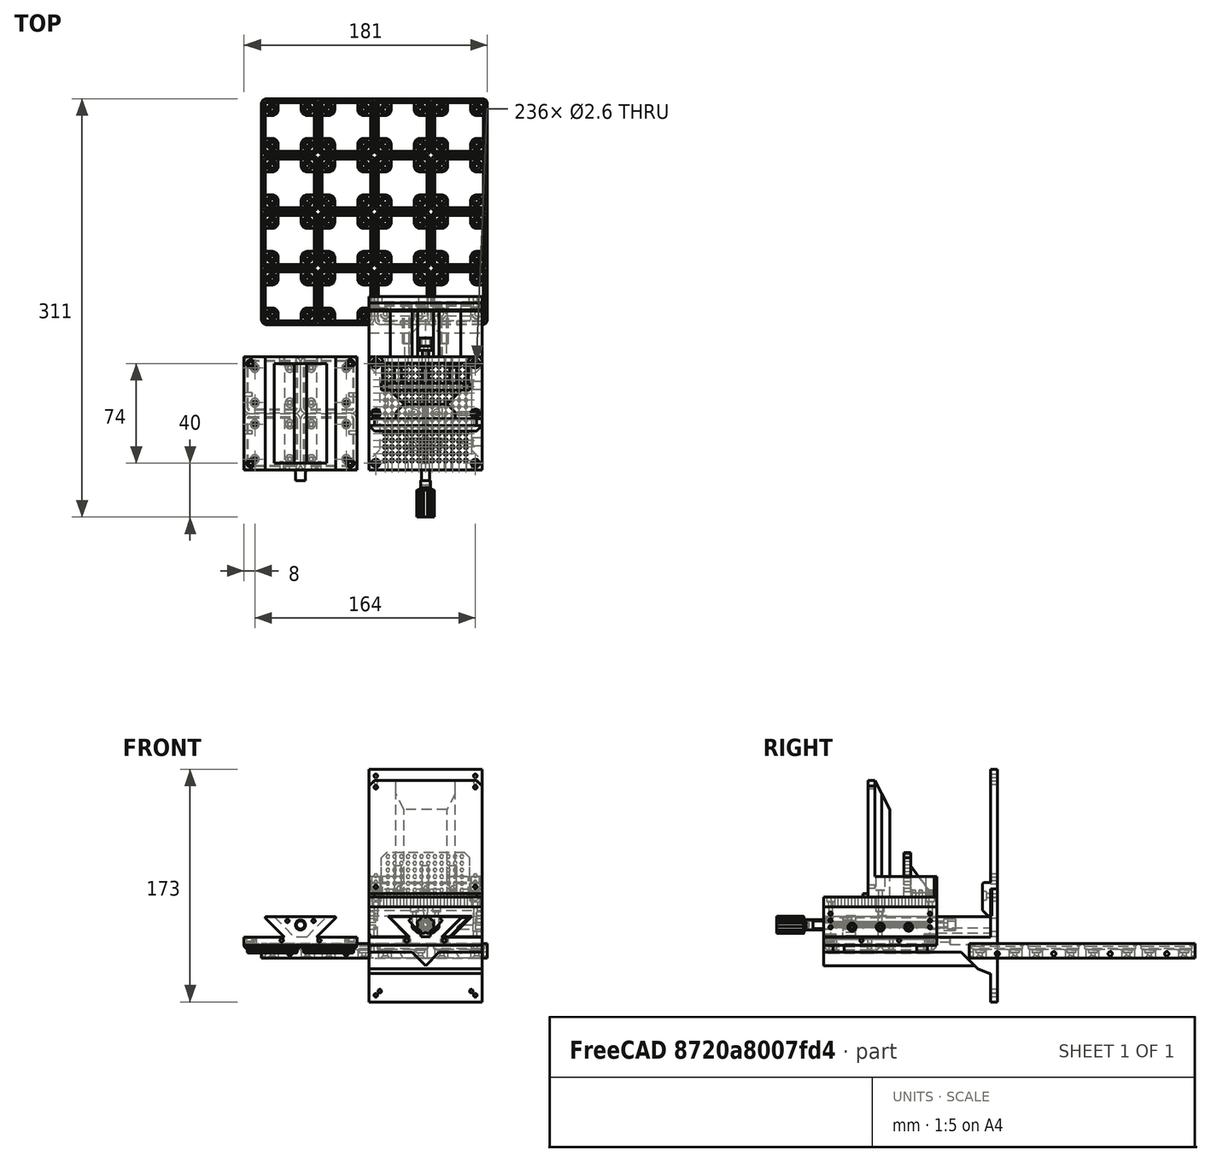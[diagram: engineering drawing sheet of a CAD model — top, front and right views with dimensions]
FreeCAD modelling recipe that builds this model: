
FCSTD DOCUMENT  (FreeCAD 1.0R39109 (Git))
Label: Linear Stage Z Version
License: All rights reserved
LicenseURL: https://en.wikipedia.org/wiki/All_rights_reserved
objects: Sketcher::SketchObject×94, PartDesign::Pocket×53, PartDesign::Pad×46, PartDesign::Chamfer×30, PartDesign::Plane×17, PartDesign::ShapeBinder×15, PartDesign::Body×15, PartDesign::Fillet×6, PartDesign::SubShapeBinder×5, PartDesign::Hole×3, PartDesign::FeatureBase×3, PartDesign::LinearPattern×2, PartDesign::Point×1, Part::Part2DObjectPython×1, Part::Helix×1, PartDesign::AdditivePipe×1, Part::FeaturePython×1, App::VarSet×1, PartDesign::FeaturePython×1
note: 673 computed .brp shape members not serialized (recipe doc carries the construction recipe); baked Part::Feature solids carry a one-line shape summary decoded from their .brp

FEATURE [Sketcher::SketchObject] Sketch
  ArcFitTolerance = 1e-06
  AttachmentSupport = -> [XZ_Plane]
  FullyConstrained = true
  MakeInternals = false
  MapMode = 5
  Placement = pos=(0,0,0) rot=(1,0,0;1.5708rad)
  sketch-geometry (8):
    g0: LineSegment StartX=0 StartY=0 StartZ=0 EndX=84 EndY=0 EndZ=0
    g1: LineSegment StartX=0 StartY=0 StartZ=0 EndX=0 EndY=5 EndZ=0
    g2: LineSegment StartX=84 StartY=0 StartZ=0 EndX=84 EndY=5 EndZ=0
    g3: LineSegment StartX=0 StartY=5 StartZ=0 EndX=30 EndY=5 EndZ=0
    g4: LineSegment StartX=84 StartY=5 StartZ=0 EndX=54 EndY=5 EndZ=0
    g5: LineSegment StartX=30 StartY=5 StartZ=0 EndX=15 EndY=20 EndZ=0
    g6: LineSegment StartX=54 StartY=5 StartZ=0 EndX=69 EndY=20 EndZ=0
    g7: LineSegment StartX=15 StartY=20 StartZ=0 EndX=69 EndY=20 EndZ=0
  constraints (24):
    c: Distance(g0) = 84
    c: Distance(g1) = 5
    c: Coincident(g1,g0)
    c: PointOnObject(g1,g-2)
    c: Vertical(g1)
    c: Distance(g2) = 5
    c: Vertical(g2)
    c: Tangent(g0,g-1)
    c: PointOnObject(g2,g0)
    c: PointOnObject(g0,g2)
    c: Coincident(g3,g1)
    c: Horizontal(g3)
    c: Coincident(g4,g2)
    c: Horizontal(g4)
    c: DistanceX(g3,g3) = 30
    c: DistanceX(g4,g4) = 30
    c: Angle(g-1,g5) = 2.35619
    c: Coincident(g5,g3)
    c: Angle(g-1,g6) = 0.785398
    c: Coincident(g6,g4)
    c: DistanceY(g-1,g5) = 20
    c: DistanceY(g-1,g6) = 20
    c: Coincident(g7,g5)
    c: Coincident(g7,g6)
FEATURE [PartDesign::Pad] Pad
  Direction = (0,-1,2e-16)
  Length = 5
  Length2 = 10
  Placement = pos=(0,0,0) rot=(1,0,0;1.5708rad)
  Profile = -> Sketch
  ReferenceAxis = -> Sketch [N_Axis]
  Refine = true
  Suppressed = false
  Type = 0
FEATURE [Sketcher::SketchObject] Sketch001
  ArcFitTolerance = 1e-06
  AttachmentSupport = -> [Pad]
  ExternalGeometry = -> [Pad]
  FullyConstrained = true
  MakeInternals = false
  MapMode = 5
  Placement = pos=(0,-5,0) rot=(1,0,0;1.5708rad)
  sketch-geometry (14):
    g0: LineSegment StartX=15 StartY=20 StartZ=0 EndX=22.5 EndY=20 EndZ=0
    g1: LineSegment [constr] StartX=30 StartY=5 StartZ=0 EndX=37.5 EndY=5 EndZ=0
    g2: LineSegment StartX=22.5 StartY=20 StartZ=0 EndX=37.5 EndY=5 EndZ=0
    g3: LineSegment StartX=69 StartY=20 StartZ=0 EndX=61.5 EndY=20 EndZ=0
    g4: LineSegment [constr] StartX=54 StartY=5 StartZ=0 EndX=46.5 EndY=5 EndZ=0
    g5: LineSegment StartX=46.5 StartY=5 StartZ=0 EndX=61.5 EndY=20 EndZ=0
    g6: LineSegment StartX=46.5 StartY=5 StartZ=0 EndX=37.5 EndY=5 EndZ=0
    g7: LineSegment StartX=15 StartY=20 StartZ=0 EndX=30 EndY=5 EndZ=0
    g8: LineSegment StartX=30 StartY=5 StartZ=0 EndX=0 EndY=5 EndZ=0
    g9: LineSegment StartX=0 StartY=5 StartZ=0 EndX=0 EndY=0 EndZ=0
    g10: LineSegment StartX=0 StartY=0 StartZ=0 EndX=84 EndY=0 EndZ=0
    g11: LineSegment StartX=84 StartY=0 StartZ=0 EndX=84 EndY=5 EndZ=0
    g12: LineSegment StartX=84 StartY=5 StartZ=0 EndX=54 EndY=5 EndZ=0
    g13: LineSegment StartX=54 StartY=5 StartZ=0 EndX=69 EndY=20 EndZ=0
  constraints (32):
    c: Distance(g0) = 7.5
    c: Coincident(g0,g-4)
    c: PointOnObject(g0,g-3)
    c: Distance(g1) = 7.5
    c: Coincident(g1,g-5)
    c: Horizontal(g1)
    c: Coincident(g2,g0)
    c: Coincident(g2,g1)
    c: Distance(g3) = 7.5
    c: Coincident(g3,g-3)
    c: PointOnObject(g3,g-3)
    c: Distance(g4) = 7.5
    c: Coincident(g4,g-6)
    c: Horizontal(g4)
    c: Coincident(g5,g4)
    c: Coincident(g5,g3)
    c: Coincident(g6,g4)
    c: Coincident(g6,g1)
    c: Coincident(g7,g0)
    c: Coincident(g7,g1)
    c: Coincident(g8,g1)
    c: Coincident(g8,g-8)
    c: Coincident(g9,g8)
    c: Coincident(g9,g-1)
    c: Coincident(g10,g9)
    c: Coincident(g10,g-9)
    c: Coincident(g11,g10)
    c: Coincident(g11,g-7)
    c: Coincident(g12,g11)
    c: Coincident(g12,g4)
    c: Coincident(g13,g4)
    c: Coincident(g13,g3)
FEATURE [PartDesign::Pad] Pad001
  BaseFeature = -> Pad
  Direction = (0,-1,2e-16)
  Length = 74
  Length2 = 10
  Placement = pos=(0,0,0) rot=(1,0,0;1.5708rad)
  Profile = -> Sketch001
  ReferenceAxis = -> Sketch001 [N_Axis]
  Refine = true
  Suppressed = false
  Type = 0
FEATURE [Sketcher::SketchObject] Sketch002
  ArcFitTolerance = 1e-06
  AttachmentSupport = -> [Pad001]
  ExternalGeometry = -> [Pad001]
  FullyConstrained = true
  MakeInternals = false
  MapMode = 5
  Placement = pos=(0,-5,0) rot=(1,0,0;1.5708rad)
  sketch-geometry (2):
    g0: LineSegment [constr] StartX=42 StartY=20 StartZ=0 EndX=42 EndY=14 EndZ=0
    g1: Circle CenterX=42 CenterY=14 CenterZ=0 NormalX=0 NormalY=0 NormalZ=1 AngleXU=0 Radius=3
  constraints (5):
    c: Distance(g0) = 6
    c: Symmetric(g-3,g-3,g0)
    c: Vertical(g0)
    c: Diameter(g1) = 6
    c: Coincident(g1,g0)
FEATURE [PartDesign::Hole] Hole
  BaseFeature = -> Pad001
  CustomThreadClearance = 0
  Depth = 25
  DepthType = 0
  Diameter = 6
  DrillForDepth = false
  DrillPoint = 1
  DrillPointAngle = 118
  HoleCutCountersinkAngle = 90
  HoleCutCustomValues = false
  HoleCutDepth = 0
  HoleCutDiameter = 6.1
  HoleCutType = 0
  ModelThread = false
  Placement = pos=(0,0,0) rot=(1,0,0;1.5708rad)
  Profile = -> Sketch002
  Refine = true
  Suppressed = false
  Tapered = false
  TaperedAngle = 90
  ThreadClass = 0
  ThreadDepth = 25
  ThreadDepthType = 0
  ThreadDirection = 0
  ThreadFit = 0
  ThreadSize = 0
  ThreadType = 0
  Threaded = false
  UseCustomThreadClearance = false
FEATURE [Sketcher::SketchObject] Sketch003
  ArcFitTolerance = 1e-06
  AttachmentSupport = -> [Hole]
  ExternalGeometry = -> [Hole]
  FullyConstrained = true
  MakeInternals = false
  MapMode = 5
  Placement = pos=(0,-79,1.74e-14) rot=(1,0,0;1.5708rad)
  sketch-geometry (16):
    g0: LineSegment StartX=15 StartY=20 StartZ=0 EndX=69 EndY=20 EndZ=0
    g1: LineSegment StartX=15 StartY=20 StartZ=0 EndX=30 EndY=5 EndZ=0
    g2: LineSegment StartX=30 StartY=5 StartZ=0 EndX=0 EndY=5 EndZ=0
    g3: LineSegment StartX=0 StartY=5 StartZ=0 EndX=0 EndY=0 EndZ=0
    g4: LineSegment StartX=0 StartY=0 StartZ=0 EndX=84 EndY=0 EndZ=0
    g5: LineSegment StartX=84 StartY=0 StartZ=0 EndX=84 EndY=5 EndZ=0
    g6: LineSegment StartX=84 StartY=5 StartZ=0 EndX=54 EndY=5 EndZ=0
    g7: LineSegment StartX=54 StartY=5 StartZ=0 EndX=69 EndY=20 EndZ=0
    g8: LineSegment [constr] StartX=42 StartY=20 StartZ=0 EndX=42 EndY=14 EndZ=0
    g9: Circle CenterX=42 CenterY=14 CenterZ=0 NormalX=0 NormalY=0 NormalZ=1 AngleXU=0 Radius=3
    g10: LineSegment [constr] StartX=42 StartY=14 StartZ=0 EndX=22.5 EndY=20 EndZ=0
    g11: LineSegment [constr] StartX=42 StartY=14 StartZ=0 EndX=61.5 EndY=20 EndZ=0
    g12: GeomPoint [constr] X=32.25 Y=17 Z=0
    g13: GeomPoint [constr] X=51.75 Y=17 Z=0
    g14: Circle CenterX=32.25 CenterY=17 CenterZ=0 NormalX=0 NormalY=0 NormalZ=1 AngleXU=0 Radius=1.25
    g15: Circle CenterX=51.75 CenterY=17 CenterZ=0 NormalX=0 NormalY=0 NormalZ=1 AngleXU=0 Radius=1.25
  constraints (31):
    c: Coincident(g0,g-4)
    c: Coincident(g0,g-11)
    c: Coincident(g1,g0)
    c: Coincident(g1,g-5)
    c: Coincident(g2,g1)
    c: Coincident(g2,g-6)
    c: Coincident(g3,g2)
    c: Coincident(g3,g-1)
    c: Coincident(g4,g3)
    c: Coincident(g4,g-8)
    c: Coincident(g5,g4)
    c: Coincident(g5,g-9)
    c: Coincident(g6,g5)
    c: Coincident(g6,g-10)
    c: Coincident(g7,g6)
    c: Coincident(g7,g0)
    c: Distance(g8) = 6
    c: Symmetric(g0,g0,g8)
    c: Vertical(g8)
    c: Diameter(g9) = 6
    c: Coincident(g9,g8)
    c: Coincident(g10,g8)
    c: Coincident(g10,g-14)
    c: Coincident(g11,g8)
    c: Coincident(g11,g-12)
    c: Symmetric(g10,g10,g12)
    c: Symmetric(g11,g11,g13)
    c: Diameter(g14) = 2.5
    c: Coincident(g14,g12)
    c: Diameter(g15) = 2.5
    c: Coincident(g15,g13)
FEATURE [PartDesign::Pad] Pad002
  BaseFeature = -> Hole
  Direction = (0,-1,2e-16)
  Length = 5
  Length2 = 10
  Placement = pos=(0,0,0) rot=(1,0,0;1.5708rad)
  Profile = -> Sketch003
  ReferenceAxis = -> Sketch003 [N_Axis]
  Refine = true
  Suppressed = false
  Type = 0
FEATURE [PartDesign::Plane] DatumPlane
  AttachmentSupport = -> [Pad002]
  Length = 131.586
  MapMode = 5
  Placement = pos=(0,0,-5e-16) rot=(1,0,0;3.14159rad)
  ResizeMode = 0
  Width = 139.586
FEATURE [Sketcher::SketchObject] Sketch004
  ArcFitTolerance = 1e-06
  AttachmentSupport = -> [Pad002]
  ExternalGeometry = -> [Pad002]
  FullyConstrained = true
  MakeInternals = false
  MapMode = 5
  Placement = pos=(0,0,-5e-16) rot=(1,0,0;3.14159rad)
  sketch-geometry (23):
    g0: LineSegment [constr] StartX=0 StartY=84 StartZ=0 EndX=84 EndY=0 EndZ=0
    g1: LineSegment [constr] StartX=41.75 StartY=41.75 StartZ=0 EndX=42.25 EndY=41.75 EndZ=0
    g2: LineSegment [constr] StartX=42.25 StartY=41.75 StartZ=0 EndX=42.25 EndY=42.25 EndZ=0
    g3: LineSegment [constr] StartX=42.25 StartY=42.25 StartZ=0 EndX=41.75 EndY=42.25 EndZ=0
    g4: LineSegment [constr] StartX=41.75 StartY=42.25 StartZ=0 EndX=41.75 EndY=41.75 EndZ=0
    g5: GeomPoint [constr] X=42 Y=42 Z=0
    g6: LineSegment [constr] StartX=0 StartY=0 StartZ=0 EndX=84 EndY=84 EndZ=0
    g7: LineSegment StartX=42.25 StartY=42.25 StartZ=0 EndX=83.75 EndY=42.25 EndZ=0
    g8: LineSegment StartX=83.75 StartY=42.25 StartZ=0 EndX=83.75 EndY=83.75 EndZ=0
    g9: LineSegment StartX=83.75 StartY=83.75 StartZ=0 EndX=42.25 EndY=83.75 EndZ=0
    g10: LineSegment StartX=42.25 StartY=83.75 StartZ=0 EndX=42.25 EndY=42.25 EndZ=0
    g11: LineSegment StartX=41.75 StartY=42.25 StartZ=0 EndX=41.75 EndY=83.75 EndZ=0
    g12: LineSegment StartX=41.75 StartY=83.75 StartZ=0 EndX=0.25 EndY=83.75 EndZ=0
    g13: LineSegment StartX=0.25 StartY=83.75 StartZ=0 EndX=0.25 EndY=42.25 EndZ=0
    g14: LineSegment StartX=0.25 StartY=42.25 StartZ=0 EndX=41.75 EndY=42.25 EndZ=0
    g15: LineSegment StartX=42.25 StartY=41.75 StartZ=0 EndX=42.25 EndY=0.25 EndZ=0
    g16: LineSegment StartX=42.25 StartY=0.25 StartZ=0 EndX=83.75 EndY=0.25 EndZ=0
    g17: LineSegment StartX=83.75 StartY=0.25 StartZ=0 EndX=83.75 EndY=41.75 EndZ=0
    g18: LineSegment StartX=83.75 StartY=41.75 StartZ=0 EndX=42.25 EndY=41.75 EndZ=0
    g19: LineSegment StartX=41.75 StartY=41.75 StartZ=0 EndX=0.25 EndY=41.75 EndZ=0
    g20: LineSegment StartX=0.25 StartY=41.75 StartZ=0 EndX=0.25 EndY=0.25 EndZ=0
    g21: LineSegment StartX=0.25 StartY=0.25 StartZ=0 EndX=41.75 EndY=0.25 EndZ=0
    g22: LineSegment StartX=41.75 StartY=0.25 StartZ=0 EndX=41.75 EndY=41.75 EndZ=0
  constraints (61):
    c: Coincident(g0,g-6)
    c: Coincident(g0,g-5)
    c: Coincident(g1,g2)
    c: Coincident(g2,g3)
    c: Coincident(g3,g4)
    c: Coincident(g4,g1)
    c: Horizontal(g1)
    c: Horizontal(g3)
    c: Vertical(g2)
    c: Vertical(g4)
    c: Symmetric(g3,g1,g5)
    c: Distance(g2,g4) = 0.5
    c: Distance(g1,g3) = 0.5
    c: PointOnObject(g5,g0)
    c: Coincident(g6,g-1)
    c: Coincident(g6,g-4)
    c: PointOnObject(g5,g6)
    c: Coincident(g7,g8)
    c: Coincident(g8,g9)
    c: Coincident(g9,g10)
    c: Coincident(g10,g7)
    c: Horizontal(g7)
    c: Horizontal(g9)
    c: Vertical(g8)
    c: Vertical(g10)
    c: Distance(g8,g10) = 41.5
    c: Coincident(g7,g2)
    c: PointOnObject(g8,g6)
    c: Coincident(g11,g12)
    c: Coincident(g12,g13)
    c: Coincident(g13,g14)
    c: Coincident(g14,g11)
    c: Vertical(g11)
    c: Vertical(g13)
    c: Horizontal(g12)
    c: Horizontal(g14)
    c: Distance(g11,g13) = 41.5
    c: Coincident(g11,g3)
    c: PointOnObject(g12,g0)
    c: Coincident(g15,g16)
    c: Coincident(g16,g17)
    c: Coincident(g17,g18)
    c: Coincident(g18,g15)
    c: Vertical(g15)
    c: Vertical(g17)
    c: Horizontal(g16)
    c: Horizontal(g18)
    c: Distance(g15,g17) = 41.5
    c: Coincident(g15,g1)
    c: PointOnObject(g16,g0)
    c: Coincident(g19,g20)
    c: Coincident(g20,g21)
    c: Coincident(g21,g22)
    c: Coincident(g22,g19)
    c: Horizontal(g19)
    c: Horizontal(g21)
    c: Vertical(g20)
    c: Vertical(g22)
    c: Distance(g20,g22) = 41.5
    c: Coincident(g19,g1)
    c: PointOnObject(g20,g6)
FEATURE [PartDesign::Pad] Pad003
  BaseFeature = -> Pad002
  Direction = (0,0,-1)
  Length = 1
  Length2 = 10
  Placement = pos=(0,0,0) rot=(1,0,0;1.5708rad)
  Profile = -> Sketch004
  ReferenceAxis = -> Sketch004 [N_Axis]
  Refine = true
  Suppressed = false
  Type = 0
FEATURE [PartDesign::Plane] DatumPlane001
  AttachmentSupport = -> [Pad003]
  Length = 131.586
  MapMode = 5
  Placement = pos=(0,0,-1) rot=(1,0,0;3.14159rad)
  ResizeMode = 0
  Width = 139.586
FEATURE [Sketcher::SketchObject] Sketch005
  ArcFitTolerance = 1e-06
  AttachmentSupport = -> [DatumPlane001]
  ExternalGeometry = -> [Pad003]
  FullyConstrained = true
  MakeInternals = false
  MapMode = 5
  Placement = pos=(0,0,-1) rot=(1,0,0;3.14159rad)
  sketch-geometry (28):
    g0: LineSegment [constr] StartX=41.75 StartY=42.25 StartZ=0 EndX=0.25 EndY=83.75 EndZ=0
    g1: GeomPoint [constr] X=21 Y=63 Z=0
    g2: LineSegment StartX=2.4 StartY=44.4 StartZ=0 EndX=39.6 EndY=44.4 EndZ=0
    g3: LineSegment StartX=39.6 StartY=44.4 StartZ=0 EndX=39.6 EndY=81.6 EndZ=0
    g4: LineSegment StartX=39.6 StartY=81.6 StartZ=0 EndX=2.4 EndY=81.6 EndZ=0
    g5: LineSegment StartX=2.4 StartY=81.6 StartZ=0 EndX=2.4 EndY=44.4 EndZ=0
    g6: GeomPoint [constr] X=21 Y=63 Z=0
    g7: LineSegment [constr] StartX=42.25 StartY=83.75 StartZ=0 EndX=83.75 EndY=42.25 EndZ=0
    g8: LineSegment [constr] StartX=83.75 StartY=41.75 StartZ=0 EndX=42.25 EndY=0.25 EndZ=0
    g9: LineSegment [constr] StartX=41.75 StartY=0.25 StartZ=0 EndX=0.25 EndY=41.75 EndZ=0
    g10: GeomPoint [constr] X=63 Y=63 Z=0
    g11: GeomPoint [constr] X=63 Y=21 Z=0
    g12: GeomPoint [constr] X=21 Y=21 Z=0
    g13: LineSegment StartX=44.4 StartY=44.4 StartZ=0 EndX=81.6 EndY=44.4 EndZ=0
    g14: LineSegment StartX=81.6 StartY=44.4 StartZ=0 EndX=81.6 EndY=81.6 EndZ=0
    g15: LineSegment StartX=81.6 StartY=81.6 StartZ=0 EndX=44.4 EndY=81.6 EndZ=0
    g16: LineSegment StartX=44.4 StartY=81.6 StartZ=0 EndX=44.4 EndY=44.4 EndZ=0
    g17: GeomPoint [constr] X=63 Y=63 Z=0
    g18: LineSegment StartX=44.4 StartY=2.4 StartZ=0 EndX=81.6 EndY=2.4 EndZ=0
    g19: LineSegment StartX=81.6 StartY=2.4 StartZ=0 EndX=81.6 EndY=39.6 EndZ=0
    g20: LineSegment StartX=81.6 StartY=39.6 StartZ=0 EndX=44.4 EndY=39.6 EndZ=0
    g21: LineSegment StartX=44.4 StartY=39.6 StartZ=0 EndX=44.4 EndY=2.4 EndZ=0
    g22: GeomPoint [constr] X=63 Y=21 Z=0
    g23: LineSegment StartX=2.4 StartY=2.4 StartZ=0 EndX=39.6 EndY=2.4 EndZ=0
    g24: LineSegment StartX=39.6 StartY=2.4 StartZ=0 EndX=39.6 EndY=39.6 EndZ=0
    g25: LineSegment StartX=39.6 StartY=39.6 StartZ=0 EndX=2.4 EndY=39.6 EndZ=0
    g26: LineSegment StartX=2.4 StartY=39.6 StartZ=0 EndX=2.4 EndY=2.4 EndZ=0
    g27: GeomPoint [constr] X=21 Y=21 Z=0
  constraints (60):
    c: Coincident(g0,g-14)
    c: Coincident(g0,g-16)
    c: Symmetric(g0,g0,g1)
    c: Coincident(g2,g3)
    c: Coincident(g3,g4)
    c: Coincident(g4,g5)
    c: Coincident(g5,g2)
    c: Horizontal(g2)
    c: Horizontal(g4)
    c: Vertical(g3)
    c: Vertical(g5)
    c: Symmetric(g4,g2,g6)
    c: Distance(g3,g5) = 37.2
    c: Distance(g2,g4) = 37.2
    c: Coincident(g6,g1)
    c: Coincident(g7,g-18)
    c: Coincident(g7,g-17)
    c: Coincident(g8,g-9)
    c: Coincident(g8,g-10)
    c: Coincident(g9,g-4)
    c: Coincident(g9,g-6)
    c: Symmetric(g7,g7,g10)
    c: Symmetric(g8,g8,g11)
    c: Symmetric(g9,g9,g12)
    c: Coincident(g13,g14)
    c: Coincident(g14,g15)
    c: Coincident(g15,g16)
    c: Coincident(g16,g13)
    c: Horizontal(g13)
    c: Horizontal(g15)
    c: Vertical(g14)
    c: Vertical(g16)
    c: Symmetric(g15,g13,g17)
    c: Distance(g14,g16) = 37.2
    c: Distance(g13,g15) = 37.2
    c: Coincident(g17,g10)
    c: Coincident(g18,g19)
    c: Coincident(g19,g20)
    c: Coincident(g20,g21)
    c: Coincident(g21,g18)
    c: Horizontal(g18)
    c: Horizontal(g20)
    c: Vertical(g19)
    c: Vertical(g21)
    c: Symmetric(g20,g18,g22)
    c: Distance(g19,g21) = 37.2
    c: Coincident(g22,g11)
    c: PointOnObject(g19,g8)
    c: Coincident(g23,g24)
    c: Coincident(g24,g25)
    c: Coincident(g25,g26)
    c: Coincident(g26,g23)
    c: Horizontal(g23)
    c: Horizontal(g25)
    c: Vertical(g24)
    c: Vertical(g26)
    c: Symmetric(g25,g23,g27)
    c: Distance(g24,g26) = 37.2
    c: Distance(g23,g25) = 37.2
    c: Coincident(g27,g12)
FEATURE [PartDesign::Pad] Pad004
  BaseFeature = -> Pad003
  Direction = (0,0,-1)
  Length = 3.5
  Length2 = 10
  Placement = pos=(0,0,0) rot=(1,0,0;1.5708rad)
  Profile = -> Sketch005
  ReferenceAxis = -> Sketch005 [N_Axis]
  Refine = true
  Suppressed = false
  Type = 0
FEATURE [PartDesign::Chamfer] Chamfer
  Angle = 45
  Base = -> Pad004 [Edge114]
  BaseFeature = -> Pad004
  ChamferType = 0
  FlipDirection = false
  Placement = pos=(0,0,0) rot=(1,0,0;1.5708rad)
  Refine = true
  Size = 7
  Size2 = 1
  SupportTransform = false
  Suppressed = false
  UseAllEdges = false
FEATURE [PartDesign::Chamfer] Chamfer001
  Angle = 45
  Base = -> Chamfer [Edge23]
  BaseFeature = -> Chamfer
  ChamferType = 0
  FlipDirection = false
  Placement = pos=(0,0,0) rot=(1,0,0;1.5708rad)
  Refine = true
  Size = 7
  Size2 = 1
  SupportTransform = false
  Suppressed = false
  UseAllEdges = false
FEATURE [PartDesign::Chamfer] Chamfer002
  Angle = 45
  Base = -> Chamfer001 [Edge136,Edge28,Edge143,Edge22,Edge135,Edge128,Edge144,Edge148,Edge140,Edge127,Edge132,Edge138,Edge26,Edge130]
  BaseFeature = -> Chamfer001
  ChamferType = 0
  FlipDirection = false
  Placement = pos=(0,0,0) rot=(1,0,0;1.5708rad)
  Refine = true
  Size = 7
  Size2 = 1
  SupportTransform = false
  Suppressed = false
  UseAllEdges = false
FEATURE [PartDesign::Chamfer] Chamfer003
  Angle = 45
  Base = -> Chamfer002 [Edge77,Edge79,Edge93,Edge81,Edge95,Edge38,Edge76,Edge32,Edge92,Edge84,Edge97,Edge85,Edge87,Edge89,Edge35]
  BaseFeature = -> Chamfer002
  ChamferType = 0
  FlipDirection = false
  Placement = pos=(0,0,0) rot=(1,0,0;1.5708rad)
  Refine = true
  Size = 8
  Size2 = 1
  SupportTransform = false
  Suppressed = false
  UseAllEdges = false
FEATURE [PartDesign::Chamfer] Chamfer004
  Angle = 45
  Base = -> Chamfer003 [Edge231]
  BaseFeature = -> Chamfer003
  ChamferType = 0
  FlipDirection = false
  Placement = pos=(0,0,0) rot=(1,0,0;1.5708rad)
  Refine = true
  Size = 7
  Size2 = 1
  SupportTransform = false
  Suppressed = false
  UseAllEdges = false
FEATURE [PartDesign::Chamfer] Chamfer005
  Angle = 45
  Base = -> Chamfer004 [Edge1,Edge2,Edge4,Edge6,Edge8,Edge7,Edge5,Edge3]
  BaseFeature = -> Chamfer004
  ChamferType = 0
  FlipDirection = false
  Placement = pos=(0,0,0) rot=(1,0,0;1.5708rad)
  Refine = true
  Size = 2
  Size2 = 1
  SupportTransform = false
  Suppressed = false
  UseAllEdges = false
FEATURE [PartDesign::Chamfer] Chamfer006
  Angle = 45
  Base = -> Chamfer005 [Edge60,Edge64,Edge62,Edge58,Edge55,Edge50,Edge52,Edge56]
  BaseFeature = -> Chamfer005
  ChamferType = 0
  FlipDirection = false
  Placement = pos=(0,0,0) rot=(1,0,0;1.5708rad)
  Refine = true
  Size = 0.8
  Size2 = 1
  SupportTransform = false
  Suppressed = false
  UseAllEdges = false
FEATURE [PartDesign::Chamfer] Chamfer007
  Angle = 45
  Base = -> Chamfer006 [Edge207,Edge208,Edge205,Edge206,Edge204,Edge202,Edge203,Edge201]
  BaseFeature = -> Chamfer006
  ChamferType = 0
  FlipDirection = false
  Placement = pos=(0,0,0) rot=(1,0,0;1.5708rad)
  Refine = true
  Size = 2
  Size2 = 1
  SupportTransform = false
  Suppressed = false
  UseAllEdges = false
FEATURE [PartDesign::Chamfer] Chamfer008
  Angle = 45
  Base = -> Chamfer007 [Edge63,Edge64,Edge60,Edge57,Edge52,Edge50,Edge55,Edge59]
  BaseFeature = -> Chamfer007
  ChamferType = 0
  FlipDirection = false
  Placement = pos=(0,0,0) rot=(1,0,0;1.5708rad)
  Refine = true
  Size = 0.8
  Size2 = 1
  SupportTransform = false
  Suppressed = false
  UseAllEdges = false
FEATURE [PartDesign::Chamfer] Chamfer009
  Angle = 45
  Base = -> Chamfer008 [Edge179,Edge177,Edge178,Edge181,Edge180,Edge182,Edge184,Edge183]
  BaseFeature = -> Chamfer008
  ChamferType = 0
  FlipDirection = false
  Placement = pos=(0,0,0) rot=(1,0,0;1.5708rad)
  Refine = true
  Size = 2
  Size2 = 1
  SupportTransform = false
  Suppressed = false
  UseAllEdges = false
FEATURE [PartDesign::Chamfer] Chamfer010
  Angle = 45
  Base = -> Chamfer009 [Edge55,Edge58,Edge62,Edge64,Edge61,Edge56,Edge53,Edge50]
  BaseFeature = -> Chamfer009
  ChamferType = 0
  FlipDirection = false
  Placement = pos=(0,0,0) rot=(1,0,0;1.5708rad)
  Refine = true
  Size = 0.8
  Size2 = 1
  SupportTransform = false
  Suppressed = false
  UseAllEdges = false
FEATURE [PartDesign::Chamfer] Chamfer011
  Angle = 45
  Base = -> Chamfer010 [Edge203,Edge205,Edge201,Edge202,Edge204,Edge206,Edge208,Edge207]
  BaseFeature = -> Chamfer010
  ChamferType = 0
  FlipDirection = false
  Placement = pos=(0,0,0) rot=(1,0,0;1.5708rad)
  Refine = true
  Size = 2
  Size2 = 1
  SupportTransform = false
  Suppressed = false
  UseAllEdges = false
FEATURE [PartDesign::Chamfer] Chamfer012
  Angle = 45
  Base = -> Chamfer011 [Edge62,Edge59,Edge54,Edge50,Edge53,Edge56,Edge61,Edge64]
  BaseFeature = -> Chamfer011
  ChamferType = 0
  FlipDirection = false
  Placement = pos=(0,0,0) rot=(1,0,0;1.5708rad)
  Refine = true
  Size = 0.8
  Size2 = 1
  SupportTransform = false
  Suppressed = false
  UseAllEdges = false
FEATURE [PartDesign::Fillet] Fillet
  Base = -> Chamfer012 [Edge188,Edge187]
  BaseFeature = -> Chamfer012
  Placement = pos=(0,0,0) rot=(1,0,0;1.5708rad)
  Radius = 0.5
  Refine = true
  SupportTransform = false
  Suppressed = false
  UseAllEdges = false
FEATURE [PartDesign::ShapeBinder] ShapeBinder
  Support = -> [Fillet]
  TraceSupport = false
FEATURE [PartDesign::ShapeBinder] CopyFillet
  Placement = pos=(0,-5,2e-15) rot=(0,0,1;0rad)
  TraceSupport = false
FEATURE [PartDesign::Plane] DatumPlane002
  AttachmentSupport = -> [CopyFillet]
  Length = 111.71
  MapMode = 5
  Placement = pos=(0,-84,2e-15) rot=(1,0,0;1.5708rad)
  ResizeMode = 0
  Width = 63.9806
FEATURE [Sketcher::SketchObject] Sketch006
  ArcFitTolerance = 1e-06
  AttachmentSupport = -> [DatumPlane002]
  ExternalGeometry = -> [ShapeBinder]
  FullyConstrained = true
  MakeInternals = false
  MapMode = 5
  Placement = pos=(0,-84,2e-15) rot=(1,0,0;1.5708rad)
  sketch-geometry (16):
    g0: LineSegment [constr] StartX=68.1465 StartY=19.1464 StartZ=0 EndX=69 EndY=20 EndZ=0
    g1: LineSegment [constr] StartX=67.7929 StartY=20 StartZ=0 EndX=69 EndY=20 EndZ=0
    g2: LineSegment [constr] StartX=69 StartY=20 StartZ=0 EndX=69.5 EndY=20 EndZ=0
    g3: LineSegment [constr] StartX=69.5 StartY=20 StartZ=0 EndX=74.5 EndY=20 EndZ=0
    g4: LineSegment [constr] StartX=54 StartY=5 StartZ=0 EndX=54.5 EndY=5 EndZ=0
    g5: LineSegment [constr] StartX=54.5 StartY=5 StartZ=0 EndX=59.5 EndY=5 EndZ=0
    g6: LineSegment [constr] StartX=59.5 StartY=5 StartZ=0 EndX=74.5 EndY=20 EndZ=0
    g7: LineSegment [constr] StartX=54.5 StartY=5 StartZ=0 EndX=69.5 EndY=20 EndZ=0
    g8: LineSegment [constr] StartX=59.5 StartY=5 StartZ=0 EndX=59.8536 EndY=5.35355 EndZ=0
    g9: LineSegment [constr] StartX=54.5 StartY=5 StartZ=0 EndX=54.8536 EndY=5.35355 EndZ=0
    g10: LineSegment [constr] StartX=74.5 StartY=20 StartZ=0 EndX=74.1465 EndY=19.6464 EndZ=0
    g11: LineSegment [constr] StartX=69.5 StartY=20 StartZ=0 EndX=69.1465 EndY=19.6464 EndZ=0
    g12: LineSegment StartX=54.8536 StartY=5.35355 StartZ=0 EndX=59.8536 EndY=5.35355 EndZ=0
    g13: LineSegment StartX=59.8536 StartY=5.35355 StartZ=0 EndX=74.1465 EndY=19.6464 EndZ=0
    g14: LineSegment StartX=74.1465 StartY=19.6464 StartZ=0 EndX=69.1465 EndY=19.6464 EndZ=0
    g15: LineSegment StartX=69.1465 StartY=19.6464 StartZ=0 EndX=54.8536 EndY=5.35355 EndZ=0
  constraints (41):
    c: Coincident(g0,g-3)
    c: Coincident(g1,g-4)
    c: Coincident(g1,g0)
    c: Angle(g-4,g1) = 3.14159
    c: Angle(g-3,g0) = 3.14159
    c: Distance(g2) = 0.5
    c: Coincident(g2,g0)
    c: Horizontal(g2)
    c: Distance(g3) = 5
    c: Coincident(g3,g2)
    c: Horizontal(g3)
    c: Distance(g4) = 0.5
    c: Coincident(g4,g-3)
    c: Horizontal(g4)
    c: Distance(g5) = 5
    c: Coincident(g5,g4)
    c: Horizontal(g5)
    c: Coincident(g6,g5)
    c: Coincident(g6,g3)
    c: Coincident(g7,g4)
    c: Coincident(g7,g2)
    c: Distance(g8) = 0.5
    c: Coincident(g8,g5)
    c: PointOnObject(g8,g6)
    c: Distance(g9) = 0.5
    c: Coincident(g9,g4)
    c: PointOnObject(g9,g7)
    c: Distance(g10) = 0.5
    c: Coincident(g10,g3)
    c: PointOnObject(g10,g6)
    c: Distance(g11) = 0.5
    c: Coincident(g11,g2)
    c: PointOnObject(g11,g7)
    c: Coincident(g12,g9)
    c: Coincident(g12,g8)
    c: Coincident(g13,g8)
    c: Coincident(g13,g10)
    c: Coincident(g14,g10)
    c: Coincident(g14,g11)
    c: Coincident(g15,g11)
    c: Coincident(g15,g9)
FEATURE [PartDesign::Pad] Pad005
  Direction = (0,-1,2e-16)
  Length = 84
  Length2 = 10
  Placement = pos=(0,-84,2e-15) rot=(1,0,0;1.5708rad)
  Profile = -> Sketch006
  ReferenceAxis = -> Sketch006 [N_Axis]
  Refine = true
  Reversed = true
  Suppressed = false
  Type = 0
FEATURE [PartDesign::Plane] DatumPlane003
  AttachmentSupport = -> [Pad005]
  Length = 125.801
  MapMode = 5
  Placement = pos=(27.25,-84,-27.25) rot=(0.92388,0,0.382683;3.14159rad)
  ResizeMode = 0
  Width = 130.341
FEATURE [Sketcher::SketchObject] Sketch007
  ArcFitTolerance = 1e-06
  AttachmentSupport = -> [DatumPlane003]
  ExternalGeometry = -> [Pad005]
  FullyConstrained = true
  MakeInternals = false
  MapMode = 5
  Placement = pos=(27.25,-84,-27.25) rot=(0.92388,0,0.382683;3.14159rad)
  sketch-geometry (8):
    g0: LineSegment [constr] StartX=46.1084 StartY=-42 StartZ=0 EndX=66.3216 EndY=-42 EndZ=0
    g1: LineSegment [constr] StartX=56.215 StartY=-42 StartZ=0 EndX=56.215 EndY=-1.42e-14 EndZ=0
    g2: LineSegment [constr] StartX=56.215 StartY=-42 StartZ=0 EndX=56.215 EndY=-84 EndZ=0
    g3: GeomPoint [constr] X=56.215 Y=-63 Z=0
    g4: GeomPoint [constr] X=56.215 Y=-21 Z=0
    g5: Circle CenterX=56.215 CenterY=-21 CenterZ=0 NormalX=0 NormalY=0 NormalZ=1 AngleXU=0 Radius=1.55
    g6: Circle CenterX=56.215 CenterY=-42 CenterZ=0 NormalX=0 NormalY=0 NormalZ=1 AngleXU=0 Radius=1.55
    g7: Circle CenterX=56.215 CenterY=-63 CenterZ=0 NormalX=0 NormalY=0 NormalZ=1 AngleXU=0 Radius=1.55
  constraints (14):
    c: Symmetric(g-4,g-4,g0)
    c: Symmetric(g-3,g-3,g0)
    c: Symmetric(g0,g0,g1)
    c: Symmetric(g-5,g-5,g1)
    c: Coincident(g2,g1)
    c: Symmetric(g-6,g-6,g2)
    c: Symmetric(g2,g2,g3)
    c: Symmetric(g1,g1,g4)
    c: Diameter(g5) = 3.1
    c: Coincident(g5,g4)
    c: Diameter(g6) = 3.1
    c: Coincident(g6,g1)
    c: Diameter(g7) = 3.1
    c: Coincident(g7,g3)
FEATURE [PartDesign::Pocket] Pocket
  BaseFeature = -> Pad005
  Direction = (-0.707107,0,0.707107)
  Length = 1
  Length2 = 5
  Placement = pos=(0,-84,2e-15) rot=(1,0,0;1.5708rad)
  Profile = -> Sketch007
  ReferenceAxis = -> Sketch007 [N_Axis]
  Refine = true
  Suppressed = false
  Type = 0
FEATURE [PartDesign::Fillet] Fillet001
  Base = -> Pocket [Edge5,Edge10,Edge1,Edge2]
  BaseFeature = -> Pocket
  Placement = pos=(0,-84,2e-15) rot=(1,0,0;1.5708rad)
  Radius = 1
  Refine = true
  SupportTransform = false
  Suppressed = false
  UseAllEdges = false
FEATURE [PartDesign::Fillet] Fillet002
  Base = -> Fillet001 [Edge24,Edge25,Edge23]
  BaseFeature = -> Fillet001
  Placement = pos=(0,-84,2e-15) rot=(1,0,0;1.5708rad)
  Radius = 0.3
  Refine = true
  SupportTransform = false
  Suppressed = false
  UseAllEdges = false
FEATURE [PartDesign::Fillet] Fillet003
  Base = -> Fillet002 [Edge31,Edge37,Edge39]
  BaseFeature = -> Fillet002
  Placement = pos=(0,-84,2e-15) rot=(1,0,0;1.5708rad)
  Radius = 0.3
  Refine = true
  SupportTransform = false
  Suppressed = false
  UseAllEdges = false
FEATURE [PartDesign::Body] Body001  label="Shim"
  AllowCompound = false
  Group = -> [ShapeBinder,DatumPlane002,CopyFillet,Sketch006,Pad005,DatumPlane003,Sketch007,Pocket,Fillet001,Fillet002,Fillet003]
  Origin = -> Origin001
  Tip = -> Fillet003
FEATURE [PartDesign::ShapeBinder] ShapeBinder001
  Support = -> [Fillet]
  TraceSupport = false
FEATURE [PartDesign::ShapeBinder] CopyFillet001
  Placement = pos=(0,-5,2e-15) rot=(0,0,1;0rad)
  TraceSupport = false
FEATURE [PartDesign::Plane] DatumPlane004
  AttachmentSupport = -> [CopyFillet001]
  Length = 124.108
  MapMode = 5
  Placement = pos=(0,-84,2e-15) rot=(1,0,0;1.5708rad)
  ResizeMode = 0
  Width = 67.4619
FEATURE [Sketcher::SketchObject] Sketch008
  ArcFitTolerance = 1e-06
  AttachmentSupport = -> [DatumPlane004]
  ExternalGeometry = -> [ShapeBinder001]
  FullyConstrained = true
  MakeInternals = false
  MapMode = 5
  Placement = pos=(0,-84,2e-15) rot=(1,0,0;1.5708rad)
  sketch-geometry (21):
    g0: LineSegment [constr] StartX=54 StartY=5 StartZ=0 EndX=61 EndY=5 EndZ=0
    g1: LineSegment [constr] StartX=68.1465 StartY=19.1464 StartZ=0 EndX=69 EndY=20 EndZ=0
    g2: LineSegment [constr] StartX=67.7929 StartY=20 StartZ=0 EndX=69 EndY=20 EndZ=0
    g3: LineSegment [constr] StartX=69 StartY=20 StartZ=0 EndX=76 EndY=20 EndZ=0
    g4: LineSegment [constr] StartX=61 StartY=5 StartZ=0 EndX=61.3536 EndY=5.35355 EndZ=0
    g5: LineSegment [constr] StartX=76 StartY=20 StartZ=0 EndX=76.3536 EndY=20.3536 EndZ=0
    g6: LineSegment StartX=76.3536 StartY=20.3536 StartZ=0 EndX=61.3536 EndY=5.35355 EndZ=0
    g7: LineSegment [constr] StartX=84 StartY=5 StartZ=0 EndX=84 EndY=5.5 EndZ=0
    g8: LineSegment StartX=61.3536 StartY=5.35355 StartZ=0 EndX=84 EndY=5.35355 EndZ=0
    g9: LineSegment StartX=84 StartY=5.35355 StartZ=0 EndX=84 EndY=25.3536 EndZ=0
    g10: LineSegment [constr] StartX=30 StartY=5 StartZ=0 EndX=29.5 EndY=5 EndZ=0
    g11: LineSegment [constr] StartX=16.2071 StartY=20 StartZ=0 EndX=14.5 EndY=20 EndZ=0
    g12: LineSegment [constr] StartX=29.5 StartY=5 StartZ=0 EndX=14.5 EndY=20 EndZ=0
    g13: LineSegment [constr] StartX=14.5 StartY=20 StartZ=0 EndX=14.1465 EndY=20.3536 EndZ=0
    g14: LineSegment [constr] StartX=29.5 StartY=5 StartZ=0 EndX=29.1464 EndY=5.35355 EndZ=0
    g15: LineSegment StartX=29.1464 StartY=5.35355 StartZ=0 EndX=14.1465 EndY=20.3536 EndZ=0
    g16: LineSegment [constr] StartX=0 StartY=5 StartZ=0 EndX=0 EndY=15 EndZ=0
    g17: LineSegment StartX=29.1464 StartY=5.35355 StartZ=0 EndX=0 EndY=5.35355 EndZ=0
    g18: LineSegment StartX=0 StartY=5.35355 StartZ=0 EndX=0 EndY=25.3536 EndZ=0
    g19: LineSegment StartX=0 StartY=25.3536 StartZ=0 EndX=84 EndY=25.3536 EndZ=0
    g20: LineSegment StartX=14.1465 StartY=20.3536 StartZ=0 EndX=76.3536 EndY=20.3536 EndZ=0
  constraints (58):
    c: Distance(g0) = 7
    c: Coincident(g0,g-8)
    c: PointOnObject(g0,g-8)
    c: Coincident(g1,g-7)
    c: Coincident(g2,g-6)
    c: Coincident(g2,g1)
    c: Parallel(g2,g-6)
    c: Parallel(g1,g-7)
    c: Distance(g3) = 7
    c: Coincident(g3,g1)
    c: Parallel(g3,g-6)
    c: Distance(g4) = 0.5
    c: Coincident(g4,g0)
    c: Parallel(g-7,g4)
    c: Distance(g5) = 0.5
    c: Coincident(g5,g3)
    c: Parallel(g5,g1)
    c: Coincident(g6,g5)
    c: Coincident(g6,g4)
    c: Distance(g7) = 0.5
    c: Coincident(g7,g-9)
    c: Vertical(g7)
    c: Coincident(g8,g4)
    c: PointOnObject(g8,g7)
    c: Horizontal(g8)
    c: Distance(g9) = 20
    c: Coincident(g9,g8)
    c: Vertical(g9)
    c: Distance(g10) = 0.5
    c: Coincident(g10,g-5)
    c: PointOnObject(g10,g-3)
    c: Coincident(g11,g-6)
    c: Horizontal(g11)
    c: Coincident(g12,g10)
    c: PointOnObject(g12,g11)
    c: Parallel(g12,g-5)
    c: PointOnObject(g11,g12)
    c: Distance(g13) = 0.5
    c: Coincident(g13,g11)
    c: Parallel(g12,g13)
    c: Distance(g14) = 0.5
    c: Coincident(g14,g10)
    c: PointOnObject(g14,g12)
    c: Coincident(g15,g14)
    c: Coincident(g15,g13)
    c: Distance(g16) = 10
    c: Coincident(g16,g-4)
    c: PointOnObject(g16,g-2)
    c: Coincident(g17,g14)
    c: PointOnObject(g17,g16)
    c: Parallel(g17,g-3)
    c: Distance(g18) = 20
    c: Coincident(g18,g17)
    c: PointOnObject(g18,g-2)
    c: Coincident(g19,g18)
    c: Coincident(g19,g9)
    c: Coincident(g20,g13)
    c: Coincident(g20,g5)
FEATURE [PartDesign::Pad] Pad006
  Direction = (0,-1,2e-16)
  Length = 84
  Length2 = 10
  Placement = pos=(0,-84,2e-15) rot=(1,0,0;1.5708rad)
  Profile = -> Sketch008
  ReferenceAxis = -> Sketch008 [N_Axis]
  Refine = true
  Reversed = true
  Suppressed = false
  Type = 0
FEATURE [Sketcher::SketchObject] Sketch009
  ArcFitTolerance = 1e-06
  AttachmentSupport = -> [Pad006]
  ExternalGeometry = -> [Pad006]
  FullyConstrained = true
  MakeInternals = false
  MapMode = 5
  Placement = pos=(84,-84,2e-15) rot=(0.707107,0,0.707107;3.14159rad)
  sketch-geometry (11):
    g0: GeomPoint [constr] X=25.3536 Y=-42 Z=0
    g1: GeomPoint [constr] X=5.35355 Y=-42 Z=0
    g2: LineSegment [constr] StartX=5.35355 StartY=-42 StartZ=0 EndX=25.3536 EndY=-42 EndZ=0
    g3: LineSegment [constr] StartX=5.35355 StartY=-42 StartZ=0 EndX=12.3536 EndY=-42 EndZ=0
    g4: LineSegment [constr] StartX=12.3536 StartY=-42 StartZ=0 EndX=12.3536 EndY=-7.1e-15 EndZ=0
    g5: LineSegment [constr] StartX=12.3536 StartY=-42 StartZ=0 EndX=12.3536 EndY=-84 EndZ=0
    g6: GeomPoint [constr] X=12.3536 Y=-21 Z=0
    g7: GeomPoint [constr] X=12.3536 Y=-63 Z=0
    g8: Circle CenterX=12.3536 CenterY=-21 CenterZ=0 NormalX=0 NormalY=0 NormalZ=1 AngleXU=0 Radius=1.325
    g9: Circle CenterX=12.3536 CenterY=-42 CenterZ=0 NormalX=0 NormalY=0 NormalZ=1 AngleXU=0 Radius=1.325
    g10: Circle CenterX=12.3536 CenterY=-63 CenterZ=0 NormalX=0 NormalY=0 NormalZ=1 AngleXU=0 Radius=1.325
  constraints (21):
    c: Symmetric(g-3,g-3,g0)
    c: Symmetric(g-5,g-5,g1)
    c: Coincident(g2,g1)
    c: Coincident(g2,g0)
    c: Distance(g3) = 7
    c: Coincident(g3,g1)
    c: PointOnObject(g3,g2)
    c: Coincident(g4,g3)
    c: PointOnObject(g4,g-6)
    c: Parallel(g4,g-5)
    c: Coincident(g5,g3)
    c: PointOnObject(g5,g-4)
    c: Vertical(g5)
    c: Symmetric(g4,g4,g6)
    c: Symmetric(g5,g5,g7)
    c: Diameter(g8) = 2.65
    c: Coincident(g8,g6)
    c: Diameter(g9) = 2.65
    c: Coincident(g9,g3)
    c: Diameter(g10) = 2.65
    c: Coincident(g10,g7)
FEATURE [PartDesign::Pocket] Pocket001
  BaseFeature = -> Pad006
  Direction = (-1,0,2e-16)
  Length = 20
  Length2 = 5
  Placement = pos=(0,-84,2e-15) rot=(1,0,0;1.5708rad)
  Profile = -> Sketch009
  ReferenceAxis = -> Sketch009 [N_Axis]
  Refine = true
  Suppressed = false
  Type = 0
FEATURE [Sketcher::SketchObject] Sketch010
  ArcFitTolerance = 1e-06
  AttachmentSupport = -> [Pocket001]
  ExternalGeometry = -> [Pocket001]
  FullyConstrained = true
  MakeInternals = false
  MapMode = 5
  Placement = pos=(7.71195e-08,-84,20.3536) rot=(1,0,0;3.14159rad)
  sketch-geometry (8):
    g0: LineSegment [constr] StartX=14.1465 StartY=0 StartZ=0 EndX=41.9965 EndY=0 EndZ=0
    g1: LineSegment [constr] StartX=41.9965 StartY=0 StartZ=0 EndX=41.9965 EndY=-84 EndZ=0
    g2: GeomPoint [constr] X=41.9965 Y=-42 Z=0
    g3: LineSegment StartX=35.4965 StartY=-47 StartZ=0 EndX=48.4965 EndY=-47 EndZ=0
    g4: LineSegment StartX=48.4965 StartY=-47 StartZ=0 EndX=48.4965 EndY=-37 EndZ=0
    g5: LineSegment StartX=48.4965 StartY=-37 StartZ=0 EndX=35.4965 EndY=-37 EndZ=0
    g6: LineSegment StartX=35.4965 StartY=-37 StartZ=0 EndX=35.4965 EndY=-47 EndZ=0
    g7: GeomPoint [constr] X=41.9965 Y=-42 Z=0
  constraints (19):
    c: Distance(g0) = 27.85
    c: Coincident(g0,g-3)
    c: PointOnObject(g0,g-3)
    c: Coincident(g1,g0)
    c: PointOnObject(g1,g-4)
    c: Vertical(g1)
    c: Symmetric(g1,g1,g2)
    c: Coincident(g3,g4)
    c: Coincident(g4,g5)
    c: Coincident(g5,g6)
    c: Coincident(g6,g3)
    c: Horizontal(g3)
    c: Horizontal(g5)
    c: Vertical(g4)
    c: Vertical(g6)
    c: Symmetric(g5,g3,g7)
    c: Distance(g4,g6) = 13
    c: Distance(g3,g5) = 10
    c: Coincident(g7,g2)
FEATURE [PartDesign::Pocket] Pocket002
  BaseFeature = -> Pocket001
  Direction = (3.78899e-09,0,1)
  Length = 0.5
  Length2 = 5
  Placement = pos=(0,-84,2e-15) rot=(1,0,0;1.5708rad)
  Profile = -> Sketch010
  ReferenceAxis = -> Sketch010 [N_Axis]
  Refine = true
  Suppressed = false
  Type = 0
FEATURE [Sketcher::SketchObject] Sketch011
  ArcFitTolerance = 1e-06
  AttachmentSupport = -> [Pocket002]
  FullyConstrained = true
  MakeInternals = false
  MapMode = 5
  Placement = pos=(7.9014e-08,-84,20.8536) rot=(1,0,0;3.14159rad)
  sketch-geometry (2):
    g0: LineSegment [constr] StartX=41.9965 StartY=-37 StartZ=0 EndX=41.9965 EndY=-47 EndZ=0
    g1: Circle CenterX=41.9965 CenterY=-42 CenterZ=0 NormalX=0 NormalY=0 NormalZ=1 AngleXU=0 Radius=1.55
  constraints (4):
    c: Symmetric(g-3,g-3,g0)
    c: Symmetric(g-5,g-5,g0)
    c: Diameter(g1) = 3.1
    c: Symmetric(g0,g0,g1)
FEATURE [PartDesign::Pocket] Pocket003
  BaseFeature = -> Pocket002
  Direction = (3.78899e-09,0,1)
  Length = 5
  Length2 = 5
  Placement = pos=(0,-84,2e-15) rot=(1,0,0;1.5708rad)
  Profile = -> Sketch011
  ReferenceAxis = -> Sketch011 [N_Axis]
  Refine = true
  Suppressed = false
  Type = 0
FEATURE [Sketcher::SketchObject] Sketch012
  ArcFitTolerance = 1e-06
  AttachmentSupport = -> [Pocket003]
  ExternalGeometry = -> [Pocket003]
  FullyConstrained = true
  MakeInternals = false
  MapMode = 5
  Placement = pos=(7.11416e-08,-84,25.3536) rot=(0,0,1;3.14159rad)
  sketch-geometry (20):
    g0: LineSegment [constr] StartX=-84 StartY=1.42e-14 StartZ=0 EndX=-84 EndY=-5 EndZ=0
    g1: LineSegment [constr] StartX=-84 StartY=-5 StartZ=0 EndX=-79 EndY=-5 EndZ=0
    g2: LineSegment [constr] StartX=-79 StartY=-5 StartZ=0 EndX=-79 EndY=1.42e-14 EndZ=0
    g3: LineSegment [constr] StartX=-79 StartY=1.42e-14 StartZ=0 EndX=-84 EndY=1.42e-14 EndZ=0
    g4: LineSegment [constr] StartX=-84 StartY=-84 StartZ=0 EndX=-79 EndY=-84 EndZ=0
    g5: LineSegment [constr] StartX=-79 StartY=-84 StartZ=0 EndX=-79 EndY=-79 EndZ=0
    g6: LineSegment [constr] StartX=-79 StartY=-79 StartZ=0 EndX=-84 EndY=-79 EndZ=0
    g7: LineSegment [constr] StartX=-84 StartY=-79 StartZ=0 EndX=-84 EndY=-84 EndZ=0
    g8: LineSegment [constr] StartX=0 StartY=0 StartZ=0 EndX=-5 EndY=0 EndZ=0
    g9: LineSegment [constr] StartX=-5 StartY=0 StartZ=0 EndX=-5 EndY=-5 EndZ=0
    g10: LineSegment [constr] StartX=-5 StartY=-5 StartZ=0 EndX=0 EndY=-5 EndZ=0
    g11: LineSegment [constr] StartX=0 StartY=-5 StartZ=0 EndX=0 EndY=0 EndZ=0
    g12: LineSegment [constr] StartX=7.11416e-08 StartY=-84 StartZ=0 EndX=7.11416e-08 EndY=-79 EndZ=0
    g13: LineSegment [constr] StartX=7.11416e-08 StartY=-79 StartZ=0 EndX=-5 EndY=-79 EndZ=0
    g14: LineSegment [constr] StartX=-5 StartY=-79 StartZ=0 EndX=-5 EndY=-84 EndZ=0
    g15: LineSegment [constr] StartX=-5 StartY=-84 StartZ=0 EndX=7.11416e-08 EndY=-84 EndZ=0
    g16: Circle CenterX=-79 CenterY=-5 CenterZ=0 NormalX=0 NormalY=0 NormalZ=1 AngleXU=0 Radius=1.35
    g17: Circle CenterX=-79 CenterY=-79 CenterZ=0 NormalX=0 NormalY=0 NormalZ=1 AngleXU=0 Radius=1.35
    g18: Circle CenterX=-5 CenterY=-79 CenterZ=0 NormalX=0 NormalY=0 NormalZ=1 AngleXU=0 Radius=1.35
    g19: Circle CenterX=-5 CenterY=-5 CenterZ=0 NormalX=0 NormalY=0 NormalZ=1 AngleXU=0 Radius=1.35
  constraints (52):
    c: Coincident(g0,g1)
    c: Coincident(g1,g2)
    c: Coincident(g2,g3)
    c: Coincident(g3,g0)
    c: Vertical(g0)
    c: Vertical(g2)
    c: Horizontal(g1)
    c: Horizontal(g3)
    c: Distance(g0,g2) = 5
    c: Distance(g1,g3) = 5
    c: Coincident(g0,g-4)
    c: Coincident(g4,g5)
    c: Coincident(g5,g6)
    c: Coincident(g6,g7)
    c: Coincident(g7,g4)
    c: Horizontal(g4)
    c: Horizontal(g6)
    c: Vertical(g5)
    c: Vertical(g7)
    c: Distance(g5,g7) = 5
    c: Distance(g4,g6) = 5
    c: Coincident(g4,g-6)
    c: Coincident(g8,g9)
    c: Coincident(g9,g10)
    c: Coincident(g10,g11)
    c: Coincident(g11,g8)
    c: Horizontal(g8)
    c: Horizontal(g10)
    c: Vertical(g9)
    c: Vertical(g11)
    c: Distance(g9,g11) = 5
    c: Distance(g8,g10) = 5
    c: Coincident(g8,g-1)
    c: Coincident(g12,g13)
    c: Coincident(g13,g14)
    c: Coincident(g14,g15)
    c: Coincident(g15,g12)
    c: Vertical(g12)
    c: Vertical(g14)
    c: Horizontal(g13)
    c: Horizontal(g15)
    c: Distance(g12,g14) = 5
    c: Distance(g13,g15) = 5
    c: Coincident(g12,g-6)
    c: Diameter(g16) = 2.7
    c: Coincident(g16,g1)
    c: Diameter(g17) = 2.7
    c: Coincident(g17,g5)
    c: Diameter(g18) = 2.7
    c: Coincident(g18,g13)
    c: Diameter(g19) = 2.7
    c: Coincident(g19,g9)
FEATURE [PartDesign::Pocket] Pocket004
  BaseFeature = -> Pocket003
  Direction = (-2.80598e-09,0,-1)
  Length = 5
  Length2 = 5
  Placement = pos=(0,-84,2e-15) rot=(1,0,0;1.5708rad)
  Profile = -> Sketch012
  ReferenceAxis = -> Sketch012 [N_Axis]
  Refine = true
  Suppressed = false
  Type = 0
FEATURE [Sketcher::SketchObject] Sketch013
  ArcFitTolerance = 1e-06
  AttachmentSupport = -> [Pocket004]
  ExternalGeometry = -> [Pocket004]
  FullyConstrained = true
  MakeInternals = false
  MapMode = 5
  Placement = pos=(7.11416e-08,-84,25.3536) rot=(0,0,1;3.14159rad)
  sketch-geometry (4):
    g0: LineSegment [constr] StartX=7.11416e-08 StartY=-42 StartZ=0 EndX=-5 EndY=-42 EndZ=0
    g1: Circle CenterX=-5 CenterY=-42 CenterZ=0 NormalX=0 NormalY=0 NormalZ=1 AngleXU=0 Radius=1.35
    g2: LineSegment [constr] StartX=-84 StartY=-42 StartZ=0 EndX=-79 EndY=-42 EndZ=0
    g3: Circle CenterX=-79 CenterY=-42 CenterZ=0 NormalX=0 NormalY=0 NormalZ=1 AngleXU=0 Radius=1.35
  constraints (10):
    c: Distance(g0) = 5
    c: Symmetric(g-3,g-3,g0)
    c: Horizontal(g0)
    c: Diameter(g1) = 2.7
    c: Coincident(g1,g0)
    c: Distance(g2) = 5
    c: Symmetric(g-4,g-4,g2)
    c: Horizontal(g2)
    c: Diameter(g3) = 2.7
    c: Coincident(g3,g2)
FEATURE [PartDesign::Pocket] Pocket005
  BaseFeature = -> Pocket004
  Direction = (-2.80598e-09,0,-1)
  Length = 22
  Length2 = 5
  Placement = pos=(0,-84,2e-15) rot=(1,0,0;1.5708rad)
  Profile = -> Sketch013
  ReferenceAxis = -> Sketch013 [N_Axis]
  Refine = true
  Suppressed = false
  Type = 0
FEATURE [PartDesign::ShapeBinder] CopyPocket005
  Placement = pos=(0,-84,2e-15) rot=(1,0,0;1.5708rad)
  TraceSupport = false
FEATURE [PartDesign::Plane] DatumPlane005
  AttachmentSupport = -> [CopyPocket005]
  Length = 91.117
  MapMode = 5
  Placement = pos=(7.9014e-08,-84,20.8536) rot=(1,0,0;3.14159rad)
  ResizeMode = 0
  Width = 126.87
FEATURE [Sketcher::SketchObject] Sketch014
  ArcFitTolerance = 1e-06
  AttachmentSupport = -> [DatumPlane005]
  FullyConstrained = true
  MakeInternals = false
  MapMode = 5
  Placement = pos=(7.9014e-08,-84,20.8536) rot=(1,0,0;3.14159rad)
  sketch-geometry (6):
    g0: Circle CenterX=41.9965 CenterY=-42 CenterZ=0 NormalX=0 NormalY=0 NormalZ=1 AngleXU=0 Radius=1.35
    g1: LineSegment StartX=35.7465 StartY=-46.75 StartZ=0 EndX=48.2465 EndY=-46.75 EndZ=0
    g2: LineSegment StartX=48.2465 StartY=-46.75 StartZ=0 EndX=48.2465 EndY=-37.25 EndZ=0
    g3: LineSegment StartX=48.2465 StartY=-37.25 StartZ=0 EndX=35.7465 EndY=-37.25 EndZ=0
    g4: LineSegment StartX=35.7465 StartY=-37.25 StartZ=0 EndX=35.7465 EndY=-46.75 EndZ=0
    g5: GeomPoint [constr] X=41.9965 Y=-42 Z=0
  constraints (14):
    c: Diameter(g0) = 2.7
    c: Coincident(g0,g-4)
    c: Coincident(g1,g2)
    c: Coincident(g2,g3)
    c: Coincident(g3,g4)
    c: Coincident(g4,g1)
    c: Horizontal(g1)
    c: Horizontal(g3)
    c: Vertical(g2)
    c: Vertical(g4)
    c: Symmetric(g3,g1,g5)
    c: Distance(g2,g4) = 12.5
    c: Distance(g1,g3) = 9.5
    c: Coincident(g5,g0)
FEATURE [PartDesign::Pad] Pad007
  Direction = (-3.78899e-09,0,-1)
  Length = 3
  Length2 = 10
  Placement = pos=(7.9014e-08,-84,20.8536) rot=(1,0,0;3.14159rad)
  Profile = -> Sketch014
  ReferenceAxis = -> Sketch014 [N_Axis]
  Refine = true
  Suppressed = false
  Type = 0
FEATURE [Sketcher::SketchObject] Sketch015
  ArcFitTolerance = 1e-06
  AttachmentSupport = -> [Pad007]
  ExternalGeometry = -> [Pad007]
  FullyConstrained = true
  MakeInternals = false
  MapMode = 5
  Placement = pos=(6.7647e-08,-84,17.8536) rot=(1,0,0;3.14159rad)
  sketch-geometry (4):
    g0: LineSegment StartX=35.7465 StartY=-37.25 StartZ=0 EndX=35.7465 EndY=-46.75 EndZ=0
    g1: LineSegment StartX=35.7465 StartY=-46.75 StartZ=0 EndX=48.2465 EndY=-46.75 EndZ=0
    g2: LineSegment StartX=48.2465 StartY=-46.75 StartZ=0 EndX=48.2465 EndY=-37.25 EndZ=0
    g3: LineSegment StartX=48.2465 StartY=-37.25 StartZ=0 EndX=35.7465 EndY=-37.25 EndZ=0
  constraints (10):
    c: Coincident(g0,g1)
    c: Coincident(g1,g2)
    c: Coincident(g2,g3)
    c: Coincident(g3,g0)
    c: Vertical(g0)
    c: Vertical(g2)
    c: Horizontal(g1)
    c: Horizontal(g3)
    c: Coincident(g0,g-6)
    c: Coincident(g1,g-5)
FEATURE [PartDesign::Pad] Pad008
  BaseFeature = -> Pad007
  Direction = (-3.78899e-09,0,-1)
  Length = 8
  Length2 = 10
  Placement = pos=(7.9014e-08,-84,20.8536) rot=(1,0,0;3.14159rad)
  Profile = -> Sketch015
  ReferenceAxis = -> Sketch015 [N_Axis]
  Refine = true
  Suppressed = false
  Type = 0
FEATURE [Sketcher::SketchObject] Sketch016
  ArcFitTolerance = 1e-06
  AttachmentSupport = -> [Pad008]
  ExternalGeometry = -> [Pad008]
  FullyConstrained = true
  MakeInternals = false
  MapMode = 5
  Placement = pos=(7.9014e-08,-46.75,20.8536) rot=(0,0.707107,-0.707107;3.14159rad)
  sketch-geometry (2):
    g0: LineSegment [constr] StartX=-41.9965 StartY=0 StartZ=0 EndX=-41.9965 EndY=7 EndZ=0
    g1: Circle CenterX=-41.9965 CenterY=7 CenterZ=0 NormalX=0 NormalY=0 NormalZ=1 AngleXU=0 Radius=2.5
  constraints (5):
    c: Distance(g0) = 7
    c: Symmetric(g-6,g-6,g0)
    c: Vertical(g0)
    c: Diameter(g1) = 5
    c: Coincident(g1,g0)
FEATURE [PartDesign::Hole] Hole001
  BaseFeature = -> Pad008
  CustomThreadClearance = 0
  Depth = 12.72
  DepthType = 0
  Diameter = 4.2
  DrillForDepth = false
  DrillPoint = 1
  DrillPointAngle = 118
  HoleCutCountersinkAngle = 90
  HoleCutCustomValues = false
  HoleCutDepth = 0
  HoleCutDiameter = 6.1
  HoleCutType = 0
  ModelThread = false
  Placement = pos=(7.9014e-08,-84,20.8536) rot=(1,0,0;3.14159rad)
  Profile = -> Sketch016
  Refine = true
  Suppressed = false
  Tapered = false
  TaperedAngle = 90
  ThreadClass = 0
  ThreadDepth = 12.72
  ThreadDepthType = 0
  ThreadDirection = 0
  ThreadFit = 0
  ThreadSize = 13
  ThreadType = 1
  Threaded = true
  UseCustomThreadClearance = false
FEATURE [Sketcher::SketchObject] Sketch017
  ArcFitTolerance = 1e-06
  AttachmentSupport = -> [Hole001]
  ExternalGeometry = -> [Hole001]
  FullyConstrained = true
  MakeInternals = false
  MapMode = 5
  Placement = pos=(7.9014e-08,-46.75,20.8536) rot=(0,0.707107,-0.707107;3.14159rad)
  sketch-geometry (4):
    g0: LineSegment [constr] StartX=-48.2465 StartY=0 StartZ=0 EndX=-48.2465 EndY=2.5 EndZ=0
    g1: LineSegment [constr] StartX=-35.7465 StartY=0 StartZ=0 EndX=-35.7465 EndY=2.5 EndZ=0
    g2: Circle CenterX=-48.2465 CenterY=2.5 CenterZ=0 NormalX=0 NormalY=0 NormalZ=1 AngleXU=0 Radius=1
    g3: Circle CenterX=-35.7465 CenterY=2.5 CenterZ=0 NormalX=0 NormalY=0 NormalZ=1 AngleXU=0 Radius=1
  constraints (10):
    c: Distance(g0) = 2.5
    c: Coincident(g0,g-6)
    c: PointOnObject(g0,g-3)
    c: Distance(g1) = 2.5
    c: Coincident(g1,g-6)
    c: PointOnObject(g1,g-5)
    c: Diameter(g2) = 2
    c: Coincident(g2,g0)
    c: Diameter(g3) = 2
    c: Coincident(g3,g1)
FEATURE [PartDesign::Pocket] Pocket006
  BaseFeature = -> Hole001
  Direction = (0,1,2e-16)
  Length = 10
  Length2 = 5
  Placement = pos=(7.9014e-08,-84,20.8536) rot=(1,0,0;3.14159rad)
  Profile = -> Sketch017
  ReferenceAxis = -> Sketch017 [N_Axis]
  Refine = true
  Suppressed = false
  Type = 0
FEATURE [PartDesign::Chamfer] Chamfer013
  Angle = 45
  Base = -> Pocket006 [Edge30,Edge29]
  BaseFeature = -> Pocket006
  ChamferType = 0
  FlipDirection = false
  Placement = pos=(7.9014e-08,-84,20.8536) rot=(1,0,0;3.14159rad)
  Refine = true
  Size = 3
  Size2 = 1
  SupportTransform = false
  Suppressed = false
  UseAllEdges = false
FEATURE [PartDesign::Body] Body003  label="PlateThreadBlock OLD"
  AllowCompound = false
  Group = -> [DatumPlane005,CopyPocket005,Sketch014,Pad007,Sketch015,Pad008,Sketch016,Hole001,Sketch017,Pocket006,Chamfer013]
  Origin = -> Origin003
  Tip = -> Chamfer013
FEATURE [PartDesign::FeatureBase] Clone
  BaseFeature = -> Body003
  Suppressed = false
FEATURE [Sketcher::SketchObject] Sketch018
  ArcFitTolerance = 1e-06
  AttachmentSupport = -> [Clone]
  ExternalGeometry = -> [Clone]
  FullyConstrained = true
  MakeInternals = false
  MapMode = 5
  Placement = pos=(0,-46.75,0) rot=(1,0,0;1.5708rad)
  sketch-geometry (1):
    g0: Circle CenterX=41.9965 CenterY=13.8536 CenterZ=0 NormalX=0 NormalY=0 NormalZ=1 AngleXU=0 Radius=2.5
  constraints (2):
    c: Diameter(g0) = 5
    c: Coincident(g0,g-3)
FEATURE [PartDesign::Hole] Hole002
  BaseFeature = -> Clone
  CustomThreadClearance = 0.2
  Depth = 25
  DepthType = 0
  Diameter = 5.2
  DrillForDepth = false
  DrillPoint = 1
  DrillPointAngle = 118
  HoleCutCountersinkAngle = 90
  HoleCutCustomValues = false
  HoleCutDepth = 0
  HoleCutDiameter = 6.1
  HoleCutType = 0
  ModelThread = true
  Profile = -> Sketch018
  Refine = true
  Suppressed = false
  Tapered = false
  TaperedAngle = 90
  ThreadClass = 0
  ThreadDepth = 25
  ThreadDepthType = 0
  ThreadDirection = 0
  ThreadFit = 0
  ThreadSize = 14
  ThreadType = 1
  Threaded = true
  UseCustomThreadClearance = true
FEATURE [PartDesign::ShapeBinder] ShapeBinder003
  Placement = pos=(0,-84,2e-14) rot=(1,0,0;1.5708rad)
  Support = -> [Fillet]
  TraceSupport = false
FEATURE [PartDesign::Plane] DatumPlane006
  AttachmentSupport = -> [ShapeBinder003]
  Length = 62.113
  MapMode = 11
  Placement = pos=(42,-84,14) rot=(0.57735,-0.57735,0.57735;2.0944rad)
  ResizeMode = 0
  Width = 85.4755
FEATURE [Sketcher::SketchObject] Sketch019
  ArcFitTolerance = 1e-06
  AttachmentSupport = -> [DatumPlane006]
  ExternalGeometry = -> [ShapeBinder003]
  FullyConstrained = true
  MakeInternals = false
  MapMode = 5
  Placement = pos=(42,-84,14) rot=(0.57735,-0.57735,0.57735;2.0944rad)
  sketch-geometry (1):
    g0: Circle CenterX=0 CenterY=0 CenterZ=0 NormalX=0 NormalY=0 NormalZ=1 AngleXU=0 Radius=2.9
  constraints (2):
    c: Diameter(g0) = 5.8
    c: Coincident(g0,g-1)
FEATURE [PartDesign::Pad] Pad009
  Direction = (0,-1,0)
  Length = 5
  Length2 = 10
  Placement = pos=(42,-84,14) rot=(0.57735,-0.57735,0.57735;2.0944rad)
  Profile = -> Sketch019
  ReferenceAxis = -> Sketch019 [N_Axis]
  Refine = true
  Reversed = true
  Suppressed = false
  Type = 0
FEATURE [Sketcher::SketchObject] Sketch020
  ArcFitTolerance = 1e-06
  AttachmentSupport = -> [Pad009]
  ExternalGeometry = -> [Pad009]
  FullyConstrained = true
  MakeInternals = false
  MapMode = 5
  Placement = pos=(42,-84,14) rot=(0.57735,-0.57735,0.57735;2.0944rad)
  sketch-geometry (1):
    g0: Circle CenterX=0 CenterY=0 CenterZ=0 NormalX=0 NormalY=0 NormalZ=1 AngleXU=0 Radius=3
  constraints (2):
    c: Diameter(g0) = 6
    c: Coincident(g0,g-1)
FEATURE [PartDesign::Pad] Pad010
  BaseFeature = -> Pad009
  Direction = (0,-1,0)
  Length = 15
  Length2 = 10
  Placement = pos=(42,-84,14) rot=(0.57735,-0.57735,0.57735;2.0944rad)
  Profile = -> Sketch020
  ReferenceAxis = -> Sketch020 [N_Axis]
  Refine = true
  Suppressed = false
  Type = 0
FEATURE [Sketcher::SketchObject] Sketch021
  ArcFitTolerance = 1e-06
  AttachmentSupport = -> [Pad010]
  ExternalGeometry = -> [Pad010]
  FullyConstrained = true
  MakeInternals = false
  MapMode = 5
  Placement = pos=(42,-99,14) rot=(0.57735,-0.57735,0.57735;2.0944rad)
  sketch-geometry (1):
    g0: Circle CenterX=0 CenterY=0 CenterZ=0 NormalX=0 NormalY=0 NormalZ=1 AngleXU=0 Radius=7.5
  constraints (2):
    c: Diameter(g0) = 15
    c: Coincident(g0,g-1)
FEATURE [PartDesign::Pad] Pad011
  BaseFeature = -> Pad010
  Direction = (0,-1,0)
  Length = 20
  Length2 = 10
  Placement = pos=(42,-84,14) rot=(0.57735,-0.57735,0.57735;2.0944rad)
  Profile = -> Sketch021
  ReferenceAxis = -> Sketch021 [N_Axis]
  Refine = true
  Suppressed = false
  Type = 0
FEATURE [Sketcher::SketchObject] Sketch022
  ArcFitTolerance = 1e-06
  AttachmentSupport = -> [Pad011]
  ExternalGeometry = -> [Pad011]
  FullyConstrained = true
  MakeInternals = false
  MapMode = 5
  Placement = pos=(42,-119,14) rot=(0.57735,-0.57735,0.57735;2.0944rad)
  sketch-geometry (17):
    g0: LineSegment [constr] StartX=-5.29923e-11 StartY=5.2929e-11 StartZ=0 EndX=-5.29923e-11 EndY=7.5 EndZ=0
    g1: LineSegment [constr] StartX=-5.29923e-11 StartY=5.2929e-11 StartZ=0 EndX=7.5 EndY=5.2929e-11 EndZ=0
    g2: LineSegment [constr] StartX=-5.29923e-11 StartY=5.2929e-11 StartZ=0 EndX=-5.29923e-11 EndY=-7.5 EndZ=0
    g3: LineSegment [constr] StartX=-5.29923e-11 StartY=5.2929e-11 StartZ=0 EndX=-7.5 EndY=5.2929e-11 EndZ=0
    g4: LineSegment [constr] StartX=-5.29923e-11 StartY=5.2929e-11 StartZ=0 EndX=-5.3033 EndY=5.3033 EndZ=0
    g5: LineSegment [constr] StartX=-5.29923e-11 StartY=5.2929e-11 StartZ=0 EndX=5.3033 EndY=5.3033 EndZ=0
    g6: LineSegment [constr] StartX=-5.29923e-11 StartY=5.2929e-11 StartZ=0 EndX=5.3033 EndY=-5.3033 EndZ=0
    g7: LineSegment [constr] StartX=-5.29923e-11 StartY=5.2929e-11 StartZ=0 EndX=-5.3033 EndY=-5.3033 EndZ=0
    g8: Circle CenterX=-5.3033 CenterY=5.3033 CenterZ=0 NormalX=0 NormalY=0 NormalZ=1 AngleXU=0 Radius=1.34e-13
    g9: Circle CenterX=-5.3033 CenterY=5.3033 CenterZ=0 NormalX=0 NormalY=0 NormalZ=1 AngleXU=0 Radius=1.75
    g10: Circle CenterX=-7.5 CenterY=5.2929e-11 CenterZ=0 NormalX=0 NormalY=0 NormalZ=1 AngleXU=0 Radius=1.75
    g11: Circle CenterX=-5.3033 CenterY=-5.3033 CenterZ=0 NormalX=0 NormalY=0 NormalZ=1 AngleXU=0 Radius=1.75
    g12: Circle CenterX=-5.29923e-11 CenterY=-7.5 CenterZ=0 NormalX=0 NormalY=0 NormalZ=1 AngleXU=0 Radius=1.75
    g13: Circle CenterX=5.3033 CenterY=-5.3033 CenterZ=0 NormalX=0 NormalY=0 NormalZ=1 AngleXU=0 Radius=1.75
    g14: Circle CenterX=7.5 CenterY=5.2929e-11 CenterZ=0 NormalX=0 NormalY=0 NormalZ=1 AngleXU=0 Radius=1.75
    g15: Circle CenterX=5.3033 CenterY=5.3033 CenterZ=0 NormalX=0 NormalY=0 NormalZ=1 AngleXU=0 Radius=1.75
    g16: Circle CenterX=-5.29923e-11 CenterY=7.5 CenterZ=0 NormalX=0 NormalY=0 NormalZ=1 AngleXU=0 Radius=1.75
  constraints (42):
    c: Coincident(g0,g-1)
    c: PointOnObject(g0,g-3)
    c: Vertical(g0)
    c: Coincident(g1,g0)
    c: PointOnObject(g1,g-3)
    c: Horizontal(g1)
    c: Coincident(g2,g0)
    c: PointOnObject(g2,g-3)
    c: Vertical(g2)
    c: Coincident(g3,g0)
    c: PointOnObject(g3,g-3)
    c: Horizontal(g3)
    c: Angle(g-1,g4) = 2.35619
    c: Coincident(g4,g0)
    c: PointOnObject(g4,g-3)
    c: Angle(g-1,g5) = 0.785398
    c: Coincident(g5,g0)
    c: PointOnObject(g5,g-3)
    c: Angle(g-1,g6) = -0.785398
    c: Coincident(g6,g0)
    c: PointOnObject(g6,g-3)
    c: Angle(g-1,g7) = -2.35619
    c: Coincident(g7,g0)
    c: PointOnObject(g7,g-3)
    c: Coincident(g8,g4)
    c: Tangent(g8,g-3)
    c: Diameter(g9) = 3.5
    c: Coincident(g9,g4)
    c: Diameter(g10) = 3.5
    c: Coincident(g10,g3)
    c: Diameter(g11) = 3.5
    c: Coincident(g11,g7)
    c: Diameter(g12) = 3.5
    c: Coincident(g12,g2)
    c: Diameter(g13) = 3.5
    c: Coincident(g13,g6)
    c: Diameter(g14) = 3.5
    c: Coincident(g14,g1)
    c: Diameter(g15) = 3.5
    c: Coincident(g15,g5)
    c: Diameter(g16) = 3.5
    c: Coincident(g16,g0)
FEATURE [PartDesign::Pocket] Pocket007
  BaseFeature = -> Pad011
  Direction = (0,1,0)
  Length = 50
  Length2 = 5
  Placement = pos=(42,-84,14) rot=(0.57735,-0.57735,0.57735;2.0944rad)
  Profile = -> Sketch022
  ReferenceAxis = -> Sketch022 [N_Axis]
  Refine = true
  Suppressed = false
  Type = 1
FEATURE [PartDesign::Fillet] Fillet004
  Base = -> Pocket007 [Edge23]
  BaseFeature = -> Pocket007
  Placement = pos=(42,-84,14) rot=(0.57735,-0.57735,0.57735;2.0944rad)
  Radius = 4
  Refine = true
  SupportTransform = false
  Suppressed = false
  UseAllEdges = false
FEATURE [PartDesign::Point] DatumPoint
  AttacherType = Attacher::AttachEnginePoint
  AttachmentSupport = -> [Fillet004]
  MapMode = 36
  Placement = pos=(42,-79,14) rot=(0.707107,0,0.707107;3.14159rad)
FEATURE [Part::Part2DObjectPython] VThreadProfile  # Draft 2D object (typed FeaturePython)
  Area = 21.5626
  Closed = true
  Continuity = C2
  Deviation = 0.1
  Height = 74
  Helix = Helix
  Instructions = Expand this with the ... button to view instructions | Sweep this object along a helix of the same pitch to produce your thread. | It is recommended to make the helix in the ThreadProfile workbench. | If there is an active Body the ThreadProfile object will be put into it.,If not it can be dragged and dropped into the body later. | If there is an active Body when the helix is made there will be made a ShapeBinder for it | For internal threads you will need to cut the Sweep object out of a cylinder, or if using Part Design sweep it as a Subtractive Pipe. | Always use Frenet mode | I have provided some presets, but it is possible there could be some errors.  Double check for mission critical applications. | Also, the tolerances might be different from what you wish to have.  I believe the internal minor diameters are all minimum and the external are all maximum.
  InternalOrExternal = 1
  MakeFace = true
  MinorDiameter = 4.773
  Parameterization = 1
  Pitch = 1
  Placement = pos=(42,-79,14) rot=(1,0,0;-1.5708rad)
  Points = (66) [(2.37314,0.228827,0),(2.31975,0.451556,0),(2.25136,0.667864,0),(2.16643,0.876642,0),(2.06474,1.07659,0),(1.94661,1.26636,0),(1.81267,1.44463,0),+59 more]
  Presets = 16
  Quality = 11
  ThreadCount = 74
  Variants = 0
  Version = 1.92
  external2S_data = [-0.00461051,-0.00886426,-0.0128148,-0.0165028,-0.0199596,-0.0232105,-0.0262759,-0.0291725,-0.0319145,-0.0345137,-0.0369805,-0.0393235,-0.0415505,-0.0436681,-0.0456823,-0.0475981,-0.0494204,-0.0511532,-0.0528003,-0.0543649,-0.0558502,+698 more]
  external3S_data = [-0.00677828,-0.0128149,-0.0182584,-0.0232106,-0.0277444,-0.0319145,-0.0357632,-0.0393236,-0.0426227,-0.0456823,-0.0485208,-0.0511533,-0.0535928,-0.0558503,-0.0579353,-0.059856,-0.0616195,-0.0632319,-0.0646984,-0.0660239,-0.0672123,+698 more]
  external45_data = [-0.00137363,-0.00271738,-0.00403219,-0.00531893,-0.00657844,-0.00781148,-0.00901878,-0.010201,-0.0113589,-0.012493,-0.0136039,-0.0146921,-0.0157583,-0.0168028,-0.0178261,-0.0188288,-0.0198112,-0.0207738,-0.0217169,-0.0226409,-0.0235462,+698 more]
  external_data = [-0.00235387,-0.00461052,-0.00677828,-0.00886428,-0.0108747,-0.0128149,-0.0146895,-0.0165028,-0.0182584,-0.0199597,-0.0216095,-0.0232106,-0.0247653,-0.0262759,-0.0277444,-0.0291725,-0.0305621,-0.0319145,-0.0332313,-0.0345138,-0.0357632,+698 more]
  internal2S_data = [0,0,0,0,0,0,0,0,0,0,0,0,0,0,0,0,0,0,0,0,0,0,0,0,0,0,0,0,0,0,0,0,0,0,0,0,0,0,0,0,0,0,0,0,0,0,0,0,0,0,0,0,0,0,0,0,0,0,0,0,0,0,0,0,0,0,0,0,0,0,0,0,0,0,0,0,0,0,0,0,0,0,0,0,0,0,0,0,0,0,0.00481128,0.00962256,0.0144338,0.0192451,0.0240564,+624 more]
  internal3S_data = [0,0,0,0,0,0,0,0,0,0,0,0,0,0,0,0,0,0,0,0,0,0,0,0,0,0,0,0,0,0,0,0,0,0,0,0,0,0,0,0,0,0,0,0,0,0,0,0,0,0,0,0,0,0,0,0,0,0,0,0,0.00721688,0.0144338,0.0216506,0.0288675,0.0360844,0.0433013,0.0505181,0.057735,0.0649519,0.0721688,0.0793857,0.0866025,+647 more]
  internal45_data = [0,0,0,0,0,0,0,0,0,0,0,0,0,0,0,0,0,0,0,0,0,0,0,0,0,0,0,0,0,0,0,0,0,0,0,0,0,0,0,0,0,0,0,0,0,0,0,0,0,0,0,0,0,0,0,0,0,0,0,0,0,0,0,0,0,0,0,0,0,0,0,0,0,0,0,0,0,0,0,0,0,0,0,0,0,0,0,0,0,0,0,0,0,0,0,0,0,0,0,0,0,0,0,0,0,0,0,0,0,0,0,0,0,0,0,0,0,0,0,0,+599 more]
  internal_data = [0,0,0,0,0,0,0,0,0,0,0,0,0,0,0,0,0,0,0,0,0,0,0,0,0,0,0,0,0,0,0,0,0,0,0,0,0,0,0,0,0,0,0,0,0,0,0,0,0,0,0,0,0,0,0,0,0,0,0,0,0,0,0,0,0,0,0,0,0,0,0,0,0,0,0,0,0,0,0,0,0,0,0,0,0,0,0,0,0,0,0,0,0,0,0,0,0,0,0,0,0,0,0,0,0,0,0,0,0,0,0,0,0,0,0,0,0,0,0,0,+599 more]
  preset_names = <blob: 3959 chars omitted>
  presets_data = [0,0,0,2.20878,24.1173,24.6888,0.25,0.693,0.729,0.25,0.793,0.829,0.25,0.893,0.929,0.3,1.032,1.075,0.35,1.171,1.221,0.35,1.371,1.421,0.4,1.509,1.567,0.45,1.648,1.713,0.45,1.948,2.013,0.5,2.387,2.459,0.6,2.764,2.85,0.7,3.141,3.242,0.75,3.58,+712 more]
FEATURE [Part::Helix] Helix
  Angle = 0
  AttacherType = Attacher::AttachEngine3D
  Height = 74
  Length = 470.808
  LocalCoord = 0
  Pitch = 1
  Placement = pos=(42,-79,14) rot=(1,0,0;-1.5708rad)
  Radius = 1
  SegmentLength = 1
  Style = 0
  expr: AttachmentOffset = VThreadProfile.AttachmentOffset
  expr: AttachmentSupport = VThreadProfile.AttachmentSupport
  expr: Height = VThreadProfile.ThreadCount * VThreadProfile.Pitch
  expr: MapMode = VThreadProfile.MapMode
  expr: MapPathParameter = VThreadProfile.MapPathParameter
  expr: MapReversed = VThreadProfile.MapReversed
  expr: Pitch = VThreadProfile.Pitch
  expr: SegmentLength = 1
FEATURE [PartDesign::AdditivePipe] AdditivePipe
  AuxilleryCurvelinear = true
  AuxillerySpineTangent = false
  BaseFeature = -> Fillet004
  Binormal = (0,0,0)
  Mode = 2
  Placement = pos=(42,-84,14) rot=(0.57735,-0.57735,0.57735;2.0944rad)
  Profile = -> VThreadProfile
  Refine = true
  Spine = -> Helix [Edge1,Edge2,Edge3,Edge4,Edge5,Edge6,Edge7,Edge8,Edge9,Edge10,Edge11,Edge12,Edge13,Edge14,Edge15,Edge16,Edge17,Edge18,Edge19,Edge20,Edge21,Edge22,Edge23,Edge24,Edge25,Edge26,Edge27,Edge28,Edge29,Edge30,Edge31,Edge32,Edge33,Edge34,Edge35,Edge36,Edge37,Edge38,Edge39,Edge40,+34 more]
  SpineTangent = false
  Suppressed = false
  Transformation = 0
  Transition = 0
FEATURE [PartDesign::ShapeBinder] ShapeBinder004
  Support = -> [Fillet]
  TraceSupport = false
FEATURE [PartDesign::Plane] DatumPlane007
  AttachmentSupport = -> [AdditivePipe]
  Length = 62.1132
  MapMode = 5
  Placement = pos=(42.0014,-4.99998,14) rot=(0.577354,0.577344,0.577354;4.18878rad)
  ResizeMode = 0
  Width = 85.4783
FEATURE [Sketcher::SketchObject] Sketch023
  ArcFitTolerance = 1e-06
  AttachmentSupport = -> [DatumPlane007]
  FullyConstrained = true
  MakeInternals = false
  MapMode = 5
  Placement = pos=(42.0014,-4.99998,14) rot=(0.577354,0.577344,0.577354;4.18878rad)
  sketch-geometry (1):
    g0: Circle CenterX=0 CenterY=0 CenterZ=0 NormalX=0 NormalY=0 NormalZ=1 AngleXU=0 Radius=2.9
  constraints (2):
    c: Diameter(g0) = 5.8
    c: Coincident(g0,g-1)
FEATURE [PartDesign::Pad] Pad012
  BaseFeature = -> AdditivePipe
  Direction = (1.755e-05,1,1.0234e-10)
  Length = 10
  Length2 = 10
  Placement = pos=(42,-84,14) rot=(0.57735,-0.57735,0.57735;2.0944rad)
  Profile = -> Sketch023
  ReferenceAxis = -> Sketch023 [N_Axis]
  Refine = true
  Suppressed = false
  Type = 0
FEATURE [PartDesign::ShapeBinder] CopyPocket008
  Placement = pos=(42,-84,14) rot=(0.57735,-0.57735,0.57735;2.0944rad)
  TraceSupport = false
FEATURE [PartDesign::Plane] DatumPlane008
  AttachmentSupport = -> [CopyPocket008]
  Length = 61.9575
  MapMode = 5
  Placement = pos=(41.9985,5.00002,14) rot=(-0.577347,-0.577357,-0.577347;2.09438rad)
  ResizeMode = 0
  Width = 83.4479
FEATURE [Sketcher::SketchObject] Sketch025
  ArcFitTolerance = 1e-06
  AttachmentSupport = -> [DatumPlane008]
  ExternalGeometry = -> [CopyPocket008]
  FullyConstrained = true
  MakeInternals = false
  MapMode = 5
  Placement = pos=(41.9985,5.00002,14) rot=(-0.577347,-0.577357,-0.577347;2.09438rad)
  sketch-geometry (2):
    g0: Circle CenterX=0 CenterY=0 CenterZ=0 NormalX=0 NormalY=0 NormalZ=1 AngleXU=0 Radius=1.55
    g1: Circle CenterX=0 CenterY=0 CenterZ=0 NormalX=0 NormalY=0 NormalZ=1 AngleXU=0 Radius=4.5
  constraints (4):
    c: Diameter(g0) = 3.1
    c: Coincident(g0,g-1)
    c: Diameter(g1) = 9
    c: Coincident(g1,g0)
FEATURE [PartDesign::Pad] Pad013
  Direction = (-1.75232e-05,1,-4.99912e-10)
  Length = 3
  Length2 = 10
  Placement = pos=(41.9985,5.00002,14) rot=(-0.577347,-0.577357,-0.577347;2.09438rad)
  Profile = -> Sketch025
  ReferenceAxis = -> Sketch025 [N_Axis]
  Refine = true
  Suppressed = false
  Type = 0
FEATURE [PartDesign::Plane] DatumPlane009
  AttachmentSupport = -> [Pad013]
  Length = 61.9575
  MapMode = 5
  Placement = pos=(41.9984,8.00002,14) rot=(-0.577347,-0.577357,-0.577347;2.09438rad)
  ResizeMode = 0
  Width = 83.4479
FEATURE [Sketcher::SketchObject] Sketch026
  ArcFitTolerance = 1e-06
  AttachmentSupport = -> [DatumPlane009]
  ExternalGeometry = -> [Pad013]
  FullyConstrained = true
  MakeInternals = false
  MapMode = 5
  Placement = pos=(41.9984,8.00002,14) rot=(-0.577347,-0.577357,-0.577347;2.09438rad)
  sketch-geometry (2):
    g0: Circle CenterX=0 CenterY=0 CenterZ=0 NormalX=0 NormalY=0 NormalZ=1 AngleXU=0 Radius=4.50001
    g1: Circle CenterX=0 CenterY=0 CenterZ=0 NormalX=0 NormalY=0 NormalZ=1 AngleXU=0 Radius=3.1
  constraints (4):
    c: Coincident(g0,g-1)
    c: Tangent(g0,g-3)
    c: Diameter(g1) = 6.2
    c: Coincident(g1,g0)
FEATURE [PartDesign::Pad] Pad014
  BaseFeature = -> Pad013
  Direction = (-1.75232e-05,1,-4.99912e-10)
  Length = 6
  Length2 = 10
  Placement = pos=(41.9985,5.00002,14) rot=(-0.577347,-0.577357,-0.577347;2.09438rad)
  Profile = -> Sketch026
  ReferenceAxis = -> Sketch026 [N_Axis]
  Refine = true
  Suppressed = false
  Type = 0
FEATURE [PartDesign::Chamfer] Chamfer014
  Angle = 45
  Base = -> Pad014 [Edge11]
  BaseFeature = -> Pad014
  ChamferType = 0
  FlipDirection = false
  Placement = pos=(41.9985,5.00002,14) rot=(-0.577347,-0.577357,-0.577347;2.09438rad)
  Refine = true
  Size = 0.5
  Size2 = 1
  SupportTransform = false
  Suppressed = false
  UseAllEdges = false
FEATURE [PartDesign::Body] Body006  label="Adjuster Cap"
  AllowCompound = false
  Group = -> [DatumPlane008,CopyPocket008,Sketch025,Pad013,DatumPlane009,Sketch026,Pad014,Chamfer014]
  Origin = -> Origin006
  Tip = -> Chamfer014
FEATURE [Sketcher::SketchObject] Sketch027
  ArcFitTolerance = 1e-06
  AttachmentSupport = -> [Fillet]
  ExternalGeometry = -> [Fillet]
  FullyConstrained = true
  MakeInternals = false
  MapMode = 5
  Placement = pos=(0,-84,0) rot=(1,0,0;1.5708rad)
  sketch-geometry (2):
    g0: Circle CenterX=42 CenterY=14 CenterZ=0 NormalX=0 NormalY=0 NormalZ=1 AngleXU=0 Radius=3.125
    g1: Circle CenterX=42 CenterY=14 CenterZ=0 NormalX=0 NormalY=0 NormalZ=1 AngleXU=0 Radius=3.75
  constraints (4):
    c: Coincident(g0,g-3)
    c: Diameter(g1) = 7.5
    c: Coincident(g1,g0)
    c: Diameter(g0) = 6.25
FEATURE [PartDesign::Pad] Pad015
  BaseFeature = -> Fillet
  Direction = (0,-1,2e-16)
  Length = 8
  Length2 = 10
  Placement = pos=(0,0,0) rot=(1,0,0;1.5708rad)
  Profile = -> Sketch027
  ReferenceAxis = -> Sketch027 [N_Axis]
  Refine = true
  Suppressed = false
  Type = 0
FEATURE [PartDesign::Fillet] Fillet005
  Base = -> Pad015 [Edge70]
  BaseFeature = -> Pad015
  Placement = pos=(0,0,0) rot=(1,0,0;1.5708rad)
  Radius = 2
  Refine = true
  SupportTransform = false
  Suppressed = false
  UseAllEdges = false
FEATURE [Sketcher::SketchObject] Sketch030
  ArcFitTolerance = 1e-06
  AttachmentSupport = -> [Pocket005]
  ExternalGeometry = -> [Pocket005]
  FullyConstrained = true
  MakeInternals = false
  MapMode = 5
  Placement = pos=(7.11416e-08,-84,25.3536) rot=(0,0,1;3.14159rad)
  sketch-geometry (11):
    g0: LineSegment StartX=-84 StartY=0 StartZ=0 EndX=-84 EndY=-84 EndZ=0
    g1: LineSegment StartX=-84 StartY=-84 StartZ=0 EndX=7.11416e-08 EndY=-84 EndZ=0
    g2: LineSegment StartX=7.11416e-08 StartY=-84 StartZ=0 EndX=7.11416e-08 EndY=0 EndZ=0
    g3: LineSegment StartX=7.11416e-08 StartY=0 StartZ=0 EndX=-84 EndY=0 EndZ=0
    g4: Circle CenterX=-79 CenterY=-5 CenterZ=0 NormalX=0 NormalY=0 NormalZ=1 AngleXU=0 Radius=1.35
    g5: Circle CenterX=-79 CenterY=-42 CenterZ=0 NormalX=0 NormalY=0 NormalZ=1 AngleXU=0 Radius=1.35
    g6: Circle CenterX=-79 CenterY=-79 CenterZ=0 NormalX=0 NormalY=0 NormalZ=1 AngleXU=0 Radius=1.35
    g7: Circle CenterX=-41.9965 CenterY=-42 CenterZ=0 NormalX=0 NormalY=0 NormalZ=1 AngleXU=0 Radius=1.55
    g8: Circle CenterX=-5 CenterY=-5 CenterZ=0 NormalX=0 NormalY=0 NormalZ=1 AngleXU=0 Radius=1.35
    g9: Circle CenterX=-5 CenterY=-42 CenterZ=0 NormalX=0 NormalY=0 NormalZ=1 AngleXU=0 Radius=1.35
    g10: Circle CenterX=-5 CenterY=-79 CenterZ=0 NormalX=0 NormalY=0 NormalZ=1 AngleXU=0 Radius=1.35
  constraints (24):
    c: Coincident(g0,g1)
    c: Coincident(g1,g2)
    c: Coincident(g2,g3)
    c: Coincident(g3,g0)
    c: Vertical(g0)
    c: Vertical(g2)
    c: Horizontal(g1)
    c: Horizontal(g3)
    c: Coincident(g0,g-7)
    c: Coincident(g1,g-6)
    c: Coincident(g4,g-3)
    c: Equal(g4,g-3)
    c: Coincident(g5,g-10)
    c: Equal(g5,g-10)
    c: Coincident(g6,g-12)
    c: Equal(g6,g-12)
    c: Coincident(g7,g-9)
    c: Equal(g7,g-9)
    c: Coincident(g8,g-11)
    c: Equal(g8,g-11)
    c: Coincident(g9,g-8)
    c: Equal(g9,g-8)
    c: Coincident(g10,g-13)
    c: Equal(g10,g-13)
FEATURE [PartDesign::Pad] Pad016
  BaseFeature = -> Pocket005
  Direction = (2.80598e-09,0,1)
  Length = 2
  Length2 = 10
  Placement = pos=(0,-84,2e-15) rot=(1,0,0;1.5708rad)
  Profile = -> Sketch030
  ReferenceAxis = -> Sketch030 [N_Axis]
  Refine = true
  Suppressed = false
  Type = 0
FEATURE [Sketcher::SketchObject] Sketch031
  ArcFitTolerance = 1e-06
  AttachmentSupport = -> [Pad016]
  ExternalGeometry = -> [Pad016]
  FullyConstrained = true
  MakeInternals = false
  MapMode = 5
  Placement = pos=(7.67535e-08,-84,27.3536) rot=(0,0,1;3.14159rad)
  sketch-geometry (1):
    g0: Circle CenterX=-41.9965 CenterY=-42 CenterZ=0 NormalX=0 NormalY=0 NormalZ=1 AngleXU=0 Radius=3
  constraints (2):
    c: Diameter(g0) = 6
    c: Coincident(g0,g-3)
FEATURE [PartDesign::Pocket] Pocket011
  BaseFeature = -> Pad016
  Direction = (-2.80598e-09,0,-1)
  Length = 4
  Length2 = 5
  Placement = pos=(0,-84,2e-15) rot=(1,0,0;1.5708rad)
  Profile = -> Sketch031
  ReferenceAxis = -> Sketch031 [N_Axis]
  Refine = true
  Suppressed = false
  Type = 0
FEATURE [PartDesign::ShapeBinder] CopyPocket011
  Placement = pos=(0,-84,2e-15) rot=(1,0,0;1.5708rad)
  TraceSupport = false
FEATURE [PartDesign::Plane] DatumPlane010
  AttachmentSupport = -> [CopyPocket011]
  Length = 130.8
  MapMode = 5
  Placement = pos=(7.67535e-08,-84,27.3536) rot=(0,0,1;3.14159rad)
  ResizeMode = 0
  Width = 130.8
FEATURE [Sketcher::SketchObject] Sketch032
  ArcFitTolerance = 1e-06
  AttachmentSupport = -> [DatumPlane010]
  ExternalGeometry = -> [CopyPocket011]
  FullyConstrained = true
  MakeInternals = false
  MapMode = 5
  Placement = pos=(7.67535e-08,-84,27.3536) rot=(0,0,1;3.14159rad)
  sketch-geometry (10):
    g0: Circle CenterX=-79 CenterY=-42 CenterZ=0 NormalX=0 NormalY=0 NormalZ=1 AngleXU=0 Radius=3
    g1: Circle CenterX=-5 CenterY=-42 CenterZ=0 NormalX=0 NormalY=0 NormalZ=1 AngleXU=0 Radius=3
    g2: LineSegment StartX=-84 StartY=0 StartZ=0 EndX=-84 EndY=-84 EndZ=0
    g3: LineSegment StartX=-84 StartY=-84 StartZ=0 EndX=7.11416e-08 EndY=-84 EndZ=0
    g4: LineSegment StartX=7.11416e-08 StartY=-84 StartZ=0 EndX=7.11416e-08 EndY=0 EndZ=0
    g5: LineSegment StartX=7.11416e-08 StartY=0 StartZ=0 EndX=-84 EndY=0 EndZ=0
    g6: Circle CenterX=-79 CenterY=-5 CenterZ=0 NormalX=0 NormalY=0 NormalZ=1 AngleXU=0 Radius=1.6
    g7: Circle CenterX=-79 CenterY=-79 CenterZ=0 NormalX=0 NormalY=0 NormalZ=1 AngleXU=0 Radius=1.6
    g8: Circle CenterX=-5 CenterY=-5 CenterZ=0 NormalX=0 NormalY=0 NormalZ=1 AngleXU=0 Radius=1.6
    g9: Circle CenterX=-5 CenterY=-79 CenterZ=0 NormalX=0 NormalY=0 NormalZ=1 AngleXU=0 Radius=1.6
  constraints (22):
    c: Diameter(g0) = 6
    c: Coincident(g0,g-8)
    c: Diameter(g1) = 6
    c: Coincident(g1,g-10)
    c: Coincident(g2,g3)
    c: Coincident(g3,g4)
    c: Coincident(g4,g5)
    c: Coincident(g5,g2)
    c: Vertical(g2)
    c: Vertical(g4)
    c: Horizontal(g3)
    c: Horizontal(g5)
    c: Coincident(g2,g-4)
    c: Coincident(g3,g-6)
    c: Diameter(g6) = 3.2
    c: Coincident(g6,g-9)
    c: Coincident(g7,g-7)
    c: Diameter(g7) = 3.2
    c: Coincident(g8,g-12)
    c: Coincident(g9,g-11)
    c: Diameter(g9) = 3.2
    c: Diameter(g8) = 3.2
FEATURE [PartDesign::Pad] Pad017
  Direction = (2.80598e-09,0,1)
  Length = 4
  Length2 = 10
  Placement = pos=(7.67535e-08,-84,27.3536) rot=(0,0,1;3.14159rad)
  Profile = -> Sketch032
  ReferenceAxis = -> Sketch032 [N_Axis]
  Refine = true
  Suppressed = false
  Type = 0
FEATURE [Sketcher::SketchObject] Sketch033
  ArcFitTolerance = 1e-06
  AttachmentSupport = -> [Pad017]
  ExternalGeometry = -> [Pad017]
  FullyConstrained = true
  MakeInternals = false
  MapMode = 5
  Placement = pos=(8.79774e-08,-84,31.3536) rot=(0,0,1;3.14159rad)
  sketch-geometry (10):
    g0: Circle CenterX=-79 CenterY=-42 CenterZ=0 NormalX=0 NormalY=0 NormalZ=1 AngleXU=0 Radius=3
    g1: Circle CenterX=-5 CenterY=-42 CenterZ=0 NormalX=0 NormalY=0 NormalZ=1 AngleXU=0 Radius=3
    g2: Circle CenterX=-5 CenterY=-5 CenterZ=0 NormalX=0 NormalY=0 NormalZ=1 AngleXU=0 Radius=3
    g3: Circle CenterX=-5 CenterY=-79 CenterZ=0 NormalX=0 NormalY=0 NormalZ=1 AngleXU=0 Radius=3
    g4: Circle CenterX=-79 CenterY=-79 CenterZ=0 NormalX=0 NormalY=0 NormalZ=1 AngleXU=0 Radius=3
    g5: Circle CenterX=-79 CenterY=-5 CenterZ=0 NormalX=0 NormalY=0 NormalZ=1 AngleXU=0 Radius=3
    g6: LineSegment StartX=-84 StartY=0 StartZ=0 EndX=-84 EndY=-84 EndZ=0
    g7: LineSegment StartX=-84 StartY=-84 StartZ=0 EndX=7.11416e-08 EndY=-84 EndZ=0
    g8: LineSegment StartX=7.11416e-08 StartY=-84 StartZ=0 EndX=7.11416e-08 EndY=0 EndZ=0
    g9: LineSegment StartX=7.11416e-08 StartY=0 StartZ=0 EndX=-84 EndY=0 EndZ=0
  constraints (22):
    c: Coincident(g0,g-8)
    c: Equal(g0,g-8)
    c: Coincident(g1,g-11)
    c: Equal(g1,g-11)
    c: Diameter(g2) = 6
    c: Coincident(g2,g-10)
    c: Diameter(g3) = 6
    c: Coincident(g3,g-12)
    c: Diameter(g4) = 6
    c: Coincident(g4,g-7)
    c: Diameter(g5) = 6
    c: Coincident(g5,g-9)
    c: Coincident(g6,g7)
    c: Coincident(g7,g8)
    c: Coincident(g8,g9)
    c: Coincident(g9,g6)
    c: Vertical(g6)
    c: Vertical(g8)
    c: Horizontal(g7)
    c: Horizontal(g9)
    c: Coincident(g6,g-4)
    c: Coincident(g7,g-6)
FEATURE [PartDesign::Pad] Pad018
  BaseFeature = -> Pad017
  Direction = (2.80598e-09,0,1)
  Length = 3.5
  Length2 = 10
  Placement = pos=(7.67535e-08,-84,27.3536) rot=(0,0,1;3.14159rad)
  Profile = -> Sketch033
  ReferenceAxis = -> Sketch033 [N_Axis]
  Refine = true
  Suppressed = false
  Type = 0
FEATURE [Sketcher::SketchObject] Sketch034
  ArcFitTolerance = 1e-06
  AttachmentSupport = -> [Pad018]
  ExternalGeometry = -> [Pad018]
  FullyConstrained = false
  MakeInternals = false
  MapMode = 5
  Placement = pos=(9.77984e-08,-84,34.8536) rot=(0,0,1;3.14159rad)
  sketch-geometry (212):
    g0: LineSegment [constr] StartX=-42 StartY=-7.1e-15 StartZ=0 EndX=-42 EndY=-84 EndZ=0
    g1: GeomPoint X=-42 Y=-42 Z=0
    g2: Circle CenterX=-42 CenterY=-42 CenterZ=0 NormalX=0 NormalY=0 NormalZ=1 AngleXU=0 Radius=1.3
    g3: Circle CenterX=-37 CenterY=-42 CenterZ=0 NormalX=0 NormalY=0 NormalZ=1 AngleXU=0 Radius=1.3
    g4: Circle CenterX=-32 CenterY=-42 CenterZ=0 NormalX=0 NormalY=0 NormalZ=1 AngleXU=0 Radius=1.3
    g5: Circle CenterX=-27 CenterY=-42 CenterZ=0 NormalX=0 NormalY=0 NormalZ=1 AngleXU=0 Radius=1.3
    g6: Circle CenterX=-22 CenterY=-42 CenterZ=0 NormalX=0 NormalY=0 NormalZ=1 AngleXU=0 Radius=1.3
    g7: Circle CenterX=-17 CenterY=-42 CenterZ=0 NormalX=0 NormalY=0 NormalZ=1 AngleXU=0 Radius=1.3
    g8: Circle CenterX=-12 CenterY=-42 CenterZ=0 NormalX=0 NormalY=0 NormalZ=1 AngleXU=0 Radius=1.3
    g9: GeomPoint X=-42 Y=-37 Z=0
    g10: Circle CenterX=-42 CenterY=-37 CenterZ=0 NormalX=0 NormalY=0 NormalZ=1 AngleXU=0 Radius=1.3
    g11: Circle CenterX=-37 CenterY=-37 CenterZ=0 NormalX=0 NormalY=0 NormalZ=1 AngleXU=0 Radius=1.3
    g12: Circle CenterX=-32 CenterY=-37 CenterZ=0 NormalX=0 NormalY=0 NormalZ=1 AngleXU=0 Radius=1.3
    g13: Circle CenterX=-27 CenterY=-37 CenterZ=0 NormalX=0 NormalY=0 NormalZ=1 AngleXU=0 Radius=1.3
    g14: Circle CenterX=-22 CenterY=-37 CenterZ=0 NormalX=0 NormalY=0 NormalZ=1 AngleXU=0 Radius=1.3
    g15: Circle CenterX=-17 CenterY=-37 CenterZ=0 NormalX=0 NormalY=0 NormalZ=1 AngleXU=0 Radius=1.3
    g16: Circle CenterX=-12 CenterY=-37 CenterZ=0 NormalX=0 NormalY=0 NormalZ=1 AngleXU=0 Radius=1.3
    g17: GeomPoint X=-42 Y=-32 Z=0
    g18: Circle CenterX=-42 CenterY=-32 CenterZ=0 NormalX=0 NormalY=0 NormalZ=1 AngleXU=0 Radius=1.3
    g19: Circle CenterX=-37 CenterY=-32 CenterZ=0 NormalX=0 NormalY=0 NormalZ=1 AngleXU=0 Radius=1.3
    g20: Circle CenterX=-32 CenterY=-32 CenterZ=0 NormalX=0 NormalY=0 NormalZ=1 AngleXU=0 Radius=1.3
    g21: Circle CenterX=-27 CenterY=-32 CenterZ=0 NormalX=0 NormalY=0 NormalZ=1 AngleXU=0 Radius=1.3
    g22: Circle CenterX=-22 CenterY=-32 CenterZ=0 NormalX=0 NormalY=0 NormalZ=1 AngleXU=0 Radius=1.3
    g23: Circle CenterX=-17 CenterY=-32 CenterZ=0 NormalX=0 NormalY=0 NormalZ=1 AngleXU=0 Radius=1.3
    g24: Circle CenterX=-12 CenterY=-32 CenterZ=0 NormalX=0 NormalY=0 NormalZ=1 AngleXU=0 Radius=1.3
    g25: GeomPoint X=-42 Y=-27 Z=0
    g26: Circle CenterX=-42 CenterY=-27 CenterZ=0 NormalX=0 NormalY=0 NormalZ=1 AngleXU=0 Radius=1.3
    g27: Circle CenterX=-37 CenterY=-27 CenterZ=0 NormalX=0 NormalY=0 NormalZ=1 AngleXU=0 Radius=1.3
    g28: Circle CenterX=-32 CenterY=-27 CenterZ=0 NormalX=0 NormalY=0 NormalZ=1 AngleXU=0 Radius=1.3
    g29: Circle CenterX=-27 CenterY=-27 CenterZ=0 NormalX=0 NormalY=0 NormalZ=1 AngleXU=0 Radius=1.3
    g30: Circle CenterX=-22 CenterY=-27 CenterZ=0 NormalX=0 NormalY=0 NormalZ=1 AngleXU=0 Radius=1.3
    g31: Circle CenterX=-17 CenterY=-27 CenterZ=0 NormalX=0 NormalY=0 NormalZ=1 AngleXU=0 Radius=1.3
    g32: Circle CenterX=-12 CenterY=-27 CenterZ=0 NormalX=0 NormalY=0 NormalZ=1 AngleXU=0 Radius=1.3
    g33: GeomPoint X=-42 Y=-22 Z=0
    g34: Circle CenterX=-42 CenterY=-22 CenterZ=0 NormalX=0 NormalY=0 NormalZ=1 AngleXU=0 Radius=1.3
    g35: Circle CenterX=-37 CenterY=-22 CenterZ=0 NormalX=0 NormalY=0 NormalZ=1 AngleXU=0 Radius=1.3
    g36: Circle CenterX=-32 CenterY=-22 CenterZ=0 NormalX=0 NormalY=0 NormalZ=1 AngleXU=0 Radius=1.3
    g37: Circle CenterX=-27 CenterY=-22 CenterZ=0 NormalX=0 NormalY=0 NormalZ=1 AngleXU=0 Radius=1.3
    g38: Circle CenterX=-22 CenterY=-22 CenterZ=0 NormalX=0 NormalY=0 NormalZ=1 AngleXU=0 Radius=1.3
    g39: Circle CenterX=-17 CenterY=-22 CenterZ=0 NormalX=0 NormalY=0 NormalZ=1 AngleXU=0 Radius=1.3
    g40: Circle CenterX=-12 CenterY=-22 CenterZ=0 NormalX=0 NormalY=0 NormalZ=1 AngleXU=0 Radius=1.3
    g41: GeomPoint X=-42 Y=-17 Z=0
    g42: Circle CenterX=-42 CenterY=-17 CenterZ=0 NormalX=0 NormalY=0 NormalZ=1 AngleXU=0 Radius=1.3
    g43: Circle CenterX=-37 CenterY=-17 CenterZ=0 NormalX=0 NormalY=0 NormalZ=1 AngleXU=0 Radius=1.3
    g44: Circle CenterX=-32 CenterY=-17 CenterZ=0 NormalX=0 NormalY=0 NormalZ=1 AngleXU=0 Radius=1.3
    g45: Circle CenterX=-27 CenterY=-17 CenterZ=0 NormalX=0 NormalY=0 NormalZ=1 AngleXU=0 Radius=1.3
    g46: Circle CenterX=-22 CenterY=-17 CenterZ=0 NormalX=0 NormalY=0 NormalZ=1 AngleXU=0 Radius=1.3
    g47: Circle CenterX=-17 CenterY=-17 CenterZ=0 NormalX=0 NormalY=0 NormalZ=1 AngleXU=0 Radius=1.3
    g48: Circle CenterX=-12 CenterY=-17 CenterZ=0 NormalX=0 NormalY=0 NormalZ=1 AngleXU=0 Radius=1.3
    g49: GeomPoint X=-42 Y=-12 Z=0
    g50: Circle CenterX=-42 CenterY=-12 CenterZ=0 NormalX=0 NormalY=0 NormalZ=1 AngleXU=0 Radius=1.3
    g51: Circle CenterX=-37 CenterY=-12 CenterZ=0 NormalX=0 NormalY=0 NormalZ=1 AngleXU=0 Radius=1.3
    g52: Circle CenterX=-32 CenterY=-12 CenterZ=0 NormalX=0 NormalY=0 NormalZ=1 AngleXU=0 Radius=1.3
    g53: Circle CenterX=-27 CenterY=-12 CenterZ=0 NormalX=0 NormalY=0 NormalZ=1 AngleXU=0 Radius=1.3
    g54: Circle CenterX=-22 CenterY=-12 CenterZ=0 NormalX=0 NormalY=0 NormalZ=1 AngleXU=0 Radius=1.3
    g55: Circle CenterX=-17 CenterY=-12 CenterZ=0 NormalX=0 NormalY=0 NormalZ=1 AngleXU=0 Radius=1.3
    g56: Circle CenterX=-12 CenterY=-12 CenterZ=0 NormalX=0 NormalY=0 NormalZ=1 AngleXU=0 Radius=1.3
    g57: GeomPoint X=-42 Y=-7 Z=0
    g58: Circle CenterX=-42 CenterY=-7 CenterZ=0 NormalX=0 NormalY=0 NormalZ=1 AngleXU=0 Radius=1.3
    g59: Circle CenterX=-37 CenterY=-7 CenterZ=0 NormalX=0 NormalY=0 NormalZ=1 AngleXU=0 Radius=1.3
    g60: Circle CenterX=-32 CenterY=-7 CenterZ=0 NormalX=0 NormalY=0 NormalZ=1 AngleXU=0 Radius=1.3
    g61: Circle CenterX=-27 CenterY=-7 CenterZ=0 NormalX=0 NormalY=0 NormalZ=1 AngleXU=0 Radius=1.3
    g62: Circle CenterX=-22 CenterY=-7 CenterZ=0 NormalX=0 NormalY=0 NormalZ=1 AngleXU=0 Radius=1.3
    g63: Circle CenterX=-17 CenterY=-7 CenterZ=0 NormalX=0 NormalY=0 NormalZ=1 AngleXU=0 Radius=1.3
    g64: Circle CenterX=-12 CenterY=-7 CenterZ=0 NormalX=0 NormalY=0 NormalZ=1 AngleXU=0 Radius=1.3
    g65: LineSegment [constr] StartX=-84 StartY=-42 StartZ=0 EndX=7.11416e-08 EndY=-42 EndZ=0
    g66: Circle CenterX=-47 CenterY=-42 CenterZ=0 NormalX=0 NormalY=0 NormalZ=1 AngleXU=0 Radius=1.3
    g67: Circle CenterX=-52 CenterY=-42 CenterZ=0 NormalX=0 NormalY=0 NormalZ=1 AngleXU=0 Radius=1.3
    g68: Circle CenterX=-57 CenterY=-42 CenterZ=0 NormalX=0 NormalY=0 NormalZ=1 AngleXU=0 Radius=1.3
    g69: Circle CenterX=-62 CenterY=-42 CenterZ=0 NormalX=0 NormalY=0 NormalZ=1 AngleXU=0 Radius=1.3
    g70: Circle CenterX=-67 CenterY=-42 CenterZ=0 NormalX=0 NormalY=0 NormalZ=1 AngleXU=0 Radius=1.3
    g71: Circle CenterX=-72 CenterY=-42 CenterZ=0 NormalX=0 NormalY=0 NormalZ=1 AngleXU=0 Radius=1.3
    g72: Circle CenterX=-47 CenterY=-37 CenterZ=0 NormalX=0 NormalY=0 NormalZ=1 AngleXU=0 Radius=1.3
    g73: Circle CenterX=-52 CenterY=-37 CenterZ=0 NormalX=0 NormalY=0 NormalZ=1 AngleXU=0 Radius=1.3
    g74: Circle CenterX=-57 CenterY=-37 CenterZ=0 NormalX=0 NormalY=0 NormalZ=1 AngleXU=0 Radius=1.3
    g75: Circle CenterX=-62 CenterY=-37 CenterZ=0 NormalX=0 NormalY=0 NormalZ=1 AngleXU=0 Radius=1.3
    g76: Circle CenterX=-67 CenterY=-37 CenterZ=0 NormalX=0 NormalY=0 NormalZ=1 AngleXU=0 Radius=1.3
    g77: Circle CenterX=-72 CenterY=-37 CenterZ=0 NormalX=0 NormalY=0 NormalZ=1 AngleXU=0 Radius=1.3
    g78: Circle CenterX=-47 CenterY=-32 CenterZ=0 NormalX=0 NormalY=0 NormalZ=1 AngleXU=0 Radius=1.3
    g79: Circle CenterX=-52 CenterY=-32 CenterZ=0 NormalX=0 NormalY=0 NormalZ=1 AngleXU=0 Radius=1.3
    g80: Circle CenterX=-57 CenterY=-32 CenterZ=0 NormalX=0 NormalY=0 NormalZ=1 AngleXU=0 Radius=1.3
    g81: Circle CenterX=-62 CenterY=-32 CenterZ=0 NormalX=0 NormalY=0 NormalZ=1 AngleXU=0 Radius=1.3
    g82: Circle CenterX=-67 CenterY=-32 CenterZ=0 NormalX=0 NormalY=0 NormalZ=1 AngleXU=0 Radius=1.3
    g83: Circle CenterX=-72 CenterY=-32 CenterZ=0 NormalX=0 NormalY=0 NormalZ=1 AngleXU=0 Radius=1.3
    g84: Circle CenterX=-47 CenterY=-27 CenterZ=0 NormalX=0 NormalY=0 NormalZ=1 AngleXU=0 Radius=1.3
    g85: Circle CenterX=-52 CenterY=-27 CenterZ=0 NormalX=0 NormalY=0 NormalZ=1 AngleXU=0 Radius=1.3
    g86: Circle CenterX=-57 CenterY=-27 CenterZ=0 NormalX=0 NormalY=0 NormalZ=1 AngleXU=0 Radius=1.3
    g87: Circle CenterX=-62 CenterY=-27 CenterZ=0 NormalX=0 NormalY=0 NormalZ=1 AngleXU=0 Radius=1.3
    g88: Circle CenterX=-67 CenterY=-27 CenterZ=0 NormalX=0 NormalY=0 NormalZ=1 AngleXU=0 Radius=1.3
    g89: Circle CenterX=-72 CenterY=-27 CenterZ=0 NormalX=0 NormalY=0 NormalZ=1 AngleXU=0 Radius=1.3
    g90: Circle CenterX=-47 CenterY=-22 CenterZ=0 NormalX=0 NormalY=0 NormalZ=1 AngleXU=0 Radius=1.3
    g91: Circle CenterX=-52 CenterY=-22 CenterZ=0 NormalX=0 NormalY=0 NormalZ=1 AngleXU=0 Radius=1.3
    g92: Circle CenterX=-57 CenterY=-22 CenterZ=0 NormalX=0 NormalY=0 NormalZ=1 AngleXU=0 Radius=1.3
    g93: Circle CenterX=-62 CenterY=-22 CenterZ=0 NormalX=0 NormalY=0 NormalZ=1 AngleXU=0 Radius=1.3
    g94: Circle CenterX=-67 CenterY=-22 CenterZ=0 NormalX=0 NormalY=0 NormalZ=1 AngleXU=0 Radius=1.3
    g95: Circle CenterX=-72 CenterY=-22 CenterZ=0 NormalX=0 NormalY=0 NormalZ=1 AngleXU=0 Radius=1.3
    g96: Circle CenterX=-47 CenterY=-17 CenterZ=0 NormalX=0 NormalY=0 NormalZ=1 AngleXU=0 Radius=1.3
    g97: Circle CenterX=-52 CenterY=-17 CenterZ=0 NormalX=0 NormalY=0 NormalZ=1 AngleXU=0 Radius=1.3
    g98: Circle CenterX=-57 CenterY=-17 CenterZ=0 NormalX=0 NormalY=0 NormalZ=1 AngleXU=0 Radius=1.3
    g99: Circle CenterX=-62 CenterY=-17 CenterZ=0 NormalX=0 NormalY=0 NormalZ=1 AngleXU=0 Radius=1.3
    g100: Circle CenterX=-67 CenterY=-17 CenterZ=0 NormalX=0 NormalY=0 NormalZ=1 AngleXU=0 Radius=1.3
    g101: Circle CenterX=-72 CenterY=-17 CenterZ=0 NormalX=0 NormalY=0 NormalZ=1 AngleXU=0 Radius=1.3
    g102: Circle CenterX=-47 CenterY=-12 CenterZ=0 NormalX=0 NormalY=0 NormalZ=1 AngleXU=0 Radius=1.3
    g103: Circle CenterX=-52 CenterY=-12 CenterZ=0 NormalX=0 NormalY=0 NormalZ=1 AngleXU=0 Radius=1.3
    g104: Circle CenterX=-57 CenterY=-12 CenterZ=0 NormalX=0 NormalY=0 NormalZ=1 AngleXU=0 Radius=1.3
    g105: Circle CenterX=-62 CenterY=-12 CenterZ=0 NormalX=0 NormalY=0 NormalZ=1 AngleXU=0 Radius=1.3
    g106: Circle CenterX=-67 CenterY=-12 CenterZ=0 NormalX=0 NormalY=0 NormalZ=1 AngleXU=0 Radius=1.3
    g107: Circle CenterX=-72 CenterY=-12 CenterZ=0 NormalX=0 NormalY=0 NormalZ=1 AngleXU=0 Radius=1.3
    g108: Circle CenterX=-47 CenterY=-7 CenterZ=0 NormalX=0 NormalY=0 NormalZ=1 AngleXU=0 Radius=1.3
    g109: Circle CenterX=-52 CenterY=-7 CenterZ=0 NormalX=0 NormalY=0 NormalZ=1 AngleXU=0 Radius=1.3
    g110: Circle CenterX=-57 CenterY=-7 CenterZ=0 NormalX=0 NormalY=0 NormalZ=1 AngleXU=0 Radius=1.3
    g111: Circle CenterX=-62 CenterY=-7 CenterZ=0 NormalX=0 NormalY=0 NormalZ=1 AngleXU=0 Radius=1.3
    g112: Circle CenterX=-67 CenterY=-7 CenterZ=0 NormalX=0 NormalY=0 NormalZ=1 AngleXU=0 Radius=1.3
    g113: Circle CenterX=-72 CenterY=-7 CenterZ=0 NormalX=0 NormalY=0 NormalZ=1 AngleXU=0 Radius=1.3
    g114: GeomPoint X=-42 Y=-47 Z=0
    g115: Circle CenterX=-42 CenterY=-47 CenterZ=0 NormalX=0 NormalY=0 NormalZ=1 AngleXU=0 Radius=1.3
    g116: Circle CenterX=-37 CenterY=-47 CenterZ=0 NormalX=0 NormalY=0 NormalZ=1 AngleXU=0 Radius=1.3
    g117: Circle CenterX=-32 CenterY=-47 CenterZ=0 NormalX=0 NormalY=0 NormalZ=1 AngleXU=0 Radius=1.3
    g118: Circle CenterX=-27 CenterY=-47 CenterZ=0 NormalX=0 NormalY=0 NormalZ=1 AngleXU=0 Radius=1.3
    g119: Circle CenterX=-22 CenterY=-47 CenterZ=0 NormalX=0 NormalY=0 NormalZ=1 AngleXU=0 Radius=1.3
    g120: Circle CenterX=-17 CenterY=-47 CenterZ=0 NormalX=0 NormalY=0 NormalZ=1 AngleXU=0 Radius=1.3
    g121: Circle CenterX=-12 CenterY=-47 CenterZ=0 NormalX=0 NormalY=0 NormalZ=1 AngleXU=0 Radius=1.3
    g122: GeomPoint X=-42 Y=-52 Z=0
    g123: Circle CenterX=-42 CenterY=-52 CenterZ=0 NormalX=0 NormalY=0 NormalZ=1 AngleXU=0 Radius=1.3
    g124: Circle CenterX=-37 CenterY=-52 CenterZ=0 NormalX=0 NormalY=0 NormalZ=1 AngleXU=0 Radius=1.3
    g125: Circle CenterX=-32 CenterY=-52 CenterZ=0 NormalX=0 NormalY=0 NormalZ=1 AngleXU=0 Radius=1.3
    g126: Circle CenterX=-27 CenterY=-52 CenterZ=0 NormalX=0 NormalY=0 NormalZ=1 AngleXU=0 Radius=1.3
    g127: Circle CenterX=-22 CenterY=-52 CenterZ=0 NormalX=0 NormalY=0 NormalZ=1 AngleXU=0 Radius=1.3
    g128: Circle CenterX=-17 CenterY=-52 CenterZ=0 NormalX=0 NormalY=0 NormalZ=1 AngleXU=0 Radius=1.3
    g129: Circle CenterX=-12 CenterY=-52 CenterZ=0 NormalX=0 NormalY=0 NormalZ=1 AngleXU=0 Radius=1.3
    g130: GeomPoint X=-42 Y=-57 Z=0
    g131: Circle CenterX=-42 CenterY=-57 CenterZ=0 NormalX=0 NormalY=0 NormalZ=1 AngleXU=0 Radius=1.3
    g132: Circle CenterX=-37 CenterY=-57 CenterZ=0 NormalX=0 NormalY=0 NormalZ=1 AngleXU=0 Radius=1.3
    g133: Circle CenterX=-32 CenterY=-57 CenterZ=0 NormalX=0 NormalY=0 NormalZ=1 AngleXU=0 Radius=1.3
    g134: Circle CenterX=-27 CenterY=-57 CenterZ=0 NormalX=0 NormalY=0 NormalZ=1 AngleXU=0 Radius=1.3
    g135: Circle CenterX=-22 CenterY=-57 CenterZ=0 NormalX=0 NormalY=0 NormalZ=1 AngleXU=0 Radius=1.3
    g136: Circle CenterX=-17 CenterY=-57 CenterZ=0 NormalX=0 NormalY=0 NormalZ=1 AngleXU=0 Radius=1.3
    g137: Circle CenterX=-12 CenterY=-57 CenterZ=0 NormalX=0 NormalY=0 NormalZ=1 AngleXU=0 Radius=1.3
    g138: GeomPoint X=-42 Y=-62 Z=0
    g139: Circle CenterX=-42 CenterY=-62 CenterZ=0 NormalX=0 NormalY=0 NormalZ=1 AngleXU=0 Radius=1.3
    g140: Circle CenterX=-37 CenterY=-62 CenterZ=0 NormalX=0 NormalY=0 NormalZ=1 AngleXU=0 Radius=1.3
    g141: Circle CenterX=-32 CenterY=-62 CenterZ=0 NormalX=0 NormalY=0 NormalZ=1 AngleXU=0 Radius=1.3
    g142: Circle CenterX=-27 CenterY=-62 CenterZ=0 NormalX=0 NormalY=0 NormalZ=1 AngleXU=0 Radius=1.3
    g143: Circle CenterX=-22 CenterY=-62 CenterZ=0 NormalX=0 NormalY=0 NormalZ=1 AngleXU=0 Radius=1.3
    g144: Circle CenterX=-17 CenterY=-62 CenterZ=0 NormalX=0 NormalY=0 NormalZ=1 AngleXU=0 Radius=1.3
    g145: Circle CenterX=-12 CenterY=-62 CenterZ=0 NormalX=0 NormalY=0 NormalZ=1 AngleXU=0 Radius=1.3
    g146: GeomPoint X=-42 Y=-67 Z=0
    g147: Circle CenterX=-42 CenterY=-67 CenterZ=0 NormalX=0 NormalY=0 NormalZ=1 AngleXU=0 Radius=1.3
    g148: Circle CenterX=-37 CenterY=-67 CenterZ=0 NormalX=0 NormalY=0 NormalZ=1 AngleXU=0 Radius=1.3
    g149: Circle CenterX=-32 CenterY=-67 CenterZ=0 NormalX=0 NormalY=0 NormalZ=1 AngleXU=0 Radius=1.3
    g150: Circle CenterX=-27 CenterY=-67 CenterZ=0 NormalX=0 NormalY=0 NormalZ=1 AngleXU=0 Radius=1.3
    g151: Circle CenterX=-22 CenterY=-67 CenterZ=0 NormalX=0 NormalY=0 NormalZ=1 AngleXU=0 Radius=1.3
    g152: Circle CenterX=-17 CenterY=-67 CenterZ=0 NormalX=0 NormalY=0 NormalZ=1 AngleXU=0 Radius=1.3
    g153: Circle CenterX=-12 CenterY=-67 CenterZ=0 NormalX=0 NormalY=0 NormalZ=1 AngleXU=0 Radius=1.3
    g154: GeomPoint X=-42 Y=-72 Z=0
    g155: Circle CenterX=-42 CenterY=-72 CenterZ=0 NormalX=0 NormalY=0 NormalZ=1 AngleXU=0 Radius=1.3
    g156: Circle CenterX=-37 CenterY=-72 CenterZ=0 NormalX=0 NormalY=0 NormalZ=1 AngleXU=0 Radius=1.3
    g157: Circle CenterX=-32 CenterY=-72 CenterZ=0 NormalX=0 NormalY=0 NormalZ=1 AngleXU=0 Radius=1.3
    g158: Circle CenterX=-27 CenterY=-72 CenterZ=0 NormalX=0 NormalY=0 NormalZ=1 AngleXU=0 Radius=1.3
    g159: Circle CenterX=-22 CenterY=-72 CenterZ=0 NormalX=0 NormalY=0 NormalZ=1 AngleXU=0 Radius=1.3
    g160: Circle CenterX=-17 CenterY=-72 CenterZ=0 NormalX=0 NormalY=0 NormalZ=1 AngleXU=0 Radius=1.3
    g161: Circle CenterX=-12 CenterY=-72 CenterZ=0 NormalX=0 NormalY=0 NormalZ=1 AngleXU=0 Radius=1.3
    g162: GeomPoint X=-42 Y=-77 Z=0
    g163: Circle CenterX=-42 CenterY=-77 CenterZ=0 NormalX=0 NormalY=0 NormalZ=1 AngleXU=0 Radius=1.3
    g164: Circle CenterX=-37 CenterY=-77 CenterZ=0 NormalX=0 NormalY=0 NormalZ=1 AngleXU=0 Radius=1.3
    g165: Circle CenterX=-32 CenterY=-77 CenterZ=0 NormalX=0 NormalY=0 NormalZ=1 AngleXU=0 Radius=1.3
    g166: Circle CenterX=-27 CenterY=-77 CenterZ=0 NormalX=0 NormalY=0 NormalZ=1 AngleXU=0 Radius=1.3
    g167: Circle CenterX=-22 CenterY=-77 CenterZ=0 NormalX=0 NormalY=0 NormalZ=1 AngleXU=0 Radius=1.3
    g168: Circle CenterX=-17 CenterY=-77 CenterZ=0 NormalX=0 NormalY=0 NormalZ=1 AngleXU=0 Radius=1.3
    g169: Circle CenterX=-12 CenterY=-77 CenterZ=0 NormalX=0 NormalY=0 NormalZ=1 AngleXU=0 Radius=1.3
    g170: Circle CenterX=-47 CenterY=-47 CenterZ=0 NormalX=0 NormalY=0 NormalZ=1 AngleXU=0 Radius=1.3
    g171: Circle CenterX=-52 CenterY=-47 CenterZ=0 NormalX=0 NormalY=0 NormalZ=1 AngleXU=0 Radius=1.3
    g172: Circle CenterX=-57 CenterY=-47 CenterZ=0 NormalX=0 NormalY=0 NormalZ=1 AngleXU=0 Radius=1.3
    g173: Circle CenterX=-62 CenterY=-47 CenterZ=0 NormalX=0 NormalY=0 NormalZ=1 AngleXU=0 Radius=1.3
    g174: Circle CenterX=-67 CenterY=-47 CenterZ=0 NormalX=0 NormalY=0 NormalZ=1 AngleXU=0 Radius=1.3
    g175: Circle CenterX=-72 CenterY=-47 CenterZ=0 NormalX=0 NormalY=0 NormalZ=1 AngleXU=0 Radius=1.3
    g176: Circle CenterX=-47 CenterY=-52 CenterZ=0 NormalX=0 NormalY=0 NormalZ=1 AngleXU=0 Radius=1.3
    g177: Circle CenterX=-52 CenterY=-52 CenterZ=0 NormalX=0 NormalY=0 NormalZ=1 AngleXU=0 Radius=1.3
    g178: Circle CenterX=-57 CenterY=-52 CenterZ=0 NormalX=0 NormalY=0 NormalZ=1 AngleXU=0 Radius=1.3
    g179: Circle CenterX=-62 CenterY=-52 CenterZ=0 NormalX=0 NormalY=0 NormalZ=1 AngleXU=0 Radius=1.3
    g180: Circle CenterX=-67 CenterY=-52 CenterZ=0 NormalX=0 NormalY=0 NormalZ=1 AngleXU=0 Radius=1.3
    g181: Circle CenterX=-72 CenterY=-52 CenterZ=0 NormalX=0 NormalY=0 NormalZ=1 AngleXU=0 Radius=1.3
    g182: Circle CenterX=-47 CenterY=-57 CenterZ=0 NormalX=0 NormalY=0 NormalZ=1 AngleXU=0 Radius=1.3
    g183: Circle CenterX=-52 CenterY=-57 CenterZ=0 NormalX=0 NormalY=0 NormalZ=1 AngleXU=0 Radius=1.3
    g184: Circle CenterX=-57 CenterY=-57 CenterZ=0 NormalX=0 NormalY=0 NormalZ=1 AngleXU=0 Radius=1.3
    g185: Circle CenterX=-62 CenterY=-57 CenterZ=0 NormalX=0 NormalY=0 NormalZ=1 AngleXU=0 Radius=1.3
    g186: Circle CenterX=-67 CenterY=-57 CenterZ=0 NormalX=0 NormalY=0 NormalZ=1 AngleXU=0 Radius=1.3
    g187: Circle CenterX=-72 CenterY=-57 CenterZ=0 NormalX=0 NormalY=0 NormalZ=1 AngleXU=0 Radius=1.3
    g188: Circle CenterX=-47 CenterY=-62 CenterZ=0 NormalX=0 NormalY=0 NormalZ=1 AngleXU=0 Radius=1.3
    g189: Circle CenterX=-52 CenterY=-62 CenterZ=0 NormalX=0 NormalY=0 NormalZ=1 AngleXU=0 Radius=1.3
    g190: Circle CenterX=-57 CenterY=-62 CenterZ=0 NormalX=0 NormalY=0 NormalZ=1 AngleXU=0 Radius=1.3
    g191: Circle CenterX=-62 CenterY=-62 CenterZ=0 NormalX=0 NormalY=0 NormalZ=1 AngleXU=0 Radius=1.3
    g192: Circle CenterX=-67 CenterY=-62 CenterZ=0 NormalX=0 NormalY=0 NormalZ=1 AngleXU=0 Radius=1.3
    g193: Circle CenterX=-72 CenterY=-62 CenterZ=0 NormalX=0 NormalY=0 NormalZ=1 AngleXU=0 Radius=1.3
    g194: Circle CenterX=-47 CenterY=-67 CenterZ=0 NormalX=0 NormalY=0 NormalZ=1 AngleXU=0 Radius=1.3
    g195: Circle CenterX=-52 CenterY=-67 CenterZ=0 NormalX=0 NormalY=0 NormalZ=1 AngleXU=0 Radius=1.3
    g196: Circle CenterX=-57 CenterY=-67 CenterZ=0 NormalX=0 NormalY=0 NormalZ=1 AngleXU=0 Radius=1.3
    g197: Circle CenterX=-62 CenterY=-67 CenterZ=0 NormalX=0 NormalY=0 NormalZ=1 AngleXU=0 Radius=1.3
    g198: Circle CenterX=-67 CenterY=-67 CenterZ=0 NormalX=0 NormalY=0 NormalZ=1 AngleXU=0 Radius=1.3
    g199: Circle CenterX=-72 CenterY=-67 CenterZ=0 NormalX=0 NormalY=0 NormalZ=1 AngleXU=0 Radius=1.3
    g200: Circle CenterX=-47 CenterY=-72 CenterZ=0 NormalX=0 NormalY=0 NormalZ=1 AngleXU=0 Radius=1.3
    g201: Circle CenterX=-52 CenterY=-72 CenterZ=0 NormalX=0 NormalY=0 NormalZ=1 AngleXU=0 Radius=1.3
    g202: Circle CenterX=-57 CenterY=-72 CenterZ=0 NormalX=0 NormalY=0 NormalZ=1 AngleXU=0 Radius=1.3
    g203: Circle CenterX=-62 CenterY=-72 CenterZ=0 NormalX=0 NormalY=0 NormalZ=1 AngleXU=0 Radius=1.3
    g204: Circle CenterX=-67 CenterY=-72 CenterZ=0 NormalX=0 NormalY=0 NormalZ=1 AngleXU=0 Radius=1.3
    g205: Circle CenterX=-72 CenterY=-72 CenterZ=0 NormalX=0 NormalY=0 NormalZ=1 AngleXU=0 Radius=1.3
    g206: Circle CenterX=-47 CenterY=-77 CenterZ=0 NormalX=0 NormalY=0 NormalZ=1 AngleXU=0 Radius=1.3
    g207: Circle CenterX=-52 CenterY=-77 CenterZ=0 NormalX=0 NormalY=0 NormalZ=1 AngleXU=0 Radius=1.3
    g208: Circle CenterX=-57 CenterY=-77 CenterZ=0 NormalX=0 NormalY=0 NormalZ=1 AngleXU=0 Radius=1.3
    g209: Circle CenterX=-62 CenterY=-77 CenterZ=0 NormalX=0 NormalY=0 NormalZ=1 AngleXU=0 Radius=1.3
    g210: Circle CenterX=-67 CenterY=-77 CenterZ=0 NormalX=0 NormalY=0 NormalZ=1 AngleXU=0 Radius=1.3
    g211: Circle CenterX=-72 CenterY=-77 CenterZ=0 NormalX=0 NormalY=0 NormalZ=1 AngleXU=0 Radius=1.3
  constraints (215):
    c: Symmetric(g-4,g-4,g0)
    c: Symmetric(g-6,g-6,g0)
    c: Symmetric(g0,g0,g1)
    c: Diameter(g2) = 2.6
    c: Coincident(g2,g1)
    c: Diameter(g3) = 2.6
    c: Diameter(g4) = 2.6
    c: Diameter(g5) = 2.6
    c: Diameter(g6) = 2.6
    c: Diameter(g7) = 2.6
    c: Diameter(g8) = 2.6
    c: Diameter(g10) = 2.6
    c: Diameter(g18) = 2.6
    c: Diameter(g26) = 2.6
    c: Diameter(g34) = 2.6
    c: Diameter(g42) = 2.6
    c: Diameter(g50) = 2.6
    c: Diameter(g58) = 2.6
    c: Coincident(g10,g9)
    c: Coincident(g18,g17)
    c: Coincident(g26,g25)
    c: Coincident(g34,g33)
    c: Coincident(g42,g41)
    c: Coincident(g50,g49)
    c: Coincident(g58,g57)
    c: Diameter(g11) = 2.6
    c: Diameter(g19) = 2.6
    c: Diameter(g27) = 2.6
    c: Diameter(g35) = 2.6
    c: Diameter(g43) = 2.6
    c: Diameter(g51) = 2.6
    c: Diameter(g59) = 2.6
    c: Diameter(g12) = 2.6
    c: Diameter(g20) = 2.6
    c: Diameter(g28) = 2.6
    c: Diameter(g36) = 2.6
    c: Diameter(g44) = 2.6
    c: Diameter(g52) = 2.6
    c: Diameter(g60) = 2.6
    c: Diameter(g13) = 2.6
    c: Diameter(g21) = 2.6
    c: Diameter(g29) = 2.6
    c: Diameter(g37) = 2.6
    c: Diameter(g45) = 2.6
    c: Diameter(g53) = 2.6
    c: Diameter(g61) = 2.6
    c: Diameter(g14) = 2.6
    c: Diameter(g22) = 2.6
    c: Diameter(g30) = 2.6
    c: Diameter(g38) = 2.6
    c: Diameter(g46) = 2.6
    c: Diameter(g54) = 2.6
    c: Diameter(g62) = 2.6
    c: Diameter(g15) = 2.6
    c: Diameter(g23) = 2.6
    c: Diameter(g31) = 2.6
    c: Diameter(g39) = 2.6
    c: Diameter(g47) = 2.6
    c: Diameter(g55) = 2.6
    c: Diameter(g63) = 2.6
    c: Diameter(g16) = 2.6
    c: Diameter(g24) = 2.6
    c: Diameter(g32) = 2.6
    c: Diameter(g40) = 2.6
    c: Diameter(g48) = 2.6
    c: Diameter(g56) = 2.6
    c: Diameter(g64) = 2.6
    c: Symmetric(g-3,g-3,g65)
    c: Symmetric(g-5,g-5,g65)
    c: Diameter(g66) = 2.6
    c: Diameter(g67) = 2.6
    c: Diameter(g68) = 2.6
    c: Diameter(g69) = 2.6
    c: Diameter(g70) = 2.6
    c: Diameter(g71) = 2.6
    c: Diameter(g72) = 2.6
    c: Diameter(g78) = 2.6
    c: Diameter(g84) = 2.6
    c: Diameter(g90) = 2.6
    c: Diameter(g96) = 2.6
    c: Diameter(g102) = 2.6
    c: Diameter(g108) = 2.6
    c: Diameter(g73) = 2.6
    c: Diameter(g79) = 2.6
    c: Diameter(g85) = 2.6
    c: Diameter(g91) = 2.6
    c: Diameter(g97) = 2.6
    c: Diameter(g103) = 2.6
    c: Diameter(g109) = 2.6
    c: Diameter(g74) = 2.6
    c: Diameter(g80) = 2.6
    c: Diameter(g86) = 2.6
    c: Diameter(g92) = 2.6
    c: Diameter(g98) = 2.6
    c: Diameter(g104) = 2.6
    c: Diameter(g110) = 2.6
    c: Diameter(g75) = 2.6
    c: Diameter(g81) = 2.6
    c: Diameter(g87) = 2.6
    c: Diameter(g93) = 2.6
    c: Diameter(g99) = 2.6
    c: Diameter(g105) = 2.6
    c: Diameter(g111) = 2.6
    c: Diameter(g76) = 2.6
    c: Diameter(g82) = 2.6
    c: Diameter(g88) = 2.6
    c: Diameter(g94) = 2.6
    c: Diameter(g100) = 2.6
    c: Diameter(g106) = 2.6
    c: Diameter(g112) = 2.6
    c: Diameter(g77) = 2.6
    c: Diameter(g83) = 2.6
    c: Diameter(g89) = 2.6
    c: Diameter(g95) = 2.6
    c: Diameter(g101) = 2.6
    c: Diameter(g107) = 2.6
    c: Diameter(g113) = 2.6
    c: Diameter(g115) = 2.6
    c: Diameter(g123) = 2.6
    c: Diameter(g131) = 2.6
    c: Diameter(g139) = 2.6
    c: Diameter(g147) = 2.6
    c: Diameter(g155) = 2.6
    c: Diameter(g163) = 2.6
    c: Coincident(g115,g114)
    c: Coincident(g123,g122)
    c: Coincident(g131,g130)
    c: Coincident(g139,g138)
    c: Coincident(g147,g146)
    c: Coincident(g155,g154)
    c: Coincident(g163,g162)
    c: Diameter(g116) = 2.6
    c: Diameter(g124) = 2.6
    c: Diameter(g132) = 2.6
    c: Diameter(g140) = 2.6
    c: Diameter(g148) = 2.6
    c: Diameter(g156) = 2.6
    c: Diameter(g164) = 2.6
    c: Diameter(g117) = 2.6
    c: Diameter(g125) = 2.6
    c: Diameter(g133) = 2.6
    c: Diameter(g141) = 2.6
    c: Diameter(g149) = 2.6
    c: Diameter(g157) = 2.6
    c: Diameter(g165) = 2.6
    c: Diameter(g118) = 2.6
    c: Diameter(g126) = 2.6
    c: Diameter(g134) = 2.6
    c: Diameter(g142) = 2.6
    c: Diameter(g150) = 2.6
    c: Diameter(g158) = 2.6
    c: Diameter(g166) = 2.6
    c: Diameter(g119) = 2.6
    c: Diameter(g127) = 2.6
    c: Diameter(g135) = 2.6
    c: Diameter(g143) = 2.6
    c: Diameter(g151) = 2.6
    c: Diameter(g159) = 2.6
    c: Diameter(g167) = 2.6
    c: Diameter(g120) = 2.6
    c: Diameter(g128) = 2.6
    c: Diameter(g136) = 2.6
    c: Diameter(g144) = 2.6
    c: Diameter(g152) = 2.6
    c: Diameter(g160) = 2.6
    c: Diameter(g168) = 2.6
    c: Diameter(g121) = 2.6
    c: Diameter(g129) = 2.6
    c: Diameter(g137) = 2.6
    c: Diameter(g145) = 2.6
    c: Diameter(g153) = 2.6
    c: Diameter(g161) = 2.6
    c: Diameter(g169) = 2.6
    c: Diameter(g170) = 2.6
    c: Diameter(g176) = 2.6
    c: Diameter(g182) = 2.6
    c: Diameter(g188) = 2.6
    c: Diameter(g194) = 2.6
    c: Diameter(g200) = 2.6
    c: Diameter(g206) = 2.6
    c: Diameter(g171) = 2.6
    c: Diameter(g177) = 2.6
    c: Diameter(g183) = 2.6
    c: Diameter(g189) = 2.6
    c: Diameter(g195) = 2.6
    c: Diameter(g201) = 2.6
    c: Diameter(g207) = 2.6
    c: Diameter(g172) = 2.6
    c: Diameter(g178) = 2.6
    c: Diameter(g184) = 2.6
    c: Diameter(g190) = 2.6
    c: Diameter(g196) = 2.6
    c: Diameter(g202) = 2.6
    c: Diameter(g208) = 2.6
    c: Diameter(g173) = 2.6
    c: Diameter(g179) = 2.6
    c: Diameter(g185) = 2.6
    c: Diameter(g191) = 2.6
    c: Diameter(g197) = 2.6
    c: Diameter(g203) = 2.6
    c: Diameter(g209) = 2.6
    c: Diameter(g174) = 2.6
    c: Diameter(g180) = 2.6
    c: Diameter(g186) = 2.6
    c: Diameter(g192) = 2.6
    c: Diameter(g198) = 2.6
    c: Diameter(g204) = 2.6
    c: Diameter(g210) = 2.6
    c: Diameter(g175) = 2.6
    c: Diameter(g181) = 2.6
    c: Diameter(g187) = 2.6
    c: Diameter(g193) = 2.6
    c: Diameter(g199) = 2.6
    c: Diameter(g205) = 2.6
    c: Diameter(g211) = 2.6
FEATURE [PartDesign::Pocket] Pocket012
  BaseFeature = -> Pad018
  Direction = (-2.80598e-09,0,-1)
  Length = 8
  Length2 = 5
  Placement = pos=(7.67535e-08,-84,27.3536) rot=(0,0,1;3.14159rad)
  Profile = -> Sketch034
  ReferenceAxis = -> Sketch034 [N_Axis]
  Refine = true
  Suppressed = false
  Type = 0
FEATURE [PartDesign::Body] Body008  label="M3 5mm Spaced Mounting Plate"
  AllowCompound = false
  Group = -> [DatumPlane010,CopyPocket011,Sketch032,Pad017,Sketch033,Pad018,Sketch034,Pocket012]
  Origin = -> Origin008
  Tip = -> Pocket012
FEATURE [Sketcher::SketchObject] Sketch035
  ArcFitTolerance = 1e-06
  AttachmentSupport = -> [Pad012]
  FullyConstrained = true
  MakeInternals = false
  MapMode = 5
  Placement = pos=(42.0016,5.00002,14) rot=(0.577354,0.577344,0.577354;4.18878rad)
  sketch-geometry (1):
    g0: Circle CenterX=0 CenterY=0 CenterZ=0 NormalX=0 NormalY=0 NormalZ=1 AngleXU=0 Radius=1.35
  constraints (2):
    c: Diameter(g0) = 2.7
    c: Coincident(g0,g-1)
FEATURE [PartDesign::Pocket] Pocket013
  BaseFeature = -> Pad012
  Direction = (-1.755e-05,-1,-1.0234e-10)
  Length = 5
  Length2 = 5
  Placement = pos=(42,-84,14) rot=(0.57735,-0.57735,0.57735;2.0944rad)
  Profile = -> Sketch035
  ReferenceAxis = -> Sketch035 [N_Axis]
  Refine = true
  Suppressed = false
  Type = 0
FEATURE [Sketcher::SketchObject] Sketch036
  ArcFitTolerance = 1e-06
  AttachmentSupport = -> [Pocket013]
  ExternalGeometry = -> [Pocket013]
  FullyConstrained = true
  MakeInternals = false
  MapMode = 5
  Placement = pos=(42.0016,5.00002,14) rot=(0.577354,0.577344,0.577354;4.18878rad)
  sketch-geometry (2):
    g0: Circle CenterX=0 CenterY=0 CenterZ=0 NormalX=0 NormalY=0 NormalZ=1 AngleXU=0 Radius=2.5
    g1: Circle CenterX=0 CenterY=0 CenterZ=0 NormalX=0 NormalY=0 NormalZ=1 AngleXU=0 Radius=2.9
  constraints (4):
    c: Diameter(g0) = 5
    c: Coincident(g0,g-1)
    c: Coincident(g1,g0)
    c: Tangent(g1,g-3)
FEATURE [PartDesign::Pocket] Pocket014
  BaseFeature = -> Pocket013
  Direction = (-1.755e-05,-1,-1.0234e-10)
  Length = 10
  Length2 = 5
  Placement = pos=(42,-84,14) rot=(0.57735,-0.57735,0.57735;2.0944rad)
  Profile = -> Sketch036
  ReferenceAxis = -> Sketch036 [N_Axis]
  Refine = true
  Suppressed = false
  Type = 0
FEATURE [Sketcher::SketchObject] Sketch037
  ArcFitTolerance = 1e-06
  AttachmentSupport = -> [Pocket011]
  FullyConstrained = true
  MakeInternals = false
  MapMode = 5
  Placement = pos=(84,-84,-1.80021e-08) rot=(0.707107,0,0.707107;3.14159rad)
  sketch-geometry (3):
    g0: Circle CenterX=12.3536 CenterY=-21 CenterZ=0 NormalX=0 NormalY=0 NormalZ=1 AngleXU=0 Radius=3
    g1: Circle CenterX=12.3536 CenterY=-42 CenterZ=0 NormalX=0 NormalY=0 NormalZ=1 AngleXU=0 Radius=3
    g2: Circle CenterX=12.3536 CenterY=-63 CenterZ=0 NormalX=0 NormalY=0 NormalZ=1 AngleXU=0 Radius=3
  constraints (6):
    c: Diameter(g0) = 6
    c: Coincident(g0,g-3)
    c: Diameter(g1) = 6
    c: Coincident(g1,g-4)
    c: Diameter(g2) = 6
    c: Coincident(g2,g-5)
FEATURE [PartDesign::Pocket] Pocket015
  BaseFeature = -> Pocket011
  Direction = (-1,0,2.14311e-10)
  Length = 7
  Length2 = 5
  Placement = pos=(0,-84,2e-15) rot=(1,0,0;1.5708rad)
  Profile = -> Sketch037
  ReferenceAxis = -> Sketch037 [N_Axis]
  Refine = true
  Suppressed = false
  Type = 0
FEATURE [Sketcher::SketchObject] Sketch038
  ArcFitTolerance = 1e-06
  AttachmentSupport = -> [Fillet005]
  ExternalGeometry = -> [Fillet005]
  FullyConstrained = false
  MakeInternals = false
  MapMode = 5
  Placement = pos=(0,0,0) rot=(0.707107,0,-0.707107;3.14159rad)
  sketch-geometry (332):
    g0: LineSegment [constr] StartX=-5 StartY=0 StartZ=0 EndX=-5 EndY=1 EndZ=0
    g1: LineSegment StartX=-5 StartY=1 StartZ=0 EndX=-3.00761 EndY=1.17431 EndZ=0
    g2: LineSegment StartX=-5 StartY=1 StartZ=0 EndX=-3.00761 EndY=0.825689 EndZ=0
    g3: LineSegment StartX=-3.00761 StartY=0.825689 StartZ=0 EndX=-3.00761 EndY=1.17431 EndZ=0
    g4: LineSegment [constr] StartX=-5 StartY=1 StartZ=0 EndX=-5 EndY=2 EndZ=0
    g5: LineSegment StartX=-5 StartY=2 StartZ=0 EndX=-3.00761 EndY=2.17431 EndZ=0
    g6: LineSegment StartX=-5 StartY=2 StartZ=0 EndX=-3.00761 EndY=1.82569 EndZ=0
    g7: LineSegment StartX=-3.00761 StartY=1.82569 StartZ=0 EndX=-3.00761 EndY=2.17431 EndZ=0
    g8: LineSegment [constr] StartX=-5 StartY=2 StartZ=0 EndX=-5 EndY=3 EndZ=0
    g9: LineSegment StartX=-5 StartY=3 StartZ=0 EndX=-3.00761 EndY=3.17431 EndZ=0
    g10: LineSegment StartX=-5 StartY=3 StartZ=0 EndX=-3.00761 EndY=2.82569 EndZ=0
    g11: LineSegment StartX=-3.00761 StartY=2.82569 StartZ=0 EndX=-3.00761 EndY=3.17431 EndZ=0
    g12: LineSegment [constr] StartX=-5 StartY=3 StartZ=0 EndX=-5 EndY=4 EndZ=0
    g13: LineSegment StartX=-5 StartY=4 StartZ=0 EndX=-3.00761 EndY=4.17431 EndZ=0
    g14: LineSegment StartX=-5 StartY=4 StartZ=0 EndX=-3.00761 EndY=3.82569 EndZ=0
    g15: LineSegment StartX=-3.00761 StartY=3.82569 StartZ=0 EndX=-3.00761 EndY=4.17431 EndZ=0
    g16: LineSegment [constr] StartX=-5 StartY=4 StartZ=0 EndX=-5 EndY=5 EndZ=0
    g17: LineSegment StartX=-5 StartY=5 StartZ=0 EndX=-3.00761 EndY=5.17431 EndZ=0
    g18: LineSegment StartX=-5 StartY=5 StartZ=0 EndX=-3.00761 EndY=4.82569 EndZ=0
    g19: LineSegment StartX=-3.00761 StartY=4.82569 StartZ=0 EndX=-3.00761 EndY=5.17431 EndZ=0
    g20: LineSegment [constr] StartX=-5 StartY=5 StartZ=0 EndX=-5 EndY=6 EndZ=0
    g21: LineSegment StartX=-5 StartY=6 StartZ=0 EndX=-3.00761 EndY=6.17431 EndZ=0
    g22: LineSegment StartX=-5 StartY=6 StartZ=0 EndX=-3.00761 EndY=5.82569 EndZ=0
    g23: LineSegment StartX=-3.00761 StartY=5.82569 StartZ=0 EndX=-3.00761 EndY=6.17431 EndZ=0
    g24: LineSegment [constr] StartX=-5 StartY=6 StartZ=0 EndX=-5 EndY=7 EndZ=0
    g25: LineSegment StartX=-5 StartY=7 StartZ=0 EndX=-3.00761 EndY=7.17431 EndZ=0
    g26: LineSegment StartX=-5 StartY=7 StartZ=0 EndX=-3.00761 EndY=6.82569 EndZ=0
    g27: LineSegment StartX=-3.00761 StartY=6.82569 StartZ=0 EndX=-3.00761 EndY=7.17431 EndZ=0
    g28: LineSegment [constr] StartX=-5 StartY=7 StartZ=0 EndX=-5 EndY=8 EndZ=0
    g29: LineSegment StartX=-5 StartY=8 StartZ=0 EndX=-3.00761 EndY=8.17431 EndZ=0
    g30: LineSegment StartX=-5 StartY=8 StartZ=0 EndX=-3.00761 EndY=7.82569 EndZ=0
    g31: LineSegment StartX=-3.00761 StartY=7.82569 StartZ=0 EndX=-3.00761 EndY=8.17431 EndZ=0
    g32: LineSegment [constr] StartX=-5 StartY=8 StartZ=0 EndX=-5 EndY=9 EndZ=0
    g33: LineSegment StartX=-5 StartY=9 StartZ=0 EndX=-3.00761 EndY=9.17431 EndZ=0
    g34: LineSegment StartX=-5 StartY=9 StartZ=0 EndX=-3.00761 EndY=8.82569 EndZ=0
    g35: LineSegment StartX=-3.00761 StartY=8.82569 StartZ=0 EndX=-3.00761 EndY=9.17431 EndZ=0
    g36: LineSegment [constr] StartX=-5 StartY=9 StartZ=0 EndX=-5 EndY=10 EndZ=0
    g37: LineSegment StartX=-5 StartY=10 StartZ=0 EndX=-3.00761 EndY=10.1743 EndZ=0
    g38: LineSegment StartX=-5 StartY=10 StartZ=0 EndX=-3.00761 EndY=9.82569 EndZ=0
    g39: LineSegment StartX=-3.00761 StartY=9.82569 StartZ=0 EndX=-3.00761 EndY=10.1743 EndZ=0
    g40: LineSegment [constr] StartX=-5 StartY=10 StartZ=0 EndX=-5 EndY=11 EndZ=0
    g41: LineSegment StartX=-5 StartY=11 StartZ=0 EndX=-3.00761 EndY=11.1743 EndZ=0
    g42: LineSegment StartX=-5 StartY=11 StartZ=0 EndX=-3.00761 EndY=10.8257 EndZ=0
    g43: LineSegment StartX=-3.00761 StartY=10.8257 StartZ=0 EndX=-3.00761 EndY=11.1743 EndZ=0
    g44: LineSegment [constr] StartX=-5 StartY=11 StartZ=0 EndX=-5 EndY=12 EndZ=0
    g45: LineSegment StartX=-5 StartY=12 StartZ=0 EndX=-3.00761 EndY=12.1743 EndZ=0
    g46: LineSegment StartX=-5 StartY=12 StartZ=0 EndX=-3.00761 EndY=11.8257 EndZ=0
    g47: LineSegment StartX=-3.00761 StartY=11.8257 StartZ=0 EndX=-3.00761 EndY=12.1743 EndZ=0
    g48: LineSegment [constr] StartX=-5 StartY=12 StartZ=0 EndX=-5 EndY=13 EndZ=0
    g49: LineSegment StartX=-5 StartY=13 StartZ=0 EndX=-3.00761 EndY=13.1743 EndZ=0
    g50: LineSegment StartX=-5 StartY=13 StartZ=0 EndX=-3.00761 EndY=12.8257 EndZ=0
    g51: LineSegment StartX=-3.00761 StartY=12.8257 StartZ=0 EndX=-3.00761 EndY=13.1743 EndZ=0
    g52: LineSegment [constr] StartX=-5 StartY=13 StartZ=0 EndX=-5 EndY=14 EndZ=0
    g53: LineSegment StartX=-5 StartY=14 StartZ=0 EndX=-3.00761 EndY=14.1743 EndZ=0
    g54: LineSegment StartX=-5 StartY=14 StartZ=0 EndX=-3.00761 EndY=13.8257 EndZ=0
    g55: LineSegment StartX=-3.00761 StartY=13.8257 StartZ=0 EndX=-3.00761 EndY=14.1743 EndZ=0
    g56: LineSegment [constr] StartX=-5 StartY=14 StartZ=0 EndX=-5 EndY=15 EndZ=0
    g57: LineSegment StartX=-5 StartY=15 StartZ=0 EndX=-3.00761 EndY=15.1743 EndZ=0
    g58: LineSegment StartX=-5 StartY=15 StartZ=0 EndX=-3.00761 EndY=14.8257 EndZ=0
    g59: LineSegment StartX=-3.00761 StartY=14.8257 StartZ=0 EndX=-3.00761 EndY=15.1743 EndZ=0
    g60: LineSegment [constr] StartX=-5 StartY=15 StartZ=0 EndX=-5 EndY=16 EndZ=0
    g61: LineSegment StartX=-5 StartY=16 StartZ=0 EndX=-3.00761 EndY=16.1743 EndZ=0
    g62: LineSegment StartX=-5 StartY=16 StartZ=0 EndX=-3.00761 EndY=15.8257 EndZ=0
    g63: LineSegment StartX=-3.00761 StartY=15.8257 StartZ=0 EndX=-3.00761 EndY=16.1743 EndZ=0
    g64: LineSegment [constr] StartX=-5 StartY=16 StartZ=0 EndX=-5 EndY=17 EndZ=0
    g65: LineSegment StartX=-5 StartY=17 StartZ=0 EndX=-3.00761 EndY=17.1743 EndZ=0
    g66: LineSegment StartX=-5 StartY=17 StartZ=0 EndX=-3.00761 EndY=16.8257 EndZ=0
    g67: LineSegment StartX=-3.00761 StartY=16.8257 StartZ=0 EndX=-3.00761 EndY=17.1743 EndZ=0
    g68: LineSegment [constr] StartX=-5 StartY=17 StartZ=0 EndX=-5 EndY=18 EndZ=0
    g69: LineSegment StartX=-5 StartY=18 StartZ=0 EndX=-3.00761 EndY=18.1743 EndZ=0
    g70: LineSegment StartX=-5 StartY=18 StartZ=0 EndX=-3.00761 EndY=17.8257 EndZ=0
    g71: LineSegment StartX=-3.00761 StartY=17.8257 StartZ=0 EndX=-3.00761 EndY=18.1743 EndZ=0
    g72: LineSegment [constr] StartX=-5 StartY=18 StartZ=0 EndX=-5 EndY=19 EndZ=0
    g73: LineSegment StartX=-5 StartY=19 StartZ=0 EndX=-3.00761 EndY=19.1743 EndZ=0
    g74: LineSegment StartX=-5 StartY=19 StartZ=0 EndX=-3.00761 EndY=18.8257 EndZ=0
    g75: LineSegment StartX=-3.00761 StartY=18.8257 StartZ=0 EndX=-3.00761 EndY=19.1743 EndZ=0
    g76: LineSegment [constr] StartX=-5 StartY=19 StartZ=0 EndX=-5 EndY=20 EndZ=0
    g77: LineSegment StartX=-5 StartY=20 StartZ=0 EndX=-3.00761 EndY=20.1743 EndZ=0
    g78: LineSegment StartX=-5 StartY=20 StartZ=0 EndX=-3.00761 EndY=19.8257 EndZ=0
    g79: LineSegment StartX=-3.00761 StartY=19.8257 StartZ=0 EndX=-3.00761 EndY=20.1743 EndZ=0
    g80: LineSegment [constr] StartX=-5 StartY=20 StartZ=0 EndX=-5 EndY=21 EndZ=0
    g81: LineSegment StartX=-5 StartY=21 StartZ=0 EndX=-3.00761 EndY=21.1743 EndZ=0
    g82: LineSegment StartX=-5 StartY=21 StartZ=0 EndX=-3.00761 EndY=20.8257 EndZ=0
    g83: LineSegment StartX=-3.00761 StartY=20.8257 StartZ=0 EndX=-3.00761 EndY=21.1743 EndZ=0
    g84: LineSegment [constr] StartX=-5 StartY=21 StartZ=0 EndX=-5 EndY=22 EndZ=0
    g85: LineSegment StartX=-5 StartY=22 StartZ=0 EndX=-3.00761 EndY=22.1743 EndZ=0
    g86: LineSegment StartX=-5 StartY=22 StartZ=0 EndX=-3.00761 EndY=21.8257 EndZ=0
    g87: LineSegment StartX=-3.00761 StartY=21.8257 StartZ=0 EndX=-3.00761 EndY=22.1743 EndZ=0
    g88: LineSegment [constr] StartX=-5 StartY=22 StartZ=0 EndX=-5 EndY=23 EndZ=0
    g89: LineSegment StartX=-5 StartY=23 StartZ=0 EndX=-3.00761 EndY=23.1743 EndZ=0
    g90: LineSegment StartX=-5 StartY=23 StartZ=0 EndX=-3.00761 EndY=22.8257 EndZ=0
    g91: LineSegment StartX=-3.00761 StartY=22.8257 StartZ=0 EndX=-3.00761 EndY=23.1743 EndZ=0
    g92: LineSegment [constr] StartX=-5 StartY=23 StartZ=0 EndX=-5 EndY=24 EndZ=0
    g93: LineSegment StartX=-5 StartY=24 StartZ=0 EndX=-3.00761 EndY=24.1743 EndZ=0
    g94: LineSegment StartX=-5 StartY=24 StartZ=0 EndX=-3.00761 EndY=23.8257 EndZ=0
    g95: LineSegment StartX=-3.00761 StartY=23.8257 StartZ=0 EndX=-3.00761 EndY=24.1743 EndZ=0
    g96: LineSegment [constr] StartX=-5 StartY=24 StartZ=0 EndX=-5 EndY=25 EndZ=0
    g97: LineSegment StartX=-5 StartY=25 StartZ=0 EndX=-3.00761 EndY=25.1743 EndZ=0
    g98: LineSegment StartX=-5 StartY=25 StartZ=0 EndX=-3.00761 EndY=24.8257 EndZ=0
    g99: LineSegment StartX=-3.00761 StartY=24.8257 StartZ=0 EndX=-3.00761 EndY=25.1743 EndZ=0
    g100: LineSegment [constr] StartX=-5 StartY=25 StartZ=0 EndX=-5 EndY=26 EndZ=0
    g101: LineSegment StartX=-5 StartY=26 StartZ=0 EndX=-3.00761 EndY=26.1743 EndZ=0
    g102: LineSegment StartX=-5 StartY=26 StartZ=0 EndX=-3.00761 EndY=25.8257 EndZ=0
    g103: LineSegment StartX=-3.00761 StartY=25.8257 StartZ=0 EndX=-3.00761 EndY=26.1743 EndZ=0
    g104: LineSegment [constr] StartX=-5 StartY=26 StartZ=0 EndX=-5 EndY=27 EndZ=0
    g105: LineSegment StartX=-5 StartY=27 StartZ=0 EndX=-3.00761 EndY=27.1743 EndZ=0
    g106: LineSegment StartX=-5 StartY=27 StartZ=0 EndX=-3.00761 EndY=26.8257 EndZ=0
    g107: LineSegment StartX=-3.00761 StartY=26.8257 StartZ=0 EndX=-3.00761 EndY=27.1743 EndZ=0
    g108: LineSegment [constr] StartX=-5 StartY=27 StartZ=0 EndX=-5 EndY=28 EndZ=0
    g109: LineSegment StartX=-5 StartY=28 StartZ=0 EndX=-3.00761 EndY=28.1743 EndZ=0
    g110: LineSegment StartX=-5 StartY=28 StartZ=0 EndX=-3.00761 EndY=27.8257 EndZ=0
    g111: LineSegment StartX=-3.00761 StartY=27.8257 StartZ=0 EndX=-3.00761 EndY=28.1743 EndZ=0
    g112: LineSegment [constr] StartX=-5 StartY=28 StartZ=0 EndX=-5 EndY=29 EndZ=0
    g113: LineSegment StartX=-5 StartY=29 StartZ=0 EndX=-3.00761 EndY=29.1743 EndZ=0
    g114: LineSegment StartX=-5 StartY=29 StartZ=0 EndX=-3.00761 EndY=28.8257 EndZ=0
    g115: LineSegment StartX=-3.00761 StartY=28.8257 StartZ=0 EndX=-3.00761 EndY=29.1743 EndZ=0
    g116: LineSegment [constr] StartX=-5 StartY=29 StartZ=0 EndX=-5 EndY=30 EndZ=0
    g117: LineSegment StartX=-5 StartY=30 StartZ=0 EndX=-3.00761 EndY=30.1743 EndZ=0
    g118: LineSegment StartX=-5 StartY=30 StartZ=0 EndX=-3.00761 EndY=29.8257 EndZ=0
    g119: LineSegment StartX=-3.00761 StartY=29.8257 StartZ=0 EndX=-3.00761 EndY=30.1743 EndZ=0
    g120: LineSegment [constr] StartX=-5 StartY=30 StartZ=0 EndX=-5 EndY=31 EndZ=0
    g121: LineSegment StartX=-5 StartY=31 StartZ=0 EndX=-3.00761 EndY=31.1743 EndZ=0
    g122: LineSegment StartX=-5 StartY=31 StartZ=0 EndX=-3.00761 EndY=30.8257 EndZ=0
    g123: LineSegment StartX=-3.00761 StartY=30.8257 StartZ=0 EndX=-3.00761 EndY=31.1743 EndZ=0
    g124: LineSegment [constr] StartX=-5 StartY=31 StartZ=0 EndX=-5 EndY=32 EndZ=0
    g125: LineSegment StartX=-5 StartY=32 StartZ=0 EndX=-3.00761 EndY=32.1743 EndZ=0
    g126: LineSegment StartX=-5 StartY=32 StartZ=0 EndX=-3.00761 EndY=31.8257 EndZ=0
    g127: LineSegment StartX=-3.00761 StartY=31.8257 StartZ=0 EndX=-3.00761 EndY=32.1743 EndZ=0
    g128: LineSegment [constr] StartX=-5 StartY=32 StartZ=0 EndX=-5 EndY=33 EndZ=0
    g129: LineSegment StartX=-5 StartY=33 StartZ=0 EndX=-3.00761 EndY=33.1743 EndZ=0
    g130: LineSegment StartX=-5 StartY=33 StartZ=0 EndX=-3.00761 EndY=32.8257 EndZ=0
    g131: LineSegment StartX=-3.00761 StartY=32.8257 StartZ=0 EndX=-3.00761 EndY=33.1743 EndZ=0
    g132: LineSegment [constr] StartX=-5 StartY=33 StartZ=0 EndX=-5 EndY=34 EndZ=0
    g133: LineSegment StartX=-5 StartY=34 StartZ=0 EndX=-3.00761 EndY=34.1743 EndZ=0
    g134: LineSegment StartX=-5 StartY=34 StartZ=0 EndX=-3.00761 EndY=33.8257 EndZ=0
    g135: LineSegment StartX=-3.00761 StartY=33.8257 StartZ=0 EndX=-3.00761 EndY=34.1743 EndZ=0
    g136: LineSegment [constr] StartX=-5 StartY=34 StartZ=0 EndX=-5 EndY=35 EndZ=0
    g137: LineSegment StartX=-5 StartY=35 StartZ=0 EndX=-3.00761 EndY=35.1743 EndZ=0
    g138: LineSegment StartX=-5 StartY=35 StartZ=0 EndX=-3.00761 EndY=34.8257 EndZ=0
    g139: LineSegment StartX=-3.00761 StartY=34.8257 StartZ=0 EndX=-3.00761 EndY=35.1743 EndZ=0
    g140: LineSegment [constr] StartX=-5 StartY=35 StartZ=0 EndX=-5 EndY=36 EndZ=0
    g141: LineSegment StartX=-5 StartY=36 StartZ=0 EndX=-3.00761 EndY=36.1743 EndZ=0
    g142: LineSegment StartX=-5 StartY=36 StartZ=0 EndX=-3.00761 EndY=35.8257 EndZ=0
    g143: LineSegment StartX=-3.00761 StartY=35.8257 StartZ=0 EndX=-3.00761 EndY=36.1743 EndZ=0
    g144: LineSegment [constr] StartX=-5 StartY=36 StartZ=0 EndX=-5 EndY=37 EndZ=0
    g145: LineSegment StartX=-5 StartY=37 StartZ=0 EndX=-3.00761 EndY=37.1743 EndZ=0
    g146: LineSegment StartX=-5 StartY=37 StartZ=0 EndX=-3.00761 EndY=36.8257 EndZ=0
    g147: LineSegment StartX=-3.00761 StartY=36.8257 StartZ=0 EndX=-3.00761 EndY=37.1743 EndZ=0
    g148: LineSegment [constr] StartX=-5 StartY=37 StartZ=0 EndX=-5 EndY=38 EndZ=0
    g149: LineSegment StartX=-5 StartY=38 StartZ=0 EndX=-3.00761 EndY=38.1743 EndZ=0
    g150: LineSegment StartX=-5 StartY=38 StartZ=0 EndX=-3.00761 EndY=37.8257 EndZ=0
    g151: LineSegment StartX=-3.00761 StartY=37.8257 StartZ=0 EndX=-3.00761 EndY=38.1743 EndZ=0
    g152: LineSegment [constr] StartX=-5 StartY=38 StartZ=0 EndX=-5 EndY=39 EndZ=0
    g153: LineSegment StartX=-5 StartY=39 StartZ=0 EndX=-3.00761 EndY=39.1743 EndZ=0
    g154: LineSegment StartX=-5 StartY=39 StartZ=0 EndX=-3.00761 EndY=38.8257 EndZ=0
    g155: LineSegment StartX=-3.00761 StartY=38.8257 StartZ=0 EndX=-3.00761 EndY=39.1743 EndZ=0
    g156: LineSegment [constr] StartX=-5 StartY=39 StartZ=0 EndX=-5 EndY=40 EndZ=0
    g157: LineSegment StartX=-5 StartY=40 StartZ=0 EndX=-3.00761 EndY=40.1743 EndZ=0
    g158: LineSegment StartX=-5 StartY=40 StartZ=0 EndX=-3.00761 EndY=39.8257 EndZ=0
    g159: LineSegment StartX=-3.00761 StartY=39.8257 StartZ=0 EndX=-3.00761 EndY=40.1743 EndZ=0
    g160: LineSegment [constr] StartX=-5 StartY=40 StartZ=0 EndX=-5 EndY=41 EndZ=0
    g161: LineSegment StartX=-5 StartY=41 StartZ=0 EndX=-3.00761 EndY=41.1743 EndZ=0
    g162: LineSegment StartX=-5 StartY=41 StartZ=0 EndX=-3.00761 EndY=40.8257 EndZ=0
    g163: LineSegment StartX=-3.00761 StartY=40.8257 StartZ=0 EndX=-3.00761 EndY=41.1743 EndZ=0
    g164: LineSegment [constr] StartX=-5 StartY=41 StartZ=0 EndX=-5 EndY=42 EndZ=0
    g165: LineSegment StartX=-5 StartY=42 StartZ=0 EndX=-3.00761 EndY=42.1743 EndZ=0
    g166: LineSegment StartX=-5 StartY=42 StartZ=0 EndX=-3.00761 EndY=41.8257 EndZ=0
    g167: LineSegment StartX=-3.00761 StartY=41.8257 StartZ=0 EndX=-3.00761 EndY=42.1743 EndZ=0
    g168: LineSegment [constr] StartX=-5 StartY=42 StartZ=0 EndX=-5 EndY=43 EndZ=0
    g169: LineSegment StartX=-5 StartY=43 StartZ=0 EndX=-3.00761 EndY=43.1743 EndZ=0
    g170: LineSegment StartX=-5 StartY=43 StartZ=0 EndX=-3.00761 EndY=42.8257 EndZ=0
    g171: LineSegment StartX=-3.00761 StartY=42.8257 StartZ=0 EndX=-3.00761 EndY=43.1743 EndZ=0
    g172: LineSegment [constr] StartX=-5 StartY=43 StartZ=0 EndX=-5 EndY=44 EndZ=0
    g173: LineSegment StartX=-5 StartY=44 StartZ=0 EndX=-3.00761 EndY=44.1743 EndZ=0
    g174: LineSegment StartX=-5 StartY=44 StartZ=0 EndX=-3.00761 EndY=43.8257 EndZ=0
    g175: LineSegment StartX=-3.00761 StartY=43.8257 StartZ=0 EndX=-3.00761 EndY=44.1743 EndZ=0
    g176: LineSegment [constr] StartX=-5 StartY=44 StartZ=0 EndX=-5 EndY=45 EndZ=0
    g177: LineSegment StartX=-5 StartY=45 StartZ=0 EndX=-3.00761 EndY=45.1743 EndZ=0
    g178: LineSegment StartX=-5 StartY=45 StartZ=0 EndX=-3.00761 EndY=44.8257 EndZ=0
    g179: LineSegment StartX=-3.00761 StartY=44.8257 StartZ=0 EndX=-3.00761 EndY=45.1743 EndZ=0
    g180: LineSegment [constr] StartX=-5 StartY=45 StartZ=0 EndX=-5 EndY=46 EndZ=0
    g181: LineSegment StartX=-5 StartY=46 StartZ=0 EndX=-3.00761 EndY=46.1743 EndZ=0
    g182: LineSegment StartX=-5 StartY=46 StartZ=0 EndX=-3.00761 EndY=45.8257 EndZ=0
    g183: LineSegment StartX=-3.00761 StartY=45.8257 StartZ=0 EndX=-3.00761 EndY=46.1743 EndZ=0
    g184: LineSegment [constr] StartX=-5 StartY=46 StartZ=0 EndX=-5 EndY=47 EndZ=0
    g185: LineSegment StartX=-5 StartY=47 StartZ=0 EndX=-3.00761 EndY=47.1743 EndZ=0
    g186: LineSegment StartX=-5 StartY=47 StartZ=0 EndX=-3.00761 EndY=46.8257 EndZ=0
    g187: LineSegment StartX=-3.00761 StartY=46.8257 StartZ=0 EndX=-3.00761 EndY=47.1743 EndZ=0
    g188: LineSegment [constr] StartX=-5 StartY=47 StartZ=0 EndX=-5 EndY=48 EndZ=0
    g189: LineSegment StartX=-5 StartY=48 StartZ=0 EndX=-3.00761 EndY=48.1743 EndZ=0
    g190: LineSegment StartX=-5 StartY=48 StartZ=0 EndX=-3.00761 EndY=47.8257 EndZ=0
    g191: LineSegment StartX=-3.00761 StartY=47.8257 StartZ=0 EndX=-3.00761 EndY=48.1743 EndZ=0
    g192: LineSegment [constr] StartX=-5 StartY=48 StartZ=0 EndX=-5 EndY=49 EndZ=0
    g193: LineSegment StartX=-5 StartY=49 StartZ=0 EndX=-3.00761 EndY=49.1743 EndZ=0
    g194: LineSegment StartX=-5 StartY=49 StartZ=0 EndX=-3.00761 EndY=48.8257 EndZ=0
    g195: LineSegment StartX=-3.00761 StartY=48.8257 StartZ=0 EndX=-3.00761 EndY=49.1743 EndZ=0
    g196: LineSegment [constr] StartX=-5 StartY=49 StartZ=0 EndX=-5 EndY=50 EndZ=0
    g197: LineSegment StartX=-5 StartY=50 StartZ=0 EndX=-3.00761 EndY=50.1743 EndZ=0
    g198: LineSegment StartX=-5 StartY=50 StartZ=0 EndX=-3.00761 EndY=49.8257 EndZ=0
    g199: LineSegment StartX=-3.00761 StartY=49.8257 StartZ=0 EndX=-3.00761 EndY=50.1743 EndZ=0
    g200: LineSegment [constr] StartX=-5 StartY=50 StartZ=0 EndX=-5 EndY=51 EndZ=0
    g201: LineSegment StartX=-5 StartY=51 StartZ=0 EndX=-3.00761 EndY=51.1743 EndZ=0
    g202: LineSegment StartX=-5 StartY=51 StartZ=0 EndX=-3.00761 EndY=50.8257 EndZ=0
    g203: LineSegment StartX=-3.00761 StartY=50.8257 StartZ=0 EndX=-3.00761 EndY=51.1743 EndZ=0
    g204: LineSegment [constr] StartX=-5 StartY=51 StartZ=0 EndX=-5 EndY=52 EndZ=0
    g205: LineSegment StartX=-5 StartY=52 StartZ=0 EndX=-3.00761 EndY=52.1743 EndZ=0
    g206: LineSegment StartX=-5 StartY=52 StartZ=0 EndX=-3.00761 EndY=51.8257 EndZ=0
    g207: LineSegment StartX=-3.00761 StartY=51.8257 StartZ=0 EndX=-3.00761 EndY=52.1743 EndZ=0
    g208: LineSegment [constr] StartX=-5 StartY=52 StartZ=0 EndX=-5 EndY=53 EndZ=0
    g209: LineSegment StartX=-5 StartY=53 StartZ=0 EndX=-3.00761 EndY=53.1743 EndZ=0
    g210: LineSegment StartX=-5 StartY=53 StartZ=0 EndX=-3.00761 EndY=52.8257 EndZ=0
    g211: LineSegment StartX=-3.00761 StartY=52.8257 StartZ=0 EndX=-3.00761 EndY=53.1743 EndZ=0
    g212: LineSegment [constr] StartX=-5 StartY=53 StartZ=0 EndX=-5 EndY=54 EndZ=0
    g213: LineSegment StartX=-5 StartY=54 StartZ=0 EndX=-3.00761 EndY=54.1743 EndZ=0
    g214: LineSegment StartX=-5 StartY=54 StartZ=0 EndX=-3.00761 EndY=53.8257 EndZ=0
    g215: LineSegment StartX=-3.00761 StartY=53.8257 StartZ=0 EndX=-3.00761 EndY=54.1743 EndZ=0
    g216: LineSegment [constr] StartX=-5 StartY=54 StartZ=0 EndX=-5 EndY=55 EndZ=0
    g217: LineSegment StartX=-5 StartY=55 StartZ=0 EndX=-3.00761 EndY=55.1743 EndZ=0
    g218: LineSegment StartX=-5 StartY=55 StartZ=0 EndX=-3.00761 EndY=54.8257 EndZ=0
    g219: LineSegment StartX=-3.00761 StartY=54.8257 StartZ=0 EndX=-3.00761 EndY=55.1743 EndZ=0
    g220: LineSegment [constr] StartX=-5 StartY=55 StartZ=0 EndX=-5 EndY=56 EndZ=0
    g221: LineSegment StartX=-5 StartY=56 StartZ=0 EndX=-3.00761 EndY=56.1743 EndZ=0
    g222: LineSegment StartX=-5 StartY=56 StartZ=0 EndX=-3.00761 EndY=55.8257 EndZ=0
    g223: LineSegment StartX=-3.00761 StartY=55.8257 StartZ=0 EndX=-3.00761 EndY=56.1743 EndZ=0
    g224: LineSegment [constr] StartX=-5 StartY=56 StartZ=0 EndX=-5 EndY=57 EndZ=0
    g225: LineSegment StartX=-5 StartY=57 StartZ=0 EndX=-3.00761 EndY=57.1743 EndZ=0
    g226: LineSegment StartX=-5 StartY=57 StartZ=0 EndX=-3.00761 EndY=56.8257 EndZ=0
    g227: LineSegment StartX=-3.00761 StartY=56.8257 StartZ=0 EndX=-3.00761 EndY=57.1743 EndZ=0
    g228: LineSegment [constr] StartX=-5 StartY=57 StartZ=0 EndX=-5 EndY=58 EndZ=0
    g229: LineSegment StartX=-5 StartY=58 StartZ=0 EndX=-3.00761 EndY=58.1743 EndZ=0
    g230: LineSegment StartX=-5 StartY=58 StartZ=0 EndX=-3.00761 EndY=57.8257 EndZ=0
    g231: LineSegment StartX=-3.00761 StartY=57.8257 StartZ=0 EndX=-3.00761 EndY=58.1743 EndZ=0
    g232: LineSegment [constr] StartX=-5 StartY=58 StartZ=0 EndX=-5 EndY=59 EndZ=0
    g233: LineSegment StartX=-5 StartY=59 StartZ=0 EndX=-3.00761 EndY=59.1743 EndZ=0
    g234: LineSegment StartX=-5 StartY=59 StartZ=0 EndX=-3.00761 EndY=58.8257 EndZ=0
    g235: LineSegment StartX=-3.00761 StartY=58.8257 StartZ=0 EndX=-3.00761 EndY=59.1743 EndZ=0
    g236: LineSegment [constr] StartX=-5 StartY=59 StartZ=0 EndX=-5 EndY=60 EndZ=0
    g237: LineSegment StartX=-5 StartY=60 StartZ=0 EndX=-3.00761 EndY=60.1743 EndZ=0
    g238: LineSegment StartX=-5 StartY=60 StartZ=0 EndX=-3.00761 EndY=59.8257 EndZ=0
    g239: LineSegment StartX=-3.00761 StartY=59.8257 StartZ=0 EndX=-3.00761 EndY=60.1743 EndZ=0
    g240: LineSegment [constr] StartX=-5 StartY=60 StartZ=0 EndX=-5 EndY=61 EndZ=0
    g241: LineSegment StartX=-5 StartY=61 StartZ=0 EndX=-3.00761 EndY=61.1743 EndZ=0
    g242: LineSegment StartX=-5 StartY=61 StartZ=0 EndX=-3.00761 EndY=60.8257 EndZ=0
    g243: LineSegment StartX=-3.00761 StartY=60.8257 StartZ=0 EndX=-3.00761 EndY=61.1743 EndZ=0
    g244: LineSegment [constr] StartX=-5 StartY=61 StartZ=0 EndX=-5 EndY=62 EndZ=0
    g245: LineSegment StartX=-5 StartY=62 StartZ=0 EndX=-3.00761 EndY=62.1743 EndZ=0
    g246: LineSegment StartX=-5 StartY=62 StartZ=0 EndX=-3.00761 EndY=61.8257 EndZ=0
    g247: LineSegment StartX=-3.00761 StartY=61.8257 StartZ=0 EndX=-3.00761 EndY=62.1743 EndZ=0
    g248: LineSegment [constr] StartX=-5 StartY=62 StartZ=0 EndX=-5 EndY=63 EndZ=0
    g249: LineSegment StartX=-5 StartY=63 StartZ=0 EndX=-3.00761 EndY=63.1743 EndZ=0
    g250: LineSegment StartX=-5 StartY=63 StartZ=0 EndX=-3.00761 EndY=62.8257 EndZ=0
    g251: LineSegment StartX=-3.00761 StartY=62.8257 StartZ=0 EndX=-3.00761 EndY=63.1743 EndZ=0
    g252: LineSegment [constr] StartX=-5 StartY=63 StartZ=0 EndX=-5 EndY=64 EndZ=0
    g253: LineSegment StartX=-5 StartY=64 StartZ=0 EndX=-3.00761 EndY=64.1743 EndZ=0
    g254: LineSegment StartX=-5 StartY=64 StartZ=0 EndX=-3.00761 EndY=63.8257 EndZ=0
    g255: LineSegment StartX=-3.00761 StartY=63.8257 StartZ=0 EndX=-3.00761 EndY=64.1743 EndZ=0
    g256: LineSegment [constr] StartX=-5 StartY=64 StartZ=0 EndX=-5 EndY=65 EndZ=0
    g257: LineSegment StartX=-5 StartY=65 StartZ=0 EndX=-3.00761 EndY=65.1743 EndZ=0
    g258: LineSegment StartX=-5 StartY=65 StartZ=0 EndX=-3.00761 EndY=64.8257 EndZ=0
    g259: LineSegment StartX=-3.00761 StartY=64.8257 StartZ=0 EndX=-3.00761 EndY=65.1743 EndZ=0
    g260: LineSegment [constr] StartX=-5 StartY=65 StartZ=0 EndX=-5 EndY=66 EndZ=0
    g261: LineSegment StartX=-5 StartY=66 StartZ=0 EndX=-3.00761 EndY=66.1743 EndZ=0
    g262: LineSegment StartX=-5 StartY=66 StartZ=0 EndX=-3.00761 EndY=65.8257 EndZ=0
    g263: LineSegment StartX=-3.00761 StartY=65.8257 StartZ=0 EndX=-3.00761 EndY=66.1743 EndZ=0
    g264: LineSegment [constr] StartX=-5 StartY=66 StartZ=0 EndX=-5 EndY=67 EndZ=0
    g265: LineSegment StartX=-5 StartY=67 StartZ=0 EndX=-3.00761 EndY=67.1743 EndZ=0
    g266: LineSegment StartX=-5 StartY=67 StartZ=0 EndX=-3.00761 EndY=66.8257 EndZ=0
    g267: LineSegment StartX=-3.00761 StartY=66.8257 StartZ=0 EndX=-3.00761 EndY=67.1743 EndZ=0
    g268: LineSegment [constr] StartX=-5 StartY=67 StartZ=0 EndX=-5 EndY=68 EndZ=0
    g269: LineSegment StartX=-5 StartY=68 StartZ=0 EndX=-3.00761 EndY=68.1743 EndZ=0
    g270: LineSegment StartX=-5 StartY=68 StartZ=0 EndX=-3.00761 EndY=67.8257 EndZ=0
    g271: LineSegment StartX=-3.00761 StartY=67.8257 StartZ=0 EndX=-3.00761 EndY=68.1743 EndZ=0
    g272: LineSegment [constr] StartX=-5 StartY=68 StartZ=0 EndX=-5 EndY=69 EndZ=0
    g273: LineSegment StartX=-5 StartY=69 StartZ=0 EndX=-3.00761 EndY=69.1743 EndZ=0
    g274: LineSegment StartX=-5 StartY=69 StartZ=0 EndX=-3.00761 EndY=68.8257 EndZ=0
    g275: LineSegment StartX=-3.00761 StartY=68.8257 StartZ=0 EndX=-3.00761 EndY=69.1743 EndZ=0
    g276: LineSegment [constr] StartX=-5 StartY=69 StartZ=0 EndX=-5 EndY=70 EndZ=0
    g277: LineSegment StartX=-5 StartY=70 StartZ=0 EndX=-3.00761 EndY=70.1743 EndZ=0
    g278: LineSegment StartX=-5 StartY=70 StartZ=0 EndX=-3.00761 EndY=69.8257 EndZ=0
    g279: LineSegment StartX=-3.00761 StartY=69.8257 StartZ=0 EndX=-3.00761 EndY=70.1743 EndZ=0
    g280: LineSegment [constr] StartX=-5 StartY=70 StartZ=0 EndX=-5 EndY=71 EndZ=0
    g281: LineSegment StartX=-5 StartY=71 StartZ=0 EndX=-3.00761 EndY=71.1743 EndZ=0
    g282: LineSegment StartX=-5 StartY=71 StartZ=0 EndX=-3.00761 EndY=70.8257 EndZ=0
    g283: LineSegment StartX=-3.00761 StartY=70.8257 StartZ=0 EndX=-3.00761 EndY=71.1743 EndZ=0
    g284: LineSegment [constr] StartX=-5 StartY=71 StartZ=0 EndX=-5 EndY=72 EndZ=0
    g285: LineSegment StartX=-5 StartY=72 StartZ=0 EndX=-3.00761 EndY=72.1743 EndZ=0
    g286: LineSegment StartX=-5 StartY=72 StartZ=0 EndX=-3.00761 EndY=71.8257 EndZ=0
    g287: LineSegment StartX=-3.00761 StartY=71.8257 StartZ=0 EndX=-3.00761 EndY=72.1743 EndZ=0
    g288: LineSegment [constr] StartX=-5 StartY=72 StartZ=0 EndX=-5 EndY=73 EndZ=0
    g289: LineSegment StartX=-5 StartY=73 StartZ=0 EndX=-3.00761 EndY=73.1743 EndZ=0
    g290: LineSegment StartX=-5 StartY=73 StartZ=0 EndX=-3.00761 EndY=72.8257 EndZ=0
    g291: LineSegment StartX=-3.00761 StartY=72.8257 StartZ=0 EndX=-3.00761 EndY=73.1743 EndZ=0
    g292: LineSegment [constr] StartX=-5 StartY=73 StartZ=0 EndX=-5 EndY=74 EndZ=0
    g293: LineSegment StartX=-5 StartY=74 StartZ=0 EndX=-3.00761 EndY=74.1743 EndZ=0
    g294: LineSegment StartX=-5 StartY=74 StartZ=0 EndX=-3.00761 EndY=73.8257 EndZ=0
    g295: LineSegment StartX=-3.00761 StartY=73.8257 StartZ=0 EndX=-3.00761 EndY=74.1743 EndZ=0
    g296: LineSegment [constr] StartX=-5 StartY=74 StartZ=0 EndX=-5 EndY=75 EndZ=0
    g297: LineSegment StartX=-5 StartY=75 StartZ=0 EndX=-3.00761 EndY=75.1743 EndZ=0
    g298: LineSegment StartX=-5 StartY=75 StartZ=0 EndX=-3.00761 EndY=74.8257 EndZ=0
    g299: LineSegment StartX=-3.00761 StartY=74.8257 StartZ=0 EndX=-3.00761 EndY=75.1743 EndZ=0
    g300: LineSegment [constr] StartX=-5 StartY=75 StartZ=0 EndX=-5 EndY=76 EndZ=0
    g301: LineSegment StartX=-5 StartY=76 StartZ=0 EndX=-3.00761 EndY=76.1743 EndZ=0
    g302: LineSegment StartX=-5 StartY=76 StartZ=0 EndX=-3.00761 EndY=75.8257 EndZ=0
    g303: LineSegment StartX=-3.00761 StartY=75.8257 StartZ=0 EndX=-3.00761 EndY=76.1743 EndZ=0
    g304: LineSegment [constr] StartX=-5 StartY=76 StartZ=0 EndX=-5 EndY=77 EndZ=0
    g305: LineSegment StartX=-5 StartY=77 StartZ=0 EndX=-3.00761 EndY=77.1743 EndZ=0
    g306: LineSegment StartX=-5 StartY=77 StartZ=0 EndX=-3.00761 EndY=76.8257 EndZ=0
    g307: LineSegment StartX=-3.00761 StartY=76.8257 StartZ=0 EndX=-3.00761 EndY=77.1743 EndZ=0
    g308: LineSegment [constr] StartX=-5 StartY=77 StartZ=0 EndX=-5 EndY=78 EndZ=0
    g309: LineSegment StartX=-5 StartY=78 StartZ=0 EndX=-3.00761 EndY=78.1743 EndZ=0
    g310: LineSegment StartX=-5 StartY=78 StartZ=0 EndX=-3.00761 EndY=77.8257 EndZ=0
    g311: LineSegment StartX=-3.00761 StartY=77.8257 StartZ=0 EndX=-3.00761 EndY=78.1743 EndZ=0
    g312: LineSegment [constr] StartX=-5 StartY=78 StartZ=0 EndX=-5 EndY=79 EndZ=0
    g313: LineSegment StartX=-5 StartY=79 StartZ=0 EndX=-3.00761 EndY=79.1743 EndZ=0
    g314: LineSegment StartX=-5 StartY=79 StartZ=0 EndX=-3.00761 EndY=78.8257 EndZ=0
    g315: LineSegment StartX=-3.00761 StartY=78.8257 StartZ=0 EndX=-3.00761 EndY=79.1743 EndZ=0
    g316: LineSegment [constr] StartX=-5 StartY=79 StartZ=0 EndX=-5 EndY=80 EndZ=0
    g317: LineSegment StartX=-5 StartY=80 StartZ=0 EndX=-3.00761 EndY=80.1743 EndZ=0
    g318: LineSegment StartX=-5 StartY=80 StartZ=0 EndX=-3.00761 EndY=79.8257 EndZ=0
    g319: LineSegment StartX=-3.00761 StartY=79.8257 StartZ=0 EndX=-3.00761 EndY=80.1743 EndZ=0
    g320: LineSegment [constr] StartX=-5 StartY=80 StartZ=0 EndX=-5 EndY=81 EndZ=0
    g321: LineSegment StartX=-5 StartY=81 StartZ=0 EndX=-3.00761 EndY=81.1743 EndZ=0
    g322: LineSegment StartX=-5 StartY=81 StartZ=0 EndX=-3.00761 EndY=80.8257 EndZ=0
    g323: LineSegment StartX=-3.00761 StartY=80.8257 StartZ=0 EndX=-3.00761 EndY=81.1743 EndZ=0
    g324: LineSegment [constr] StartX=-5 StartY=81 StartZ=0 EndX=-5 EndY=82 EndZ=0
    g325: LineSegment StartX=-5 StartY=82 StartZ=0 EndX=-3.00761 EndY=82.1743 EndZ=0
    g326: LineSegment StartX=-5 StartY=82 StartZ=0 EndX=-3.00761 EndY=81.8257 EndZ=0
    g327: LineSegment StartX=-3.00761 StartY=81.8257 StartZ=0 EndX=-3.00761 EndY=82.1743 EndZ=0
    g328: LineSegment [constr] StartX=-5 StartY=82 StartZ=0 EndX=-5 EndY=83 EndZ=0
    g329: LineSegment StartX=-5 StartY=83 StartZ=0 EndX=-3.00761 EndY=83.1743 EndZ=0
    g330: LineSegment StartX=-5 StartY=83 StartZ=0 EndX=-3.00761 EndY=82.8257 EndZ=0
    g331: LineSegment StartX=-3.00761 StartY=82.8257 StartZ=0 EndX=-3.00761 EndY=83.1743 EndZ=0
  constraints (339):
    c: Distance(g0) = 1
    c: Coincident(g0,g-4)
    c: PointOnObject(g0,g-3)
    c: Distance(g1) = 2
    c: Angle(g-1,g1) = 0.0872665
    c: Coincident(g1,g0)
    c: Distance(g2) = 2
    c: Angle(g-1,g2) = -0.0872665
    c: Coincident(g2,g0)
    c: Coincident(g3,g2)
    c: Coincident(g3,g1)
    c: Coincident(g5,g4)
    c: Coincident(g9,g8)
    c: Coincident(g13,g12)
    c: Coincident(g17,g16)
    c: Coincident(g21,g20)
    c: Coincident(g25,g24)
    c: Coincident(g29,g28)
    c: Coincident(g33,g32)
    c: Coincident(g37,g36)
    c: Coincident(g41,g40)
    c: Coincident(g45,g44)
    c: Coincident(g49,g48)
    c: Coincident(g53,g52)
    c: Coincident(g57,g56)
    c: Coincident(g61,g60)
    c: Coincident(g65,g64)
    c: Coincident(g69,g68)
    c: Coincident(g73,g72)
    c: Coincident(g77,g76)
    c: Coincident(g81,g80)
    c: Coincident(g85,g84)
    c: Coincident(g89,g88)
    c: Coincident(g93,g92)
    c: Coincident(g97,g96)
    c: Coincident(g101,g100)
    c: Coincident(g105,g104)
    c: Coincident(g109,g108)
    c: Coincident(g113,g112)
    c: Coincident(g117,g116)
    c: Coincident(g121,g120)
    c: Coincident(g125,g124)
    c: Coincident(g129,g128)
    c: Coincident(g133,g132)
    c: Coincident(g137,g136)
    c: Coincident(g141,g140)
    c: Coincident(g145,g144)
    c: Coincident(g149,g148)
    c: Coincident(g153,g152)
    c: Coincident(g157,g156)
    c: Coincident(g161,g160)
    c: Coincident(g165,g164)
    c: Coincident(g169,g168)
    c: Coincident(g173,g172)
    c: Coincident(g177,g176)
    c: Coincident(g181,g180)
    c: Coincident(g185,g184)
    c: Coincident(g189,g188)
    c: Coincident(g193,g192)
    c: Coincident(g197,g196)
    c: Coincident(g201,g200)
    c: Coincident(g205,g204)
    c: Coincident(g209,g208)
    c: Coincident(g213,g212)
    c: Coincident(g217,g216)
    c: Coincident(g221,g220)
    c: Coincident(g225,g224)
    c: Coincident(g229,g228)
    c: Coincident(g233,g232)
    c: Coincident(g237,g236)
    c: Coincident(g241,g240)
    c: Coincident(g245,g244)
    c: Coincident(g249,g248)
    c: Coincident(g253,g252)
    c: Coincident(g257,g256)
    c: Coincident(g261,g260)
    c: Coincident(g265,g264)
    c: Coincident(g269,g268)
    c: Coincident(g273,g272)
    c: Coincident(g277,g276)
    c: Coincident(g281,g280)
    c: Coincident(g285,g284)
    c: Coincident(g289,g288)
    c: Coincident(g293,g292)
    c: Coincident(g297,g296)
    c: Coincident(g301,g300)
    c: Coincident(g305,g304)
    c: Coincident(g309,g308)
    c: Coincident(g313,g312)
    c: Coincident(g317,g316)
    c: Coincident(g321,g320)
    c: Coincident(g325,g324)
    c: Coincident(g329,g328)
    c: Coincident(g6,g4)
    c: Coincident(g10,g8)
    c: Coincident(g14,g12)
    c: Coincident(g18,g16)
    c: Coincident(g22,g20)
    c: Coincident(g26,g24)
    c: Coincident(g30,g28)
    c: Coincident(g34,g32)
    c: Coincident(g38,g36)
    c: Coincident(g42,g40)
    c: Coincident(g46,g44)
    c: Coincident(g50,g48)
    c: Coincident(g54,g52)
    c: Coincident(g58,g56)
    c: Coincident(g62,g60)
    c: Coincident(g66,g64)
    c: Coincident(g70,g68)
    c: Coincident(g74,g72)
    c: Coincident(g78,g76)
    c: Coincident(g82,g80)
    c: Coincident(g86,g84)
    c: Coincident(g90,g88)
    c: Coincident(g94,g92)
    c: Coincident(g98,g96)
    c: Coincident(g102,g100)
    c: Coincident(g106,g104)
    c: Coincident(g110,g108)
    c: Coincident(g114,g112)
    c: Coincident(g118,g116)
    c: Coincident(g122,g120)
    c: Coincident(g126,g124)
    c: Coincident(g130,g128)
    c: Coincident(g134,g132)
    c: Coincident(g138,g136)
    c: Coincident(g142,g140)
    c: Coincident(g146,g144)
    c: Coincident(g150,g148)
    c: Coincident(g154,g152)
    c: Coincident(g158,g156)
    c: Coincident(g162,g160)
    c: Coincident(g166,g164)
    c: Coincident(g170,g168)
    c: Coincident(g174,g172)
    c: Coincident(g178,g176)
    c: Coincident(g182,g180)
    c: Coincident(g186,g184)
    c: Coincident(g190,g188)
    c: Coincident(g194,g192)
    c: Coincident(g198,g196)
    c: Coincident(g202,g200)
    c: Coincident(g206,g204)
    c: Coincident(g210,g208)
    c: Coincident(g214,g212)
    c: Coincident(g218,g216)
    c: Coincident(g222,g220)
    c: Coincident(g226,g224)
    c: Coincident(g230,g228)
    c: Coincident(g234,g232)
    c: Coincident(g238,g236)
    c: Coincident(g242,g240)
    c: Coincident(g246,g244)
    c: Coincident(g250,g248)
    c: Coincident(g254,g252)
    c: Coincident(g258,g256)
    c: Coincident(g262,g260)
    c: Coincident(g266,g264)
    c: Coincident(g270,g268)
    c: Coincident(g274,g272)
    c: Coincident(g278,g276)
    c: Coincident(g282,g280)
    c: Coincident(g286,g284)
    c: Coincident(g290,g288)
    c: Coincident(g294,g292)
    c: Coincident(g298,g296)
    c: Coincident(g302,g300)
    c: Coincident(g306,g304)
    c: Coincident(g310,g308)
    c: Coincident(g314,g312)
    c: Coincident(g318,g316)
    c: Coincident(g322,g320)
    c: Coincident(g326,g324)
    c: Coincident(g330,g328)
    c: Coincident(g7,g6)
    c: Coincident(g11,g10)
    c: Coincident(g15,g14)
    c: Coincident(g19,g18)
    c: Coincident(g23,g22)
    c: Coincident(g27,g26)
    c: Coincident(g31,g30)
    c: Coincident(g35,g34)
    c: Coincident(g39,g38)
    c: Coincident(g43,g42)
    c: Coincident(g47,g46)
    c: Coincident(g51,g50)
    c: Coincident(g55,g54)
    c: Coincident(g59,g58)
    c: Coincident(g63,g62)
    c: Coincident(g67,g66)
    c: Coincident(g71,g70)
    c: Coincident(g75,g74)
    c: Coincident(g79,g78)
    c: Coincident(g83,g82)
    c: Coincident(g87,g86)
    c: Coincident(g91,g90)
    c: Coincident(g95,g94)
    c: Coincident(g99,g98)
    c: Coincident(g103,g102)
    c: Coincident(g107,g106)
    c: Coincident(g111,g110)
    c: Coincident(g115,g114)
    c: Coincident(g119,g118)
    c: Coincident(g123,g122)
    c: Coincident(g127,g126)
    c: Coincident(g131,g130)
    c: Coincident(g135,g134)
    c: Coincident(g139,g138)
    c: Coincident(g143,g142)
    c: Coincident(g147,g146)
    c: Coincident(g151,g150)
    c: Coincident(g155,g154)
    c: Coincident(g159,g158)
    c: Coincident(g163,g162)
    c: Coincident(g167,g166)
    c: Coincident(g171,g170)
    c: Coincident(g175,g174)
    c: Coincident(g179,g178)
    c: Coincident(g183,g182)
    c: Coincident(g187,g186)
    c: Coincident(g191,g190)
    c: Coincident(g195,g194)
    c: Coincident(g199,g198)
    c: Coincident(g203,g202)
    c: Coincident(g207,g206)
    c: Coincident(g211,g210)
    c: Coincident(g215,g214)
    c: Coincident(g219,g218)
    c: Coincident(g223,g222)
    c: Coincident(g227,g226)
    c: Coincident(g231,g230)
    c: Coincident(g235,g234)
    c: Coincident(g239,g238)
    c: Coincident(g243,g242)
    c: Coincident(g247,g246)
    c: Coincident(g251,g250)
    c: Coincident(g255,g254)
    c: Coincident(g259,g258)
    c: Coincident(g263,g262)
    c: Coincident(g267,g266)
    c: Coincident(g271,g270)
    c: Coincident(g275,g274)
    c: Coincident(g279,g278)
    c: Coincident(g283,g282)
    c: Coincident(g287,g286)
    c: Coincident(g291,g290)
    c: Coincident(g295,g294)
    c: Coincident(g299,g298)
    c: Coincident(g303,g302)
    c: Coincident(g307,g306)
    c: Coincident(g311,g310)
    c: Coincident(g315,g314)
    c: Coincident(g319,g318)
    c: Coincident(g323,g322)
    c: Coincident(g327,g326)
    c: Coincident(g331,g330)
    c: Coincident(g7,g5)
    c: Coincident(g11,g9)
    c: Coincident(g15,g13)
    c: Coincident(g19,g17)
    c: Coincident(g23,g21)
    c: Coincident(g27,g25)
    c: Coincident(g31,g29)
    c: Coincident(g35,g33)
    c: Coincident(g39,g37)
    c: Coincident(g43,g41)
    c: Coincident(g47,g45)
    c: Coincident(g51,g49)
    c: Coincident(g55,g53)
    c: Coincident(g59,g57)
    c: Coincident(g63,g61)
    c: Coincident(g67,g65)
    c: Coincident(g71,g69)
    c: Coincident(g75,g73)
    c: Coincident(g79,g77)
    c: Coincident(g83,g81)
    c: Coincident(g87,g85)
    c: Coincident(g91,g89)
    c: Coincident(g95,g93)
    c: Coincident(g99,g97)
    c: Coincident(g103,g101)
    c: Coincident(g107,g105)
    c: Coincident(g111,g109)
    c: Coincident(g115,g113)
    c: Coincident(g119,g117)
    c: Coincident(g123,g121)
    c: Coincident(g127,g125)
    c: Coincident(g131,g129)
    c: Coincident(g135,g133)
    c: Coincident(g139,g137)
    c: Coincident(g143,g141)
    c: Coincident(g147,g145)
    c: Coincident(g151,g149)
    c: Coincident(g155,g153)
    c: Coincident(g159,g157)
    c: Coincident(g163,g161)
    c: Coincident(g167,g165)
    c: Coincident(g171,g169)
    c: Coincident(g175,g173)
    c: Coincident(g179,g177)
    c: Coincident(g183,g181)
    c: Coincident(g187,g185)
    c: Coincident(g191,g189)
    c: Coincident(g195,g193)
    c: Coincident(g199,g197)
    c: Coincident(g203,g201)
    c: Coincident(g207,g205)
    c: Coincident(g211,g209)
    c: Coincident(g215,g213)
    c: Coincident(g219,g217)
    c: Coincident(g223,g221)
    c: Coincident(g227,g225)
    c: Coincident(g231,g229)
    c: Coincident(g235,g233)
    c: Coincident(g239,g237)
    c: Coincident(g243,g241)
    c: Coincident(g247,g245)
    c: Coincident(g251,g249)
    c: Coincident(g255,g253)
    c: Coincident(g259,g257)
    c: Coincident(g263,g261)
    c: Coincident(g267,g265)
    c: Coincident(g271,g269)
    c: Coincident(g275,g273)
    c: Coincident(g279,g277)
    c: Coincident(g283,g281)
    c: Coincident(g287,g285)
    c: Coincident(g291,g289)
    c: Coincident(g295,g293)
    c: Coincident(g299,g297)
    c: Coincident(g303,g301)
    c: Coincident(g307,g305)
    c: Coincident(g311,g309)
    c: Coincident(g315,g313)
    c: Coincident(g319,g317)
    c: Coincident(g323,g321)
    c: Coincident(g327,g325)
    c: Coincident(g331,g329)
FEATURE [PartDesign::Pocket] Pocket016
  BaseFeature = -> Fillet005
  Direction = (1,0,2e-16)
  Length = 0.5
  Length2 = 5
  Placement = pos=(0,0,0) rot=(1,0,0;1.5708rad)
  Profile = -> Sketch038
  ReferenceAxis = -> Sketch038 [N_Axis]
  Refine = true
  Suppressed = false
  Type = 0
FEATURE [Sketcher::SketchObject] Sketch039
  ArcFitTolerance = 1e-06
  AttachmentSupport = -> [Pocket015]
  ExternalGeometry = -> [Pocket015]
  FullyConstrained = false
  MakeInternals = false
  MapMode = 5
  Placement = pos=(-1.2282e-09,-84,2e-15) rot=(-0.707107,0,0.707107;3.14159rad)
  sketch-geometry (68):
    g0: LineSegment [constr] StartX=-5.35355 StartY=-84 StartZ=0 EndX=-5.35355 EndY=-75 EndZ=0
    g1: LineSegment StartX=-5.35355 StartY=-75 StartZ=0 EndX=-7.34594 EndY=-74.8257 EndZ=0
    g2: LineSegment StartX=-5.35355 StartY=-75 StartZ=0 EndX=-7.34594 EndY=-75.1743 EndZ=0
    g3: LineSegment StartX=-7.34594 StartY=-75.1743 StartZ=0 EndX=-7.34594 EndY=-74.8257 EndZ=0
    g4: LineSegment StartX=-5.35355 StartY=-75.9 StartZ=0 EndX=-7.34594 EndY=-75.7257 EndZ=0
    g5: LineSegment StartX=-5.35355 StartY=-75.9 StartZ=0 EndX=-7.34594 EndY=-76.0743 EndZ=0
    g6: LineSegment StartX=-7.34594 StartY=-76.0743 StartZ=0 EndX=-7.34594 EndY=-75.7257 EndZ=0
    g7: LineSegment StartX=-5.35355 StartY=-76.8 StartZ=0 EndX=-7.34594 EndY=-76.6257 EndZ=0
    g8: LineSegment StartX=-5.35355 StartY=-76.8 StartZ=0 EndX=-7.34594 EndY=-76.9743 EndZ=0
    g9: LineSegment StartX=-7.34594 StartY=-76.9743 StartZ=0 EndX=-7.34594 EndY=-76.6257 EndZ=0
    g10: LineSegment StartX=-5.35355 StartY=-77.7 StartZ=0 EndX=-7.34594 EndY=-77.5257 EndZ=0
    g11: LineSegment StartX=-5.35355 StartY=-77.7 StartZ=0 EndX=-7.34594 EndY=-77.8743 EndZ=0
    g12: LineSegment StartX=-7.34594 StartY=-77.8743 StartZ=0 EndX=-7.34594 EndY=-77.5257 EndZ=0
    g13: LineSegment StartX=-5.35355 StartY=-78.6 StartZ=0 EndX=-7.34594 EndY=-78.4257 EndZ=0
    g14: LineSegment StartX=-5.35355 StartY=-78.6 StartZ=0 EndX=-7.34594 EndY=-78.7743 EndZ=0
    g15: LineSegment StartX=-7.34594 StartY=-78.7743 StartZ=0 EndX=-7.34594 EndY=-78.4257 EndZ=0
    g16: LineSegment StartX=-5.35355 StartY=-79.5 StartZ=0 EndX=-7.34594 EndY=-79.3257 EndZ=0
    g17: LineSegment StartX=-5.35355 StartY=-79.5 StartZ=0 EndX=-7.34594 EndY=-79.6743 EndZ=0
    g18: LineSegment StartX=-7.34594 StartY=-79.6743 StartZ=0 EndX=-7.34594 EndY=-79.3257 EndZ=0
    g19: LineSegment StartX=-5.35355 StartY=-80.4 StartZ=0 EndX=-7.34594 EndY=-80.2257 EndZ=0
    g20: LineSegment StartX=-5.35355 StartY=-80.4 StartZ=0 EndX=-7.34594 EndY=-80.5743 EndZ=0
    g21: LineSegment StartX=-7.34594 StartY=-80.5743 StartZ=0 EndX=-7.34594 EndY=-80.2257 EndZ=0
    g22: LineSegment StartX=-5.35355 StartY=-81.3 StartZ=0 EndX=-7.34594 EndY=-81.1257 EndZ=0
    g23: LineSegment StartX=-5.35355 StartY=-81.3 StartZ=0 EndX=-7.34594 EndY=-81.4743 EndZ=0
    g24: LineSegment StartX=-7.34594 StartY=-81.4743 StartZ=0 EndX=-7.34594 EndY=-81.1257 EndZ=0
    g25: LineSegment StartX=-5.35355 StartY=-82.2 StartZ=0 EndX=-7.34594 EndY=-82.0257 EndZ=0
    g26: LineSegment StartX=-5.35355 StartY=-82.2 StartZ=0 EndX=-7.34594 EndY=-82.3743 EndZ=0
    g27: LineSegment StartX=-7.34594 StartY=-82.3743 StartZ=0 EndX=-7.34594 EndY=-82.0257 EndZ=0
    g28: LineSegment StartX=-5.35355 StartY=-83.1 StartZ=0 EndX=-7.34594 EndY=-82.9257 EndZ=0
    g29: LineSegment StartX=-5.35355 StartY=-83.1 StartZ=0 EndX=-7.34594 EndY=-83.2743 EndZ=0
    g30: LineSegment StartX=-7.34594 StartY=-83.2743 StartZ=0 EndX=-7.34594 EndY=-82.9257 EndZ=0
    g31: LineSegment [constr] StartX=-5.35355 StartY=0 StartZ=0 EndX=-5.35355 EndY=-9 EndZ=0
    g32: LineSegment StartX=-5.35355 StartY=-9 StartZ=0 EndX=-7.34594 EndY=-9.17431 EndZ=0
    g33: LineSegment StartX=-5.35355 StartY=-9 StartZ=0 EndX=-7.34594 EndY=-8.82569 EndZ=0
    g34: LineSegment StartX=-7.34594 StartY=-8.82569 StartZ=0 EndX=-7.34594 EndY=-9.17431 EndZ=0
    g35: LineSegment StartX=-5.35355 StartY=-8.1 StartZ=0 EndX=-7.34594 EndY=-8.27431 EndZ=0
    g36: LineSegment StartX=-5.35355 StartY=-8.1 StartZ=0 EndX=-7.34594 EndY=-7.92569 EndZ=0
    g37: LineSegment StartX=-7.34594 StartY=-7.92569 StartZ=0 EndX=-7.34594 EndY=-8.27431 EndZ=0
    g38: LineSegment StartX=-5.35355 StartY=-7.2 StartZ=0 EndX=-7.34594 EndY=-7.37431 EndZ=0
    g39: LineSegment StartX=-5.35355 StartY=-7.2 StartZ=0 EndX=-7.34594 EndY=-7.02569 EndZ=0
    g40: LineSegment StartX=-7.34594 StartY=-7.02569 StartZ=0 EndX=-7.34594 EndY=-7.37431 EndZ=0
    g41: LineSegment StartX=-5.35355 StartY=-6.3 StartZ=0 EndX=-7.34594 EndY=-6.47431 EndZ=0
    g42: LineSegment StartX=-5.35355 StartY=-6.3 StartZ=0 EndX=-7.34594 EndY=-6.12569 EndZ=0
    g43: LineSegment StartX=-7.34594 StartY=-6.12569 StartZ=0 EndX=-7.34594 EndY=-6.47431 EndZ=0
    g44: LineSegment StartX=-5.35355 StartY=-5.4 StartZ=0 EndX=-7.34594 EndY=-5.57431 EndZ=0
    g45: LineSegment StartX=-5.35355 StartY=-5.4 StartZ=0 EndX=-7.34594 EndY=-5.22569 EndZ=0
    g46: LineSegment StartX=-7.34594 StartY=-5.22569 StartZ=0 EndX=-7.34594 EndY=-5.57431 EndZ=0
    g47: LineSegment StartX=-5.35355 StartY=-4.5 StartZ=0 EndX=-7.34594 EndY=-4.67431 EndZ=0
    g48: LineSegment StartX=-5.35355 StartY=-4.5 StartZ=0 EndX=-7.34594 EndY=-4.32569 EndZ=0
    g49: LineSegment StartX=-7.34594 StartY=-4.32569 StartZ=0 EndX=-7.34594 EndY=-4.67431 EndZ=0
    g50: LineSegment StartX=-5.35355 StartY=-3.6 StartZ=0 EndX=-7.34594 EndY=-3.77431 EndZ=0
    g51: LineSegment StartX=-5.35355 StartY=-3.6 StartZ=0 EndX=-7.34594 EndY=-3.42569 EndZ=0
    g52: LineSegment StartX=-7.34594 StartY=-3.42569 StartZ=0 EndX=-7.34594 EndY=-3.77431 EndZ=0
    g53: LineSegment StartX=-5.35355 StartY=-2.7 StartZ=0 EndX=-7.34594 EndY=-2.87431 EndZ=0
    g54: LineSegment StartX=-5.35355 StartY=-2.7 StartZ=0 EndX=-7.34594 EndY=-2.52569 EndZ=0
    g55: LineSegment StartX=-7.34594 StartY=-2.52569 StartZ=0 EndX=-7.34594 EndY=-2.87431 EndZ=0
    g56: LineSegment StartX=-5.35355 StartY=-1.8 StartZ=0 EndX=-7.34594 EndY=-1.97431 EndZ=0
    g57: LineSegment StartX=-5.35355 StartY=-1.8 StartZ=0 EndX=-7.34594 EndY=-1.62569 EndZ=0
    g58: LineSegment StartX=-7.34594 StartY=-1.62569 StartZ=0 EndX=-7.34594 EndY=-1.97431 EndZ=0
    g59: LineSegment StartX=-5.35355 StartY=-0.9 StartZ=0 EndX=-7.34594 EndY=-1.07431 EndZ=0
    g60: LineSegment StartX=-5.35355 StartY=-0.9 StartZ=0 EndX=-7.34594 EndY=-0.725689 EndZ=0
    g61: LineSegment StartX=-7.34594 StartY=-0.725689 StartZ=0 EndX=-7.34594 EndY=-1.07431 EndZ=0
    g62: LineSegment StartX=-5.35355 StartY=-84 StartZ=0 EndX=-7.34594 EndY=-83.8257 EndZ=0
    g63: LineSegment StartX=-7.34594 StartY=-83.8257 StartZ=0 EndX=-7.34594 EndY=-84 EndZ=0
    g64: LineSegment StartX=-7.34594 StartY=-84 StartZ=0 EndX=-5.35355 EndY=-84 EndZ=0
    g65: LineSegment StartX=-5.35355 StartY=0 StartZ=0 EndX=-7.34594 EndY=-0.174312 EndZ=0
    g66: LineSegment StartX=-7.34594 StartY=-0.174312 StartZ=0 EndX=-7.34594 EndY=0 EndZ=0
    g67: LineSegment StartX=-7.34594 StartY=0 StartZ=0 EndX=-5.35355 EndY=0 EndZ=0
  constraints (74):
    c: Distance(g0) = 9
    c: Coincident(g0,g-4)
    c: PointOnObject(g0,g-3)
    c: Distance(g1) = 2
    c: Angle(g-1,g1) = 3.05433
    c: Coincident(g1,g0)
    c: Distance(g2) = 2
    c: Angle(g-1,g2) = -3.05433
    c: Coincident(g2,g0)
    c: Coincident(g3,g2)
    c: Coincident(g3,g1)
    c: Coincident(g6,g5)
    c: Coincident(g9,g8)
    c: Coincident(g12,g11)
    c: Coincident(g15,g14)
    c: Coincident(g18,g17)
    c: Coincident(g21,g20)
    c: Coincident(g24,g23)
    c: Coincident(g27,g26)
    c: Coincident(g30,g29)
    c: Coincident(g6,g4)
    c: Coincident(g9,g7)
    c: Coincident(g12,g10)
    c: Coincident(g15,g13)
    c: Coincident(g18,g16)
    c: Coincident(g21,g19)
    c: Coincident(g24,g22)
    c: Coincident(g27,g25)
    c: Coincident(g30,g28)
    c: Distance(g31) = 9
    c: Coincident(g31,g-3)
    c: PointOnObject(g31,g-3)
    c: Distance(g32) = 2
    c: Angle(g-1,g32) = -3.05433
    c: Coincident(g32,g31)
    c: Distance(g33) = 2
    c: Angle(g-1,g33) = 3.05433
    c: Coincident(g33,g31)
    c: Coincident(g34,g33)
    c: Coincident(g34,g32)
    c: Coincident(g37,g36)
    c: Coincident(g40,g39)
    c: Coincident(g43,g42)
    c: Coincident(g46,g45)
    c: Coincident(g49,g48)
    c: Coincident(g52,g51)
    c: Coincident(g55,g54)
    c: Coincident(g58,g57)
    c: Coincident(g61,g60)
    c: Coincident(g37,g35)
    c: Coincident(g40,g38)
    c: Coincident(g43,g41)
    c: Coincident(g46,g44)
    c: Coincident(g49,g47)
    c: Coincident(g52,g50)
    c: Coincident(g55,g53)
    c: Coincident(g58,g56)
    c: Coincident(g61,g59)
    c: Distance(g62) = 2
    c: Angle(g-1,g62) = 3.05433
    c: Coincident(g62,g0)
    c: Coincident(g63,g62)
    c: PointOnObject(g63,g-4)
    c: Vertical(g63)
    c: Coincident(g64,g63)
    c: Coincident(g64,g0)
    c: Distance(g65) = 2
    c: Angle(g-1,g65) = -3.05433
    c: Coincident(g65,g31)
    c: Coincident(g66,g65)
    c: Vertical(g66)
    c: Coincident(g67,g66)
    c: Coincident(g67,g31)
    c: Horizontal(g67)
FEATURE [PartDesign::Pocket] Pocket017
  BaseFeature = -> Pocket015
  Direction = (1,0,-2.14311e-10)
  Length = 0.5
  Length2 = 5
  Placement = pos=(0,-84,2e-15) rot=(1,0,0;1.5708rad)
  Profile = -> Sketch039
  ReferenceAxis = -> Sketch039 [N_Axis]
  Refine = true
  Suppressed = false
  Type = 0
FEATURE [Sketcher::SketchObject] Sketch040
  ArcFitTolerance = 1e-06
  AttachmentSupport = -> [Hole002]
  ExternalGeometry = -> [Hole002]
  FullyConstrained = true
  MakeInternals = false
  MapMode = 5
  Placement = pos=(3.7335e-08,0,9.85355) rot=(1,0,0;3.14159rad)
  sketch-geometry (4):
    g0: LineSegment StartX=38.7465 StartY=46.75 StartZ=0 EndX=38.7465 EndY=37.25 EndZ=0
    g1: LineSegment StartX=38.7465 StartY=37.25 StartZ=0 EndX=45.2465 EndY=37.25 EndZ=0
    g2: LineSegment StartX=45.2465 StartY=37.25 StartZ=0 EndX=45.2465 EndY=46.75 EndZ=0
    g3: LineSegment StartX=45.2465 StartY=46.75 StartZ=0 EndX=38.7465 EndY=46.75 EndZ=0
  constraints (10):
    c: Coincident(g0,g1)
    c: Coincident(g1,g2)
    c: Coincident(g2,g3)
    c: Coincident(g3,g0)
    c: Vertical(g0)
    c: Vertical(g2)
    c: Horizontal(g1)
    c: Horizontal(g3)
    c: Coincident(g0,g-5)
    c: Coincident(g1,g-6)
FEATURE [PartDesign::Pad] Pad019
  BaseFeature = -> Hole002
  Direction = (-3.78899e-09,0,-1)
  Length = 4.65
  Length2 = 10
  Profile = -> Sketch040
  ReferenceAxis = -> Sketch040 [N_Axis]
  Refine = true
  Suppressed = false
  Type = 0
FEATURE [PartDesign::Chamfer] Chamfer015
  Angle = 45
  Base = -> Pad019 [Edge6]
  BaseFeature = -> Pad019
  ChamferType = 0
  FlipDirection = false
  Refine = true
  Size = 4
  Size2 = 1
  SupportTransform = false
  Suppressed = false
  UseAllEdges = false
FEATURE [PartDesign::Chamfer] Chamfer016
  Angle = 45
  Base = -> Chamfer015 [Edge47]
  BaseFeature = -> Chamfer015
  ChamferType = 0
  FlipDirection = false
  Refine = true
  Size = 4
  Size2 = 1
  SupportTransform = false
  Suppressed = false
  UseAllEdges = false
FEATURE [Sketcher::SketchObject] Sketch041
  ArcFitTolerance = 1e-06
  AttachmentSupport = -> [Chamfer016]
  ExternalGeometry = -> [Chamfer016]
  FullyConstrained = true
  MakeInternals = false
  MapMode = 5
  Placement = pos=(0,-37.25,0) rot=(0,0.707107,0.707107;3.14159rad)
  sketch-geometry (4):
    g0: LineSegment StartX=-48.2465 StartY=20.8536 StartZ=0 EndX=-48.2465 EndY=6.85355 EndZ=0
    g1: LineSegment StartX=-48.2465 StartY=6.85355 StartZ=0 EndX=-46.2465 EndY=6.85355 EndZ=0
    g2: LineSegment StartX=-46.2465 StartY=6.85355 StartZ=0 EndX=-46.2465 EndY=20.8536 EndZ=0
    g3: LineSegment StartX=-46.2465 StartY=20.8536 StartZ=0 EndX=-48.2465 EndY=20.8536 EndZ=0
  constraints (11):
    c: Coincident(g0,g1)
    c: Coincident(g1,g2)
    c: Coincident(g2,g3)
    c: Coincident(g3,g0)
    c: Vertical(g0)
    c: Vertical(g2)
    c: Horizontal(g1)
    c: Horizontal(g3)
    c: Distance(g0,g2) = 2
    c: Distance(g1,g3) = 14
    c: Coincident(g0,g-11)
FEATURE [PartDesign::Pocket] Pocket018
  BaseFeature = -> Chamfer016
  Direction = (0,-1,2e-16)
  Length = 10
  Length2 = 5
  Profile = -> Sketch041
  ReferenceAxis = -> Sketch041 [N_Axis]
  Refine = true
  Suppressed = false
  Type = 0
FEATURE [Sketcher::SketchObject] Sketch043
  ArcFitTolerance = 1e-06
  AttachmentSupport = -> [Pocket018]
  ExternalGeometry = -> [Pocket018]
  FullyConstrained = true
  MakeInternals = false
  MapMode = 5
  Placement = pos=(0,-37.25,0) rot=(0,0.707107,0.707107;3.14159rad)
  sketch-geometry (4):
    g0: LineSegment StartX=-35.7465 StartY=20.8536 StartZ=0 EndX=-37.7465 EndY=20.8536 EndZ=0
    g1: LineSegment StartX=-37.7465 StartY=20.8536 StartZ=0 EndX=-37.7465 EndY=7.85355 EndZ=0
    g2: LineSegment StartX=-37.7465 StartY=7.85355 StartZ=0 EndX=-35.7465 EndY=7.85355 EndZ=0
    g3: LineSegment StartX=-35.7465 StartY=7.85355 StartZ=0 EndX=-35.7465 EndY=20.8536 EndZ=0
  constraints (11):
    c: Coincident(g0,g1)
    c: Coincident(g1,g2)
    c: Coincident(g2,g3)
    c: Coincident(g3,g0)
    c: Horizontal(g0)
    c: Horizontal(g2)
    c: Vertical(g1)
    c: Vertical(g3)
    c: Distance(g1,g3) = 2
    c: Distance(g0,g2) = 13
    c: Coincident(g0,g-4)
FEATURE [PartDesign::Pocket] Pocket019
  BaseFeature = -> Pocket018
  Direction = (0,-1,2e-16)
  Length = 10
  Length2 = 5
  Profile = -> Sketch043
  ReferenceAxis = -> Sketch043 [N_Axis]
  Refine = true
  Suppressed = false
  Type = 0
FEATURE [Sketcher::SketchObject] Sketch044
  ArcFitTolerance = 1e-06
  AttachmentSupport = -> [Pocket019]
  ExternalGeometry = -> [Pocket019]
  FullyConstrained = true
  MakeInternals = false
  MapMode = 5
  Placement = pos=(0,-37.25,0) rot=(0,0.707107,0.707107;3.14159rad)
  sketch-geometry (4):
    g0: LineSegment StartX=-46.2465 StartY=20.8536 StartZ=0 EndX=-54.2465 EndY=20.8536 EndZ=0
    g1: LineSegment StartX=-54.2465 StartY=20.8536 StartZ=0 EndX=-54.2465 EndY=16.8536 EndZ=0
    g2: LineSegment StartX=-46.2465 StartY=8.26777 StartZ=0 EndX=-46.2465 EndY=20.8536 EndZ=0
    g3: LineSegment StartX=-54.2465 StartY=16.8536 StartZ=0 EndX=-46.2465 EndY=8.26777 EndZ=0
  constraints (10):
    c: Distance(g0) = 8
    c: Coincident(g0,g-4)
    c: Horizontal(g0)
    c: Distance(g1) = 4
    c: Coincident(g1,g0)
    c: Vertical(g1)
    c: Coincident(g2,g0)
    c: Coincident(g3,g1)
    c: Coincident(g3,g2)
    c: Coincident(g-4,g2)
FEATURE [PartDesign::Pad] Pad020
  BaseFeature = -> Pocket019
  Direction = (0,1,-2e-16)
  Length = 9.5
  Length2 = 10
  Profile = -> Sketch044
  ReferenceAxis = -> Sketch044 [N_Axis]
  Refine = true
  Reversed = true
  Suppressed = false
  Type = 0
FEATURE [Sketcher::SketchObject] Sketch045
  ArcFitTolerance = 1e-06
  AttachmentSupport = -> [Pad020]
  ExternalGeometry = -> [Pad020]
  FullyConstrained = true
  MakeInternals = false
  MapMode = 5
  Placement = pos=(2.2e-14,-37.25,1.23e-14) rot=(0,0.707107,0.707107;3.14159rad)
  sketch-geometry (4):
    g0: LineSegment StartX=-37.7465 StartY=20.8536 StartZ=0 EndX=-29.7465 EndY=20.8536 EndZ=0
    g1: LineSegment StartX=-29.7465 StartY=20.8536 StartZ=0 EndX=-29.7465 EndY=16.8536 EndZ=0
    g2: LineSegment StartX=-29.7465 StartY=16.8536 StartZ=0 EndX=-37.7465 EndY=8.26777 EndZ=0
    g3: LineSegment StartX=-37.7465 StartY=8.26777 StartZ=0 EndX=-37.7465 EndY=20.8536 EndZ=0
  constraints (10):
    c: Distance(g0) = 8
    c: Coincident(g0,g-4)
    c: Horizontal(g0)
    c: Distance(g1) = 4
    c: Coincident(g1,g0)
    c: Vertical(g1)
    c: Coincident(g2,g1)
    c: Coincident(g2,g-6)
    c: Coincident(g3,g2)
    c: Coincident(g3,g0)
FEATURE [PartDesign::Pad] Pad021
  BaseFeature = -> Pad020
  Direction = (0,1,-2e-16)
  Length = 9.5
  Length2 = 10
  Profile = -> Sketch045
  ReferenceAxis = -> Sketch045 [N_Axis]
  Refine = true
  Reversed = true
  Suppressed = false
  Type = 0
FEATURE [Sketcher::SketchObject] Sketch046
  ArcFitTolerance = 1e-06
  AttachmentSupport = -> [Pad021]
  ExternalGeometry = -> [Pad021]
  FullyConstrained = true
  MakeInternals = false
  MapMode = 5
  Placement = pos=(8.12e-14,-37.25,0) rot=(0,0.707107,0.707107;3.14159rad)
  sketch-geometry (2):
    g0: GeomPoint [constr] X=-54.2465 Y=18.8536 Z=0
    g1: Circle CenterX=-54.2465 CenterY=18.8536 CenterZ=0 NormalX=0 NormalY=0 NormalZ=1 AngleXU=0 Radius=1
  constraints (3):
    c: Symmetric(g-3,g-3,g0)
    c: Diameter(g1) = 2
    c: Coincident(g1,g0)
FEATURE [PartDesign::Pocket] Pocket020
  BaseFeature = -> Pad021
  Direction = (2.2e-15,-1,2e-16)
  Length = 10
  Length2 = 5
  Profile = -> Sketch046
  ReferenceAxis = -> Sketch046 [N_Axis]
  Refine = true
  Suppressed = false
  Type = 0
FEATURE [Sketcher::SketchObject] Sketch047
  ArcFitTolerance = 1e-06
  AttachmentSupport = -> [Pocket020]
  ExternalGeometry = -> [Pocket020]
  FullyConstrained = true
  MakeInternals = false
  MapMode = 5
  Placement = pos=(8.12e-14,-37.25,0) rot=(0,0.707107,0.707107;3.14159rad)
  sketch-geometry (2):
    g0: GeomPoint X=-29.7465 Y=18.8536 Z=0
    g1: Circle CenterX=-29.7465 CenterY=18.8536 CenterZ=0 NormalX=0 NormalY=0 NormalZ=1 AngleXU=0 Radius=1
  constraints (3):
    c: Symmetric(g-3,g-3,g0)
    c: Diameter(g1) = 2
    c: Coincident(g1,g0)
FEATURE [PartDesign::Pocket] Pocket021
  BaseFeature = -> Pocket020
  Direction = (2.2e-15,-1,2e-16)
  Length = 11
  Length2 = 5
  Profile = -> Sketch047
  ReferenceAxis = -> Sketch047 [N_Axis]
  Refine = true
  Suppressed = false
  Type = 0
FEATURE [Sketcher::SketchObject] Sketch048
  ArcFitTolerance = 1e-06
  AttachmentSupport = -> [Pocket021]
  ExternalGeometry = -> [Pocket021]
  FullyConstrained = true
  MakeInternals = false
  MapMode = 5
  Placement = pos=(6.7647e-08,0,17.8536) rot=(0,0,1;0rad)
  sketch-geometry (1):
    g0: Circle CenterX=41.9965 CenterY=-42 CenterZ=0 NormalX=0 NormalY=0 NormalZ=1 AngleXU=0 Radius=1.35
  constraints (2):
    c: Coincident(g0,g-3)
    c: Equal(g0,g-3)
FEATURE [PartDesign::Pad] Pad022
  BaseFeature = -> Pocket021
  Direction = (3.78899e-09,0,1)
  Length = 3
  Length2 = 10
  Profile = -> Sketch048
  ReferenceAxis = -> Sketch048 [N_Axis]
  Refine = true
  Suppressed = false
  Type = 0
FEATURE [Sketcher::SketchObject] Sketch049
  ArcFitTolerance = 1e-06
  AttachmentSupport = -> [Pad022]
  ExternalGeometry = -> [Pad022]
  FullyConstrained = true
  MakeInternals = false
  MapMode = 5
  Placement = pos=(3.93837e-08,0,20.8536) rot=(0,0,1;0rad)
  sketch-geometry (8):
    g0: GeomPoint X=33.7465 Y=-37.25 Z=0
    g1: GeomPoint X=33.7465 Y=-46.75 Z=0
    g2: GeomPoint X=50.2465 Y=-46.75 Z=0
    g3: GeomPoint X=50.2465 Y=-37.25 Z=0
    g4: LineSegment [constr] StartX=33.7465 StartY=-37.25 StartZ=0 EndX=33.7465 EndY=-46.75 EndZ=0
    g5: LineSegment [constr] StartX=50.2465 StartY=-37.25 StartZ=0 EndX=50.2465 EndY=-46.75 EndZ=0
    g6: Circle CenterX=33.7465 CenterY=-42 CenterZ=0 NormalX=0 NormalY=0 NormalZ=1 AngleXU=0 Radius=1.35
    g7: Circle CenterX=50.2465 CenterY=-42 CenterZ=0 NormalX=0 NormalY=0 NormalZ=1 AngleXU=0 Radius=1.35
  constraints (12):
    c: Symmetric(g-3,g-3,g0)
    c: Symmetric(g-6,g-6,g1)
    c: Symmetric(g-5,g-5,g2)
    c: Symmetric(g-4,g-4,g3)
    c: Coincident(g4,g0)
    c: Coincident(g4,g1)
    c: Coincident(g5,g3)
    c: Coincident(g5,g2)
    c: Diameter(g6) = 2.7
    c: Symmetric(g4,g4,g6)
    c: Diameter(g7) = 2.7
    c: Symmetric(g5,g5,g7)
FEATURE [PartDesign::Pocket] Pocket022
  BaseFeature = -> Pad022
  Direction = (-1.88858e-09,0,-1)
  Length = 13
  Length2 = 5
  Profile = -> Sketch049
  ReferenceAxis = -> Sketch049 [N_Axis]
  Refine = true
  Suppressed = false
  Type = 0
FEATURE [Sketcher::SketchObject] Sketch050
  ArcFitTolerance = 1e-06
  AttachmentSupport = -> [Pocket017]
  FullyConstrained = true
  MakeInternals = false
  MapMode = 5
  Placement = pos=(7.71195e-08,-84,20.3536) rot=(1,0,0;3.14159rad)
  sketch-geometry (10):
    g0: LineSegment [constr] StartX=35.4965 StartY=-37 StartZ=0 EndX=29.6465 EndY=-37 EndZ=0
    g1: LineSegment [constr] StartX=48.4965 StartY=-37 StartZ=0 EndX=54.3465 EndY=-37 EndZ=0
    g2: LineSegment StartX=29.6465 StartY=-37 StartZ=0 EndX=29.6465 EndY=-47 EndZ=0
    g3: LineSegment StartX=29.6465 StartY=-47 StartZ=0 EndX=35.4965 EndY=-47 EndZ=0
    g4: LineSegment StartX=35.4965 StartY=-47 StartZ=0 EndX=35.4965 EndY=-37 EndZ=0
    g5: LineSegment StartX=35.4965 StartY=-37 StartZ=0 EndX=29.6465 EndY=-37 EndZ=0
    g6: LineSegment StartX=54.3465 StartY=-37 StartZ=0 EndX=48.4965 EndY=-37 EndZ=0
    g7: LineSegment StartX=48.4965 StartY=-37 StartZ=0 EndX=48.4965 EndY=-47 EndZ=0
    g8: LineSegment StartX=48.4965 StartY=-47 StartZ=0 EndX=54.3465 EndY=-47 EndZ=0
    g9: LineSegment StartX=54.3465 StartY=-47 StartZ=0 EndX=54.3465 EndY=-37 EndZ=0
  constraints (26):
    c: Distance(g0) = 5.85
    c: Coincident(g0,g-4)
    c: Horizontal(g0)
    c: Distance(g1) = 5.85
    c: Coincident(g1,g-5)
    c: Horizontal(g1)
    c: Coincident(g2,g3)
    c: Coincident(g3,g4)
    c: Coincident(g4,g5)
    c: Coincident(g5,g2)
    c: Vertical(g2)
    c: Vertical(g4)
    c: Horizontal(g3)
    c: Horizontal(g5)
    c: Coincident(g2,g0)
    c: Coincident(g3,g-6)
    c: Coincident(g6,g7)
    c: Coincident(g7,g8)
    c: Coincident(g8,g9)
    c: Coincident(g9,g6)
    c: Horizontal(g6)
    c: Horizontal(g8)
    c: Vertical(g7)
    c: Vertical(g9)
    c: Coincident(g6,g1)
    c: Coincident(g7,g-6)
FEATURE [PartDesign::Pocket] Pocket023
  BaseFeature = -> Pocket017
  Direction = (3.78899e-09,1.1e-15,1)
  Length = 0.5
  Length2 = 5
  Placement = pos=(0,-84,2e-15) rot=(1,0,0;1.5708rad)
  Profile = -> Sketch050
  ReferenceAxis = -> Sketch050 [N_Axis]
  Refine = true
  Suppressed = false
  Type = 0
FEATURE [Sketcher::SketchObject] Sketch051
  ArcFitTolerance = 1e-06
  AttachmentSupport = -> [Pocket023]
  ExternalGeometry = -> [Pocket023]
  FullyConstrained = true
  MakeInternals = false
  MapMode = 5
  Placement = pos=(7.9014e-08,-84,20.8536) rot=(1,0,0;3.14159rad)
  sketch-geometry (4):
    g0: LineSegment [constr] StartX=41.9965 StartY=-42 StartZ=0 EndX=50.2465 EndY=-42 EndZ=0
    g1: LineSegment [constr] StartX=41.9965 StartY=-42 StartZ=0 EndX=33.7465 EndY=-42 EndZ=0
    g2: Circle CenterX=33.7465 CenterY=-42 CenterZ=0 NormalX=0 NormalY=0 NormalZ=1 AngleXU=0 Radius=1.5
    g3: Circle CenterX=50.2465 CenterY=-42 CenterZ=0 NormalX=0 NormalY=0 NormalZ=1 AngleXU=0 Radius=1.5
  constraints (10):
    c: Distance(g0) = 8.25
    c: Coincident(g0,g-3)
    c: Horizontal(g0)
    c: Distance(g1) = 8.25
    c: Coincident(g1,g0)
    c: Horizontal(g1)
    c: Diameter(g2) = 3
    c: Coincident(g2,g1)
    c: Diameter(g3) = 3
    c: Coincident(g3,g0)
FEATURE [PartDesign::Pocket] Pocket024
  BaseFeature = -> Pocket023
  Direction = (3.78899e-09,1.2e-15,1)
  Length = 11
  Length2 = 5
  Placement = pos=(0,-84,2e-15) rot=(1,0,0;1.5708rad)
  Profile = -> Sketch051
  ReferenceAxis = -> Sketch051 [N_Axis]
  Refine = true
  Suppressed = false
  Type = 0
FEATURE [Sketcher::SketchObject] Sketch052
  ArcFitTolerance = 1e-06
  AttachmentSupport = -> [Pocket024]
  ExternalGeometry = -> [Pocket024]
  FullyConstrained = true
  MakeInternals = false
  MapMode = 5
  Placement = pos=(6.55296e-08,-84,23.3536) rot=(0,0,1;3.14159rad)
  sketch-geometry (2):
    g0: Circle CenterX=-41.9965 CenterY=-42 CenterZ=0 NormalX=0 NormalY=0 NormalZ=1 AngleXU=0 Radius=1.55
    g1: Circle CenterX=-41.9965 CenterY=-42 CenterZ=0 NormalX=0 NormalY=0 NormalZ=1 AngleXU=0 Radius=3
  constraints (4):
    c: Diameter(g0) = 3.1
    c: Coincident(g0,g-4)
    c: Diameter(g1) = 6
    c: Coincident(g1,g0)
FEATURE [PartDesign::Pad] Pad023
  BaseFeature = -> Pocket024
  Direction = (2.80598e-09,0,1)
  Length = 4
  Length2 = 10
  Placement = pos=(0,-84,2e-15) rot=(1,0,0;1.5708rad)
  Profile = -> Sketch052
  ReferenceAxis = -> Sketch052 [N_Axis]
  Refine = true
  Suppressed = false
  Type = 0
FEATURE [Sketcher::SketchObject] Sketch053
  ArcFitTolerance = 1e-06
  AttachmentSupport = -> [Pad023]
  ExternalGeometry = -> [Pad023]
  FullyConstrained = true
  MakeInternals = false
  MapMode = 5
  Placement = pos=(7.67535e-08,-84,27.3536) rot=(0,0,1;3.14159rad)
  sketch-geometry (2):
    g0: Circle CenterX=-50.2465 CenterY=-42 CenterZ=0 NormalX=0 NormalY=0 NormalZ=1 AngleXU=0 Radius=3
    g1: Circle CenterX=-33.7465 CenterY=-42 CenterZ=0 NormalX=0 NormalY=0 NormalZ=1 AngleXU=0 Radius=3
  constraints (4):
    c: Diameter(g0) = 6
    c: Coincident(g0,g-4)
    c: Diameter(g1) = 6
    c: Coincident(g1,g-3)
FEATURE [PartDesign::Pocket] Pocket025
  BaseFeature = -> Pad023
  Direction = (-2.80598e-09,0,-1)
  Length = 3.5
  Length2 = 5
  Placement = pos=(0,-84,2e-15) rot=(1,0,0;1.5708rad)
  Profile = -> Sketch053
  ReferenceAxis = -> Sketch053 [N_Axis]
  Refine = true
  Suppressed = false
  Type = 0
FEATURE [Sketcher::SketchObject] Sketch054
  ArcFitTolerance = 1e-06
  AttachmentSupport = -> [Pocket022]
  ExternalGeometry = -> [Pocket022]
  FullyConstrained = true
  MakeInternals = false
  MapMode = 5
  Placement = pos=(3.93837e-08,0,20.8536) rot=(0,0,1;0rad)
  sketch-geometry (8):
    g0: GeomPoint X=41.9965 Y=-37.25 Z=0
    g1: GeomPoint X=41.9965 Y=-46.75 Z=0
    g2: LineSegment [constr] StartX=41.9965 StartY=-37.25 StartZ=0 EndX=41.9965 EndY=-46.75 EndZ=0
    g3: GeomPoint [constr] X=41.9965 Y=-42 Z=0
    g4: LineSegment StartX=41.9965 StartY=-41 StartZ=0 EndX=41.1304 EndY=-42.5 EndZ=0
    g5: LineSegment StartX=41.1304 StartY=-42.5 StartZ=0 EndX=42.8625 EndY=-42.5 EndZ=0
    g6: LineSegment StartX=42.8625 StartY=-42.5 StartZ=0 EndX=41.9965 EndY=-41 EndZ=0
    g7: Circle [constr] CenterX=41.9965 CenterY=-42 CenterZ=0 NormalX=0 NormalY=0 NormalZ=1 AngleXU=0 Radius=1
  constraints (16):
    c: Symmetric(g-3,g-3,g0)
    c: Symmetric(g-4,g-4,g1)
    c: Coincident(g2,g0)
    c: Coincident(g2,g1)
    c: Symmetric(g2,g2,g3)
    c: Coincident(g4,g5)
    c: Coincident(g5,g6)
    c: Coincident(g6,g4)
    c: Equal(g4,g5)
    c: Equal(g4,g6)
    c: PointOnObject(g4,g7)
    c: PointOnObject(g5,g7)
    c: PointOnObject(g6,g7)
    c: Radius(g7) = 1
    c: Coincident(g7,g3)
    c: PointOnObject(g6,g2)
FEATURE [PartDesign::Pocket] Pocket026
  BaseFeature = -> Pocket022
  Direction = (-1.88858e-09,0,-1)
  Length = 0.5
  Length2 = 5
  Profile = -> Sketch054
  ReferenceAxis = -> Sketch054 [N_Axis]
  Refine = true
  Suppressed = false
  Type = 0
FEATURE [PartDesign::Body] Body004  label="Thread Block Modelled"
  AllowCompound = false
  Group = -> [Clone,Sketch018,Hole002,Sketch040,Pad019,Chamfer015,Chamfer016,Sketch041,Pocket018,Sketch043,Pocket019,Sketch044,Pad020,Sketch045,Pad021,Sketch046,Pocket020,Sketch047,Pocket021,Sketch048,Pad022,Sketch049,Pocket022,Sketch054,Pocket026]
  Origin = -> Origin004
  Placement = pos=(0,-23,0) rot=(0,0,1;0rad)
  Tip = -> Pocket026
FEATURE [Sketcher::SketchObject] Sketch055
  ArcFitTolerance = 1e-06
  AttachmentSupport = -> [Pocket014]
  ExternalGeometry = -> [Pocket014]
  FullyConstrained = true
  MakeInternals = false
  MapMode = 5
  Placement = pos=(42,-84,14) rot=(0.57735,0.57735,0.57735;4.18879rad)
  sketch-geometry (2):
    g0: Circle CenterX=0 CenterY=-0.03 CenterZ=0 NormalX=0 NormalY=0 NormalZ=1 AngleXU=0 Radius=3.03
    g1: Circle CenterX=0 CenterY=-0.03 CenterZ=0 NormalX=0 NormalY=0 NormalZ=1 AngleXU=0 Radius=3.75
  constraints (5):
    c: PointOnObject(g0,g-2)
    c: Tangent(g0,g-3)
    c: Diameter(g0) = 6.06
    c: Diameter(g1) = 7.5
    c: Coincident(g1,g0)
FEATURE [PartDesign::Pad] Pad024
  BaseFeature = -> Pocket014
  Direction = (0,1,0)
  Length = 21
  Length2 = 10
  Placement = pos=(42,-84,14) rot=(0.57735,-0.57735,0.57735;2.0944rad)
  Profile = -> Sketch055
  ReferenceAxis = -> Sketch055 [N_Axis]
  Refine = true
  Reversed = true
  Suppressed = false
  Type = 0
FEATURE [Sketcher::SketchObject] Sketch056
  ArcFitTolerance = 1e-06
  AttachmentSupport = -> [Pad024]
  ExternalGeometry = -> [Pad024]
  FullyConstrained = true
  MakeInternals = false
  MapMode = 5
  Placement = pos=(42,-84,14) rot=(0.57735,0.57735,0.57735;4.18879rad)
  sketch-geometry (2):
    g0: Circle CenterX=0 CenterY=0 CenterZ=0 NormalX=0 NormalY=0 NormalZ=1 AngleXU=0 Radius=2.9
    g1: Circle CenterX=0 CenterY=-0.03 CenterZ=0 NormalX=0 NormalY=0 NormalZ=1 AngleXU=0 Radius=3.75
  constraints (4):
    c: Coincident(g0,g-1)
    c: Diameter(g0) = 5.8
    c: Coincident(g1,g-3)
    c: Equal(g1,g-3)
FEATURE [PartDesign::Pocket] Pocket027
  BaseFeature = -> Pad024
  Direction = (0,-1,0)
  Length = 8
  Length2 = 5
  Placement = pos=(42,-84,14) rot=(0.57735,-0.57735,0.57735;2.0944rad)
  Profile = -> Sketch056
  ReferenceAxis = -> Sketch056 [N_Axis]
  Refine = true
  Suppressed = false
  Type = 0
FEATURE [Part::FeaturePython] BinBase  label="2u Gridfinity Base Plate"  # WARN: FeaturePython — macro-defined, semantics opaque (R4)
  BaseProfileBottomChamfer = 0.8
  BaseProfileHeight = 4.75
  BaseProfileTopChamfer = 2.15
  BaseProfileVerticalSection = 1.8
  BinBottomRadius = 0.8
  BinOuterRadius = 3.75
  BinUnit = 41.5
  BinVerticalRadius = 1.6
  CustomHeight = 42
  GridSize = 42
  HeightUnitValue = 7
  HeightUnits = 1
  MagnetHoleDepth = 2.4
  MagnetHoleDiameter = 6.5
  MagnetHoleDistanceFromEdge = 8
  MagnetHoles = true
  NonStandardHeight = false
  Placement = pos=(-72,-63,-2) rot=(0,0,1;0rad)
  ScrewHoleDepth = 6
  ScrewHoleDiameter = 3
  ScrewHoles = true
  SequentialBridgingLayerHeight = 0.2
  StackingLip = false
  StackingLipBottomChamfer = 0.7
  StackingLipTopChamfer = 1.5
  StackingLipTopLedge = 0.4
  StackingLipVerticalSection = 1.8
  Tolerance = 0.25
  TotalHeight = 7
  WallThickness = 1
  version = 0.6.0
  xGridUnits = 2
  xTotalWidth = 83.5
  yGridUnits = 2
  yTotalWidth = 83.5
FEATURE [PartDesign::ShapeBinder] CopyBinBase
  Placement = pos=(-72,-63,-2) rot=(0,0,1;0rad)
  TraceSupport = false
FEATURE [PartDesign::Plane] DatumPlane011
  AttachmentSupport = -> [CopyBinBase]
  Length = 183.02
  MapMode = 5
  Placement = pos=(-72,-63,-9) rot=(1,0,0;3.14159rad)
  ResizeMode = 0
  Width = 144.02
FEATURE [PartDesign::SubShapeBinder] Binder
  BindCopyOnChange = 0
  BindMode = 0
  ClaimChildren = false
  Context = -> Body007 [Binder.]
  Fuse = false
  MakeFace = true
  OffsetFill = false
  OffsetIntersection = false
  OffsetJoinType = 0
  OffsetOpenResult = false
  PartialLoad = false
  Refine = true
  Relative = true
  Support = -> [BinBase]
  _Version = 2
FEATURE [PartDesign::SubShapeBinder] Binder001
  BindCopyOnChange = 0
  BindMode = 0
  ClaimChildren = false
  Context = -> Body007 [Binder001.]
  Fuse = false
  MakeFace = true
  OffsetFill = false
  OffsetIntersection = false
  OffsetJoinType = 0
  OffsetOpenResult = false
  PartialLoad = false
  Refine = true
  Relative = true
  Support = -> [BinBase[Face242]]
  _Version = 2
FEATURE [PartDesign::SubShapeBinder] Binder002
  BindCopyOnChange = 0
  BindMode = 0
  ClaimChildren = false
  Context = -> Body007 [Binder002.]
  Fuse = false
  MakeFace = true
  OffsetFill = false
  OffsetIntersection = false
  OffsetJoinType = 0
  OffsetOpenResult = false
  PartialLoad = false
  Refine = true
  Relative = true
  Support = -> [BinBase[Face2]]
  _Version = 2
FEATURE [PartDesign::SubShapeBinder] Binder003
  BindCopyOnChange = 0
  BindMode = 0
  ClaimChildren = false
  Context = -> Body007 [Binder003.]
  Fuse = false
  MakeFace = true
  OffsetFill = false
  OffsetIntersection = false
  OffsetJoinType = 0
  OffsetOpenResult = false
  PartialLoad = false
  Refine = true
  Relative = true
  Support = -> [BinBase[Face236]]
  _Version = 2
FEATURE [PartDesign::SubShapeBinder] Binder004
  BindCopyOnChange = 0
  BindMode = 0
  ClaimChildren = false
  Context = -> Body007 [Binder004.]
  Fuse = false
  MakeFace = true
  OffsetFill = false
  OffsetIntersection = false
  OffsetJoinType = 0
  OffsetOpenResult = false
  PartialLoad = false
  Refine = true
  Relative = true
  Support = -> [BinBase[Face234]]
  _Version = 2
FEATURE [Sketcher::SketchObject] Sketch060
  ArcFitTolerance = 1e-06
  AttachmentSupport = -> [DatumPlane011]
  ExternalGeometry = -> [Binder004,Binder001,Binder003,Binder002]
  FullyConstrained = true
  MakeInternals = false
  MapMode = 5
  Placement = pos=(-72,-63,-9) rot=(1,0,0;3.14159rad)
  sketch-geometry (8):
    g0: Circle CenterX=80 CenterY=13 CenterZ=0 NormalX=0 NormalY=0 NormalZ=1 AngleXU=0 Radius=1.3
    g1: Circle CenterX=80 CenterY=-13 CenterZ=0 NormalX=0 NormalY=0 NormalZ=1 AngleXU=0 Radius=1.3
    g2: Circle CenterX=80 CenterY=-29 CenterZ=0 NormalX=0 NormalY=0 NormalZ=1 AngleXU=0 Radius=1.3
    g3: Circle CenterX=80 CenterY=-55 CenterZ=0 NormalX=0 NormalY=0 NormalZ=1 AngleXU=0 Radius=1.3
    g4: Circle CenterX=148 CenterY=-55 CenterZ=0 NormalX=0 NormalY=0 NormalZ=1 AngleXU=0 Radius=1.3
    g5: Circle CenterX=148 CenterY=-29 CenterZ=0 NormalX=0 NormalY=0 NormalZ=1 AngleXU=0 Radius=1.3
    g6: Circle CenterX=148 CenterY=-13 CenterZ=0 NormalX=0 NormalY=0 NormalZ=1 AngleXU=0 Radius=1.3
    g7: Circle CenterX=148 CenterY=13 CenterZ=0 NormalX=0 NormalY=0 NormalZ=1 AngleXU=0 Radius=1.3
  constraints (16):
    c: Diameter(g0) = 2.6
    c: Coincident(g0,g-3)
    c: Diameter(g1) = 2.6
    c: Coincident(g1,g-8)
    c: Diameter(g2) = 2.6
    c: Coincident(g2,g-7)
    c: Diameter(g3) = 2.6
    c: Coincident(g3,g-6)
    c: Diameter(g4) = 2.6
    c: Coincident(g4,g-5)
    c: Diameter(g5) = 2.6
    c: Coincident(g5,g-10)
    c: Diameter(g6) = 2.6
    c: Coincident(g6,g-9)
    c: Diameter(g7) = 2.6
    c: Coincident(g7,g-4)
FEATURE [Sketcher::SketchObject] Sketch061
  ArcFitTolerance = 1e-06
  AttachmentSupport = -> [Pocket016]
  ExternalGeometry = -> [Pocket016]
  FullyConstrained = true
  MakeInternals = false
  MapMode = 5
  Placement = pos=(84,0,0) rot=(0.707107,0,0.707107;3.14159rad)
  expr: Constraints[19] = VarSet.HoleDiameter
  sketch-geometry (9):
    g0: LineSegment [constr] StartX=5 StartY=84 StartZ=0 EndX=5 EndY=56 EndZ=0
    g1: LineSegment [constr] StartX=5 StartY=56 StartZ=0 EndX=5 EndY=28 EndZ=0
    g2: LineSegment [constr] StartX=5 StartY=28 StartZ=0 EndX=5 EndY=0 EndZ=0
    g3: LineSegment [constr] StartX=5 StartY=56 StartZ=0 EndX=0 EndY=56 EndZ=0
    g4: LineSegment [constr] StartX=5 StartY=28 StartZ=0 EndX=0 EndY=28 EndZ=0
    g5: GeomPoint X=2.5 Y=56 Z=0
    g6: GeomPoint X=2.5 Y=28 Z=0
    g7: Circle CenterX=2.5 CenterY=56 CenterZ=0 NormalX=0 NormalY=0 NormalZ=1 AngleXU=0 Radius=1.3
    g8: Circle CenterX=2.5 CenterY=28 CenterZ=0 NormalX=0 NormalY=0 NormalZ=1 AngleXU=0 Radius=1.3
  constraints (20):
    c: Coincident(g0,g-4)
    c: PointOnObject(g0,g-4)
    c: Coincident(g1,g0)
    c: PointOnObject(g1,g-4)
    c: Coincident(g2,g1)
    c: Coincident(g2,g-4)
    c: Equal(g0,g1)
    c: Equal(g1,g2)
    c: Coincident(g3,g0)
    c: PointOnObject(g3,g-5)
    c: Horizontal(g3)
    c: Coincident(g4,g1)
    c: PointOnObject(g4,g-5)
    c: Horizontal(g4)
    c: Symmetric(g3,g3,g5)
    c: Symmetric(g4,g4,g6)
    c: Coincident(g7,g5)
    c: Coincident(g8,g6)
    c: Equal(g7,g8)
    c: Diameter(g8) = 2.6
FEATURE [App::VarSet] VarSet
  HoleDepth = 6
  HoleDiameter = 2.6
FEATURE [PartDesign::Pocket] Pocket031
  BaseFeature = -> Pocket016
  Direction = (-1,0,2e-16)
  Length = 6
  Length2 = 5
  Placement = pos=(0,0,0) rot=(1,0,0;1.5708rad)
  Profile = -> Sketch061
  ReferenceAxis = -> Sketch061 [N_Axis]
  Refine = true
  Suppressed = false
  Type = 0
  expr: Length = VarSet.HoleDepth
FEATURE [Sketcher::SketchObject] Sketch062
  ArcFitTolerance = 1e-06
  AttachmentSupport = -> [Pocket031]
  ExternalGeometry = -> [Pocket031]
  FullyConstrained = true
  MakeInternals = false
  MapMode = 5
  Placement = pos=(0,0,0) rot=(0.707107,0,-0.707107;3.14159rad)
  expr: Constraints[19] = VarSet.HoleDiameter
  sketch-geometry (9):
    g0: LineSegment [constr] StartX=-5 StartY=84 StartZ=0 EndX=-5 EndY=56 EndZ=0
    g1: LineSegment [constr] StartX=-5 StartY=56 StartZ=0 EndX=-5 EndY=28 EndZ=0
    g2: LineSegment [constr] StartX=-5 StartY=28 StartZ=0 EndX=-5 EndY=0 EndZ=0
    g3: LineSegment [constr] StartX=-5 StartY=56 StartZ=0 EndX=0 EndY=56 EndZ=0
    g4: LineSegment [constr] StartX=-5 StartY=28 StartZ=0 EndX=0 EndY=28 EndZ=0
    g5: GeomPoint [constr] X=-2.5 Y=56 Z=0
    g6: GeomPoint [constr] X=-2.5 Y=28 Z=0
    g7: Circle CenterX=-2.5 CenterY=56 CenterZ=0 NormalX=0 NormalY=0 NormalZ=1 AngleXU=0 Radius=1.3
    g8: Circle CenterX=-2.5 CenterY=28 CenterZ=0 NormalX=0 NormalY=0 NormalZ=1 AngleXU=0 Radius=1.3
  constraints (20):
    c: Coincident(g0,g-3)
    c: Vertical(g0)
    c: Coincident(g1,g0)
    c: Vertical(g1)
    c: Coincident(g2,g1)
    c: Coincident(g2,g-5)
    c: Equal(g2,g1)
    c: Equal(g1,g0)
    c: Coincident(g3,g0)
    c: PointOnObject(g3,g-4)
    c: Horizontal(g3)
    c: Coincident(g4,g1)
    c: PointOnObject(g4,g-4)
    c: Horizontal(g4)
    c: Symmetric(g3,g3,g5)
    c: Symmetric(g4,g4,g6)
    c: Coincident(g7,g5)
    c: Coincident(g8,g6)
    c: Equal(g8,g7)
    c: Diameter(g7) = 2.6
FEATURE [PartDesign::Pocket] Pocket032
  BaseFeature = -> Pocket031
  Direction = (1,0,2e-16)
  Length = 6
  Length2 = 5
  Placement = pos=(0,0,0) rot=(1,0,0;1.5708rad)
  Profile = -> Sketch062
  ReferenceAxis = -> Sketch062 [N_Axis]
  Refine = true
  Suppressed = false
  Type = 0
  expr: Length = VarSet.HoleDepth
FEATURE [Sketcher::SketchObject] Sketch063
  ArcFitTolerance = 1e-06
  AttachmentSupport = -> [Pocket032]
  ExternalGeometry = -> [Pocket032]
  FullyConstrained = true
  MakeInternals = false
  MapMode = 5
  Placement = pos=(0,-84,0) rot=(1,0,0;1.5708rad)
  expr: Constraints[19] = VarSet.HoleDiameter
  sketch-geometry (9):
    g0: LineSegment [constr] StartX=0 StartY=5 StartZ=0 EndX=28 EndY=5 EndZ=0
    g1: LineSegment [constr] StartX=28 StartY=5 StartZ=0 EndX=56 EndY=5 EndZ=0
    g2: LineSegment [constr] StartX=56 StartY=5 StartZ=0 EndX=84 EndY=5 EndZ=0
    g3: LineSegment [constr] StartX=28 StartY=5 StartZ=0 EndX=28 EndY=0 EndZ=0
    g4: LineSegment [constr] StartX=56 StartY=5 StartZ=0 EndX=56 EndY=0 EndZ=0
    g5: GeomPoint [constr] X=28 Y=2.5 Z=0
    g6: GeomPoint [constr] X=56 Y=2.5 Z=0
    g7: Circle CenterX=28 CenterY=2.5 CenterZ=0 NormalX=0 NormalY=0 NormalZ=1 AngleXU=0 Radius=1.3
    g8: Circle CenterX=56 CenterY=2.5 CenterZ=0 NormalX=0 NormalY=0 NormalZ=1 AngleXU=0 Radius=1.3
  constraints (20):
    c: Coincident(g0,g-3)
    c: Horizontal(g0)
    c: Coincident(g1,g0)
    c: Horizontal(g1)
    c: Coincident(g2,g1)
    c: Coincident(g2,g-4)
    c: Equal(g2,g1)
    c: Equal(g1,g0)
    c: Coincident(g3,g0)
    c: PointOnObject(g3,g-5)
    c: Vertical(g3)
    c: Coincident(g4,g1)
    c: PointOnObject(g4,g-5)
    c: Vertical(g4)
    c: Symmetric(g3,g3,g5)
    c: Symmetric(g4,g4,g6)
    c: Coincident(g7,g5)
    c: Coincident(g8,g6)
    c: Equal(g7,g8)
    c: Diameter(g7) = 2.6
FEATURE [PartDesign::Pocket] Pocket033
  BaseFeature = -> Pocket032
  Direction = (0,1,-2e-16)
  Length = 6
  Length2 = 5
  Placement = pos=(0,0,0) rot=(1,0,0;1.5708rad)
  Profile = -> Sketch063
  ReferenceAxis = -> Sketch063 [N_Axis]
  Refine = true
  Suppressed = false
  Type = 0
  expr: Length = VarSet.HoleDepth
FEATURE [Sketcher::SketchObject] Sketch064
  ArcFitTolerance = 1e-06
  AttachmentSupport = -> [Pocket033]
  ExternalGeometry = -> [Pocket033]
  FullyConstrained = true
  MakeInternals = false
  MapMode = 5
  Placement = pos=(0,1.7e-15,0) rot=(-1,0,0;1.5708rad)
  expr: Constraints[19] = VarSet.HoleDiameter
  sketch-geometry (9):
    g0: LineSegment [constr] StartX=0 StartY=-5 StartZ=0 EndX=28 EndY=-5 EndZ=0
    g1: LineSegment [constr] StartX=28 StartY=-5 StartZ=0 EndX=56 EndY=-5 EndZ=0
    g2: LineSegment [constr] StartX=56 StartY=-5 StartZ=0 EndX=84 EndY=-5 EndZ=0
    g3: LineSegment [constr] StartX=28 StartY=-5 StartZ=0 EndX=28 EndY=0 EndZ=0
    g4: LineSegment [constr] StartX=56 StartY=-5 StartZ=0 EndX=56 EndY=0 EndZ=0
    g5: GeomPoint [constr] X=28 Y=-2.5 Z=0
    g6: GeomPoint [constr] X=56 Y=-2.5 Z=0
    g7: Circle CenterX=28 CenterY=-2.5 CenterZ=0 NormalX=0 NormalY=0 NormalZ=1 AngleXU=0 Radius=1.3
    g8: Circle CenterX=56 CenterY=-2.5 CenterZ=0 NormalX=0 NormalY=0 NormalZ=1 AngleXU=0 Radius=1.3
  constraints (20):
    c: Coincident(g-4,g0)
    c: Horizontal(g0)
    c: Coincident(g0,g1)
    c: Horizontal(g1)
    c: Coincident(g1,g2)
    c: Coincident(g2,g-5)
    c: Equal(g0,g1)
    c: Equal(g1,g2)
    c: Coincident(g3,g0)
    c: PointOnObject(g3,g-3)
    c: Vertical(g3)
    c: Coincident(g4,g1)
    c: PointOnObject(g4,g-3)
    c: Vertical(g4)
    c: Symmetric(g3,g3,g5)
    c: Symmetric(g4,g4,g6)
    c: Coincident(g7,g5)
    c: Coincident(g8,g6)
    c: Equal(g7,g8)
    c: Diameter(g7) = 2.6
FEATURE [PartDesign::Pocket] Pocket034
  BaseFeature = -> Pocket033
  Direction = (0,-1,-2e-16)
  Length = 6
  Length2 = 5
  Placement = pos=(0,0,0) rot=(1,0,0;1.5708rad)
  Profile = -> Sketch064
  ReferenceAxis = -> Sketch064 [N_Axis]
  Refine = true
  Suppressed = false
  Type = 0
  expr: Length = VarSet.HoleDepth
FEATURE [PartDesign::Body] Body  label="Base with Integrated Gridfinity"
  AllowCompound = false
  Group = -> [Sketch,Pad,Sketch001,Pad001,Sketch002,Hole,Sketch003,Pad002,DatumPlane,Sketch004,Pad003,DatumPlane001,Sketch005,Pad004,Chamfer,Chamfer001,Chamfer002,Chamfer003,Chamfer004,Chamfer005,Chamfer006,Chamfer007,Chamfer008,Chamfer009,Chamfer010,Chamfer011,Chamfer012,Fillet,Sketch027,Pad015,Fillet005,Sketch038,Pocket016,Sketch061,VarSet,Pocket031,Sketch062,Pocket032,Sketch063,Pocket033,Sketch064,Pocket034]
  Origin = -> Origin
  Tip = -> Pocket034
FEATURE [PartDesign::FeatureBase] Clone001
  BaseFeature = -> Body
  Suppressed = false
FEATURE [Sketcher::SketchObject] Sketch028
  ArcFitTolerance = 1e-06
  AttachmentSupport = -> [Clone001]
  ExternalGeometry = -> [Clone001]
  FullyConstrained = true
  MakeInternals = false
  MapMode = 5
  Placement = pos=(0,1.7e-15,0) rot=(0,0.707107,0.707107;3.14159rad)
  sketch-geometry (4):
    g0: LineSegment StartX=-84 StartY=0 StartZ=0 EndX=-84 EndY=-7 EndZ=0
    g1: LineSegment StartX=-84 StartY=-7 StartZ=0 EndX=0 EndY=-7 EndZ=0
    g2: LineSegment StartX=0 StartY=-7 StartZ=0 EndX=0 EndY=0 EndZ=0
    g3: LineSegment StartX=0 StartY=0 StartZ=0 EndX=-84 EndY=0 EndZ=0
  constraints (11):
    c: Coincident(g0,g1)
    c: Coincident(g1,g2)
    c: Coincident(g2,g3)
    c: Coincident(g3,g0)
    c: Vertical(g0)
    c: Vertical(g2)
    c: Horizontal(g1)
    c: Horizontal(g3)
    c: Distance(g1,g3) = 7
    c: Coincident(g0,g-4)
    c: PointOnObject(g1,g-2)
FEATURE [PartDesign::Pocket] Pocket009
  BaseFeature = -> Clone001
  Direction = (0,-1,2e-16)
  Length = 5
  Length2 = 5
  Profile = -> Sketch028
  ReferenceAxis = -> Sketch028 [N_Axis]
  Refine = true
  Suppressed = false
  Type = 1
FEATURE [Sketcher::SketchObject] Sketch029
  ArcFitTolerance = 1e-06
  AttachmentSupport = -> [Pocket009]
  ExternalGeometry = -> [Pocket009]
  FullyConstrained = true
  MakeInternals = false
  MapMode = 5
  Placement = pos=(0,0,3e-16) rot=(1,0,0;3.14159rad)
  sketch-geometry (20):
    g0: LineSegment [constr] StartX=0 StartY=84 StartZ=0 EndX=0 EndY=79 EndZ=0
    g1: LineSegment [constr] StartX=0 StartY=79 StartZ=0 EndX=5 EndY=79 EndZ=0
    g2: LineSegment [constr] StartX=5 StartY=79 StartZ=0 EndX=5 EndY=84 EndZ=0
    g3: LineSegment [constr] StartX=5 StartY=84 StartZ=0 EndX=0 EndY=84 EndZ=0
    g4: LineSegment [constr] StartX=0 StartY=0 StartZ=0 EndX=5 EndY=0 EndZ=0
    g5: LineSegment [constr] StartX=5 StartY=0 StartZ=0 EndX=5 EndY=5 EndZ=0
    g6: LineSegment [constr] StartX=5 StartY=5 StartZ=0 EndX=0 EndY=5 EndZ=0
    g7: LineSegment [constr] StartX=0 StartY=5 StartZ=0 EndX=0 EndY=0 EndZ=0
    g8: LineSegment [constr] StartX=84 StartY=0 StartZ=0 EndX=84 EndY=5 EndZ=0
    g9: LineSegment [constr] StartX=84 StartY=5 StartZ=0 EndX=79 EndY=5 EndZ=0
    g10: LineSegment [constr] StartX=79 StartY=5 StartZ=0 EndX=79 EndY=0 EndZ=0
    g11: LineSegment [constr] StartX=79 StartY=0 StartZ=0 EndX=84 EndY=0 EndZ=0
    g12: LineSegment [constr] StartX=84 StartY=84 StartZ=0 EndX=79 EndY=84 EndZ=0
    g13: LineSegment [constr] StartX=79 StartY=84 StartZ=0 EndX=79 EndY=79 EndZ=0
    g14: LineSegment [constr] StartX=79 StartY=79 StartZ=0 EndX=84 EndY=79 EndZ=0
    g15: LineSegment [constr] StartX=84 StartY=79 StartZ=0 EndX=84 EndY=84 EndZ=0
    g16: Circle CenterX=5 CenterY=79 CenterZ=0 NormalX=0 NormalY=0 NormalZ=1 AngleXU=0 Radius=1.5
    g17: Circle CenterX=5 CenterY=5 CenterZ=0 NormalX=0 NormalY=0 NormalZ=1 AngleXU=0 Radius=1.5
    g18: Circle CenterX=79 CenterY=5 CenterZ=0 NormalX=0 NormalY=0 NormalZ=1 AngleXU=0 Radius=1.5
    g19: Circle CenterX=79 CenterY=79 CenterZ=0 NormalX=0 NormalY=0 NormalZ=1 AngleXU=0 Radius=1.5
  constraints (52):
    c: Coincident(g0,g1)
    c: Coincident(g1,g2)
    c: Coincident(g2,g3)
    c: Coincident(g3,g0)
    c: Vertical(g0)
    c: Vertical(g2)
    c: Horizontal(g1)
    c: Horizontal(g3)
    c: Distance(g0,g2) = 5
    c: Distance(g1,g3) = 5
    c: Coincident(g0,g-4)
    c: Coincident(g4,g5)
    c: Coincident(g5,g6)
    c: Coincident(g6,g7)
    c: Coincident(g7,g4)
    c: Horizontal(g4)
    c: Horizontal(g6)
    c: Vertical(g5)
    c: Vertical(g7)
    c: Distance(g5,g7) = 5
    c: Distance(g4,g6) = 5
    c: Coincident(g4,g-1)
    c: Coincident(g8,g9)
    c: Coincident(g9,g10)
    c: Coincident(g10,g11)
    c: Coincident(g11,g8)
    c: Vertical(g8)
    c: Vertical(g10)
    c: Horizontal(g9)
    c: Horizontal(g11)
    c: Distance(g8,g10) = 5
    c: Distance(g9,g11) = 5
    c: Coincident(g8,g-6)
    c: Coincident(g12,g13)
    c: Coincident(g13,g14)
    c: Coincident(g14,g15)
    c: Coincident(g15,g12)
    c: Horizontal(g12)
    c: Horizontal(g14)
    c: Vertical(g13)
    c: Vertical(g15)
    c: Distance(g13,g15) = 5
    c: Distance(g12,g14) = 5
    c: Coincident(g12,g-6)
    c: Diameter(g16) = 3
    c: Coincident(g16,g1)
    c: Diameter(g17) = 3
    c: Coincident(g17,g5)
    c: Diameter(g18) = 3
    c: Coincident(g18,g9)
    c: Diameter(g19) = 3
    c: Coincident(g19,g13)
FEATURE [PartDesign::Pocket] Pocket010
  BaseFeature = -> Pocket009
  Direction = (0,0,1)
  Length = 4
  Length2 = 5
  Profile = -> Sketch029
  ReferenceAxis = -> Sketch029 [N_Axis]
  Refine = true
  Suppressed = false
  Type = 0
FEATURE [Sketcher::SketchObject] Sketch057
  ArcFitTolerance = 1e-06
  AttachmentSupport = -> [Pocket010]
  ExternalGeometry = -> [Pocket010]
  FullyConstrained = true
  MakeInternals = false
  MapMode = 5
  Placement = pos=(0,0,3e-16) rot=(1,0,0;3.14159rad)
  sketch-geometry (4):
    g0: Circle CenterX=5 CenterY=79 CenterZ=0 NormalX=0 NormalY=0 NormalZ=1 AngleXU=0 Radius=1.5
    g1: Circle CenterX=79 CenterY=79 CenterZ=0 NormalX=0 NormalY=0 NormalZ=1 AngleXU=0 Radius=1.5
    g2: Circle CenterX=79 CenterY=5 CenterZ=0 NormalX=0 NormalY=0 NormalZ=1 AngleXU=0 Radius=1.5
    g3: Circle CenterX=5 CenterY=5 CenterZ=0 NormalX=0 NormalY=0 NormalZ=1 AngleXU=0 Radius=1.5
  constraints (8):
    c: Coincident(g0,g-3)
    c: Equal(g0,g-3)
    c: Coincident(g1,g-4)
    c: Equal(g1,g-4)
    c: Coincident(g2,g-5)
    c: Equal(g2,g-5)
    c: Coincident(g3,g-6)
    c: Equal(g3,g-6)
FEATURE [PartDesign::Pocket] Pocket028
  BaseFeature = -> Pocket010
  Direction = (0,0,1)
  Length = 10
  Length2 = 5
  Profile = -> Sketch057
  ReferenceAxis = -> Sketch057 [N_Axis]
  Refine = true
  Suppressed = false
  Type = 0
FEATURE [Sketcher::SketchObject] Sketch058
  ArcFitTolerance = 1e-06
  AttachmentSupport = -> [Pocket028]
  ExternalGeometry = -> [Pocket028]
  FullyConstrained = true
  MakeInternals = false
  MapMode = 5
  Placement = pos=(0,1.1e-15,5) rot=(0,0,1;0rad)
  sketch-geometry (4):
    g0: Circle CenterX=5 CenterY=-5 CenterZ=0 NormalX=0 NormalY=0 NormalZ=1 AngleXU=0 Radius=3
    g1: Circle CenterX=5 CenterY=-79 CenterZ=0 NormalX=0 NormalY=0 NormalZ=1 AngleXU=0 Radius=3
    g2: Circle CenterX=79 CenterY=-79 CenterZ=0 NormalX=0 NormalY=0 NormalZ=1 AngleXU=0 Radius=3
    g3: Circle CenterX=79 CenterY=-5 CenterZ=0 NormalX=0 NormalY=0 NormalZ=1 AngleXU=0 Radius=3
  constraints (8):
    c: Diameter(g0) = 6
    c: Coincident(g0,g-3)
    c: Diameter(g1) = 6
    c: Coincident(g1,g-4)
    c: Diameter(g2) = 6
    c: Coincident(g2,g-5)
    c: Diameter(g3) = 6
    c: Coincident(g3,g-6)
FEATURE [PartDesign::Pocket] Pocket029
  BaseFeature = -> Pocket028
  Direction = (0,0,-1)
  Length = 3.25
  Length2 = 5
  Profile = -> Sketch058
  ReferenceAxis = -> Sketch058 [N_Axis]
  Refine = true
  Suppressed = false
  Type = 0
FEATURE [Sketcher::SketchObject] Sketch059
  ArcFitTolerance = 1e-06
  AttachmentSupport = -> [Pocket029]
  ExternalGeometry = -> [Pocket029]
  FullyConstrained = true
  MakeInternals = false
  MapMode = 5
  Placement = pos=(0,0,3e-16) rot=(1,0,0;3.14159rad)
  sketch-geometry (8):
    g0: LineSegment StartX=0 StartY=84 StartZ=0 EndX=0 EndY=0 EndZ=0
    g1: LineSegment StartX=0 StartY=0 StartZ=0 EndX=84 EndY=0 EndZ=0
    g2: LineSegment StartX=84 StartY=0 StartZ=0 EndX=84 EndY=84 EndZ=0
    g3: LineSegment StartX=84 StartY=84 StartZ=0 EndX=0 EndY=84 EndZ=0
    g4: Circle CenterX=79 CenterY=5 CenterZ=0 NormalX=0 NormalY=0 NormalZ=1 AngleXU=0 Radius=1.5
    g5: Circle CenterX=5 CenterY=5 CenterZ=0 NormalX=0 NormalY=0 NormalZ=1 AngleXU=0 Radius=1.5
    g6: Circle CenterX=5 CenterY=79 CenterZ=0 NormalX=0 NormalY=0 NormalZ=1 AngleXU=0 Radius=1.5
    g7: Circle CenterX=79 CenterY=79 CenterZ=0 NormalX=0 NormalY=0 NormalZ=1 AngleXU=0 Radius=1.5
  constraints (18):
    c: Coincident(g0,g1)
    c: Coincident(g1,g2)
    c: Coincident(g2,g3)
    c: Coincident(g3,g0)
    c: Vertical(g0)
    c: Vertical(g2)
    c: Horizontal(g1)
    c: Horizontal(g3)
    c: Coincident(g0,g-3)
    c: Coincident(g1,g-4)
    c: Coincident(g4,g-8)
    c: Equal(g4,g-8)
    c: Coincident(g5,g-5)
    c: Equal(g5,g-5)
    c: Coincident(g6,g-6)
    c: Equal(g6,g-6)
    c: Coincident(g7,g-7)
    c: Equal(g7,g-7)
FEATURE [PartDesign::Pad] Pad025
  BaseFeature = -> Pocket029
  Direction = (0,0,-1)
  Length = 1.25
  Length2 = 10
  Profile = -> Sketch059
  ReferenceAxis = -> Sketch059 [N_Axis]
  Refine = true
  Suppressed = false
  Type = 0
FEATURE [PartDesign::Pocket] Pocket030
  BaseFeature = -> Pad025
  Direction = (0,0,1)
  Length = 12
  Length2 = 5
  Profile = -> Sketch060
  ReferenceAxis = -> Sketch060 [N_Axis]
  Refine = true
  Suppressed = false
  Type = 1
FEATURE [PartDesign::Body] Body007  label="Base"
  AllowCompound = false
  Group = -> [Clone001,Sketch028,Pocket009,Sketch029,Pocket010,Sketch057,Pocket028,Sketch058,Pocket029,Sketch059,Pad025,DatumPlane011,CopyBinBase,Binder,Binder001,Binder002,Binder003,Binder004,Sketch060,Pocket030]
  Origin = -> Origin007
  Placement = pos=(-93,0,0) rot=(0,0,1;0rad)
  Tip = -> Pocket030
FEATURE [PartDesign::FeatureBase] BaseFeature
  BaseFeature = -> BinBase
  Suppressed = false
FEATURE [PartDesign::Pocket] Pocket035
  BaseFeature = -> BaseFeature
  Direction = (0,0,1)
  Length = 5
  Length2 = 5
  Profile = -> BaseFeature [Face632,Face631,Face636,Face635,Face232,Face231,Face630,Face629]
  Refine = true
  Suppressed = false
  Type = 2
FEATURE [PartDesign::Body] Body009  label="Gridfinity Bolt On Base"
  AllowCompound = false
  BaseFeature = -> BinBase
  Group = -> [BaseFeature,Pocket035]
  Origin = -> Origin009
  Placement = pos=(-72,-63,0) rot=(0,0,1;0rad)
  Tip = -> Pocket035
FEATURE [PartDesign::FeaturePython] ScrewTogetherBaseplate  # WARN: FeaturePython — macro-defined, semantics opaque (R4)
  BaseProfileBottomChamfer = 0.7
  BaseProfileHeight = 4.25
  BaseProfileTopChamfer = 1.75
  BaseProfileVerticalSection = 1.8
  BaseThickness = 6.4
  BaseplateProfileTotalHeight = 0
  BaseplateTopLedgeWidth = 0.4
  BinBottomRadius = 1.15
  BinOuterRadius = 4
  BinVerticalRadius = 1.85
  Clearance = 0.25
  ConnectionHoleDiameter = 3.2
  GridSize = 42
  HeightUnitValue = 7
  MagnetBaseHole = 3
  MagnetBottomChamfer = 2
  MagnetChamfer = 0.4
  MagnetEdgeThickness = 1.2
  MagnetHoleDepth = 2.4
  MagnetHoleDiameter = 6.5
  MagnetHoleDistanceFromEdge = 8
  MagnetHolesShape = 0
  ScrewHoleDiameter = 3
  SmallFillet = 1
  Suppressed = false
  TotalHeight = 10.65
  version = 0.8.0
  xGridUnits = 4
  xTotalWidth = 168
  yGridUnits = 4
  yTotalWidth = 168
FEATURE [PartDesign::Body] Body010  label="Gridfinity Bolt Together Mesh"
  AllowCompound = false
  Group = -> [ScrewTogetherBaseplate]
  Origin = -> Origin010
  Placement = pos=(-59,45,0) rot=(0,0,1;0rad)
  Tip = -> ScrewTogetherBaseplate
FEATURE [Sketcher::SketchObject] Sketch065
  ArcFitTolerance = 1e-06
  AttachmentSupport = -> [Pocket025]
  ExternalGeometry = -> [Pocket025]
  FullyConstrained = true
  MakeInternals = false
  MapMode = 5
  Placement = pos=(-1.2282e-09,-84,2e-15) rot=(-0.707107,0,0.707107;3.14159rad)
  sketch-geometry (18):
    g0: LineSegment [constr] StartX=-27.3536 StartY=-1.42e-14 StartZ=0 EndX=-27.3536 EndY=-5 EndZ=0
    g1: LineSegment [constr] StartX=-27.3536 StartY=-5 StartZ=0 EndX=-22.3536 EndY=-5 EndZ=0
    g2: LineSegment [constr] StartX=-22.3536 StartY=-5 StartZ=0 EndX=-22.3536 EndY=-1.42e-14 EndZ=0
    g3: LineSegment [constr] StartX=-22.3536 StartY=-1.42e-14 StartZ=0 EndX=-27.3536 EndY=-1.42e-14 EndZ=0
    g4: LineSegment [constr] StartX=-22.3536 StartY=-5 StartZ=0 EndX=-17.3536 EndY=-5 EndZ=0
    g5: LineSegment [constr] StartX=-17.3536 StartY=-5 StartZ=0 EndX=-12.3536 EndY=-5 EndZ=0
    g6: LineSegment [constr] StartX=-27.3536 StartY=-84 StartZ=0 EndX=-22.3536 EndY=-84 EndZ=0
    g7: LineSegment [constr] StartX=-22.3536 StartY=-84 StartZ=0 EndX=-22.3536 EndY=-79 EndZ=0
    g8: LineSegment [constr] StartX=-22.3536 StartY=-79 StartZ=0 EndX=-27.3536 EndY=-79 EndZ=0
    g9: LineSegment [constr] StartX=-27.3536 StartY=-79 StartZ=0 EndX=-27.3536 EndY=-84 EndZ=0
    g10: LineSegment [constr] StartX=-22.3536 StartY=-79 StartZ=0 EndX=-17.3536 EndY=-79 EndZ=0
    g11: LineSegment [constr] StartX=-17.3536 StartY=-79 StartZ=0 EndX=-12.3536 EndY=-79 EndZ=0
    g12: Circle CenterX=-22.3536 CenterY=-79 CenterZ=0 NormalX=0 NormalY=0 NormalZ=1 AngleXU=0 Radius=1.3
    g13: Circle CenterX=-17.3536 CenterY=-79 CenterZ=0 NormalX=0 NormalY=0 NormalZ=1 AngleXU=0 Radius=1.3
    g14: Circle CenterX=-12.3536 CenterY=-79 CenterZ=0 NormalX=0 NormalY=0 NormalZ=1 AngleXU=0 Radius=1.3
    g15: Circle CenterX=-22.3536 CenterY=-5 CenterZ=0 NormalX=0 NormalY=0 NormalZ=1 AngleXU=0 Radius=1.3
    g16: Circle CenterX=-17.3536 CenterY=-5 CenterZ=0 NormalX=0 NormalY=0 NormalZ=1 AngleXU=0 Radius=1.3
    g17: Circle CenterX=-12.3536 CenterY=-5 CenterZ=0 NormalX=0 NormalY=0 NormalZ=1 AngleXU=0 Radius=1.3
  constraints (46):
    c: Coincident(g0,g1)
    c: Coincident(g1,g2)
    c: Coincident(g2,g3)
    c: Coincident(g3,g0)
    c: Vertical(g0)
    c: Vertical(g2)
    c: Horizontal(g1)
    c: Horizontal(g3)
    c: Distance(g0,g2) = 5
    c: Distance(g1,g3) = 5
    c: Coincident(g0,g-4)
    c: Distance(g4) = 5
    c: Coincident(g4,g1)
    c: Horizontal(g4)
    c: Distance(g5) = 5
    c: Coincident(g5,g4)
    c: Horizontal(g5)
    c: Coincident(g6,g7)
    c: Coincident(g7,g8)
    c: Coincident(g8,g9)
    c: Coincident(g9,g6)
    c: Horizontal(g6)
    c: Horizontal(g8)
    c: Vertical(g7)
    c: Vertical(g9)
    c: Distance(g7,g9) = 5
    c: Distance(g6,g8) = 5
    c: Coincident(g6,g-7)
    c: Distance(g10) = 5
    c: Coincident(g10,g7)
    c: Horizontal(g10)
    c: Distance(g11) = 5
    c: Coincident(g11,g10)
    c: Horizontal(g11)
    c: Diameter(g12) = 2.6
    c: Coincident(g12,g7)
    c: Coincident(g13,g10)
    c: Coincident(g14,g11)
    c: Coincident(g15,g1)
    c: Coincident(g16,g4)
    c: Coincident(g17,g5)
    c: Equal(g15,g16)
    c: Equal(g16,g17)
    c: Equal(g17,g12)
    c: Equal(g12,g13)
    c: Equal(g13,g14)
FEATURE [PartDesign::Pocket] Pocket036
  BaseFeature = -> Pocket025
  Direction = (1,0,-2.14311e-10)
  Length = 5
  Length2 = 5
  Placement = pos=(0,-84,2e-15) rot=(1,0,0;1.5708rad)
  Profile = -> Sketch065
  ReferenceAxis = -> Sketch065 [N_Axis]
  Refine = true
  Suppressed = false
  Type = 0
FEATURE [Sketcher::SketchObject] Sketch066
  ArcFitTolerance = 1e-06
  AttachmentSupport = -> [Pocket036]
  ExternalGeometry = -> [Pocket036]
  FullyConstrained = true
  MakeInternals = false
  MapMode = 5
  Placement = pos=(84,-84,-1.80021e-08) rot=(0.707107,0,0.707107;3.14159rad)
  sketch-geometry (18):
    g0: LineSegment [constr] StartX=27.3536 StartY=-1.42e-14 StartZ=0 EndX=22.3536 EndY=-1.42e-14 EndZ=0
    g1: LineSegment [constr] StartX=22.3536 StartY=-1.42e-14 StartZ=0 EndX=22.3536 EndY=-5 EndZ=0
    g2: LineSegment [constr] StartX=22.3536 StartY=-5 StartZ=0 EndX=27.3536 EndY=-5 EndZ=0
    g3: LineSegment [constr] StartX=27.3536 StartY=-5 StartZ=0 EndX=27.3536 EndY=-1.42e-14 EndZ=0
    g4: LineSegment [constr] StartX=22.3536 StartY=-5 StartZ=0 EndX=17.3536 EndY=-5 EndZ=0
    g5: LineSegment [constr] StartX=17.3536 StartY=-5 StartZ=0 EndX=12.3536 EndY=-5 EndZ=0
    g6: Circle CenterX=12.3536 CenterY=-5 CenterZ=0 NormalX=0 NormalY=0 NormalZ=1 AngleXU=0 Radius=1.3
    g7: Circle CenterX=17.3536 CenterY=-5 CenterZ=0 NormalX=0 NormalY=0 NormalZ=1 AngleXU=0 Radius=1.3
    g8: Circle CenterX=22.3536 CenterY=-5 CenterZ=0 NormalX=0 NormalY=0 NormalZ=1 AngleXU=0 Radius=1.3
    g9: LineSegment [constr] StartX=27.3536 StartY=-84 StartZ=0 EndX=27.3536 EndY=-79 EndZ=0
    g10: LineSegment [constr] StartX=27.3536 StartY=-79 StartZ=0 EndX=22.3536 EndY=-79 EndZ=0
    g11: LineSegment [constr] StartX=22.3536 StartY=-79 StartZ=0 EndX=22.3536 EndY=-84 EndZ=0
    g12: LineSegment [constr] StartX=22.3536 StartY=-84 StartZ=0 EndX=27.3536 EndY=-84 EndZ=0
    g13: LineSegment [constr] StartX=22.3536 StartY=-79 StartZ=0 EndX=17.3536 EndY=-79 EndZ=0
    g14: LineSegment [constr] StartX=17.3536 StartY=-79 StartZ=0 EndX=12.3536 EndY=-79 EndZ=0
    g15: Circle CenterX=22.3536 CenterY=-79 CenterZ=0 NormalX=0 NormalY=0 NormalZ=1 AngleXU=0 Radius=1.3
    g16: Circle CenterX=17.3536 CenterY=-79 CenterZ=0 NormalX=0 NormalY=0 NormalZ=1 AngleXU=0 Radius=1.3
    g17: Circle CenterX=12.3536 CenterY=-79 CenterZ=0 NormalX=0 NormalY=0 NormalZ=1 AngleXU=0 Radius=1.3
  constraints (46):
    c: Coincident(g0,g1)
    c: Coincident(g1,g2)
    c: Coincident(g2,g3)
    c: Coincident(g3,g0)
    c: Horizontal(g0)
    c: Horizontal(g2)
    c: Vertical(g1)
    c: Vertical(g3)
    c: Distance(g1,g3) = 5
    c: Distance(g0,g2) = 5
    c: Coincident(g0,g-5)
    c: Distance(g4) = 5
    c: Coincident(g4,g1)
    c: Horizontal(g4)
    c: Distance(g5) = 5
    c: Coincident(g5,g4)
    c: Horizontal(g5)
    c: Diameter(g6) = 2.6
    c: Coincident(g6,g5)
    c: Diameter(g7) = 2.6
    c: Coincident(g7,g4)
    c: Diameter(g8) = 2.6
    c: Coincident(g8,g1)
    c: Coincident(g9,g10)
    c: Coincident(g10,g11)
    c: Coincident(g11,g12)
    c: Coincident(g12,g9)
    c: Vertical(g9)
    c: Vertical(g11)
    c: Horizontal(g10)
    c: Horizontal(g12)
    c: Distance(g9,g11) = 5
    c: Distance(g10,g12) = 5
    c: Coincident(g9,g-5)
    c: Distance(g13) = 5
    c: Coincident(g13,g10)
    c: Horizontal(g13)
    c: Distance(g14) = 5
    c: Coincident(g14,g13)
    c: Horizontal(g14)
    c: Diameter(g15) = 2.6
    c: Coincident(g15,g10)
    c: Diameter(g16) = 2.6
    c: Coincident(g16,g13)
    c: Diameter(g17) = 2.6
    c: Coincident(g17,g14)
FEATURE [PartDesign::Pocket] Pocket037
  BaseFeature = -> Pocket036
  Direction = (-1,0,2.14311e-10)
  Length = 5
  Length2 = 5
  Placement = pos=(0,-84,2e-15) rot=(1,0,0;1.5708rad)
  Profile = -> Sketch066
  ReferenceAxis = -> Sketch066 [N_Axis]
  Refine = true
  Suppressed = false
  Type = 0
FEATURE [PartDesign::Body] Body002  label="Upper"
  AllowCompound = false
  Group = -> [ShapeBinder001,DatumPlane004,CopyFillet001,Sketch008,Pad006,Sketch009,Pocket001,Sketch010,Pocket002,Sketch011,Pocket003,Sketch012,Pocket004,Sketch013,Pocket005,Sketch030,Pad016,Sketch031,Pocket011,Sketch037,Pocket015,Sketch039,Pocket017,Sketch050,Pocket023,Sketch051,Pocket024,Sketch052,Pad023,Sketch053,Pocket025,Sketch065,Pocket036,Sketch066,Pocket037]
  Origin = -> Origin002
  Tip = -> Pocket037
FEATURE [PartDesign::ShapeBinder] CopyPocket030
  TraceSupport = false
FEATURE [PartDesign::Plane] DatumPlane012
  AttachmentSupport = -> [CopyPocket030]
  Length = 128.137
  MapMode = 5
  Placement = pos=(0,1e-16,0) rot=(0,0.707107,0.707107;3.14159rad)
  ResizeMode = 0
  Width = 103.137
FEATURE [Sketcher::SketchObject] Sketch067
  ArcFitTolerance = 1e-06
  AttachmentSupport = -> [DatumPlane012]
  ExternalGeometry = -> [CopyPocket030]
  FullyConstrained = true
  MakeInternals = false
  MapMode = 5
  Placement = pos=(0,1e-16,0) rot=(0,0.707107,0.707107;3.14159rad)
  sketch-geometry (15):
    g0: Circle CenterX=-42 CenterY=14 CenterZ=0 NormalX=0 NormalY=0 NormalZ=1 AngleXU=0 Radius=5
    g1: Circle CenterX=-28 CenterY=2.5 CenterZ=0 NormalX=0 NormalY=0 NormalZ=1 AngleXU=0 Radius=1.55
    g2: Circle CenterX=-56 CenterY=2.5 CenterZ=0 NormalX=0 NormalY=0 NormalZ=1 AngleXU=0 Radius=1.55
    g3: LineSegment StartX=-84 StartY=5 StartZ=0 EndX=-54 EndY=5 EndZ=0
    g4: LineSegment StartX=0 StartY=5 StartZ=0 EndX=-30 EndY=5 EndZ=0
    g5: LineSegment StartX=-30 StartY=5 StartZ=0 EndX=-15.8536 EndY=19.1464 EndZ=0
    g6: LineSegment StartX=-67.7929 StartY=20 StartZ=0 EndX=-16.2071 EndY=20 EndZ=0
    g7: LineSegment StartX=-54 StartY=5 StartZ=0 EndX=-68.1465 EndY=19.1464 EndZ=0
    g8: ArcOfCircle CenterX=-16.2071 CenterY=19.5 CenterZ=0 NormalX=0 NormalY=0 NormalZ=1 AngleXU=0 Radius=0.5 StartAngle=5.49779 EndAngle=7.85398
    g9: GeomPoint [constr] X=-15 Y=20 Z=0
    g10: ArcOfCircle CenterX=-67.7929 CenterY=19.5 CenterZ=0 NormalX=0 NormalY=0 NormalZ=1 AngleXU=0 Radius=0.5 StartAngle=1.5708 EndAngle=3.92699
    g11: GeomPoint [constr] X=-69 Y=20 Z=0
    g12: LineSegment StartX=-84 StartY=5 StartZ=0 EndX=-84 EndY=-1.25 EndZ=0
    g13: LineSegment StartX=0 StartY=5 StartZ=0 EndX=0 EndY=-1.25 EndZ=0
    g14: LineSegment StartX=0 StartY=-1.25 StartZ=0 EndX=-84 EndY=-1.25 EndZ=0
  constraints (31):
    c: Diameter(g0) = 10
    c: Coincident(g0,g-11)
    c: Diameter(g1) = 3.1
    c: Coincident(g1,g-3)
    c: Diameter(g2) = 3.1
    c: Coincident(g2,g-4)
    c: Coincident(g3,g-6)
    c: Coincident(g3,g-10)
    c: Coincident(g4,g-7)
    c: Coincident(g4,g-8)
    c: Coincident(g5,g4)
    c: Tangent(g5,g-8)
    c: Coincident(g7,g3)
    c: Tangent(g6,g-9)
    c: Tangent(g7,g-10)
    c: PointOnObject(g9,g5)
    c: PointOnObject(g9,g6)
    c: Tangent(g5,g8) = -1.5708
    c: Tangent(g6,g8) = 1.5708
    c: DistanceY(g8,g6) = 0.5
    c: PointOnObject(g11,g7)
    c: PointOnObject(g11,g6)
    c: Tangent(g7,g10) = 1.5708
    c: Tangent(g6,g10) = 1.5708
    c: DistanceY(g10,g6) = 0.5
    c: Coincident(g12,g3)
    c: Coincident(g12,g-5)
    c: Coincident(g13,g4)
    c: Coincident(g13,g-5)
    c: Coincident(g14,g13)
    c: Coincident(g14,g12)
FEATURE [PartDesign::Pad] Pad026
  Direction = (0,1,-2e-16)
  Length = 20
  Length2 = 10
  Placement = pos=(0,1e-16,0) rot=(0,0.707107,0.707107;3.14159rad)
  Profile = -> Sketch067
  ReferenceAxis = -> Sketch067 [N_Axis]
  Refine = true
  Suppressed = false
  Type = 0
FEATURE [Sketcher::SketchObject] Sketch068
  ArcFitTolerance = 1e-06
  AttachmentSupport = -> [Pad026]
  ExternalGeometry = -> [Pad026]
  FullyConstrained = true
  MakeInternals = false
  MapMode = 5
  Placement = pos=(0,20,-4.4e-15) rot=(0,0.707107,0.707107;3.14159rad)
  sketch-geometry (2):
    g0: Circle CenterX=-56 CenterY=2.5 CenterZ=0 NormalX=0 NormalY=0 NormalZ=1 AngleXU=0 Radius=3
    g1: Circle CenterX=-28 CenterY=2.5 CenterZ=0 NormalX=0 NormalY=0 NormalZ=1 AngleXU=0 Radius=3
  constraints (4):
    c: Diameter(g0) = 6
    c: Coincident(g0,g-4)
    c: Diameter(g1) = 6
    c: Coincident(g1,g-3)
FEATURE [PartDesign::Pocket] Pocket038
  BaseFeature = -> Pad026
  Direction = (0,-1,2e-16)
  Length = 10
  Length2 = 5
  Placement = pos=(0,1e-16,0) rot=(0,0.707107,0.707107;3.14159rad)
  Profile = -> Sketch068
  ReferenceAxis = -> Sketch068 [N_Axis]
  Refine = true
  Suppressed = false
  Type = 0
FEATURE [PartDesign::Pad] Pad027
  BaseFeature = -> Pocket038
  Direction = (-2e-16,1,-2e-16)
  Length = 20
  Length2 = 10
  Placement = pos=(0,1e-16,0) rot=(0,0.707107,0.707107;3.14159rad)
  Profile = -> Pocket038 [Face4]
  Refine = true
  Suppressed = false
  Type = 0
FEATURE [Sketcher::SketchObject] Sketch069
  ArcFitTolerance = 1e-06
  AttachmentSupport = -> [Pad027]
  ExternalGeometry = -> [Pad027]
  FullyConstrained = true
  MakeInternals = false
  MapMode = 5
  Placement = pos=(0,40,-8.8e-15) rot=(0,0.707107,0.707107;3.14159rad)
  sketch-geometry (27):
    g0: GeomPoint X=-42 Y=-1.25 Z=0
    g1: Circle CenterX=-56 CenterY=2.5 CenterZ=0 NormalX=0 NormalY=0 NormalZ=1 AngleXU=0 Radius=3
    g2: Circle CenterX=-42 CenterY=14 CenterZ=0 NormalX=0 NormalY=0 NormalZ=1 AngleXU=0 Radius=5.00001
    g3: Circle CenterX=-28 CenterY=2.5 CenterZ=0 NormalX=0 NormalY=0 NormalZ=1 AngleXU=0 Radius=3
    g4: LineSegment StartX=-84 StartY=-43.25 StartZ=0 EndX=0 EndY=-43.25 EndZ=0
    g5: LineSegment StartX=0 StartY=-43.25 StartZ=0 EndX=0 EndY=40.75 EndZ=0
    g6: LineSegment StartX=0 StartY=40.75 StartZ=0 EndX=-84 EndY=40.75 EndZ=0
    g7: LineSegment StartX=-84 StartY=40.75 StartZ=0 EndX=-84 EndY=-43.25 EndZ=0
    g8: GeomPoint [constr] X=-42 Y=-1.25 Z=0
    g9: LineSegment [constr] StartX=-76 StartY=-35.25 StartZ=0 EndX=-8 EndY=-35.25 EndZ=0
    g10: LineSegment [constr] StartX=-8 StartY=-35.25 StartZ=0 EndX=-8 EndY=32.75 EndZ=0
    g11: LineSegment [constr] StartX=-8 StartY=32.75 StartZ=0 EndX=-76 EndY=32.75 EndZ=0
    g12: LineSegment [constr] StartX=-76 StartY=32.75 StartZ=0 EndX=-76 EndY=-35.25 EndZ=0
    g13: GeomPoint [constr] X=-42 Y=-1.25 Z=0
    g14: LineSegment [constr] StartX=-79 StartY=-38.25 StartZ=0 EndX=-5 EndY=-38.25 EndZ=0
    g15: LineSegment [constr] StartX=-5 StartY=-38.25 StartZ=0 EndX=-5 EndY=35.75 EndZ=0
    g16: LineSegment [constr] StartX=-5 StartY=35.75 StartZ=0 EndX=-79 EndY=35.75 EndZ=0
    g17: LineSegment [constr] StartX=-79 StartY=35.75 StartZ=0 EndX=-79 EndY=-38.25 EndZ=0
    g18: GeomPoint [constr] X=-42 Y=-1.25 Z=0
    g19: Circle CenterX=-79 CenterY=35.75 CenterZ=0 NormalX=0 NormalY=0 NormalZ=1 AngleXU=0 Radius=1.3
    g20: Circle CenterX=-76 CenterY=32.75 CenterZ=0 NormalX=0 NormalY=0 NormalZ=1 AngleXU=0 Radius=1.3
    g21: Circle CenterX=-8 CenterY=32.75 CenterZ=0 NormalX=0 NormalY=0 NormalZ=1 AngleXU=0 Radius=1.3
    g22: Circle CenterX=-5 CenterY=35.75 CenterZ=0 NormalX=0 NormalY=0 NormalZ=1 AngleXU=0 Radius=1.3
    g23: Circle CenterX=-8 CenterY=-35.25 CenterZ=0 NormalX=0 NormalY=0 NormalZ=1 AngleXU=0 Radius=1.3
    g24: Circle CenterX=-5 CenterY=-38.25 CenterZ=0 NormalX=0 NormalY=0 NormalZ=1 AngleXU=0 Radius=1.3
    g25: Circle CenterX=-76 CenterY=-35.25 CenterZ=0 NormalX=0 NormalY=0 NormalZ=1 AngleXU=0 Radius=1.3
    g26: Circle CenterX=-79 CenterY=-38.25 CenterZ=0 NormalX=0 NormalY=0 NormalZ=1 AngleXU=0 Radius=1.3
  constraints (59):
    c: Symmetric(g-3,g-3,g0)
    c: Coincident(g1,g-4)
    c: Equal(g1,g-4)
    c: Coincident(g2,g-6)
    c: Tangent(g2,g-6)
    c: Coincident(g3,g-5)
    c: Equal(g3,g-5)
    c: Coincident(g4,g5)
    c: Coincident(g5,g6)
    c: Coincident(g6,g7)
    c: Coincident(g7,g4)
    c: Horizontal(g4)
    c: Horizontal(g6)
    c: Vertical(g5)
    c: Vertical(g7)
    c: Symmetric(g6,g4,g8)
    c: Distance(g5,g7) = 84
    c: Distance(g4,g6) = 84
    c: Coincident(g8,g0)
    c: Coincident(g9,g10)
    c: Coincident(g10,g11)
    c: Coincident(g11,g12)
    c: Coincident(g12,g9)
    c: Horizontal(g9)
    c: Horizontal(g11)
    c: Vertical(g10)
    c: Vertical(g12)
    c: Symmetric(g11,g9,g13)
    c: Distance(g10,g12) = 68
    c: Distance(g9,g11) = 68
    c: Coincident(g13,g0)
    c: Coincident(g14,g15)
    c: Coincident(g15,g16)
    c: Coincident(g16,g17)
    c: Coincident(g17,g14)
    c: Horizontal(g14)
    c: Horizontal(g16)
    c: Vertical(g15)
    c: Vertical(g17)
    c: Symmetric(g16,g14,g18)
    c: Distance(g15,g17) = 74
    c: Distance(g14,g16) = 74
    c: Coincident(g18,g0)
    c: Diameter(g19) = 2.6
    c: Coincident(g19,g16)
    c: Diameter(g20) = 2.6
    c: Coincident(g20,g11)
    c: Diameter(g21) = 2.6
    c: Coincident(g21,g10)
    c: Diameter(g22) = 2.6
    c: Coincident(g22,g15)
    c: Diameter(g23) = 2.6
    c: Coincident(g23,g9)
    c: Diameter(g24) = 2.6
    c: Coincident(g24,g14)
    c: Diameter(g25) = 2.6
    c: Coincident(g25,g9)
    c: Diameter(g26) = 2.6
    c: Coincident(g26,g14)
FEATURE [PartDesign::Pad] Pad028
  BaseFeature = -> Pad027
  Direction = (0,1,-2e-16)
  Length = 5
  Length2 = 10
  Placement = pos=(0,1e-16,0) rot=(0,0.707107,0.707107;3.14159rad)
  Profile = -> Sketch069
  ReferenceAxis = -> Sketch069 [N_Axis]
  Refine = true
  Suppressed = false
  Type = 0
FEATURE [Sketcher::SketchObject] Sketch070
  ArcFitTolerance = 1e-06
  AttachmentSupport = -> [Pad028]
  ExternalGeometry = -> [Pad028]
  FullyConstrained = true
  MakeInternals = false
  MapMode = 5
  Placement = pos=(0,1e-16,0) rot=(0,0.707107,-0.707107;3.14159rad)
  sketch-geometry (4):
    g0: LineSegment StartX=-84 StartY=1.25 StartZ=0 EndX=0 EndY=1.25 EndZ=0
    g1: LineSegment StartX=0 StartY=1.25 StartZ=0 EndX=0 EndY=6.25 EndZ=0
    g2: LineSegment StartX=0 StartY=6.25 StartZ=0 EndX=-84 EndY=6.25 EndZ=0
    g3: LineSegment StartX=-84 StartY=6.25 StartZ=0 EndX=-84 EndY=1.25 EndZ=0
  constraints (10):
    c: Coincident(g0,g1)
    c: Coincident(g1,g2)
    c: Coincident(g2,g3)
    c: Coincident(g3,g0)
    c: Horizontal(g2)
    c: Vertical(g1)
    c: Vertical(g3)
    c: Coincident(g0,g-3)
    c: Coincident(g0,g-3)
    c: DistanceY(g3,g3) = 5
FEATURE [PartDesign::Pad] Pad029
  BaseFeature = -> Pad028
  Direction = (0,-1,-2e-16)
  Length = 10
  Length2 = 10
  Placement = pos=(0,1e-16,0) rot=(0,0.707107,0.707107;3.14159rad)
  Profile = -> Sketch070
  ReferenceAxis = -> Sketch070 [N_Axis]
  Refine = true
  Reversed = true
  Suppressed = false
  Type = 2
FEATURE [Sketcher::SketchObject] Sketch071
  ArcFitTolerance = 1e-06
  AttachmentSupport = -> [Pad029]
  ExternalGeometry = -> [Pad029]
  FullyConstrained = true
  MakeInternals = false
  MapMode = 5
  Placement = pos=(0,4.3e-15,0) rot=(0,0.707107,-0.707107;3.14159rad)
  sketch-geometry (5):
    g0: LineSegment [constr] StartX=-84 StartY=6.25 StartZ=0 EndX=-84 EndY=1.25 EndZ=0
    g1: LineSegment StartX=-84 StartY=1.25 StartZ=0 EndX=0 EndY=1.25 EndZ=0
    g2: LineSegment StartX=0 StartY=1.25 StartZ=0 EndX=0 EndY=6.25 EndZ=0
    g3: LineSegment StartX=0 StartY=6.25 StartZ=0 EndX=-84 EndY=6.25 EndZ=0
    g4: LineSegment StartX=-84 StartY=6.25 StartZ=0 EndX=-84 EndY=1.25 EndZ=0
  constraints (13):
    c: Distance(g0) = 5
    c: Coincident(g0,g-3)
    c: Perpendicular(g-3,g0)
    c: Coincident(g1,g2)
    c: Coincident(g2,g3)
    c: Coincident(g3,g4)
    c: Coincident(g4,g1)
    c: Horizontal(g1)
    c: Horizontal(g3)
    c: Vertical(g2)
    c: Vertical(g4)
    c: Coincident(g1,g0)
    c: Coincident(g2,g-3)
FEATURE [PartDesign::Pad] Pad030
  BaseFeature = -> Pad029
  Direction = (0,-1,-2e-16)
  Length = 15
  Length2 = 10
  Placement = pos=(0,1e-16,0) rot=(0,0.707107,0.707107;3.14159rad)
  Profile = -> Sketch071
  ReferenceAxis = -> Sketch071 [N_Axis]
  Refine = true
  Suppressed = false
  Type = 0
FEATURE [Sketcher::SketchObject] Sketch072
  ArcFitTolerance = 1e-06
  AttachmentSupport = -> [Pad030]
  ExternalGeometry = -> [Pad030]
  FullyConstrained = true
  MakeInternals = false
  MapMode = 5
  Placement = pos=(-1e-16,6e-16,-1.25) rot=(0,0,1;0rad)
  sketch-geometry (10):
    g0: LineSegment [constr] StartX=0 StartY=0 StartZ=0 EndX=0 EndY=-5 EndZ=0
    g1: LineSegment [constr] StartX=0 StartY=-5 StartZ=0 EndX=5 EndY=-5 EndZ=0
    g2: LineSegment [constr] StartX=5 StartY=-5 StartZ=0 EndX=5 EndY=0 EndZ=0
    g3: LineSegment [constr] StartX=5 StartY=0 StartZ=0 EndX=0 EndY=0 EndZ=0
    g4: LineSegment [constr] StartX=84 StartY=4.4e-15 StartZ=0 EndX=79 EndY=4.4e-15 EndZ=0
    g5: LineSegment [constr] StartX=79 StartY=4.4e-15 StartZ=0 EndX=79 EndY=-5 EndZ=0
    g6: LineSegment [constr] StartX=79 StartY=-5 StartZ=0 EndX=84 EndY=-5 EndZ=0
    g7: LineSegment [constr] StartX=84 StartY=-5 StartZ=0 EndX=84 EndY=4.4e-15 EndZ=0
    g8: Circle CenterX=5 CenterY=-5 CenterZ=0 NormalX=0 NormalY=0 NormalZ=1 AngleXU=0 Radius=1.3
    g9: Circle CenterX=79 CenterY=-5 CenterZ=0 NormalX=0 NormalY=0 NormalZ=1 AngleXU=0 Radius=1.3
  constraints (26):
    c: Coincident(g0,g1)
    c: Coincident(g1,g2)
    c: Coincident(g2,g3)
    c: Coincident(g3,g0)
    c: Vertical(g0)
    c: Vertical(g2)
    c: Horizontal(g1)
    c: Horizontal(g3)
    c: Distance(g0,g2) = 5
    c: Distance(g1,g3) = 5
    c: Coincident(g0,g-1)
    c: Coincident(g4,g5)
    c: Coincident(g5,g6)
    c: Coincident(g6,g7)
    c: Coincident(g7,g4)
    c: Horizontal(g4)
    c: Horizontal(g6)
    c: Vertical(g5)
    c: Vertical(g7)
    c: Distance(g5,g7) = 5
    c: Distance(g4,g6) = 5
    c: Coincident(g4,g-4)
    c: Diameter(g8) = 2.6
    c: Coincident(g8,g1)
    c: Diameter(g9) = 2.6
    c: Coincident(g9,g5)
FEATURE [PartDesign::Pocket] Pocket039
  BaseFeature = -> Pad030
  Direction = (0,0,-1)
  Length = 5
  Length2 = 5
  Placement = pos=(0,1e-16,0) rot=(0,0.707107,0.707107;3.14159rad)
  Profile = -> Sketch072
  ReferenceAxis = -> Sketch072 [N_Axis]
  Refine = true
  Suppressed = false
  Type = 1
FEATURE [PartDesign::Chamfer] Chamfer017
  Angle = 45
  Base = -> Pocket039 [Edge50,Edge34]
  BaseFeature = -> Pocket039
  ChamferType = 0
  FlipDirection = false
  Placement = pos=(0,1e-16,0) rot=(0,0.707107,0.707107;3.14159rad)
  Refine = true
  Size = 8
  Size2 = 1
  SupportTransform = false
  Suppressed = false
  UseAllEdges = false
FEATURE [PartDesign::Chamfer] Chamfer018
  Angle = 45
  Base = -> Chamfer017 [Edge31]
  BaseFeature = -> Chamfer017
  ChamferType = 0
  FlipDirection = false
  Placement = pos=(0,1e-16,0) rot=(0,0.707107,0.707107;3.14159rad)
  Refine = true
  Size = 22
  Size2 = 1
  SupportTransform = false
  Suppressed = false
  UseAllEdges = false
FEATURE [Sketcher::SketchObject] Sketch073
  ArcFitTolerance = 1e-06
  AttachmentSupport = -> [Pocket027]
  FullyConstrained = true
  MakeInternals = false
  MapMode = 5
  Placement = pos=(42,-119,14) rot=(0.57735,-0.57735,0.57735;2.0944rad)
  sketch-geometry (2):
    g0: Circle CenterX=0 CenterY=0 CenterZ=0 NormalX=0 NormalY=0 NormalZ=1 AngleXU=0 Radius=7.5
    g1: Circle CenterX=0 CenterY=0 CenterZ=0 NormalX=0 NormalY=0 NormalZ=1 AngleXU=0 Radius=6.5
  constraints (4):
    c: Diameter(g0) = 15
    c: Coincident(g0,g-1)
    c: Diameter(g1) = 13
    c: Coincident(g1,g0)
FEATURE [PartDesign::Pocket] Pocket040
  BaseFeature = -> Pocket027
  Direction = (0,1,0)
  Length = 23
  Length2 = 5
  Placement = pos=(42,-84,14) rot=(0.57735,-0.57735,0.57735;2.0944rad)
  Profile = -> Sketch073
  ReferenceAxis = -> Sketch073 [N_Axis]
  Refine = true
  Suppressed = false
  Type = 0
FEATURE [PartDesign::Body] Body005  label="Adjuster"
  AllowCompound = false
  Group = -> [ShapeBinder003,DatumPlane006,Sketch019,Pad009,Sketch020,Pad010,Sketch021,Pad011,Sketch022,Pocket007,Fillet004,DatumPoint,VThreadProfile,Helix,AdditivePipe,ShapeBinder004,DatumPlane007,Sketch023,Pad012,Sketch035,Pocket013,Sketch036,Pocket014,Sketch055,Pad024,Sketch056,Pocket027,Sketch073,Pocket040]
  Origin = -> Origin005
  Tip = -> Pocket040
FEATURE [Sketcher::SketchObject] Sketch074
  ArcFitTolerance = 1e-06
  AttachmentSupport = -> [Chamfer018]
  ExternalGeometry = -> [Chamfer018]
  FullyConstrained = true
  MakeInternals = false
  MapMode = 5
  Placement = pos=(5.6e-15,1e-16,20) rot=(0,0,1;0rad)
  sketch-geometry (7):
    g0: GeomPoint [constr] X=42 Y=40 Z=0
    g1: GeomPoint [constr] X=42 Y=-1e-16 Z=0
    g2: LineSegment StartX=42 StartY=-1e-16 StartZ=0 EndX=52 EndY=-1e-16 EndZ=0
    g3: LineSegment StartX=42 StartY=-1e-16 StartZ=0 EndX=32 EndY=-1e-16 EndZ=0
    g4: LineSegment StartX=32 StartY=-1e-16 StartZ=0 EndX=32 EndY=40 EndZ=0
    g5: LineSegment StartX=52 StartY=-1e-16 StartZ=0 EndX=52 EndY=40 EndZ=0
    g6: LineSegment StartX=52 StartY=40 StartZ=0 EndX=32 EndY=40 EndZ=0
  constraints (16):
    c: Symmetric(g-4,g-4,g0)
    c: Symmetric(g-3,g-3,g1)
    c: Distance(g2) = 10
    c: Coincident(g2,g1)
    c: PointOnObject(g2,g-3)
    c: Distance(g3) = 10
    c: Coincident(g3,g1)
    c: PointOnObject(g3,g-3)
    c: Coincident(g4,g3)
    c: PointOnObject(g4,g-4)
    c: Vertical(g4)
    c: Coincident(g5,g2)
    c: PointOnObject(g5,g-4)
    c: Vertical(g5)
    c: Coincident(g6,g5)
    c: Coincident(g6,g4)
FEATURE [PartDesign::Pocket] Pocket041
  BaseFeature = -> Chamfer018
  Direction = (0,0,-1)
  Length = 12
  Length2 = 5
  Placement = pos=(0,1e-16,0) rot=(0,0.707107,0.707107;3.14159rad)
  Profile = -> Sketch074
  ReferenceAxis = -> Sketch074 [N_Axis]
  Refine = true
  Suppressed = false
  Type = 0
FEATURE [PartDesign::Chamfer] Chamfer019
  Angle = 45
  Base = -> Pocket041 [Edge96,Edge95]
  BaseFeature = -> Pocket041
  ChamferType = 0
  FlipDirection = false
  Placement = pos=(0,1e-16,0) rot=(0,0.707107,0.707107;3.14159rad)
  Refine = true
  Size = 4
  Size2 = 1
  SupportTransform = false
  Suppressed = false
  UseAllEdges = false
FEATURE [Sketcher::SketchObject] Sketch075
  ArcFitTolerance = 1e-06
  AttachmentSupport = -> [Chamfer019]
  ExternalGeometry = -> [Chamfer019]
  FullyConstrained = true
  MakeInternals = false
  MapMode = 5
  Placement = pos=(0,2.9e-15,-6.25) rot=(0,1,0;3.14159rad)
  sketch-geometry (14):
    g0: LineSegment [constr] StartX=-79 StartY=-5 StartZ=0 EndX=-79 EndY=-79 EndZ=0
    g1: LineSegment [constr] StartX=-5 StartY=-5 StartZ=0 EndX=-5 EndY=-79 EndZ=0
    g2: Circle CenterX=-79 CenterY=-79 CenterZ=0 NormalX=0 NormalY=0 NormalZ=1 AngleXU=0 Radius=1.3
    g3: Circle CenterX=-5 CenterY=-79 CenterZ=0 NormalX=0 NormalY=0 NormalZ=1 AngleXU=0 Radius=1.3
    g4: LineSegment StartX=-76 StartY=-15 StartZ=0 EndX=-76 EndY=-69 EndZ=0
    g5: LineSegment StartX=-8 StartY=-15 StartZ=0 EndX=-8 EndY=-69 EndZ=0
    g6: LineSegment [constr] StartX=-84 StartY=-7 StartZ=0 EndX=-84 EndY=-91 EndZ=0
    g7: LineSegment [constr] StartX=6e-16 StartY=-7 StartZ=0 EndX=0 EndY=-91 EndZ=0
    g8: LineSegment StartX=-76 StartY=-69 StartZ=0 EndX=-84 EndY=-77 EndZ=0
    g9: LineSegment StartX=-8 StartY=-69 StartZ=0 EndX=-1.8e-15 EndY=-77 EndZ=0
    g10: LineSegment StartX=-84 StartY=-77 StartZ=0 EndX=-84 EndY=-84 EndZ=0
    g11: LineSegment StartX=-84 StartY=-84 StartZ=0 EndX=0 EndY=-84 EndZ=0
    g12: LineSegment StartX=0 StartY=-84 StartZ=0 EndX=-1.8e-15 EndY=-77 EndZ=0
    g13: LineSegment StartX=-76 StartY=-15 StartZ=0 EndX=-8 EndY=-15 EndZ=0
  constraints (38):
    c: Distance(g0) = 74
    c: Coincident(g0,g-3)
    c: Vertical(g0)
    c: Distance(g1) = 74
    c: Coincident(g1,g-4)
    c: Vertical(g1)
    c: Diameter(g2) = 2.6
    c: Coincident(g2,g0)
    c: Diameter(g3) = 2.6
    c: Coincident(g3,g1)
    c: Distance(g4) = 54
    c: Coincident(g4,g-6)
    c: Vertical(g4)
    c: Distance(g5) = 54
    c: Coincident(g5,g-7)
    c: Vertical(g5)
    c: Distance(g6) = 84
    c: Coincident(g6,g-6)
    c: Vertical(g6)
    c: Distance(g7) = 84
    c: Coincident(g7,g-7)
    c: PointOnObject(g7,g-2)
    c: Angle(g-1,g8) = -2.35619
    c: Coincident(g8,g4)
    c: PointOnObject(g8,g6)
    c: Angle(g-1,g9) = -0.785398
    c: Coincident(g9,g5)
    c: PointOnObject(g9,g7)
    c: Distance(g10) = 7
    c: Coincident(g10,g8)
    c: PointOnObject(g10,g6)
    c: Coincident(g11,g10)
    c: PointOnObject(g11,g7)
    c: Horizontal(g11)
    c: Coincident(g12,g11)
    c: Coincident(g12,g9)
    c: Coincident(g13,g4)
    c: Coincident(g13,g5)
FEATURE [PartDesign::Pad] Pad031
  BaseFeature = -> Chamfer019
  Direction = (0,0,-1)
  Length = 5
  Length2 = 10
  Placement = pos=(0,1e-16,0) rot=(0,0.707107,0.707107;3.14159rad)
  Profile = -> Sketch075
  ReferenceAxis = -> Sketch075 [N_Axis]
  Refine = true
  Reversed = true
  Suppressed = false
  Type = 0
FEATURE [Sketcher::SketchObject] Sketch076
  ArcFitTolerance = 1e-06
  AttachmentSupport = -> [Pad031]
  ExternalGeometry = -> [Pad031]
  FullyConstrained = true
  MakeInternals = false
  MapMode = 5
  Placement = pos=(7.6e-15,-84,-1.85e-14) rot=(0,0.707107,-0.707107;3.14159rad)
  sketch-geometry (6):
    g0: GeomPoint X=-42 Y=6.25 Z=0
    g1: LineSegment [constr] StartX=-42 StartY=6.25 StartZ=0 EndX=-42 EndY=16.25 EndZ=0
    g2: LineSegment StartX=-42 StartY=6.25 StartZ=0 EndX=-32 EndY=6.25 EndZ=0
    g3: LineSegment StartX=-42 StartY=6.25 StartZ=0 EndX=-52 EndY=6.25 EndZ=0
    g4: LineSegment StartX=-52 StartY=6.25 StartZ=0 EndX=-42 EndY=16.25 EndZ=0
    g5: LineSegment StartX=-42 StartY=16.25 StartZ=0 EndX=-32 EndY=6.25 EndZ=0
  constraints (14):
    c: Symmetric(g-3,g-3,g0)
    c: Distance(g1) = 10
    c: Coincident(g1,g0)
    c: Vertical(g1)
    c: Distance(g2) = 10
    c: Coincident(g2,g0)
    c: PointOnObject(g2,g-3)
    c: Distance(g3) = 10
    c: Coincident(g3,g0)
    c: PointOnObject(g3,g-3)
    c: Coincident(g4,g3)
    c: Coincident(g4,g1)
    c: Coincident(g5,g1)
    c: Coincident(g5,g2)
FEATURE [PartDesign::Pad] Pad032
  BaseFeature = -> Pad031
  Direction = (0,-1,-2e-16)
  Length = 45
  Length2 = 10
  Placement = pos=(0,1e-16,0) rot=(0,0.707107,0.707107;3.14159rad)
  Profile = -> Sketch076
  ReferenceAxis = -> Sketch076 [N_Axis]
  Refine = true
  Reversed = true
  Suppressed = false
  Type = 1
FEATURE [PartDesign::ShapeBinder] CopyPocket012
  Placement = pos=(7.67535e-08,-84,27.3536) rot=(0,0,1;3.14159rad)
  TraceSupport = false
FEATURE [PartDesign::Plane] DatumPlane013
  AttachmentSupport = -> [CopyPocket012]
  Length = 120.881
  MapMode = 5
  Placement = pos=(9.77984e-08,-84,34.8536) rot=(0,0,1;3.14159rad)
  ResizeMode = 0
  Width = 129.881
FEATURE [Sketcher::SketchObject] Sketch077
  ArcFitTolerance = 1e-06
  AttachmentSupport = -> [DatumPlane013]
  ExternalGeometry = -> [CopyPocket012]
  FullyConstrained = true
  MakeInternals = false
  MapMode = 5
  Placement = pos=(9.77984e-08,-84,34.8536) rot=(0,0,1;3.14159rad)
  sketch-geometry (18):
    g0: Circle CenterX=-72 CenterY=-77 CenterZ=0 NormalX=0 NormalY=0 NormalZ=1 AngleXU=0 Radius=1.5
    g1: Circle CenterX=-72 CenterY=-67 CenterZ=0 NormalX=0 NormalY=0 NormalZ=1 AngleXU=0 Radius=1.5
    g2: Circle CenterX=-12 CenterY=-67 CenterZ=0 NormalX=0 NormalY=0 NormalZ=1 AngleXU=0 Radius=1.5
    g3: Circle CenterX=-12 CenterY=-77 CenterZ=0 NormalX=0 NormalY=0 NormalZ=1 AngleXU=0 Radius=1.5
    g4: LineSegment StartX=-75 StartY=-79.5 StartZ=0 EndX=-69 EndY=-79.5 EndZ=0
    g5: LineSegment [constr] StartX=-69 StartY=-79.5 StartZ=0 EndX=-69 EndY=-64.5 EndZ=0
    g6: LineSegment [constr] StartX=-69 StartY=-64.5 StartZ=0 EndX=-75 EndY=-64.5 EndZ=0
    g7: LineSegment StartX=-75 StartY=-64.5 StartZ=0 EndX=-75 EndY=-79.5 EndZ=0
    g8: GeomPoint [constr] X=-72 Y=-72 Z=0
    g9: LineSegment StartX=-15 StartY=-79.5 StartZ=0 EndX=-9 EndY=-79.5 EndZ=0
    g10: LineSegment StartX=-9 StartY=-79.5 StartZ=0 EndX=-9 EndY=-64.5 EndZ=0
    g11: LineSegment [constr] StartX=-9 StartY=-64.5 StartZ=0 EndX=-15 EndY=-64.5 EndZ=0
    g12: LineSegment [constr] StartX=-15 StartY=-64.5 StartZ=0 EndX=-15 EndY=-79.5 EndZ=0
    g13: GeomPoint [constr] X=-12 Y=-72 Z=0
    g14: LineSegment StartX=-75 StartY=-64.5 StartZ=0 EndX=-75 EndY=-59.5 EndZ=0
    g15: LineSegment StartX=-9 StartY=-64.5 StartZ=0 EndX=-9 EndY=-59.5 EndZ=0
    g16: LineSegment StartX=-75 StartY=-59.5 StartZ=0 EndX=-9 EndY=-59.5 EndZ=0
    g17: LineSegment StartX=-69 StartY=-79.5 StartZ=0 EndX=-15 EndY=-79.5 EndZ=0
  constraints (42):
    c: Coincident(g0,g-3)
    c: Coincident(g1,g-4)
    c: Coincident(g2,g-6)
    c: Coincident(g3,g-5)
    c: Diameter(g1) = 3
    c: Equal(g1,g0)
    c: Equal(g0,g3)
    c: Equal(g3,g2)
    c: Coincident(g4,g5)
    c: Coincident(g5,g6)
    c: Coincident(g6,g7)
    c: Coincident(g7,g4)
    c: Horizontal(g4)
    c: Horizontal(g6)
    c: Vertical(g5)
    c: Vertical(g7)
    c: Symmetric(g6,g4,g8)
    c: Distance(g5,g7) = 6
    c: Distance(g4,g6) = 15
    c: Coincident(g8,g-8)
    c: Coincident(g9,g10)
    c: Coincident(g10,g11)
    c: Coincident(g11,g12)
    c: Coincident(g12,g9)
    c: Horizontal(g9)
    c: Horizontal(g11)
    c: Vertical(g10)
    c: Vertical(g12)
    c: Symmetric(g11,g9,g13)
    c: Distance(g10,g12) = 6
    c: Distance(g9,g11) = 15
    c: Coincident(g13,g-7)
    c: Distance(g14) = 5
    c: Coincident(g14,g6)
    c: Vertical(g14)
    c: Distance(g15) = 5
    c: Coincident(g15,g10)
    c: Perpendicular(g11,g15)
    c: Coincident(g16,g14)
    c: Coincident(g16,g15)
    c: Coincident(g17,g4)
    c: Coincident(g17,g9)
FEATURE [PartDesign::Pad] Pad033
  Direction = (2.80598e-09,0,1)
  Length = 3
  Length2 = 10
  Placement = pos=(9.77984e-08,-84,34.8536) rot=(0,0,1;3.14159rad)
  Profile = -> Sketch077
  ReferenceAxis = -> Sketch077 [N_Axis]
  Refine = true
  Suppressed = false
  Type = 0
FEATURE [Sketcher::SketchObject] Sketch078
  ArcFitTolerance = 1e-06
  AttachmentSupport = -> [Pad033]
  ExternalGeometry = -> [Pad033]
  FullyConstrained = true
  MakeInternals = false
  MapMode = 5
  Placement = pos=(1.06216e-07,-84,37.8536) rot=(0,0,1;3.14159rad)
  sketch-geometry (25):
    g0: LineSegment [constr] StartX=-75 StartY=-59.5 StartZ=0 EndX=-75 EndY=-64.5 EndZ=0
    g1: LineSegment [constr] StartX=-75 StartY=-64.5 StartZ=0 EndX=-9 EndY=-64.5 EndZ=0
    g2: LineSegment [constr] StartX=-75 StartY=-64.5 StartZ=0 EndX=-65 EndY=-64.5 EndZ=0
    g3: LineSegment [constr] StartX=-65 StartY=-64.5 StartZ=0 EndX=-60 EndY=-64.5 EndZ=0
    g4: LineSegment [constr] StartX=-9 StartY=-64.5 StartZ=0 EndX=-19 EndY=-64.5 EndZ=0
    g5: LineSegment [constr] StartX=-19 StartY=-64.5 StartZ=0 EndX=-24 EndY=-64.5 EndZ=0
    g6: LineSegment [constr] StartX=-60 StartY=-64.5 StartZ=0 EndX=-42 EndY=-64.5 EndZ=0
    g7: LineSegment [constr] StartX=-44.5 StartY=-64.5 StartZ=0 EndX=-39.5 EndY=-64.5 EndZ=0
    g8: GeomPoint [constr] X=-42 Y=-64.5 Z=0
    g9: LineSegment StartX=-39.5 StartY=-64.5 StartZ=0 EndX=-39.5 EndY=-79.5 EndZ=0
    g10: LineSegment StartX=-44.5 StartY=-64.5 StartZ=0 EndX=-44.5 EndY=-79.5 EndZ=0
    g11: LineSegment StartX=-39.5 StartY=-79.5 StartZ=0 EndX=-44.5 EndY=-79.5 EndZ=0
    g12: LineSegment StartX=-39.5 StartY=-64.5 StartZ=0 EndX=-24 EndY=-64.5 EndZ=0
    g13: LineSegment StartX=-24 StartY=-64.5 StartZ=0 EndX=-24 EndY=-79.5 EndZ=0
    g14: LineSegment StartX=-19 StartY=-64.5 StartZ=0 EndX=-19 EndY=-79.5 EndZ=0
    g15: LineSegment StartX=-19 StartY=-79.5 StartZ=0 EndX=-24 EndY=-79.5 EndZ=0
    g16: LineSegment StartX=-19 StartY=-64.5 StartZ=0 EndX=-9 EndY=-64.5 EndZ=0
    g17: LineSegment StartX=-9 StartY=-64.5 StartZ=0 EndX=-9 EndY=-59.5 EndZ=0
    g18: LineSegment StartX=-9 StartY=-59.5 StartZ=0 EndX=-75 EndY=-59.5 EndZ=0
    g19: LineSegment StartX=-75 StartY=-59.5 StartZ=0 EndX=-75 EndY=-64.5 EndZ=0
    g20: LineSegment StartX=-75 StartY=-64.5 StartZ=0 EndX=-65 EndY=-64.5 EndZ=0
    g21: LineSegment StartX=-65 StartY=-64.5 StartZ=0 EndX=-65 EndY=-79.5 EndZ=0
    g22: LineSegment StartX=-60 StartY=-64.5 StartZ=0 EndX=-60 EndY=-79.5 EndZ=0
    g23: LineSegment StartX=-60 StartY=-79.5 StartZ=0 EndX=-65 EndY=-79.5 EndZ=0
    g24: LineSegment StartX=-60 StartY=-64.5 StartZ=0 EndX=-44.5 EndY=-64.5 EndZ=0
  constraints (62):
    c: Distance(g0) = 5
    c: Coincident(g0,g-4)
    c: PointOnObject(g0,g-4)
    c: Coincident(g1,g0)
    c: PointOnObject(g1,g-5)
    c: Horizontal(g1)
    c: Distance(g2) = 10
    c: Coincident(g2,g0)
    c: PointOnObject(g2,g1)
    c: Distance(g3) = 5
    c: Coincident(g3,g2)
    c: PointOnObject(g3,g1)
    c: Distance(g4) = 10
    c: Coincident(g4,g1)
    c: PointOnObject(g4,g1)
    c: Distance(g5) = 5
    c: Coincident(g5,g4)
    c: PointOnObject(g5,g1)
    c: Coincident(g6,g3)
    c: Symmetric(g1,g1,g6)
    c: Distance(g7) = 5
    c: Horizontal(g7)
    c: Symmetric(g7,g7,g8)
    c: Coincident(g8,g6)
    c: Coincident(g9,g7)
    c: Vertical(g9)
    c: Coincident(g10,g7)
    c: Vertical(g10)
    c: PointOnObject(g10,g-6)
    c: PointOnObject(g9,g-6)
    c: Coincident(g11,g9)
    c: Coincident(g11,g10)
    c: Coincident(g12,g7)
    c: Coincident(g12,g5)
    c: Coincident(g13,g5)
    c: PointOnObject(g13,g-6)
    c: Vertical(g13)
    c: Coincident(g14,g4)
    c: PointOnObject(g14,g-6)
    c: Vertical(g14)
    c: Coincident(g15,g14)
    c: Coincident(g15,g13)
    c: Coincident(g16,g4)
    c: Coincident(g16,g1)
    c: Coincident(g17,g1)
    c: Coincident(g17,g-5)
    c: Coincident(g18,g17)
    c: Coincident(g18,g0)
    c: Coincident(g19,g0)
    c: Coincident(g19,g0)
    c: Coincident(g20,g0)
    c: Coincident(g20,g2)
    c: Coincident(g21,g2)
    c: PointOnObject(g21,g-6)
    c: Vertical(g21)
    c: Coincident(g22,g3)
    c: PointOnObject(g22,g-6)
    c: Vertical(g22)
    c: Coincident(g23,g22)
    c: Coincident(g23,g21)
    c: Coincident(g24,g3)
    c: Coincident(g24,g7)
FEATURE [PartDesign::Pad] Pad034
  BaseFeature = -> Pad033
  Direction = (2.80598e-09,0,1)
  Length = 20
  Length2 = 10
  Placement = pos=(9.77984e-08,-84,34.8536) rot=(0,0,1;3.14159rad)
  Profile = -> Sketch078
  ReferenceAxis = -> Sketch078 [N_Axis]
  Refine = true
  Suppressed = false
  Type = 0
FEATURE [Sketcher::SketchObject] Sketch079
  ArcFitTolerance = 1e-06
  AttachmentSupport = -> [Pad034]
  ExternalGeometry = -> [Pad034]
  FullyConstrained = true
  MakeInternals = false
  MapMode = 5
  Placement = pos=(65,-84,34.8536) rot=(0.57735,0.57735,0.57735;2.0944rad)
  sketch-geometry (3):
    g0: LineSegment StartX=64.5 StartY=23 StartZ=0 EndX=79.5 EndY=3 EndZ=0
    g1: LineSegment StartX=79.5 StartY=3 StartZ=0 EndX=79.5 EndY=23 EndZ=0
    g2: LineSegment StartX=79.5 StartY=23 StartZ=0 EndX=64.5 EndY=23 EndZ=0
  constraints (6):
    c: Coincident(g0,g-3)
    c: Coincident(g0,g-4)
    c: Coincident(g1,g0)
    c: Coincident(g1,g-4)
    c: Coincident(g2,g1)
    c: Coincident(g2,g0)
FEATURE [PartDesign::Pocket] Pocket042
  BaseFeature = -> Pad034
  Direction = (-1,-1e-16,2.80598e-09)
  Length = 5
  Length2 = 5
  Placement = pos=(9.77984e-08,-84,34.8536) rot=(0,0,1;3.14159rad)
  Profile = -> Sketch079
  ReferenceAxis = -> Sketch079 [N_Axis]
  Refine = true
  Suppressed = false
  Type = 1
FEATURE [PartDesign::Pad] Pad035
  BaseFeature = -> Pocket042
  Direction = (2.80598e-09,0,1)
  Length = 10
  Length2 = 10
  Placement = pos=(9.77984e-08,-84,34.8536) rot=(0,0,1;3.14159rad)
  Profile = -> Pocket042 [Face7]
  Refine = true
  Suppressed = false
  Type = 0
FEATURE [Sketcher::SketchObject] Sketch080
  ArcFitTolerance = 1e-06
  AttachmentSupport = -> [Pad035]
  ExternalGeometry = -> [Pad035,CopyPocket012]
  FullyConstrained = true
  MakeInternals = false
  MapMode = 5
  Placement = pos=(9.77983e-08,-24.5,34.8536) rot=(1,0,0;1.5708rad)
  sketch-geometry (13):
    g0: LineSegment [constr] StartX=9 StartY=0 StartZ=0 EndX=9 EndY=5 EndZ=0
    g1: LineSegment [constr] StartX=9 StartY=5 StartZ=0 EndX=14 EndY=5 EndZ=0
    g2: LineSegment [constr] StartX=14 StartY=5 StartZ=0 EndX=14 EndY=10 EndZ=0
    g3: LineSegment [constr] StartX=14 StartY=10 StartZ=0 EndX=14 EndY=15 EndZ=0
    g4: LineSegment [constr] StartX=14 StartY=15 StartZ=0 EndX=14 EndY=20 EndZ=0
    g5: LineSegment [constr] StartX=14 StartY=20 StartZ=0 EndX=14 EndY=25 EndZ=0
    g6: LineSegment [constr] StartX=14 StartY=25 StartZ=0 EndX=14 EndY=30 EndZ=0
    g7: Circle CenterX=14 CenterY=30 CenterZ=0 NormalX=0 NormalY=0 NormalZ=1 AngleXU=0 Radius=1.3
    g8: Circle CenterX=14 CenterY=25 CenterZ=0 NormalX=0 NormalY=0 NormalZ=1 AngleXU=0 Radius=1.3
    g9: Circle CenterX=14 CenterY=20 CenterZ=0 NormalX=0 NormalY=0 NormalZ=1 AngleXU=0 Radius=1.3
    g10: Circle CenterX=14 CenterY=15 CenterZ=0 NormalX=0 NormalY=0 NormalZ=1 AngleXU=0 Radius=1.3
    g11: Circle CenterX=14 CenterY=10 CenterZ=0 NormalX=0 NormalY=0 NormalZ=1 AngleXU=0 Radius=1.3
    g12: Circle CenterX=14 CenterY=5 CenterZ=0 NormalX=0 NormalY=0 NormalZ=1 AngleXU=0 Radius=1.3
  constraints (33):
    c: Distance(g0) = 5
    c: Coincident(g0,g-3)
    c: PointOnObject(g0,g-3)
    c: Distance(g1) = 5
    c: Coincident(g1,g0)
    c: Horizontal(g1)
    c: Distance(g2) = 5
    c: Coincident(g2,g1)
    c: Vertical(g2)
    c: Distance(g3) = 5
    c: Coincident(g3,g2)
    c: Vertical(g3)
    c: Distance(g4) = 5
    c: Coincident(g4,g3)
    c: Vertical(g4)
    c: Distance(g5) = 5
    c: Coincident(g5,g4)
    c: Vertical(g5)
    c: Distance(g6) = 5
    c: Coincident(g6,g5)
    c: Vertical(g6)
    c: Diameter(g7) = 2.6
    c: Coincident(g7,g6)
    c: Diameter(g8) = 2.6
    c: Coincident(g8,g5)
    c: Diameter(g9) = 2.6
    c: Coincident(g9,g4)
    c: Diameter(g10) = 2.6
    c: Coincident(g10,g3)
    c: Diameter(g11) = 2.6
    c: Coincident(g11,g2)
    c: Diameter(g12) = 2.6
    c: Coincident(g12,g1)
FEATURE [PartDesign::Pocket] Pocket043
  BaseFeature = -> Pad035
  Direction = (0,1,-2e-16)
  Length = 5
  Length2 = 5
  Placement = pos=(9.77984e-08,-84,34.8536) rot=(0,0,1;3.14159rad)
  Profile = -> Sketch080
  ReferenceAxis = -> Sketch080 [N_Axis]
  Refine = true
  Suppressed = false
  Type = 0
FEATURE [PartDesign::LinearPattern] LinearPattern
  BaseFeature = -> Pocket043
  Direction = -> Sketch080 [H_Axis]
  Length = 55
  Mode = 0
  Occurrences = 12
  Offset = 5
  Originals = -> [Pocket043]
  Placement = pos=(9.77984e-08,-84,34.8536) rot=(0,0,1;3.14159rad)
  Refine = true
  Suppressed = false
  TransformMode = 0
FEATURE [PartDesign::ShapeBinder] CopyPocket031
  Placement = pos=(7.67535e-08,-84,27.3536) rot=(0,0,1;3.14159rad)
  TraceSupport = false
FEATURE [PartDesign::Plane] DatumPlane014
  AttachmentSupport = -> [CopyPocket031]
  Length = 130.8
  MapMode = 5
  Placement = pos=(9.77984e-08,-84,34.8536) rot=(0,0,1;3.14159rad)
  ResizeMode = 0
  Width = 130.8
FEATURE [Sketcher::SketchObject] Sketch081
  ArcFitTolerance = 1e-06
  AttachmentSupport = -> [DatumPlane014]
  ExternalGeometry = -> [CopyPocket031]
  FullyConstrained = true
  MakeInternals = false
  MapMode = 5
  Placement = pos=(9.77984e-08,-84,34.8536) rot=(0,0,1;3.14159rad)
  sketch-geometry (12):
    g0: LineSegment StartX=-84 StartY=-84 StartZ=0 EndX=-74 EndY=-84 EndZ=0
    g1: LineSegment StartX=7.11416e-08 StartY=-84 StartZ=0 EndX=-10 EndY=-84 EndZ=0
    g2: LineSegment StartX=-10 StartY=-84 StartZ=0 EndX=-10 EndY=-49 EndZ=0
    g3: LineSegment StartX=-74 StartY=-84 StartZ=0 EndX=-74 EndY=-49 EndZ=0
    g4: LineSegment StartX=-74 StartY=-49 StartZ=0 EndX=-10 EndY=-49 EndZ=0
    g5: LineSegment StartX=7.11416e-08 StartY=-84 StartZ=0 EndX=7.11416e-08 EndY=-34 EndZ=0
    g6: LineSegment StartX=7.11416e-08 StartY=-34 StartZ=0 EndX=-84 EndY=-34 EndZ=0
    g7: LineSegment StartX=-84 StartY=-34 StartZ=0 EndX=-84 EndY=-84 EndZ=0
    g8: Circle CenterX=-79 CenterY=-42 CenterZ=0 NormalX=0 NormalY=0 NormalZ=1 AngleXU=0 Radius=1.5
    g9: Circle CenterX=-79 CenterY=-79 CenterZ=0 NormalX=0 NormalY=0 NormalZ=1 AngleXU=0 Radius=1.5
    g10: Circle CenterX=-5 CenterY=-79 CenterZ=0 NormalX=0 NormalY=0 NormalZ=1 AngleXU=0 Radius=1.5
    g11: Circle CenterX=-5 CenterY=-42 CenterZ=0 NormalX=0 NormalY=0 NormalZ=1 AngleXU=0 Radius=1.5
  constraints (30):
    c: Distance(g0) = 10
    c: Coincident(g0,g-9)
    c: PointOnObject(g0,g-9)
    c: Distance(g1) = 10
    c: Coincident(g1,g-9)
    c: PointOnObject(g1,g-9)
    c: Distance(g2) = 35
    c: Coincident(g2,g1)
    c: Vertical(g2)
    c: Distance(g3) = 35
    c: Coincident(g3,g0)
    c: Vertical(g3)
    c: Coincident(g4,g3)
    c: Coincident(g4,g2)
    c: Distance(g5) = 50
    c: Coincident(g5,g1)
    c: PointOnObject(g5,g-8)
    c: Coincident(g6,g5)
    c: PointOnObject(g6,g-7)
    c: Horizontal(g6)
    c: Coincident(g7,g6)
    c: Coincident(g7,g0)
    c: Diameter(g8) = 3
    c: Coincident(g8,g-6)
    c: Diameter(g9) = 3
    c: Coincident(g9,g-3)
    c: Diameter(g10) = 3
    c: Coincident(g10,g-4)
    c: Diameter(g11) = 3
    c: Coincident(g11,g-5)
FEATURE [PartDesign::Pad] Pad036
  Direction = (2.80598e-09,0,1)
  Length = 5
  Length2 = 10
  Placement = pos=(9.77984e-08,-84,34.8536) rot=(0,0,1;3.14159rad)
  Profile = -> Sketch081
  ReferenceAxis = -> Sketch081 [N_Axis]
  Refine = true
  Suppressed = false
  Type = 0
FEATURE [Sketcher::SketchObject] Sketch082
  ArcFitTolerance = 1e-06
  AttachmentSupport = -> [Pad036]
  ExternalGeometry = -> [Pad036]
  FullyConstrained = true
  MakeInternals = false
  MapMode = 5
  Placement = pos=(1.11828e-07,-84,39.8536) rot=(0,0,1;3.14159rad)
  sketch-geometry (12):
    g0: Circle CenterX=-79 CenterY=-42 CenterZ=0 NormalX=0 NormalY=0 NormalZ=1 AngleXU=0 Radius=3.25
    g1: Circle CenterX=-79 CenterY=-79 CenterZ=0 NormalX=0 NormalY=0 NormalZ=1 AngleXU=0 Radius=3.25
    g2: Circle CenterX=-5 CenterY=-79 CenterZ=0 NormalX=0 NormalY=0 NormalZ=1 AngleXU=0 Radius=3.25
    g3: Circle CenterX=-5 CenterY=-42 CenterZ=0 NormalX=0 NormalY=0 NormalZ=1 AngleXU=0 Radius=3.25
    g4: LineSegment StartX=-84 StartY=-34 StartZ=0 EndX=7.11416e-08 EndY=-34 EndZ=0
    g5: LineSegment StartX=7.11416e-08 StartY=-34 StartZ=0 EndX=7.11416e-08 EndY=-84 EndZ=0
    g6: LineSegment StartX=7.11416e-08 StartY=-84 StartZ=0 EndX=-10 EndY=-84 EndZ=0
    g7: LineSegment StartX=-10 StartY=-84 StartZ=0 EndX=-10 EndY=-49 EndZ=0
    g8: LineSegment StartX=-10 StartY=-49 StartZ=0 EndX=-74 EndY=-49 EndZ=0
    g9: LineSegment StartX=-74 StartY=-49 StartZ=0 EndX=-74 EndY=-84 EndZ=0
    g10: LineSegment StartX=-74 StartY=-84 StartZ=0 EndX=-84 EndY=-84 EndZ=0
    g11: LineSegment StartX=-84 StartY=-84 StartZ=0 EndX=-84 EndY=-34 EndZ=0
  constraints (24):
    c: Diameter(g0) = 6.5
    c: Coincident(g0,g-13)
    c: Diameter(g1) = 6.5
    c: Coincident(g1,g-10)
    c: Diameter(g2) = 6.5
    c: Coincident(g2,g-4)
    c: Diameter(g3) = 6.5
    c: Coincident(g3,g-3)
    c: Coincident(g-14,g4)
    c: Coincident(g4,g-15)
    c: Coincident(g4,g5)
    c: Coincident(g5,g-15)
    c: Coincident(g5,g6)
    c: Coincident(g6,g-6)
    c: Coincident(g6,g7)
    c: Coincident(g7,g-7)
    c: Coincident(g7,g8)
    c: Coincident(g8,g-8)
    c: Coincident(g8,g9)
    c: Coincident(g9,g-9)
    c: Coincident(g9,g10)
    c: Coincident(g10,g-14)
    c: Coincident(g10,g11)
    c: Coincident(g11,g4)
FEATURE [PartDesign::Pad] Pad037
  BaseFeature = -> Pad036
  Direction = (2.80598e-09,0,1)
  Length = 10
  Length2 = 10
  Placement = pos=(9.77984e-08,-84,34.8536) rot=(0,0,1;3.14159rad)
  Profile = -> Sketch082
  ReferenceAxis = -> Sketch082 [N_Axis]
  Refine = true
  Suppressed = false
  Type = 0
FEATURE [Sketcher::SketchObject] Sketch083
  ArcFitTolerance = 1e-06
  AttachmentSupport = -> [Pad037]
  ExternalGeometry = -> [Pad037,CopyPocket031]
  FullyConstrained = true
  MakeInternals = false
  MapMode = 5
  Placement = pos=(9.77984e-08,-50,34.8536) rot=(1,0,0;1.5708rad)
  sketch-geometry (4):
    g0: LineSegment StartX=84 StartY=-4.26e-14 StartZ=0 EndX=84 EndY=2.5 EndZ=0
    g1: LineSegment StartX=0 StartY=0 StartZ=0 EndX=-7.11416e-08 EndY=2.5 EndZ=0
    g2: LineSegment StartX=-7.11416e-08 StartY=2.5 StartZ=0 EndX=84 EndY=2.5 EndZ=0
    g3: LineSegment StartX=84 StartY=-4.26e-14 StartZ=0 EndX=0 EndY=0 EndZ=0
  constraints (10):
    c: Distance(g0) = 2.5
    c: Coincident(g0,g-5)
    c: PointOnObject(g0,g-4)
    c: Distance(g1) = 2.5
    c: Coincident(g1,g-1)
    c: PointOnObject(g1,g-3)
    c: Coincident(g2,g1)
    c: Coincident(g2,g0)
    c: Coincident(g3,g0)
    c: Coincident(g3,g1)
FEATURE [PartDesign::Pad] Pad038
  BaseFeature = -> Pad037
  Direction = (0,-1,2e-16)
  Length = 5
  Length2 = 10
  Placement = pos=(9.77984e-08,-84,34.8536) rot=(0,0,1;3.14159rad)
  Profile = -> Sketch083
  ReferenceAxis = -> Sketch083 [N_Axis]
  Refine = true
  Suppressed = false
  Type = 0
FEATURE [Sketcher::SketchObject] Sketch084
  ArcFitTolerance = 1e-06
  AttachmentSupport = -> [Pad038]
  ExternalGeometry = -> [Pad038]
  FullyConstrained = true
  MakeInternals = false
  MapMode = 5
  Placement = pos=(9.77984e-08,-50,34.8536) rot=(1,0,0;1.5708rad)
  sketch-geometry (4):
    g0: LineSegment StartX=-7.11416e-08 StartY=2.5 StartZ=0 EndX=0 EndY=86.5 EndZ=0
    g1: LineSegment StartX=0 StartY=86.5 StartZ=0 EndX=84 EndY=86.5 EndZ=0
    g2: LineSegment StartX=84 StartY=86.5 StartZ=0 EndX=84 EndY=2.5 EndZ=0
    g3: LineSegment StartX=84 StartY=2.5 StartZ=0 EndX=-7.11416e-08 EndY=2.5 EndZ=0
  constraints (10):
    c: Distance(g0) = 84
    c: Coincident(g0,g-3)
    c: PointOnObject(g0,g-2)
    c: Distance(g1) = 84
    c: Coincident(g1,g0)
    c: Horizontal(g1)
    c: Coincident(g2,g1)
    c: Coincident(g2,g-4)
    c: Coincident(g3,g2)
    c: Coincident(g3,g0)
FEATURE [PartDesign::Pad] Pad039
  BaseFeature = -> Pad038
  Direction = (0,-1,2e-16)
  Length = 4
  Length2 = 10
  Placement = pos=(9.77984e-08,-84,34.8536) rot=(0,0,1;3.14159rad)
  Profile = -> Sketch084
  ReferenceAxis = -> Sketch084 [N_Axis]
  Refine = true
  Reversed = true
  Suppressed = false
  Type = 0
FEATURE [PartDesign::Pad] Pad040
  BaseFeature = -> Pad039
  Direction = (0,-1,0)
  Length = 1
  Length2 = 10
  Placement = pos=(9.77984e-08,-84,34.8536) rot=(0,0,1;3.14159rad)
  Profile = -> Pad039 [Face26]
  Refine = true
  Suppressed = false
  Type = 0
FEATURE [Sketcher::SketchObject] Sketch085
  ArcFitTolerance = 1e-06
  AttachmentSupport = -> [Pad040]
  ExternalGeometry = -> [Pad040]
  FullyConstrained = true
  MakeInternals = false
  MapMode = 5
  Placement = pos=(9.77984e-08,-51,34.8536) rot=(1,0,0;1.5708rad)
  sketch-geometry (20):
    g0: LineSegment [constr] StartX=0 StartY=86.5 StartZ=0 EndX=0 EndY=81.5 EndZ=0
    g1: LineSegment [constr] StartX=0 StartY=81.5 StartZ=0 EndX=5 EndY=81.5 EndZ=0
    g2: LineSegment [constr] StartX=5 StartY=81.5 StartZ=0 EndX=5 EndY=86.5 EndZ=0
    g3: LineSegment [constr] StartX=5 StartY=86.5 StartZ=0 EndX=0 EndY=86.5 EndZ=0
    g4: LineSegment [constr] StartX=84 StartY=86.5 StartZ=0 EndX=79 EndY=86.5 EndZ=0
    g5: LineSegment [constr] StartX=79 StartY=86.5 StartZ=0 EndX=79 EndY=81.5 EndZ=0
    g6: LineSegment [constr] StartX=79 StartY=81.5 StartZ=0 EndX=84 EndY=81.5 EndZ=0
    g7: LineSegment [constr] StartX=84 StartY=81.5 StartZ=0 EndX=84 EndY=86.5 EndZ=0
    g8: LineSegment [constr] StartX=84 StartY=2.5 StartZ=0 EndX=84 EndY=7.5 EndZ=0
    g9: LineSegment [constr] StartX=84 StartY=7.5 StartZ=0 EndX=79 EndY=7.5 EndZ=0
    g10: LineSegment [constr] StartX=79 StartY=7.5 StartZ=0 EndX=79 EndY=2.5 EndZ=0
    g11: LineSegment [constr] StartX=79 StartY=2.5 StartZ=0 EndX=84 EndY=2.5 EndZ=0
    g12: LineSegment [constr] StartX=-7.11416e-08 StartY=2.5 StartZ=0 EndX=5 EndY=2.5 EndZ=0
    g13: LineSegment [constr] StartX=5 StartY=2.5 StartZ=0 EndX=5 EndY=7.5 EndZ=0
    g14: LineSegment [constr] StartX=5 StartY=7.5 StartZ=0 EndX=-7.11416e-08 EndY=7.5 EndZ=0
    g15: LineSegment [constr] StartX=-7.11416e-08 StartY=7.5 StartZ=0 EndX=-7.11416e-08 EndY=2.5 EndZ=0
    g16: Circle CenterX=5 CenterY=81.5 CenterZ=0 NormalX=0 NormalY=0 NormalZ=1 AngleXU=0 Radius=1.3
    g17: Circle CenterX=79 CenterY=81.5 CenterZ=0 NormalX=0 NormalY=0 NormalZ=1 AngleXU=0 Radius=1.3
    g18: Circle CenterX=5 CenterY=7.5 CenterZ=0 NormalX=0 NormalY=0 NormalZ=1 AngleXU=0 Radius=1.3
    g19: Circle CenterX=79 CenterY=7.5 CenterZ=0 NormalX=0 NormalY=0 NormalZ=1 AngleXU=0 Radius=1.3
  constraints (52):
    c: Coincident(g0,g1)
    c: Coincident(g1,g2)
    c: Coincident(g2,g3)
    c: Coincident(g3,g0)
    c: Vertical(g0)
    c: Vertical(g2)
    c: Horizontal(g1)
    c: Horizontal(g3)
    c: Distance(g0,g2) = 5
    c: Distance(g1,g3) = 5
    c: Coincident(g0,g-4)
    c: Coincident(g4,g5)
    c: Coincident(g5,g6)
    c: Coincident(g6,g7)
    c: Coincident(g7,g4)
    c: Horizontal(g4)
    c: Horizontal(g6)
    c: Vertical(g5)
    c: Vertical(g7)
    c: Distance(g5,g7) = 5
    c: Distance(g4,g6) = 5
    c: Coincident(g4,g-4)
    c: Coincident(g8,g9)
    c: Coincident(g9,g10)
    c: Coincident(g10,g11)
    c: Coincident(g11,g8)
    c: Vertical(g8)
    c: Vertical(g10)
    c: Horizontal(g9)
    c: Horizontal(g11)
    c: Distance(g8,g10) = 5
    c: Distance(g9,g11) = 5
    c: Coincident(g8,g-5)
    c: Coincident(g12,g13)
    c: Coincident(g13,g14)
    c: Coincident(g14,g15)
    c: Coincident(g15,g12)
    c: Horizontal(g12)
    c: Horizontal(g14)
    c: Vertical(g13)
    c: Vertical(g15)
    c: Distance(g13,g15) = 5
    c: Distance(g12,g14) = 5
    c: Coincident(g12,g-5)
    c: Diameter(g16) = 2.6
    c: Coincident(g16,g1)
    c: Diameter(g17) = 2.6
    c: Coincident(g17,g5)
    c: Diameter(g18) = 2.6
    c: Coincident(g18,g13)
    c: Diameter(g19) = 2.6
    c: Coincident(g19,g9)
FEATURE [PartDesign::Pocket] Pocket044
  BaseFeature = -> Pad040
  Direction = (0,1,-2e-16)
  Length = 5
  Length2 = 5
  Placement = pos=(9.77984e-08,-84,34.8536) rot=(0,0,1;3.14159rad)
  Profile = -> Sketch085
  ReferenceAxis = -> Sketch085 [N_Axis]
  Refine = true
  Suppressed = false
  Type = 0
FEATURE [Sketcher::SketchObject] Sketch086
  ArcFitTolerance = 1e-06
  AttachmentSupport = -> [Pocket044]
  ExternalGeometry = -> [Pocket044]
  FullyConstrained = true
  MakeInternals = false
  MapMode = 5
  Placement = pos=(1.39888e-07,-84,49.8536) rot=(0,0,1;3.14159rad)
  sketch-geometry (6):
    g0: LineSegment [constr] StartX=-74 StartY=-49 StartZ=0 EndX=-64 EndY=-49 EndZ=0
    g1: LineSegment [constr] StartX=-10 StartY=-49 StartZ=0 EndX=-20 EndY=-49 EndZ=0
    g2: LineSegment StartX=-64 StartY=-49 StartZ=0 EndX=-20 EndY=-49 EndZ=0
    g3: LineSegment StartX=-20 StartY=-49 StartZ=0 EndX=-20 EndY=-38 EndZ=0
    g4: LineSegment StartX=-64 StartY=-49 StartZ=0 EndX=-64 EndY=-38 EndZ=0
    g5: LineSegment StartX=-64 StartY=-38 StartZ=0 EndX=-20 EndY=-38 EndZ=0
  constraints (16):
    c: Distance(g0) = 10
    c: Coincident(g0,g-4)
    c: PointOnObject(g0,g-4)
    c: Distance(g1) = 10
    c: Coincident(g1,g-4)
    c: PointOnObject(g1,g-4)
    c: Coincident(g2,g0)
    c: Coincident(g2,g1)
    c: Coincident(g3,g1)
    c: PointOnObject(g3,g-3)
    c: Vertical(g3)
    c: Coincident(g4,g0)
    c: PointOnObject(g4,g-3)
    c: Vertical(g4)
    c: Coincident(g5,g4)
    c: Coincident(g5,g3)
FEATURE [PartDesign::Pad] Pad041
  BaseFeature = -> Pocket044
  Direction = (2.80598e-09,0,1)
  Length = 50
  Length2 = 10
  Placement = pos=(9.77984e-08,-84,34.8536) rot=(0,0,1;3.14159rad)
  Profile = -> Sketch086
  ReferenceAxis = -> Sketch086 [N_Axis]
  Refine = true
  Suppressed = false
  Type = 0
FEATURE [Sketcher::SketchObject] Sketch087
  ArcFitTolerance = 1e-06
  AttachmentSupport = -> [Pad041]
  ExternalGeometry = -> [Pad041]
  FullyConstrained = true
  MakeInternals = false
  MapMode = 5
  Placement = pos=(64,-84,34.8536) rot=(0.57735,0.57735,0.57735;2.0944rad)
  sketch-geometry (3):
    g0: LineSegment StartX=49 StartY=65 StartZ=0 EndX=38 EndY=86.5 EndZ=0
    g1: LineSegment StartX=49 StartY=65 StartZ=0 EndX=38 EndY=65 EndZ=0
    g2: LineSegment StartX=38 StartY=65 StartZ=0 EndX=38 EndY=86.5 EndZ=0
  constraints (6):
    c: Coincident(g0,g-3)
    c: Coincident(g0,g-4)
    c: Coincident(g1,g0)
    c: Coincident(g1,g-3)
    c: Coincident(g2,g1)
    c: Coincident(g2,g0)
FEATURE [PartDesign::Pad] Pad042
  BaseFeature = -> Pad041
  Direction = (1,1e-16,-2.80598e-09)
  Length = 44
  Length2 = 10
  Placement = pos=(9.77984e-08,-84,34.8536) rot=(0,0,1;3.14159rad)
  Profile = -> Sketch087
  ReferenceAxis = -> Sketch087 [N_Axis]
  Refine = true
  Reversed = true
  Suppressed = false
  Type = 0
FEATURE [PartDesign::Chamfer] Chamfer020
  Angle = 45
  Base = -> Pad042 [Edge37,Edge39]
  BaseFeature = -> Pad042
  ChamferType = 0
  FlipDirection = false
  Placement = pos=(9.77984e-08,-84,34.8536) rot=(0,0,1;3.14159rad)
  Refine = true
  Size = 4
  Size2 = 1
  SupportTransform = false
  Suppressed = false
  UseAllEdges = false
FEATURE [PartDesign::Chamfer] Chamfer021
  Angle = 45
  Base = -> Chamfer020 [Edge43,Edge21]
  BaseFeature = -> Chamfer020
  ChamferType = 0
  FlipDirection = false
  Placement = pos=(9.77984e-08,-84,34.8536) rot=(0,0,1;3.14159rad)
  Refine = true
  Size = 4
  Size2 = 1
  SupportTransform = false
  Suppressed = false
  UseAllEdges = false
FEATURE [PartDesign::Chamfer] Chamfer022
  Angle = 45
  Base = -> Chamfer021 [Edge65,Edge71]
  BaseFeature = -> Chamfer021
  ChamferType = 0
  FlipDirection = false
  Placement = pos=(9.77984e-08,-84,34.8536) rot=(0,0,1;3.14159rad)
  Refine = true
  Size = 6
  Size2 = 1
  SupportTransform = false
  Suppressed = false
  UseAllEdges = false
FEATURE [PartDesign::Chamfer] Chamfer023
  Angle = 45
  Base = -> Chamfer022 [Edge24,Edge25]
  BaseFeature = -> Chamfer022
  ChamferType = 0
  FlipDirection = false
  Placement = pos=(9.77984e-08,-84,34.8536) rot=(0,0,1;3.14159rad)
  Refine = true
  Size = 16
  Size2 = 1
  SupportTransform = false
  Suppressed = false
  UseAllEdges = false
FEATURE [PartDesign::Chamfer] Chamfer024
  Angle = 45
  Base = -> Chamfer023 [Edge74,Edge77,Edge12,Edge16]
  BaseFeature = -> Chamfer023
  ChamferType = 0
  FlipDirection = false
  Placement = pos=(9.77984e-08,-84,34.8536) rot=(0,0,1;3.14159rad)
  Refine = true
  Size = 2
  Size2 = 1
  SupportTransform = false
  Suppressed = false
  UseAllEdges = false
FEATURE [PartDesign::Body] Body013  label="90 Degree Plate Adaptor"
  AllowCompound = false
  Group = -> [DatumPlane014,CopyPocket031,Sketch081,Pad036,Sketch082,Pad037,Sketch083,Pad038,Sketch084,Pad039,Pad040,Sketch085,Pocket044,Sketch086,Pad041,Sketch087,Pad042,Chamfer020,Chamfer021,Chamfer022,Chamfer023,Chamfer024]
  Origin = -> Origin013
  Tip = -> Chamfer024
FEATURE [PartDesign::ShapeBinder] CopyPad032
  Placement = pos=(0,0,0) rot=(0,0.707107,0.707107;3.14159rad)
  TraceSupport = false
FEATURE [PartDesign::Plane] DatumPlane015
  AttachmentSupport = -> [CopyPad032]
  Length = 175.566
  MapMode = 5
  Placement = pos=(-3.2e-15,0,0) rot=(0,-1,0;1.5708rad)
  ResizeMode = 0
  Width = 90.8159
FEATURE [Sketcher::SketchObject] Sketch088
  ArcFitTolerance = 1e-06
  AttachmentSupport = -> [DatumPlane015]
  ExternalGeometry = -> [CopyPad032]
  FullyConstrained = true
  MakeInternals = false
  MapMode = 5
  Placement = pos=(-3.2e-15,0,0) rot=(0,-1,0;1.5708rad)
  sketch-geometry (11):
    g0: LineSegment StartX=40.75 StartY=45 StartZ=0 EndX=40.75 EndY=40 EndZ=0
    g1: LineSegment StartX=40.75 StartY=40 StartZ=0 EndX=20.75 EndY=40 EndZ=0
    g2: LineSegment StartX=20.75 StartY=40 StartZ=0 EndX=20.75 EndY=37 EndZ=0
    g3: LineSegment StartX=20.75 StartY=37 StartZ=0 EndX=40.75 EndY=37 EndZ=0
    g4: LineSegment StartX=40.75 StartY=37 StartZ=0 EndX=45.75 EndY=37 EndZ=0
    g5: LineSegment StartX=40.75 StartY=45 StartZ=0 EndX=45.75 EndY=45 EndZ=0
    g6: LineSegment [constr] StartX=45.75 StartY=45 StartZ=0 EndX=45.75 EndY=40 EndZ=0
    g7: LineSegment StartX=45.75 StartY=37 StartZ=0 EndX=45.75 EndY=40 EndZ=0
    g8: LineSegment StartX=45.75 StartY=45 StartZ=0 EndX=129.75 EndY=45 EndZ=0
    g9: LineSegment StartX=45.75 StartY=40 StartZ=0 EndX=129.75 EndY=40 EndZ=0
    g10: LineSegment StartX=129.75 StartY=45 StartZ=0 EndX=129.75 EndY=40 EndZ=0
  constraints (30):
    c: Coincident(g0,g-3)
    c: Coincident(g0,g-4)
    c: Distance(g1) = 20
    c: Coincident(g1,g0)
    c: PointOnObject(g1,g-4)
    c: Distance(g2) = 3
    c: Coincident(g2,g1)
    c: Vertical(g2)
    c: Distance(g3) = 20
    c: Coincident(g3,g2)
    c: Horizontal(g3)
    c: Distance(g4) = 5
    c: Coincident(g4,g3)
    c: Horizontal(g4)
    c: Distance(g5) = 5
    c: Coincident(g5,g0)
    c: Horizontal(g5)
    c: Distance(g6) = 5
    c: Coincident(g6,g5)
    c: Vertical(g6)
    c: Coincident(g7,g4)
    c: Coincident(g7,g6)
    c: Distance(g8) = 84
    c: Coincident(g8,g5)
    c: Horizontal(g8)
    c: Distance(g9) = 84
    c: Coincident(g9,g6)
    c: Horizontal(g9)
    c: Coincident(g10,g8)
    c: Coincident(g10,g9)
FEATURE [PartDesign::Pad] Pad043
  Direction = (-1,0,2e-16)
  Length = 84
  Length2 = 10
  Placement = pos=(-3.2e-15,0,0) rot=(0,-1,0;1.5708rad)
  Profile = -> Sketch088
  ReferenceAxis = -> Sketch088 [N_Axis]
  Refine = true
  Reversed = true
  Suppressed = false
  Type = 0
FEATURE [Sketcher::SketchObject] Sketch089
  ArcFitTolerance = 1e-06
  AttachmentSupport = -> [Pad043]
  ExternalGeometry = -> [Pad043]
  FullyConstrained = true
  MakeInternals = false
  MapMode = 5
  Placement = pos=(-3.2e-15,37,0) rot=(0.57735,-0.57735,0.57735;2.0944rad)
  sketch-geometry (12):
    g0: LineSegment [constr] StartX=20.75 StartY=0 StartZ=0 EndX=40.75 EndY=0 EndZ=0
    g1: LineSegment [constr] StartX=40.75 StartY=0 StartZ=0 EndX=40.75 EndY=-84 EndZ=0
    g2: LineSegment [constr] StartX=40.75 StartY=0 StartZ=0 EndX=35.75 EndY=0 EndZ=0
    g3: LineSegment [constr] StartX=35.75 StartY=0 StartZ=0 EndX=35.75 EndY=-5 EndZ=0
    g4: LineSegment [constr] StartX=35.75 StartY=-5 StartZ=0 EndX=40.75 EndY=-5 EndZ=0
    g5: LineSegment [constr] StartX=40.75 StartY=-5 StartZ=0 EndX=40.75 EndY=0 EndZ=0
    g6: LineSegment [constr] StartX=40.75 StartY=-84 StartZ=0 EndX=40.75 EndY=-79 EndZ=0
    g7: LineSegment [constr] StartX=40.75 StartY=-79 StartZ=0 EndX=35.75 EndY=-79 EndZ=0
    g8: LineSegment [constr] StartX=35.75 StartY=-79 StartZ=0 EndX=35.75 EndY=-84 EndZ=0
    g9: LineSegment [constr] StartX=35.75 StartY=-84 StartZ=0 EndX=40.75 EndY=-84 EndZ=0
    g10: Circle CenterX=35.75 CenterY=-79 CenterZ=0 NormalX=0 NormalY=0 NormalZ=1 AngleXU=0 Radius=1.5
    g11: Circle CenterX=35.75 CenterY=-5 CenterZ=0 NormalX=0 NormalY=0 NormalZ=1 AngleXU=0 Radius=1.5
  constraints (32):
    c: Distance(g0) = 20
    c: Coincident(g0,g-3)
    c: PointOnObject(g0,g-1)
    c: Coincident(g1,g0)
    c: PointOnObject(g1,g-4)
    c: Vertical(g1)
    c: Coincident(g2,g3)
    c: Coincident(g3,g4)
    c: Coincident(g4,g5)
    c: Coincident(g5,g2)
    c: Horizontal(g2)
    c: Horizontal(g4)
    c: Vertical(g3)
    c: Vertical(g5)
    c: Distance(g3,g5) = 5
    c: Distance(g2,g4) = 5
    c: Coincident(g2,g0)
    c: Coincident(g6,g7)
    c: Coincident(g7,g8)
    c: Coincident(g8,g9)
    c: Coincident(g9,g6)
    c: Vertical(g6)
    c: Vertical(g8)
    c: Horizontal(g7)
    c: Horizontal(g9)
    c: Distance(g6,g8) = 5
    c: Distance(g7,g9) = 5
    c: Coincident(g6,g1)
    c: Diameter(g10) = 3
    c: Coincident(g10,g7)
    c: Diameter(g11) = 3
    c: Coincident(g11,g3)
FEATURE [PartDesign::Pocket] Pocket045
  BaseFeature = -> Pad043
  Direction = (0,1,0)
  Length = 5
  Length2 = 5
  Placement = pos=(-3.2e-15,0,0) rot=(0,-1,0;1.5708rad)
  Profile = -> Sketch089
  ReferenceAxis = -> Sketch089 [N_Axis]
  Refine = true
  Suppressed = false
  Type = 1
FEATURE [Sketcher::SketchObject] Sketch090
  ArcFitTolerance = 1e-06
  AttachmentSupport = -> [Pocket045]
  ExternalGeometry = -> [Pocket045]
  FullyConstrained = true
  MakeInternals = false
  MapMode = 5
  Placement = pos=(-3.2e-15,37,0) rot=(0.57735,-0.57735,0.57735;2.0944rad)
  sketch-geometry (6):
    g0: Circle CenterX=35.75 CenterY=-5 CenterZ=0 NormalX=0 NormalY=0 NormalZ=1 AngleXU=0 Radius=3.25
    g1: Circle CenterX=35.75 CenterY=-79 CenterZ=0 NormalX=0 NormalY=0 NormalZ=1 AngleXU=0 Radius=3.25
    g2: LineSegment StartX=20.75 StartY=0 StartZ=0 EndX=20.75 EndY=-84 EndZ=0
    g3: LineSegment StartX=20.75 StartY=-84 StartZ=0 EndX=45.75 EndY=-84 EndZ=0
    g4: LineSegment StartX=45.75 StartY=-84 StartZ=0 EndX=45.75 EndY=0 EndZ=0
    g5: LineSegment StartX=45.75 StartY=0 StartZ=0 EndX=20.75 EndY=0 EndZ=0
  constraints (14):
    c: Diameter(g0) = 6.5
    c: Coincident(g0,g-6)
    c: Diameter(g1) = 6.5
    c: Coincident(g1,g-5)
    c: Coincident(g2,g3)
    c: Coincident(g3,g4)
    c: Coincident(g4,g5)
    c: Coincident(g5,g2)
    c: Vertical(g2)
    c: Vertical(g4)
    c: Horizontal(g3)
    c: Horizontal(g5)
    c: Coincident(g2,g-3)
    c: Coincident(g3,g-4)
FEATURE [PartDesign::Pad] Pad044
  BaseFeature = -> Pocket045
  Direction = (0,-1,0)
  Length = 3
  Length2 = 10
  Placement = pos=(-3.2e-15,0,0) rot=(0,-1,0;1.5708rad)
  Profile = -> Sketch090
  ReferenceAxis = -> Sketch090 [N_Axis]
  Refine = true
  Suppressed = false
  Type = 0
FEATURE [Sketcher::SketchObject] Sketch091
  ArcFitTolerance = 1e-06
  AttachmentSupport = -> [Pad044]
  ExternalGeometry = -> [Pad044]
  FullyConstrained = true
  MakeInternals = false
  MapMode = 5
  Placement = pos=(-3.2e-15,40,0) rot=(0.57735,-0.57735,0.57735;2.0944rad)
  sketch-geometry (20):
    g0: LineSegment [constr] StartX=45.75 StartY=0 StartZ=0 EndX=45.75 EndY=-5 EndZ=0
    g1: LineSegment [constr] StartX=45.75 StartY=-5 StartZ=0 EndX=50.75 EndY=-5 EndZ=0
    g2: LineSegment [constr] StartX=50.75 StartY=-5 StartZ=0 EndX=50.75 EndY=0 EndZ=0
    g3: LineSegment [constr] StartX=50.75 StartY=0 StartZ=0 EndX=45.75 EndY=0 EndZ=0
    g4: LineSegment [constr] StartX=129.75 StartY=0 StartZ=0 EndX=124.75 EndY=0 EndZ=0
    g5: LineSegment [constr] StartX=124.75 StartY=0 StartZ=0 EndX=124.75 EndY=-5 EndZ=0
    g6: LineSegment [constr] StartX=124.75 StartY=-5 StartZ=0 EndX=129.75 EndY=-5 EndZ=0
    g7: LineSegment [constr] StartX=129.75 StartY=-5 StartZ=0 EndX=129.75 EndY=0 EndZ=0
    g8: LineSegment [constr] StartX=129.75 StartY=-84 StartZ=0 EndX=129.75 EndY=-79 EndZ=0
    g9: LineSegment [constr] StartX=129.75 StartY=-79 StartZ=0 EndX=124.75 EndY=-79 EndZ=0
    g10: LineSegment [constr] StartX=124.75 StartY=-79 StartZ=0 EndX=124.75 EndY=-84 EndZ=0
    g11: LineSegment [constr] StartX=124.75 StartY=-84 StartZ=0 EndX=129.75 EndY=-84 EndZ=0
    g12: LineSegment [constr] StartX=45.75 StartY=-84 StartZ=0 EndX=50.75 EndY=-84 EndZ=0
    g13: LineSegment [constr] StartX=50.75 StartY=-84 StartZ=0 EndX=50.75 EndY=-79 EndZ=0
    g14: LineSegment [constr] StartX=50.75 StartY=-79 StartZ=0 EndX=45.75 EndY=-79 EndZ=0
    g15: LineSegment [constr] StartX=45.75 StartY=-79 StartZ=0 EndX=45.75 EndY=-84 EndZ=0
    g16: Circle CenterX=50.75 CenterY=-5 CenterZ=0 NormalX=0 NormalY=0 NormalZ=1 AngleXU=0 Radius=1.3
    g17: Circle CenterX=50.75 CenterY=-79 CenterZ=0 NormalX=0 NormalY=0 NormalZ=1 AngleXU=0 Radius=1.3
    g18: Circle CenterX=124.75 CenterY=-79 CenterZ=0 NormalX=0 NormalY=0 NormalZ=1 AngleXU=0 Radius=1.3
    g19: Circle CenterX=124.75 CenterY=-5 CenterZ=0 NormalX=0 NormalY=0 NormalZ=1 AngleXU=0 Radius=1.3
  constraints (52):
    c: Coincident(g0,g1)
    c: Coincident(g1,g2)
    c: Coincident(g2,g3)
    c: Coincident(g3,g0)
    c: Vertical(g0)
    c: Vertical(g2)
    c: Horizontal(g1)
    c: Horizontal(g3)
    c: Distance(g0,g2) = 5
    c: Distance(g1,g3) = 5
    c: Coincident(g0,g-4)
    c: Coincident(g4,g5)
    c: Coincident(g5,g6)
    c: Coincident(g6,g7)
    c: Coincident(g7,g4)
    c: Horizontal(g4)
    c: Horizontal(g6)
    c: Vertical(g5)
    c: Vertical(g7)
    c: Distance(g5,g7) = 5
    c: Distance(g4,g6) = 5
    c: Coincident(g4,g-3)
    c: Coincident(g8,g9)
    c: Coincident(g9,g10)
    c: Coincident(g10,g11)
    c: Coincident(g11,g8)
    c: Vertical(g8)
    c: Vertical(g10)
    c: Horizontal(g9)
    c: Horizontal(g11)
    c: Distance(g8,g10) = 5
    c: Distance(g9,g11) = 5
    c: Coincident(g8,g-3)
    c: Coincident(g12,g13)
    c: Coincident(g13,g14)
    c: Coincident(g14,g15)
    c: Coincident(g15,g12)
    c: Horizontal(g12)
    c: Horizontal(g14)
    c: Vertical(g13)
    c: Vertical(g15)
    c: Distance(g13,g15) = 5
    c: Distance(g12,g14) = 5
    c: Coincident(g12,g-4)
    c: Diameter(g16) = 2.6
    c: Coincident(g16,g1)
    c: Diameter(g17) = 2.6
    c: Coincident(g17,g13)
    c: Diameter(g18) = 2.6
    c: Coincident(g18,g9)
    c: Diameter(g19) = 2.6
    c: Coincident(g19,g5)
FEATURE [PartDesign::Pocket] Pocket046
  BaseFeature = -> Pad044
  Direction = (0,1,0)
  Length = 5
  Length2 = 5
  Placement = pos=(-3.2e-15,0,0) rot=(0,-1,0;1.5708rad)
  Profile = -> Sketch091
  ReferenceAxis = -> Sketch091 [N_Axis]
  Refine = true
  Suppressed = false
  Type = 1
FEATURE [PartDesign::Pocket] Pocket047
  BaseFeature = -> Pocket046
  Direction = (-3e-16,-4.1e-15,-1)
  Length = 0.25
  Length2 = 5
  Placement = pos=(-3.2e-15,0,0) rot=(0,-1,0;1.5708rad)
  Profile = -> Pocket046 [Face15]
  Refine = true
  Suppressed = false
  Type = 0
FEATURE [PartDesign::ShapeBinder] CopyPad033
  Placement = pos=(0,0,0) rot=(0,0.707107,0.707107;3.14159rad)
  TraceSupport = false
FEATURE [PartDesign::Plane] DatumPlane016
  AttachmentSupport = -> [CopyPad033]
  Length = 134.975
  MapMode = 5
  Placement = pos=(3.9e-15,45,-1e-14) rot=(0,0.707107,0.707107;3.14159rad)
  ResizeMode = 0
  Width = 180.725
FEATURE [Sketcher::SketchObject] Sketch092
  ArcFitTolerance = 1e-06
  AttachmentSupport = -> [DatumPlane016]
  ExternalGeometry = -> [CopyPad033]
  FullyConstrained = true
  MakeInternals = false
  MapMode = 5
  Placement = pos=(3.9e-15,45,-1e-14) rot=(0,0.707107,0.707107;3.14159rad)
  sketch-geometry (8):
    g0: LineSegment [constr] StartX=-79 StartY=35.75 StartZ=0 EndX=-79 EndY=45.75 EndZ=0
    g1: LineSegment [constr] StartX=-5 StartY=35.75 StartZ=0 EndX=-5 EndY=45.75 EndZ=0
    g2: Circle CenterX=-79 CenterY=45.75 CenterZ=0 NormalX=0 NormalY=0 NormalZ=1 AngleXU=0 Radius=1.3
    g3: Circle CenterX=-5 CenterY=45.75 CenterZ=0 NormalX=0 NormalY=0 NormalZ=1 AngleXU=0 Radius=1.3
    g4: LineSegment [constr] StartX=-79 StartY=45.75 StartZ=0 EndX=-79 EndY=119.75 EndZ=0
    g5: LineSegment [constr] StartX=-5 StartY=45.75 StartZ=0 EndX=-5 EndY=119.75 EndZ=0
    g6: Circle CenterX=-79 CenterY=119.75 CenterZ=0 NormalX=0 NormalY=0 NormalZ=1 AngleXU=0 Radius=1.3
    g7: Circle CenterX=-5 CenterY=119.75 CenterZ=0 NormalX=0 NormalY=0 NormalZ=1 AngleXU=0 Radius=1.3
  constraints (20):
    c: Distance(g0) = 10
    c: Coincident(g0,g-4)
    c: Vertical(g0)
    c: Distance(g1) = 10
    c: Coincident(g1,g-3)
    c: Vertical(g1)
    c: Diameter(g2) = 2.6
    c: Coincident(g2,g0)
    c: Diameter(g3) = 2.6
    c: Coincident(g3,g1)
    c: Distance(g4) = 74
    c: Coincident(g4,g0)
    c: Vertical(g4)
    c: Coincident(g5,g1)
    c: Vertical(g5)
    c: Equal(g5,g4)
    c: Diameter(g6) = 2.6
    c: Coincident(g6,g4)
    c: Diameter(g7) = 2.6
    c: Coincident(g7,g5)
FEATURE [PartDesign::Pocket] Pocket048
  BaseFeature = -> Pocket047
  Direction = (0,-1,2e-16)
  Length = 5
  Length2 = 5
  Placement = pos=(-3.2e-15,0,0) rot=(0,-1,0;1.5708rad)
  Profile = -> Sketch092
  ReferenceAxis = -> Sketch092 [N_Axis]
  Refine = true
  Suppressed = false
  Type = 0
FEATURE [PartDesign::Chamfer] Chamfer025
  Angle = 45
  Base = -> Pocket048 [Edge62]
  BaseFeature = -> Pocket048
  ChamferType = 0
  FlipDirection = false
  Placement = pos=(-3.2e-15,0,0) rot=(0,-1,0;1.5708rad)
  Refine = true
  Size = 1
  Size2 = 1
  SupportTransform = false
  Suppressed = false
  UseAllEdges = false
FEATURE [PartDesign::Chamfer] Chamfer026
  Angle = 45
  Base = -> Chamfer025 [Edge32]
  BaseFeature = -> Chamfer025
  ChamferType = 0
  FlipDirection = false
  Placement = pos=(-3.2e-15,0,0) rot=(0,-1,0;1.5708rad)
  Refine = true
  Size = 4
  Size2 = 1
  SupportTransform = false
  Suppressed = false
  UseAllEdges = false
FEATURE [Sketcher::SketchObject] Sketch093
  ArcFitTolerance = 1e-06
  AttachmentSupport = -> [Pad032]
  ExternalGeometry = -> [Pad032]
  FullyConstrained = true
  MakeInternals = false
  MapMode = 5
  Placement = pos=(-3.2e-15,1e-16,0) rot=(0,-1,0;1.5708rad)
  sketch-geometry (4):
    g0: LineSegment [constr] StartX=-43.25 StartY=40 StartZ=0 EndX=-22.25 EndY=40 EndZ=0
    g1: LineSegment StartX=-22.25 StartY=40 StartZ=0 EndX=-22.25 EndY=34 EndZ=0
    g2: LineSegment StartX=-22.25 StartY=34 StartZ=0 EndX=-28.25 EndY=40 EndZ=0
    g3: LineSegment StartX=-28.25 StartY=40 StartZ=0 EndX=-22.25 EndY=40 EndZ=0
  constraints (10):
    c: Distance(g0) = 21
    c: Coincident(g0,g-4)
    c: Horizontal(g0)
    c: Coincident(g1,g0)
    c: PointOnObject(g1,g-3)
    c: Perpendicular(g0,g1)
    c: Coincident(g2,g1)
    c: Coincident(g2,g-4)
    c: Coincident(g3,g2)
    c: Coincident(g3,g0)
FEATURE [PartDesign::Pocket] Pocket049
  BaseFeature = -> Pad032
  Direction = (1,0,-2e-16)
  Length = 5
  Length2 = 5
  Placement = pos=(0,1e-16,0) rot=(0,0.707107,0.707107;3.14159rad)
  Profile = -> Sketch093
  ReferenceAxis = -> Sketch093 [N_Axis]
  Refine = true
  Suppressed = false
  Type = 1
FEATURE [PartDesign::Chamfer] Chamfer027
  Angle = 45
  Base = -> Pocket049 [Edge103]
  BaseFeature = -> Pocket049
  ChamferType = 0
  FlipDirection = false
  Placement = pos=(0,1e-16,0) rot=(0,0.707107,0.707107;3.14159rad)
  Refine = true
  Size = 5
  Size2 = 1
  SupportTransform = false
  Suppressed = false
  UseAllEdges = false
FEATURE [PartDesign::Body] Body011  label="Bolt On Z Adaptor"
  AllowCompound = false
  Group = -> [DatumPlane012,CopyPocket030,Sketch067,Pad026,Sketch068,Pocket038,Pad027,Sketch069,Pad028,Sketch070,Pad029,Sketch071,Pad030,Sketch072,Pocket039,Chamfer017,Chamfer018,Sketch074,Pocket041,Chamfer019,Sketch075,Pad031,Sketch076,Pad032,Sketch093,Pocket049,Chamfer027]
  Origin = -> Origin011
  Tip = -> Chamfer027
FEATURE [Sketcher::SketchObject] Sketch094
  ArcFitTolerance = 1e-06
  AttachmentSupport = -> [LinearPattern]
  ExternalGeometry = -> [LinearPattern]
  FullyConstrained = true
  MakeInternals = false
  MapMode = 5
  Placement = pos=(9.77984e-08,-84,34.8536) rot=(0,1,0;3.14159rad)
  sketch-geometry (6):
    g0: LineSegment [constr] StartX=-72 StartY=77 StartZ=0 EndX=-72 EndY=67 EndZ=0
    g1: LineSegment [constr] StartX=-12 StartY=77 StartZ=0 EndX=-12 EndY=67 EndZ=0
    g2: GeomPoint [constr] X=-72 Y=72 Z=0
    g3: GeomPoint [constr] X=-12 Y=72 Z=0
    g4: Circle CenterX=-72 CenterY=72 CenterZ=0 NormalX=0 NormalY=0 NormalZ=1 AngleXU=0 Radius=1.3
    g5: Circle CenterX=-12 CenterY=72 CenterZ=0 NormalX=0 NormalY=0 NormalZ=1 AngleXU=0 Radius=1.3
  constraints (10):
    c: Coincident(g0,g-3)
    c: Coincident(g0,g-4)
    c: Coincident(g1,g-6)
    c: Coincident(g1,g-5)
    c: Symmetric(g0,g0,g2)
    c: Symmetric(g1,g1,g3)
    c: Diameter(g4) = 2.6
    c: Coincident(g4,g2)
    c: Diameter(g5) = 2.6
    c: Coincident(g5,g3)
FEATURE [PartDesign::Pocket] Pocket050
  BaseFeature = -> LinearPattern
  Direction = (2.80598e-09,0,1)
  Length = 5
  Length2 = 5
  Placement = pos=(9.77984e-08,-84,34.8536) rot=(0,0,1;3.14159rad)
  Profile = -> Sketch094
  ReferenceAxis = -> Sketch094 [N_Axis]
  Refine = true
  Suppressed = false
  Type = 0
FEATURE [Sketcher::SketchObject] Sketch095
  ArcFitTolerance = 1e-06
  AttachmentSupport = -> [Pocket050]
  ExternalGeometry = -> [Pocket050]
  FullyConstrained = true
  MakeInternals = false
  MapMode = 5
  Placement = pos=(9.77984e-08,-84,34.8536) rot=(0,1,0;3.14159rad)
  sketch-geometry (6):
    g0: LineSegment [constr] StartX=-72 StartY=77 StartZ=0 EndX=-67 EndY=77 EndZ=0
    g1: LineSegment [constr] StartX=-67 StartY=77 StartZ=0 EndX=-67 EndY=72 EndZ=0
    g2: LineSegment [constr] StartX=-67 StartY=72 StartZ=0 EndX=-67 EndY=67 EndZ=0
    g3: Circle CenterX=-67 CenterY=77 CenterZ=0 NormalX=0 NormalY=0 NormalZ=1 AngleXU=0 Radius=1.3
    g4: Circle CenterX=-67 CenterY=72 CenterZ=0 NormalX=0 NormalY=0 NormalZ=1 AngleXU=0 Radius=1.3
    g5: Circle CenterX=-67 CenterY=67 CenterZ=0 NormalX=0 NormalY=0 NormalZ=1 AngleXU=0 Radius=1.3
  constraints (15):
    c: Distance(g0) = 5
    c: Coincident(g0,g-3)
    c: Horizontal(g0)
    c: Distance(g1) = 5
    c: Coincident(g1,g0)
    c: Perpendicular(g0,g1)
    c: Distance(g2) = 5
    c: Coincident(g2,g1)
    c: Vertical(g2)
    c: Diameter(g3) = 2.6
    c: Coincident(g3,g0)
    c: Diameter(g4) = 2.6
    c: Coincident(g4,g1)
    c: Diameter(g5) = 2.6
    c: Coincident(g5,g2)
FEATURE [PartDesign::Pocket] Pocket051
  BaseFeature = -> Pocket050
  Direction = (2.80598e-09,0,1)
  Length = 5
  Length2 = 5
  Placement = pos=(9.77984e-08,-84,34.8536) rot=(0,0,1;3.14159rad)
  Profile = -> Sketch095
  ReferenceAxis = -> Sketch095 [N_Axis]
  Refine = true
  Suppressed = false
  Type = 0
FEATURE [PartDesign::LinearPattern] LinearPattern001
  BaseFeature = -> Pocket051
  Direction = -> Sketch095 [H_Axis]
  Length = 50
  Mode = 0
  Occurrences = 11
  Offset = 5
  Originals = -> [Pocket051]
  Placement = pos=(9.77984e-08,-84,34.8536) rot=(0,0,1;3.14159rad)
  Refine = true
  Suppressed = false
  TransformMode = 0
FEATURE [PartDesign::Pocket] Pocket052
  BaseFeature = -> LinearPattern001
  Direction = (2.80598e-09,0,1)
  Length = 5
  Length2 = 5
  Placement = pos=(9.77984e-08,-84,34.8536) rot=(0,0,1;3.14159rad)
  Profile = -> LinearPattern001 [Face110]
  Refine = true
  Suppressed = false
  Type = 1
FEATURE [PartDesign::Pocket] Pocket053
  BaseFeature = -> Pocket052
  Direction = (2.80598e-09,0,1)
  Length = 5
  Length2 = 5
  Placement = pos=(9.77984e-08,-84,34.8536) rot=(0,0,1;3.14159rad)
  Profile = -> Pocket052 [Face150,Face131]
  Refine = true
  Suppressed = false
  Type = 1
FEATURE [PartDesign::Chamfer] Chamfer028
  Angle = 45
  Base = -> Pocket053 [Edge219,Edge222]
  BaseFeature = -> Pocket053
  ChamferType = 0
  FlipDirection = false
  Placement = pos=(9.77984e-08,-84,34.8536) rot=(0,0,1;3.14159rad)
  Refine = true
  Size = 4
  Size2 = 1
  SupportTransform = false
  Suppressed = false
  UseAllEdges = false
FEATURE [PartDesign::Chamfer] Chamfer029
  Angle = 45
  Base = -> Chamfer028 [Edge130,Edge156]
  BaseFeature = -> Chamfer028
  ChamferType = 0
  FlipDirection = false
  Placement = pos=(9.77984e-08,-84,34.8536) rot=(0,0,1;3.14159rad)
  Refine = true
  Size = 2
  Size2 = 1
  SupportTransform = false
  Suppressed = false
  UseAllEdges = false
FEATURE [PartDesign::Body] Body012  label="90 Deg Plate to Plate"
  AllowCompound = false
  Group = -> [DatumPlane013,CopyPocket012,Sketch077,Pad033,Sketch078,Pad034,Sketch079,Pocket042,Pad035,Sketch080,Pocket043,LinearPattern,Sketch094,Pocket050,Sketch095,Pocket051,LinearPattern001,Pocket052,Pocket053,Chamfer028,Chamfer029]
  Origin = -> Origin012
  Tip = -> Chamfer029
FEATURE [PartDesign::Pad] Pad045
  BaseFeature = -> Chamfer026
  Direction = (0,1,-4e-16)
  Length = 1
  Length2 = 10
  Placement = pos=(-3.2e-15,0,0) rot=(0,-1,0;1.5708rad)
  Profile = -> Chamfer026 [Face7]
  Refine = true
  Suppressed = false
  Type = 0
FEATURE [PartDesign::Body] Body014  label="Support Base Extension"
  AllowCompound = false
  Group = -> [DatumPlane015,CopyPad032,Sketch088,Pad043,Sketch089,Pocket045,Sketch090,Pad044,Sketch091,Pocket046,Pocket047,DatumPlane016,CopyPad033,Sketch092,Pocket048,Chamfer025,Chamfer026,Pad045]
  Origin = -> Origin014
  Tip = -> Pad045
